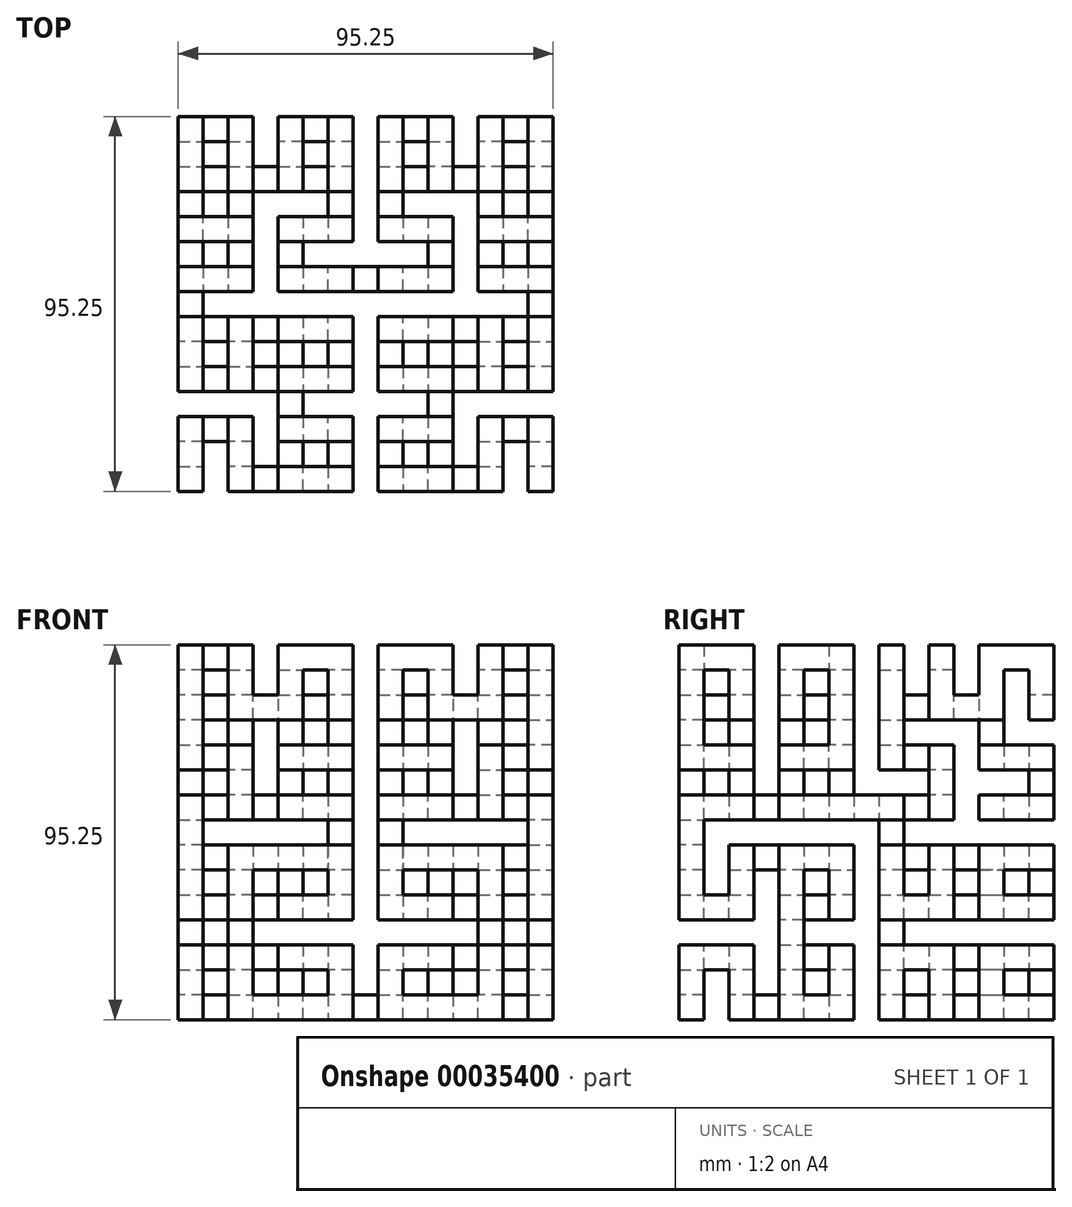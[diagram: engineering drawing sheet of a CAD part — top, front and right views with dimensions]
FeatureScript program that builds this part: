
annotation { "Feature Type Name" : "Feature", "Feature Type Description" : "" }
export const myFeature = defineFeature(function(context is Context, id is Id, definition is map)
    precondition{}
    {
        {
            var Q0;
            Q0=qCreatedBy(makeId("Top.planeOp"),FACE);
            var sketch = newSketch(context, id + "F0", { "sketchPlane" : qUnion([Q0])});
            skLineSegment(sketch, "E0.bottom", {"start": v(-71.04, -70.84) * mm, "end": v(-64.7, -70.84) * mm});
            skLineSegment(sketch, "E0.top", {"start": v(-71.04, -64.49) * mm, "end": v(-64.7, -64.49) * mm});
            skLineSegment(sketch, "E0.left", {"start": v(-71.04, -70.84) * mm, "end": v(-71.04, -64.49) * mm});
            skLineSegment(sketch, "E0.right", {"start": v(-64.7, -70.84) * mm, "end": v(-64.7, -64.49) * mm});
            skSolve(sketch);
        }
        {
            var Q0;
            Q0=makeQuery(id+"F0.imprint","IMPRINT",FACE,{"disambiguationData":[TD([[makeQuery(id+"F0.imprint","IMPRINT",EDGE,{"derivedFrom":sQuery(id+"F0.wireOp",EDGE,"E0.bottom")}),1.0]])]});
            extrude(context, id + "F1", {"entities" : qUnion([Q0]), "depth" : 19.05 * mm});
        }
        {
            var Q0;
            Q0=makeQuery(id+"F1.opExtrude","SWEPT_FACE",FACE,{"disambiguationData":[OSD([sQuery(id+"F0.wireOp",EDGE,"E0.bottom")])]});
            var sketch = newSketch(context, id + "F2", { "sketchPlane" : qUnion([Q0])});
            skLineSegment(sketch, "E1.bottom", {"start": v(-64.7, 19.05) * mm, "end": v(-71.04, 19.05) * mm});
            skLineSegment(sketch, "E1.top", {"start": v(-64.7, 12.7) * mm, "end": v(-71.04, 12.7) * mm});
            skLineSegment(sketch, "E1.left", {"start": v(-64.7, 19.05) * mm, "end": v(-64.7, 12.7) * mm});
            skLineSegment(sketch, "E1.right", {"start": v(-71.04, 19.05) * mm, "end": v(-71.04, 12.7) * mm});
            skSolve(sketch);
        }
        {
            var Q0;
            Q0=makeQuery(id+"F2.imprint","IMPRINT",FACE,{"disambiguationData":[TD([[makeQuery(id+"F2.imprint","IMPRINT",EDGE,{"derivedFrom":sQuery(id+"F2.wireOp",EDGE,"E1.bottom")}),-1.0]])]});
            extrude(context, id + "F3", {"entities" : qUnion([Q0]), "operationType" : NewBodyOperationType.ADD, "oppositeDirection" : true, "depth" : 19.05 * mm});
        }
        {
            var Q0;
            Q0=makeQuery(id+"F3.boolean.opBoolean","MERGE",FACE,{"derivedFrom":[makeQuery(id+"F1.opExtrude","CAP_FACE",FACE,{"disambiguationData":[OSD([sQuery(id+"F0.wireOp",EDGE,"E0.bottom"),sQuery(id+"F0.wireOp",EDGE,"E0.top"),sQuery(id+"F0.wireOp",EDGE,"E0.left"),sQuery(id+"F0.wireOp",EDGE,"E0.right")])],"isStart":false}),makeQuery(id+"F3.opExtrude","SWEPT_FACE",FACE,{"disambiguationData":[OSD([sQuery(id+"F2.wireOp",EDGE,"E1.bottom")])]})]});
            var sketch = newSketch(context, id + "F4", { "sketchPlane" : qUnion([Q0])});
            skLineSegment(sketch, "E2.bottom", {"start": v(-64.7, -51.79) * mm, "end": v(-71.04, -51.79) * mm});
            skLineSegment(sketch, "E2.top", {"start": v(-64.7, -58.14) * mm, "end": v(-71.04, -58.14) * mm});
            skLineSegment(sketch, "E2.left", {"start": v(-64.7, -51.79) * mm, "end": v(-64.7, -58.14) * mm});
            skLineSegment(sketch, "E2.right", {"start": v(-71.04, -51.79) * mm, "end": v(-71.04, -58.14) * mm});
            skSolve(sketch);
        }
        {
            var Q0;
            Q0=makeQuery(id+"F4.imprint","IMPRINT",FACE,{"disambiguationData":[TD([[makeQuery(id+"F4.imprint","IMPRINT",EDGE,{"derivedFrom":sQuery(id+"F4.wireOp",EDGE,"E2.bottom")}),-1.0]])]});
            extrude(context, id + "F5", {"entities" : qUnion([Q0]), "operationType" : NewBodyOperationType.ADD, "oppositeDirection" : true, "depth" : 19.05 * mm});
        }
        {
            var Q0;
            Q0=makeQuery(id+"F5.boolean.opBoolean","MERGE",FACE,{"derivedFrom":[makeQuery(id+"F3.boolean.opBoolean","MERGE",FACE,{"derivedFrom":[makeQuery(id+"F1.opExtrude","SWEPT_FACE",FACE,{"disambiguationData":[OSD([sQuery(id+"F0.wireOp",EDGE,"E0.left")])]}),makeQuery(id+"F3.opExtrude","SWEPT_FACE",FACE,{"disambiguationData":[OSD([sQuery(id+"F2.wireOp",EDGE,"E1.right")])]})]}),makeQuery(id+"F5.opExtrude","SWEPT_FACE",FACE,{"disambiguationData":[OSD([sQuery(id+"F4.wireOp",EDGE,"E2.right")])]})]});
            var sketch = newSketch(context, id + "F6", { "sketchPlane" : qUnion([Q0])});
            skLineSegment(sketch, "E3.bottom", {"start": v(51.79, 0) * mm, "end": v(58.14, 0) * mm});
            skLineSegment(sketch, "E3.top", {"start": v(51.79, 6.35) * mm, "end": v(58.14, 6.35) * mm});
            skLineSegment(sketch, "E3.left", {"start": v(51.79, 0) * mm, "end": v(51.79, 6.35) * mm});
            skLineSegment(sketch, "E3.right", {"start": v(58.14, 0) * mm, "end": v(58.14, 6.35) * mm});
            skSolve(sketch);
        }
        {
            var Q0;
            Q0=makeQuery(id+"F6.imprint","IMPRINT",FACE,{"disambiguationData":[TD([[makeQuery(id+"F6.imprint","IMPRINT",EDGE,{"derivedFrom":sQuery(id+"F6.wireOp",EDGE,"E3.bottom")}),-1.0]])]});
            extrude(context, id + "F7", {"entities" : qUnion([Q0]), "operationType" : NewBodyOperationType.ADD, "oppositeDirection" : true, "depth" : 19.05 * mm});
        }
        {
            var Q0;
            Q0=makeQuery(id+"F7.boolean.opBoolean","MERGE",FACE,{"derivedFrom":[makeQuery(id+"F5.opExtrude","CAP_FACE",FACE,{"disambiguationData":[OSD([sQuery(id+"F4.wireOp",EDGE,"E2.bottom"),sQuery(id+"F4.wireOp",EDGE,"E2.top"),sQuery(id+"F4.wireOp",EDGE,"E2.left"),sQuery(id+"F4.wireOp",EDGE,"E2.right")])],"isStart":false}),makeQuery(id+"F7.opExtrude","SWEPT_FACE",FACE,{"disambiguationData":[OSD([sQuery(id+"F6.wireOp",EDGE,"E3.bottom")])]})]});
            var sketch = newSketch(context, id + "F8", { "sketchPlane" : qUnion([Q0])});
            skLineSegment(sketch, "E4.bottom", {"start": v(-52, 58.14) * mm, "end": v(-58.34, 58.14) * mm});
            skLineSegment(sketch, "E4.top", {"start": v(-52, 51.79) * mm, "end": v(-58.34, 51.79) * mm});
            skLineSegment(sketch, "E4.left", {"start": v(-52, 58.14) * mm, "end": v(-52, 51.79) * mm});
            skLineSegment(sketch, "E4.right", {"start": v(-58.34, 58.14) * mm, "end": v(-58.34, 51.79) * mm});
            skSolve(sketch);
        }
        {
            var Q0;
            Q0=makeQuery(id+"F8.imprint","IMPRINT",FACE,{"disambiguationData":[TD([[makeQuery(id+"F8.imprint","IMPRINT",EDGE,{"derivedFrom":sQuery(id+"F8.wireOp",EDGE,"E4.bottom")}),1.0]])]});
            extrude(context, id + "F9", {"entities" : qUnion([Q0]), "operationType" : NewBodyOperationType.ADD, "oppositeDirection" : true, "depth" : 19.05 * mm});
        }
        {
            var Q0;
            Q0=makeQuery(id+"F9.boolean.opBoolean","MERGE",FACE,{"derivedFrom":[makeQuery(id+"F7.boolean.opBoolean","MERGE",FACE,{"derivedFrom":[makeQuery(id+"F5.boolean.opBoolean","MERGE",FACE,{"derivedFrom":[makeQuery(id+"F3.opExtrude","CAP_FACE",FACE,{"disambiguationData":[OSD([sQuery(id+"F2.wireOp",EDGE,"E1.bottom"),sQuery(id+"F2.wireOp",EDGE,"E1.top"),sQuery(id+"F2.wireOp",EDGE,"E1.left"),sQuery(id+"F2.wireOp",EDGE,"E1.right")])],"isStart":false}),makeQuery(id+"F5.opExtrude","SWEPT_FACE",FACE,{"disambiguationData":[OSD([sQuery(id+"F4.wireOp",EDGE,"E2.bottom")])]})]}),makeQuery(id+"F7.opExtrude","SWEPT_FACE",FACE,{"disambiguationData":[OSD([sQuery(id+"F6.wireOp",EDGE,"E3.left")])]})]}),makeQuery(id+"F9.opExtrude","SWEPT_FACE",FACE,{"disambiguationData":[OSD([sQuery(id+"F8.wireOp",EDGE,"E4.top")])]})]});
            var sketch = newSketch(context, id + "F10", { "sketchPlane" : qUnion([Q0])});
            skLineSegment(sketch, "E5.bottom", {"start": v(52, 19.05) * mm, "end": v(58.34, 19.05) * mm});
            skLineSegment(sketch, "E5.top", {"start": v(52, 12.7) * mm, "end": v(58.34, 12.7) * mm});
            skLineSegment(sketch, "E5.left", {"start": v(52, 19.05) * mm, "end": v(52, 12.7) * mm});
            skLineSegment(sketch, "E5.right", {"start": v(58.34, 19.05) * mm, "end": v(58.34, 12.7) * mm});
            skSolve(sketch);
        }
        {
            var Q0;
            Q0=makeQuery(id+"F10.imprint","IMPRINT",FACE,{"disambiguationData":[TD([[makeQuery(id+"F10.imprint","IMPRINT",EDGE,{"derivedFrom":sQuery(id+"F10.wireOp",EDGE,"E5.bottom")}),1.0]])]});
            extrude(context, id + "F11", {"entities" : qUnion([Q0]), "operationType" : NewBodyOperationType.ADD, "oppositeDirection" : true, "depth" : 19.05 * mm});
        }
        {
            var Q0;
            Q0=makeQuery(id+"F11.boolean.opBoolean","MERGE",FACE,{"derivedFrom":[makeQuery(id+"F9.opExtrude","CAP_FACE",FACE,{"disambiguationData":[OSD([sQuery(id+"F8.wireOp",EDGE,"E4.bottom"),sQuery(id+"F8.wireOp",EDGE,"E4.top"),sQuery(id+"F8.wireOp",EDGE,"E4.left"),sQuery(id+"F8.wireOp",EDGE,"E4.right")])],"isStart":false}),makeQuery(id+"F11.opExtrude","SWEPT_FACE",FACE,{"disambiguationData":[OSD([sQuery(id+"F10.wireOp",EDGE,"E5.bottom")])]})]});
            var sketch = newSketch(context, id + "F12", { "sketchPlane" : qUnion([Q0])});
            skLineSegment(sketch, "E6.bottom", {"start": v(-52, -70.84) * mm, "end": v(-58.34, -70.84) * mm});
            skLineSegment(sketch, "E6.top", {"start": v(-52, -64.49) * mm, "end": v(-58.34, -64.49) * mm});
            skLineSegment(sketch, "E6.left", {"start": v(-52, -70.84) * mm, "end": v(-52, -64.49) * mm});
            skLineSegment(sketch, "E6.right", {"start": v(-58.34, -70.84) * mm, "end": v(-58.34, -64.49) * mm});
            skSolve(sketch);
        }
        {
            var Q0;
            Q0=makeQuery(id+"F12.imprint","IMPRINT",FACE,{"disambiguationData":[TD([[makeQuery(id+"F12.imprint","IMPRINT",EDGE,{"derivedFrom":sQuery(id+"F12.wireOp",EDGE,"E6.bottom")}),1.0]])]});
            extrude(context, id + "F13", {"entities" : qUnion([Q0]), "operationType" : NewBodyOperationType.ADD, "oppositeDirection" : true, "depth" : 19.05 * mm});
        }
        {
            var Q0;
            Q0=makeQuery(id+"F13.boolean.opBoolean","MERGE",FACE,{"derivedFrom":[makeQuery(id+"F11.boolean.opBoolean","MERGE",FACE,{"derivedFrom":[makeQuery(id+"F9.opExtrude","SWEPT_FACE",FACE,{"disambiguationData":[OSD([sQuery(id+"F8.wireOp",EDGE,"E4.right")])]}),makeQuery(id+"F11.opExtrude","SWEPT_FACE",FACE,{"disambiguationData":[OSD([sQuery(id+"F10.wireOp",EDGE,"E5.right")])]})]}),makeQuery(id+"F13.opExtrude","SWEPT_FACE",FACE,{"disambiguationData":[OSD([sQuery(id+"F12.wireOp",EDGE,"E6.right")])]})]});
            var sketch = newSketch(context, id + "F14", { "sketchPlane" : qUnion([Q0])});
            skLineSegment(sketch, "E7.bottom", {"start": v(70.84, 0) * mm, "end": v(64.49, 0) * mm});
            skLineSegment(sketch, "E7.top", {"start": v(70.84, 6.35) * mm, "end": v(64.49, 6.35) * mm});
            skLineSegment(sketch, "E7.left", {"start": v(70.84, 0) * mm, "end": v(70.84, 6.35) * mm});
            skLineSegment(sketch, "E7.right", {"start": v(64.49, 0) * mm, "end": v(64.49, 6.35) * mm});
            skSolve(sketch);
        }
        {
            var Q0;
            Q0=makeQuery(id+"F14.imprint","IMPRINT",FACE,{"disambiguationData":[TD([[makeQuery(id+"F14.imprint","IMPRINT",EDGE,{"derivedFrom":sQuery(id+"F14.wireOp",EDGE,"E7.bottom")}),-1.0]])]});
            extrude(context, id + "F15", {"entities" : qUnion([Q0]), "operationType" : NewBodyOperationType.ADD, "oppositeDirection" : true, "depth" : 31.75 * mm});
        }
        {
            var Q0;
            Q0=makeQuery(id+"F15.boolean.opBoolean","MERGE",FACE,{"derivedFrom":[makeQuery(id+"F13.opExtrude","CAP_FACE",FACE,{"disambiguationData":[OSD([sQuery(id+"F12.wireOp",EDGE,"E6.bottom"),sQuery(id+"F12.wireOp",EDGE,"E6.top"),sQuery(id+"F12.wireOp",EDGE,"E6.left"),sQuery(id+"F12.wireOp",EDGE,"E6.right")])],"isStart":false}),makeQuery(id+"F15.opExtrude","SWEPT_FACE",FACE,{"disambiguationData":[OSD([sQuery(id+"F14.wireOp",EDGE,"E7.bottom")])]})]});
            var sketch = newSketch(context, id + "F16", { "sketchPlane" : qUnion([Q0])});
            skLineSegment(sketch, "E8.bottom", {"start": v(-26.6, 70.84) * mm, "end": v(-32.94, 70.84) * mm});
            skLineSegment(sketch, "E8.top", {"start": v(-26.6, 64.49) * mm, "end": v(-32.94, 64.49) * mm});
            skLineSegment(sketch, "E8.left", {"start": v(-26.6, 70.84) * mm, "end": v(-26.6, 64.49) * mm});
            skLineSegment(sketch, "E8.right", {"start": v(-32.94, 70.84) * mm, "end": v(-32.94, 64.49) * mm});
            skSolve(sketch);
        }
        {
            var Q0;
            Q0=makeQuery(id+"F16.imprint","IMPRINT",FACE,{"disambiguationData":[TD([[makeQuery(id+"F16.imprint","IMPRINT",EDGE,{"derivedFrom":sQuery(id+"F16.wireOp",EDGE,"E8.bottom")}),-1.0]])]});
            extrude(context, id + "F17", {"entities" : qUnion([Q0]), "operationType" : NewBodyOperationType.ADD, "oppositeDirection" : true, "depth" : 19.05 * mm});
        }
        {
            var Q0;
            Q0=makeQuery(id+"F17.boolean.opBoolean","MERGE",FACE,{"derivedFrom":[makeQuery(id+"F15.opExtrude","CAP_FACE",FACE,{"disambiguationData":[OSD([sQuery(id+"F14.wireOp",EDGE,"E7.bottom"),sQuery(id+"F14.wireOp",EDGE,"E7.top"),sQuery(id+"F14.wireOp",EDGE,"E7.left"),sQuery(id+"F14.wireOp",EDGE,"E7.right")])],"isStart":false}),makeQuery(id+"F17.opExtrude","SWEPT_FACE",FACE,{"disambiguationData":[OSD([sQuery(id+"F16.wireOp",EDGE,"E8.left")])]})]});
            var sketch = newSketch(context, id + "F18", { "sketchPlane" : qUnion([Q0])});
            skLineSegment(sketch, "E9.bottom", {"start": v(-64.49, 19.05) * mm, "end": v(-70.84, 19.05) * mm});
            skLineSegment(sketch, "E9.top", {"start": v(-64.49, 12.7) * mm, "end": v(-70.84, 12.7) * mm});
            skLineSegment(sketch, "E9.left", {"start": v(-64.49, 19.05) * mm, "end": v(-64.49, 12.7) * mm});
            skLineSegment(sketch, "E9.right", {"start": v(-70.84, 19.05) * mm, "end": v(-70.84, 12.7) * mm});
            skSolve(sketch);
        }
        {
            var Q0;
            Q0=makeQuery(id+"F18.imprint","IMPRINT",FACE,{"disambiguationData":[TD([[makeQuery(id+"F18.imprint","IMPRINT",EDGE,{"derivedFrom":sQuery(id+"F18.wireOp",EDGE,"E9.bottom")}),-1.0]])]});
            extrude(context, id + "F19", {"entities" : qUnion([Q0]), "operationType" : NewBodyOperationType.ADD, "oppositeDirection" : true, "depth" : 19.05 * mm});
        }
        {
            var Q0;
            Q0=makeQuery(id+"F19.boolean.opBoolean","MERGE",FACE,{"derivedFrom":[makeQuery(id+"F17.boolean.opBoolean","MERGE",FACE,{"derivedFrom":[makeQuery(id+"F15.boolean.opBoolean","MERGE",FACE,{"derivedFrom":[makeQuery(id+"F13.boolean.opBoolean","MERGE",FACE,{"derivedFrom":[makeQuery(id+"F11.opExtrude","CAP_FACE",FACE,{"disambiguationData":[OSD([sQuery(id+"F10.wireOp",EDGE,"E5.bottom"),sQuery(id+"F10.wireOp",EDGE,"E5.top"),sQuery(id+"F10.wireOp",EDGE,"E5.left"),sQuery(id+"F10.wireOp",EDGE,"E5.right")])],"isStart":false}),makeQuery(id+"F13.opExtrude","SWEPT_FACE",FACE,{"disambiguationData":[OSD([sQuery(id+"F12.wireOp",EDGE,"E6.bottom")])]})]}),makeQuery(id+"F15.opExtrude","SWEPT_FACE",FACE,{"disambiguationData":[OSD([sQuery(id+"F14.wireOp",EDGE,"E7.left")])]})]}),makeQuery(id+"F17.opExtrude","SWEPT_FACE",FACE,{"disambiguationData":[OSD([sQuery(id+"F16.wireOp",EDGE,"E8.bottom")])]})]}),makeQuery(id+"F19.opExtrude","SWEPT_FACE",FACE,{"disambiguationData":[OSD([sQuery(id+"F18.wireOp",EDGE,"E9.right")])]})]});
            var sketch = newSketch(context, id + "F20", { "sketchPlane" : qUnion([Q0])});
            skLineSegment(sketch, "E10.bottom", {"start": v(-45.64, 19.05) * mm, "end": v(-39.3, 19.05) * mm});
            skLineSegment(sketch, "E10.top", {"start": v(-45.64, 12.7) * mm, "end": v(-39.3, 12.7) * mm});
            skLineSegment(sketch, "E10.left", {"start": v(-45.64, 19.05) * mm, "end": v(-45.64, 12.7) * mm});
            skLineSegment(sketch, "E10.right", {"start": v(-39.3, 19.05) * mm, "end": v(-39.3, 12.7) * mm});
            skSolve(sketch);
        }
        {
            var Q0;
            Q0=makeQuery(id+"F20.imprint","IMPRINT",FACE,{"disambiguationData":[TD([[makeQuery(id+"F20.imprint","IMPRINT",EDGE,{"derivedFrom":sQuery(id+"F20.wireOp",EDGE,"E10.bottom")}),-1.0]])]});
            extrude(context, id + "F21", {"entities" : qUnion([Q0]), "operationType" : NewBodyOperationType.ADD, "oppositeDirection" : true, "depth" : 19.05 * mm});
        }
        {
            var Q0;
            Q0=makeQuery(id+"F21.boolean.opBoolean","MERGE",FACE,{"derivedFrom":[makeQuery(id+"F19.opExtrude","CAP_FACE",FACE,{"disambiguationData":[OSD([sQuery(id+"F18.wireOp",EDGE,"E9.bottom"),sQuery(id+"F18.wireOp",EDGE,"E9.top"),sQuery(id+"F18.wireOp",EDGE,"E9.left"),sQuery(id+"F18.wireOp",EDGE,"E9.right")])],"isStart":false}),makeQuery(id+"F21.opExtrude","SWEPT_FACE",FACE,{"disambiguationData":[OSD([sQuery(id+"F20.wireOp",EDGE,"E10.left")])]})]});
            var sketch = newSketch(context, id + "F22", { "sketchPlane" : qUnion([Q0])});
            skLineSegment(sketch, "E11.bottom", {"start": v(51.79, 19.05) * mm, "end": v(58.14, 19.05) * mm});
            skLineSegment(sketch, "E11.top", {"start": v(51.79, 12.7) * mm, "end": v(58.14, 12.7) * mm});
            skLineSegment(sketch, "E11.left", {"start": v(51.79, 19.05) * mm, "end": v(51.79, 12.7) * mm});
            skLineSegment(sketch, "E11.right", {"start": v(58.14, 19.05) * mm, "end": v(58.14, 12.7) * mm});
            skSolve(sketch);
        }
        {
            var Q0;
            Q0=makeQuery(id+"F22.imprint","IMPRINT",FACE,{"disambiguationData":[TD([[makeQuery(id+"F22.imprint","IMPRINT",EDGE,{"derivedFrom":sQuery(id+"F22.wireOp",EDGE,"E11.bottom")}),1.0]])]});
            extrude(context, id + "F23", {"entities" : qUnion([Q0]), "operationType" : NewBodyOperationType.ADD, "oppositeDirection" : true, "depth" : 19.05 * mm});
        }
        {
            var Q0;
            Q0=makeQuery(id+"F23.boolean.opBoolean","MERGE",FACE,{"derivedFrom":[makeQuery(id+"F21.boolean.opBoolean","MERGE",FACE,{"derivedFrom":[makeQuery(id+"F19.boolean.opBoolean","MERGE",FACE,{"derivedFrom":[makeQuery(id+"F17.opExtrude","CAP_FACE",FACE,{"disambiguationData":[OSD([sQuery(id+"F16.wireOp",EDGE,"E8.bottom"),sQuery(id+"F16.wireOp",EDGE,"E8.top"),sQuery(id+"F16.wireOp",EDGE,"E8.left"),sQuery(id+"F16.wireOp",EDGE,"E8.right")])],"isStart":false}),makeQuery(id+"F19.opExtrude","SWEPT_FACE",FACE,{"disambiguationData":[OSD([sQuery(id+"F18.wireOp",EDGE,"E9.bottom")])]})]}),makeQuery(id+"F21.opExtrude","SWEPT_FACE",FACE,{"disambiguationData":[OSD([sQuery(id+"F20.wireOp",EDGE,"E10.bottom")])]})]}),makeQuery(id+"F23.opExtrude","SWEPT_FACE",FACE,{"disambiguationData":[OSD([sQuery(id+"F22.wireOp",EDGE,"E11.bottom")])]})]});
            var sketch = newSketch(context, id + "F24", { "sketchPlane" : qUnion([Q0])});
            skLineSegment(sketch, "E12.bottom", {"start": v(-26.6, -51.79) * mm, "end": v(-32.94, -51.79) * mm});
            skLineSegment(sketch, "E12.top", {"start": v(-26.6, -58.14) * mm, "end": v(-32.94, -58.14) * mm});
            skLineSegment(sketch, "E12.left", {"start": v(-26.6, -51.79) * mm, "end": v(-26.6, -58.14) * mm});
            skLineSegment(sketch, "E12.right", {"start": v(-32.94, -51.79) * mm, "end": v(-32.94, -58.14) * mm});
            skSolve(sketch);
        }
        {
            var Q0;
            Q0=makeQuery(id+"F24.imprint","IMPRINT",FACE,{"disambiguationData":[TD([[makeQuery(id+"F24.imprint","IMPRINT",EDGE,{"derivedFrom":sQuery(id+"F24.wireOp",EDGE,"E12.bottom")}),-1.0]])]});
            extrude(context, id + "F25", {"entities" : qUnion([Q0]), "operationType" : NewBodyOperationType.ADD, "oppositeDirection" : true, "depth" : 19.05 * mm});
        }
        {
            var Q0;
            Q0=makeQuery(id+"F25.boolean.opBoolean","MERGE",FACE,{"derivedFrom":[makeQuery(id+"F23.opExtrude","CAP_FACE",FACE,{"disambiguationData":[OSD([sQuery(id+"F22.wireOp",EDGE,"E11.bottom"),sQuery(id+"F22.wireOp",EDGE,"E11.top"),sQuery(id+"F22.wireOp",EDGE,"E11.left"),sQuery(id+"F22.wireOp",EDGE,"E11.right")])],"isStart":false}),makeQuery(id+"F25.opExtrude","SWEPT_FACE",FACE,{"disambiguationData":[OSD([sQuery(id+"F24.wireOp",EDGE,"E12.left")])]})]});
            var sketch = newSketch(context, id + "F26", { "sketchPlane" : qUnion([Q0])});
            skLineSegment(sketch, "E13.bottom", {"start": v(-51.79, 0) * mm, "end": v(-58.14, 0) * mm});
            skLineSegment(sketch, "E13.top", {"start": v(-51.79, 6.35) * mm, "end": v(-58.14, 6.35) * mm});
            skLineSegment(sketch, "E13.left", {"start": v(-51.79, 0) * mm, "end": v(-51.79, 6.35) * mm});
            skLineSegment(sketch, "E13.right", {"start": v(-58.14, 0) * mm, "end": v(-58.14, 6.35) * mm});
            skSolve(sketch);
        }
        {
            var Q0;
            Q0=makeQuery(id+"F26.imprint","IMPRINT",FACE,{"disambiguationData":[TD([[makeQuery(id+"F26.imprint","IMPRINT",EDGE,{"derivedFrom":sQuery(id+"F26.wireOp",EDGE,"E13.bottom")}),1.0]])]});
            extrude(context, id + "F27", {"entities" : qUnion([Q0]), "operationType" : NewBodyOperationType.ADD, "oppositeDirection" : true, "depth" : 19.05 * mm});
        }
        {
            var Q0;
            Q0=makeQuery(id+"F27.boolean.opBoolean","MERGE",FACE,{"derivedFrom":[makeQuery(id+"F25.boolean.opBoolean","MERGE",FACE,{"derivedFrom":[makeQuery(id+"F23.opExtrude","SWEPT_FACE",FACE,{"disambiguationData":[OSD([sQuery(id+"F22.wireOp",EDGE,"E11.right")])]}),makeQuery(id+"F25.opExtrude","SWEPT_FACE",FACE,{"disambiguationData":[OSD([sQuery(id+"F24.wireOp",EDGE,"E12.top")])]})]}),makeQuery(id+"F27.opExtrude","SWEPT_FACE",FACE,{"disambiguationData":[OSD([sQuery(id+"F26.wireOp",EDGE,"E13.right")])]})]});
            var sketch = newSketch(context, id + "F28", { "sketchPlane" : qUnion([Q0])});
            skLineSegment(sketch, "E14.bottom", {"start": v(-45.64, 0) * mm, "end": v(-39.3, 0) * mm});
            skLineSegment(sketch, "E14.top", {"start": v(-45.64, 6.35) * mm, "end": v(-39.3, 6.35) * mm});
            skLineSegment(sketch, "E14.left", {"start": v(-45.64, 0) * mm, "end": v(-45.64, 6.35) * mm});
            skLineSegment(sketch, "E14.right", {"start": v(-39.3, 0) * mm, "end": v(-39.3, 6.35) * mm});
            skSolve(sketch);
        }
        {
            var Q0;
            Q0=makeQuery(id+"F28.imprint","IMPRINT",FACE,{"disambiguationData":[TD([[makeQuery(id+"F28.imprint","IMPRINT",EDGE,{"derivedFrom":sQuery(id+"F28.wireOp",EDGE,"E14.bottom")}),-1.0]])]});
            extrude(context, id + "F29", {"entities" : qUnion([Q0]), "operationType" : NewBodyOperationType.ADD, "oppositeDirection" : true, "depth" : 19.05 * mm});
        }
        {
            var Q0;
            Q0=makeQuery(id+"F29.boolean.opBoolean","MERGE",FACE,{"derivedFrom":[makeQuery(id+"F27.opExtrude","CAP_FACE",FACE,{"disambiguationData":[OSD([sQuery(id+"F26.wireOp",EDGE,"E13.bottom"),sQuery(id+"F26.wireOp",EDGE,"E13.top"),sQuery(id+"F26.wireOp",EDGE,"E13.left"),sQuery(id+"F26.wireOp",EDGE,"E13.right")])],"isStart":false}),makeQuery(id+"F29.opExtrude","SWEPT_FACE",FACE,{"disambiguationData":[OSD([sQuery(id+"F28.wireOp",EDGE,"E14.left")])]})]});
            var sketch = newSketch(context, id + "F30", { "sketchPlane" : qUnion([Q0])});
            skLineSegment(sketch, "E15.bottom", {"start": v(39.09, 6.35) * mm, "end": v(45.44, 6.35) * mm});
            skLineSegment(sketch, "E15.top", {"start": v(39.09, 0) * mm, "end": v(45.44, 0) * mm});
            skLineSegment(sketch, "E15.left", {"start": v(39.09, 6.35) * mm, "end": v(39.09, 0) * mm});
            skLineSegment(sketch, "E15.right", {"start": v(45.44, 6.35) * mm, "end": v(45.44, 0) * mm});
            skSolve(sketch);
        }
        {
            var Q0;
            Q0=makeQuery(id+"F30.imprint","IMPRINT",FACE,{"disambiguationData":[TD([[makeQuery(id+"F30.imprint","IMPRINT",EDGE,{"derivedFrom":sQuery(id+"F30.wireOp",EDGE,"E15.bottom")}),-1.0]])]});
            extrude(context, id + "F31", {"entities" : qUnion([Q0]), "operationType" : NewBodyOperationType.ADD, "oppositeDirection" : true, "depth" : 19.05 * mm});
        }
        {
            var Q0;
            Q0=makeQuery(id+"F31.opExtrude","SWEPT_FACE",FACE,{"disambiguationData":[OSD([sQuery(id+"F30.wireOp",EDGE,"E15.right")])]});
            var sketch = newSketch(context, id + "F32", { "sketchPlane" : qUnion([Q0])});
            skLineSegment(sketch, "E16.bottom", {"start": v(-26.6, 0) * mm, "end": v(-32.94, 0) * mm});
            skLineSegment(sketch, "E16.top", {"start": v(-26.6, 6.35) * mm, "end": v(-32.94, 6.35) * mm});
            skLineSegment(sketch, "E16.left", {"start": v(-26.6, 0) * mm, "end": v(-26.6, 6.35) * mm});
            skLineSegment(sketch, "E16.right", {"start": v(-32.94, 0) * mm, "end": v(-32.94, 6.35) * mm});
            skSolve(sketch);
        }
        {
            var Q0;
            Q0=makeQuery(id+"F32.imprint","IMPRINT",FACE,{"disambiguationData":[TD([[makeQuery(id+"F32.imprint","IMPRINT",EDGE,{"derivedFrom":sQuery(id+"F32.wireOp",EDGE,"E16.bottom")}),-1.0]])]});
            extrude(context, id + "F33", {"entities" : qUnion([Q0]), "operationType" : NewBodyOperationType.ADD, "oppositeDirection" : true, "depth" : 19.05 * mm});
        }
        {
            var Q0;
            Q0=makeQuery(id+"F33.boolean.opBoolean","MERGE",FACE,{"derivedFrom":[makeQuery(id+"F31.opExtrude","CAP_FACE",FACE,{"disambiguationData":[OSD([sQuery(id+"F30.wireOp",EDGE,"E15.bottom"),sQuery(id+"F30.wireOp",EDGE,"E15.top"),sQuery(id+"F30.wireOp",EDGE,"E15.left"),sQuery(id+"F30.wireOp",EDGE,"E15.right")])],"isStart":false}),makeQuery(id+"F33.opExtrude","SWEPT_FACE",FACE,{"disambiguationData":[OSD([sQuery(id+"F32.wireOp",EDGE,"E16.left")])]})]});
            var sketch = newSketch(context, id + "F34", { "sketchPlane" : qUnion([Q0])});
            skLineSegment(sketch, "E17.bottom", {"start": v(-26.39, 6.35) * mm, "end": v(-32.74, 6.35) * mm});
            skLineSegment(sketch, "E17.top", {"start": v(-26.39, 0) * mm, "end": v(-32.74, 0) * mm});
            skLineSegment(sketch, "E17.left", {"start": v(-26.39, 6.35) * mm, "end": v(-26.39, 0) * mm});
            skLineSegment(sketch, "E17.right", {"start": v(-32.74, 6.35) * mm, "end": v(-32.74, 0) * mm});
            skSolve(sketch);
        }
        {
            var Q0;
            Q0=makeQuery(id+"F34.imprint","IMPRINT",FACE,{"disambiguationData":[TD([[makeQuery(id+"F34.imprint","IMPRINT",EDGE,{"derivedFrom":sQuery(id+"F34.wireOp",EDGE,"E17.bottom")}),1.0]])]});
            extrude(context, id + "F35", {"entities" : qUnion([Q0]), "operationType" : NewBodyOperationType.ADD, "oppositeDirection" : true, "depth" : 19.05 * mm});
        }
        {
            var Q0;
            Q0=makeQuery(id+"F35.boolean.opBoolean","MERGE",FACE,{"derivedFrom":[makeQuery(id+"F33.boolean.opBoolean","MERGE",FACE,{"derivedFrom":[makeQuery(id+"F31.boolean.opBoolean","MERGE",FACE,{"derivedFrom":[makeQuery(id+"F29.boolean.opBoolean","MERGE",FACE,{"derivedFrom":[makeQuery(id+"F27.boolean.opBoolean","MERGE",FACE,{"derivedFrom":[makeQuery(id+"F25.opExtrude","CAP_FACE",FACE,{"disambiguationData":[OSD([sQuery(id+"F24.wireOp",EDGE,"E12.bottom"),sQuery(id+"F24.wireOp",EDGE,"E12.top"),sQuery(id+"F24.wireOp",EDGE,"E12.left"),sQuery(id+"F24.wireOp",EDGE,"E12.right")])],"isStart":false}),makeQuery(id+"F27.opExtrude","SWEPT_FACE",FACE,{"disambiguationData":[OSD([sQuery(id+"F26.wireOp",EDGE,"E13.bottom")])]})]}),makeQuery(id+"F29.opExtrude","SWEPT_FACE",FACE,{"disambiguationData":[OSD([sQuery(id+"F28.wireOp",EDGE,"E14.bottom")])]})]}),makeQuery(id+"F31.opExtrude","SWEPT_FACE",FACE,{"disambiguationData":[OSD([sQuery(id+"F30.wireOp",EDGE,"E15.top")])]})]}),makeQuery(id+"F33.opExtrude","SWEPT_FACE",FACE,{"disambiguationData":[OSD([sQuery(id+"F32.wireOp",EDGE,"E16.bottom")])]})]}),makeQuery(id+"F35.opExtrude","SWEPT_FACE",FACE,{"disambiguationData":[OSD([sQuery(id+"F34.wireOp",EDGE,"E17.top")])]})]});
            var sketch = newSketch(context, id + "F36", { "sketchPlane" : qUnion([Q0])});
            skLineSegment(sketch, "E18.bottom", {"start": v(-45.64, 26.39) * mm, "end": v(-39.3, 26.39) * mm});
            skLineSegment(sketch, "E18.top", {"start": v(-45.64, 32.74) * mm, "end": v(-39.3, 32.74) * mm});
            skLineSegment(sketch, "E18.left", {"start": v(-45.64, 26.39) * mm, "end": v(-45.64, 32.74) * mm});
            skLineSegment(sketch, "E18.right", {"start": v(-39.3, 26.39) * mm, "end": v(-39.3, 32.74) * mm});
            skSolve(sketch);
        }
        {
            var Q0;
            Q0=makeQuery(id+"F36.imprint","IMPRINT",FACE,{"disambiguationData":[TD([[makeQuery(id+"F36.imprint","IMPRINT",EDGE,{"derivedFrom":sQuery(id+"F36.wireOp",EDGE,"E18.bottom")}),-1.0]])]});
            extrude(context, id + "F37", {"entities" : qUnion([Q0]), "operationType" : NewBodyOperationType.ADD, "oppositeDirection" : true, "depth" : 19.05 * mm});
        }
        {
            var Q0;
            Q0=makeQuery(id+"F37.boolean.opBoolean","MERGE",FACE,{"derivedFrom":[makeQuery(id+"F35.opExtrude","CAP_FACE",FACE,{"disambiguationData":[OSD([sQuery(id+"F34.wireOp",EDGE,"E17.bottom"),sQuery(id+"F34.wireOp",EDGE,"E17.top"),sQuery(id+"F34.wireOp",EDGE,"E17.left"),sQuery(id+"F34.wireOp",EDGE,"E17.right")])],"isStart":false}),makeQuery(id+"F37.opExtrude","SWEPT_FACE",FACE,{"disambiguationData":[OSD([sQuery(id+"F36.wireOp",EDGE,"E18.left")])]})]});
            var sketch = newSketch(context, id + "F38", { "sketchPlane" : qUnion([Q0])});
            skLineSegment(sketch, "E19.bottom", {"start": v(32.74, 19.05) * mm, "end": v(26.39, 19.05) * mm});
            skLineSegment(sketch, "E19.top", {"start": v(32.74, 12.7) * mm, "end": v(26.39, 12.7) * mm});
            skLineSegment(sketch, "E19.left", {"start": v(32.74, 19.05) * mm, "end": v(32.74, 12.7) * mm});
            skLineSegment(sketch, "E19.right", {"start": v(26.39, 19.05) * mm, "end": v(26.39, 12.7) * mm});
            skSolve(sketch);
        }
        {
            var Q0;
            Q0=makeQuery(id+"F38.imprint","IMPRINT",FACE,{"disambiguationData":[TD([[makeQuery(id+"F38.imprint","IMPRINT",EDGE,{"derivedFrom":sQuery(id+"F38.wireOp",EDGE,"E19.bottom")}),1.0]])]});
            extrude(context, id + "F39", {"entities" : qUnion([Q0]), "operationType" : NewBodyOperationType.ADD, "oppositeDirection" : true, "depth" : 19.05 * mm});
        }
        {
            var Q0;
            Q0=makeQuery(id+"F39.boolean.opBoolean","MERGE",FACE,{"derivedFrom":[makeQuery(id+"F37.boolean.opBoolean","MERGE",FACE,{"derivedFrom":[makeQuery(id+"F35.boolean.opBoolean","MERGE",FACE,{"derivedFrom":[makeQuery(id+"F33.opExtrude","CAP_FACE",FACE,{"disambiguationData":[OSD([sQuery(id+"F32.wireOp",EDGE,"E16.bottom"),sQuery(id+"F32.wireOp",EDGE,"E16.top"),sQuery(id+"F32.wireOp",EDGE,"E16.left"),sQuery(id+"F32.wireOp",EDGE,"E16.right")])],"isStart":false}),makeQuery(id+"F35.opExtrude","SWEPT_FACE",FACE,{"disambiguationData":[OSD([sQuery(id+"F34.wireOp",EDGE,"E17.left")])]})]}),makeQuery(id+"F37.opExtrude","SWEPT_FACE",FACE,{"disambiguationData":[OSD([sQuery(id+"F36.wireOp",EDGE,"E18.bottom")])]})]}),makeQuery(id+"F39.opExtrude","SWEPT_FACE",FACE,{"disambiguationData":[OSD([sQuery(id+"F38.wireOp",EDGE,"E19.right")])]})]});
            var sketch = newSketch(context, id + "F40", { "sketchPlane" : qUnion([Q0])});
            skLineSegment(sketch, "E20.bottom", {"start": v(26.6, 19.05) * mm, "end": v(32.94, 19.05) * mm});
            skLineSegment(sketch, "E20.top", {"start": v(26.6, 12.7) * mm, "end": v(32.94, 12.7) * mm});
            skLineSegment(sketch, "E20.left", {"start": v(26.6, 19.05) * mm, "end": v(26.6, 12.7) * mm});
            skLineSegment(sketch, "E20.right", {"start": v(32.94, 19.05) * mm, "end": v(32.94, 12.7) * mm});
            skSolve(sketch);
        }
        {
            var Q0;
            Q0=makeQuery(id+"F40.imprint","IMPRINT",FACE,{"disambiguationData":[TD([[makeQuery(id+"F40.imprint","IMPRINT",EDGE,{"derivedFrom":sQuery(id+"F40.wireOp",EDGE,"E20.bottom")}),-1.0]])]});
            extrude(context, id + "F41", {"entities" : qUnion([Q0]), "operationType" : NewBodyOperationType.ADD, "oppositeDirection" : true, "depth" : 19.05 * mm});
        }
        {
            var Q0;
            Q0=makeQuery(id+"F41.boolean.opBoolean","MERGE",FACE,{"derivedFrom":[makeQuery(id+"F39.opExtrude","CAP_FACE",FACE,{"disambiguationData":[OSD([sQuery(id+"F38.wireOp",EDGE,"E19.bottom"),sQuery(id+"F38.wireOp",EDGE,"E19.top"),sQuery(id+"F38.wireOp",EDGE,"E19.left"),sQuery(id+"F38.wireOp",EDGE,"E19.right")])],"isStart":false}),makeQuery(id+"F41.opExtrude","SWEPT_FACE",FACE,{"disambiguationData":[OSD([sQuery(id+"F40.wireOp",EDGE,"E20.left")])]})]});
            var sketch = newSketch(context, id + "F42", { "sketchPlane" : qUnion([Q0])});
            skLineSegment(sketch, "E21.bottom", {"start": v(-45.44, 19.05) * mm, "end": v(-39.09, 19.05) * mm});
            skLineSegment(sketch, "E21.top", {"start": v(-45.44, 12.7) * mm, "end": v(-39.09, 12.7) * mm});
            skLineSegment(sketch, "E21.left", {"start": v(-45.44, 19.05) * mm, "end": v(-45.44, 12.7) * mm});
            skLineSegment(sketch, "E21.right", {"start": v(-39.09, 19.05) * mm, "end": v(-39.09, 12.7) * mm});
            skSolve(sketch);
        }
        {
            var Q0;
            Q0=makeQuery(id+"F42.imprint","IMPRINT",FACE,{"disambiguationData":[TD([[makeQuery(id+"F42.imprint","IMPRINT",EDGE,{"derivedFrom":sQuery(id+"F42.wireOp",EDGE,"E21.bottom")}),-1.0]])]});
            extrude(context, id + "F43", {"entities" : qUnion([Q0]), "operationType" : NewBodyOperationType.ADD, "oppositeDirection" : true, "depth" : 31.75 * mm});
        }
        {
            var Q0;
            Q0=makeQuery(id+"F43.boolean.opBoolean","MERGE",FACE,{"derivedFrom":[makeQuery(id+"F41.boolean.opBoolean","MERGE",FACE,{"derivedFrom":[makeQuery(id+"F39.boolean.opBoolean","MERGE",FACE,{"derivedFrom":[makeQuery(id+"F37.opExtrude","CAP_FACE",FACE,{"disambiguationData":[OSD([sQuery(id+"F36.wireOp",EDGE,"E18.bottom"),sQuery(id+"F36.wireOp",EDGE,"E18.top"),sQuery(id+"F36.wireOp",EDGE,"E18.left"),sQuery(id+"F36.wireOp",EDGE,"E18.right")])],"isStart":false}),makeQuery(id+"F39.opExtrude","SWEPT_FACE",FACE,{"disambiguationData":[OSD([sQuery(id+"F38.wireOp",EDGE,"E19.bottom")])]})]}),makeQuery(id+"F41.opExtrude","SWEPT_FACE",FACE,{"disambiguationData":[OSD([sQuery(id+"F40.wireOp",EDGE,"E20.bottom")])]})]}),makeQuery(id+"F43.opExtrude","SWEPT_FACE",FACE,{"disambiguationData":[OSD([sQuery(id+"F42.wireOp",EDGE,"E21.bottom")])]})]});
            var sketch = newSketch(context, id + "F44", { "sketchPlane" : qUnion([Q0])});
            skLineSegment(sketch, "E22.bottom", {"start": v(-58.34, -39.09) * mm, "end": v(-52, -39.09) * mm});
            skLineSegment(sketch, "E22.top", {"start": v(-58.34, -45.44) * mm, "end": v(-52, -45.44) * mm});
            skLineSegment(sketch, "E22.left", {"start": v(-58.34, -39.09) * mm, "end": v(-58.34, -45.44) * mm});
            skLineSegment(sketch, "E22.right", {"start": v(-52, -39.09) * mm, "end": v(-52, -45.44) * mm});
            skSolve(sketch);
        }
        {
            var Q0;
            Q0=makeQuery(id+"F44.imprint","IMPRINT",FACE,{"disambiguationData":[TD([[makeQuery(id+"F44.imprint","IMPRINT",EDGE,{"derivedFrom":sQuery(id+"F44.wireOp",EDGE,"E22.bottom")}),-1.0]])]});
            extrude(context, id + "F45", {"entities" : qUnion([Q0]), "operationType" : NewBodyOperationType.ADD, "oppositeDirection" : true, "depth" : 19.05 * mm});
        }
        {
            var Q0;
            Q0=makeQuery(id+"F45.boolean.opBoolean","MERGE",FACE,{"derivedFrom":[makeQuery(id+"F43.boolean.opBoolean","MERGE",FACE,{"derivedFrom":[makeQuery(id+"F41.opExtrude","CAP_FACE",FACE,{"disambiguationData":[OSD([sQuery(id+"F40.wireOp",EDGE,"E20.bottom"),sQuery(id+"F40.wireOp",EDGE,"E20.top"),sQuery(id+"F40.wireOp",EDGE,"E20.left"),sQuery(id+"F40.wireOp",EDGE,"E20.right")])],"isStart":false}),makeQuery(id+"F43.opExtrude","SWEPT_FACE",FACE,{"disambiguationData":[OSD([sQuery(id+"F42.wireOp",EDGE,"E21.left")])]})]}),makeQuery(id+"F45.opExtrude","SWEPT_FACE",FACE,{"disambiguationData":[OSD([sQuery(id+"F44.wireOp",EDGE,"E22.top")])]})]});
            var sketch = newSketch(context, id + "F46", { "sketchPlane" : qUnion([Q0])});
            skLineSegment(sketch, "E23.bottom", {"start": v(-58.34, 0) * mm, "end": v(-52, 0) * mm});
            skLineSegment(sketch, "E23.top", {"start": v(-58.34, 6.35) * mm, "end": v(-52, 6.35) * mm});
            skLineSegment(sketch, "E23.left", {"start": v(-58.34, 0) * mm, "end": v(-58.34, 6.35) * mm});
            skLineSegment(sketch, "E23.right", {"start": v(-52, 0) * mm, "end": v(-52, 6.35) * mm});
            skSolve(sketch);
        }
        {
            var Q0;
            Q0=makeQuery(id+"F46.imprint","IMPRINT",FACE,{"disambiguationData":[TD([[makeQuery(id+"F46.imprint","IMPRINT",EDGE,{"derivedFrom":sQuery(id+"F46.wireOp",EDGE,"E23.bottom")}),-1.0]])]});
            extrude(context, id + "F47", {"entities" : qUnion([Q0]), "operationType" : NewBodyOperationType.ADD, "oppositeDirection" : true, "depth" : 19.05 * mm});
        }
        {
            var Q0;
            Q0=makeQuery(id+"F47.boolean.opBoolean","MERGE",FACE,{"derivedFrom":[makeQuery(id+"F45.opExtrude","CAP_FACE",FACE,{"disambiguationData":[OSD([sQuery(id+"F44.wireOp",EDGE,"E22.bottom"),sQuery(id+"F44.wireOp",EDGE,"E22.top"),sQuery(id+"F44.wireOp",EDGE,"E22.left"),sQuery(id+"F44.wireOp",EDGE,"E22.right")])],"isStart":false}),makeQuery(id+"F47.opExtrude","SWEPT_FACE",FACE,{"disambiguationData":[OSD([sQuery(id+"F46.wireOp",EDGE,"E23.bottom")])]})]});
            var sketch = newSketch(context, id + "F48", { "sketchPlane" : qUnion([Q0])});
            skLineSegment(sketch, "E24.bottom", {"start": v(-58.34, 26.39) * mm, "end": v(-52, 26.39) * mm});
            skLineSegment(sketch, "E24.top", {"start": v(-58.34, 32.74) * mm, "end": v(-52, 32.74) * mm});
            skLineSegment(sketch, "E24.left", {"start": v(-58.34, 26.39) * mm, "end": v(-58.34, 32.74) * mm});
            skLineSegment(sketch, "E24.right", {"start": v(-52, 26.39) * mm, "end": v(-52, 32.74) * mm});
            skSolve(sketch);
        }
        {
            var Q0;
            Q0=makeQuery(id+"F48.imprint","IMPRINT",FACE,{"disambiguationData":[TD([[makeQuery(id+"F48.imprint","IMPRINT",EDGE,{"derivedFrom":sQuery(id+"F48.wireOp",EDGE,"E24.bottom")}),-1.0]])]});
            extrude(context, id + "F49", {"entities" : qUnion([Q0]), "operationType" : NewBodyOperationType.ADD, "oppositeDirection" : true, "depth" : 19.05 * mm});
        }
        {
            var Q0;
            Q0=makeQuery(id+"F49.boolean.opBoolean","MERGE",FACE,{"derivedFrom":[makeQuery(id+"F47.boolean.opBoolean","MERGE",FACE,{"derivedFrom":[makeQuery(id+"F45.opExtrude","SWEPT_FACE",FACE,{"disambiguationData":[OSD([sQuery(id+"F44.wireOp",EDGE,"E22.right")])]}),makeQuery(id+"F47.opExtrude","SWEPT_FACE",FACE,{"disambiguationData":[OSD([sQuery(id+"F46.wireOp",EDGE,"E23.right")])]})]}),makeQuery(id+"F49.opExtrude","SWEPT_FACE",FACE,{"disambiguationData":[OSD([sQuery(id+"F48.wireOp",EDGE,"E24.right")])]})]});
            var sketch = newSketch(context, id + "F50", { "sketchPlane" : qUnion([Q0])});
            skLineSegment(sketch, "E25.bottom", {"start": v(-26.39, 19.05) * mm, "end": v(-32.74, 19.05) * mm});
            skLineSegment(sketch, "E25.top", {"start": v(-26.39, 12.7) * mm, "end": v(-32.74, 12.7) * mm});
            skLineSegment(sketch, "E25.left", {"start": v(-26.39, 19.05) * mm, "end": v(-26.39, 12.7) * mm});
            skLineSegment(sketch, "E25.right", {"start": v(-32.74, 19.05) * mm, "end": v(-32.74, 12.7) * mm});
            skSolve(sketch);
        }
        {
            var Q0;
            Q0=makeQuery(id+"F50.imprint","IMPRINT",FACE,{"disambiguationData":[TD([[makeQuery(id+"F50.imprint","IMPRINT",EDGE,{"derivedFrom":sQuery(id+"F50.wireOp",EDGE,"E25.bottom")}),1.0]])]});
            extrude(context, id + "F51", {"entities" : qUnion([Q0]), "operationType" : NewBodyOperationType.ADD, "oppositeDirection" : true, "depth" : 19.05 * mm});
        }
        {
            var Q0;
            Q0=makeQuery(id+"F51.boolean.opBoolean","MERGE",FACE,{"derivedFrom":[makeQuery(id+"F49.opExtrude","CAP_FACE",FACE,{"disambiguationData":[OSD([sQuery(id+"F48.wireOp",EDGE,"E24.bottom"),sQuery(id+"F48.wireOp",EDGE,"E24.top"),sQuery(id+"F48.wireOp",EDGE,"E24.left"),sQuery(id+"F48.wireOp",EDGE,"E24.right")])],"isStart":false}),makeQuery(id+"F51.opExtrude","SWEPT_FACE",FACE,{"disambiguationData":[OSD([sQuery(id+"F50.wireOp",EDGE,"E25.bottom")])]})]});
            var sketch = newSketch(context, id + "F52", { "sketchPlane" : qUnion([Q0])});
            skLineSegment(sketch, "E26.bottom", {"start": v(-71.04, -26.39) * mm, "end": v(-64.7, -26.39) * mm});
            skLineSegment(sketch, "E26.top", {"start": v(-71.04, -32.74) * mm, "end": v(-64.7, -32.74) * mm});
            skLineSegment(sketch, "E26.left", {"start": v(-71.04, -26.39) * mm, "end": v(-71.04, -32.74) * mm});
            skLineSegment(sketch, "E26.right", {"start": v(-64.7, -26.39) * mm, "end": v(-64.7, -32.74) * mm});
            skSolve(sketch);
        }
        {
            var Q0;
            Q0=makeQuery(id+"F52.imprint","IMPRINT",FACE,{"disambiguationData":[TD([[makeQuery(id+"F52.imprint","IMPRINT",EDGE,{"derivedFrom":sQuery(id+"F52.wireOp",EDGE,"E26.bottom")}),1.0]])]});
            extrude(context, id + "F53", {"entities" : qUnion([Q0]), "operationType" : NewBodyOperationType.ADD, "oppositeDirection" : true, "depth" : 19.05 * mm});
        }
        {
            var Q0;
            Q0=makeQuery(id+"F53.boolean.opBoolean","MERGE",FACE,{"derivedFrom":[makeQuery(id+"F51.boolean.opBoolean","MERGE",FACE,{"derivedFrom":[makeQuery(id+"F49.boolean.opBoolean","MERGE",FACE,{"derivedFrom":[makeQuery(id+"F47.opExtrude","CAP_FACE",FACE,{"disambiguationData":[OSD([sQuery(id+"F46.wireOp",EDGE,"E23.bottom"),sQuery(id+"F46.wireOp",EDGE,"E23.top"),sQuery(id+"F46.wireOp",EDGE,"E23.left"),sQuery(id+"F46.wireOp",EDGE,"E23.right")])],"isStart":false}),makeQuery(id+"F49.opExtrude","SWEPT_FACE",FACE,{"disambiguationData":[OSD([sQuery(id+"F48.wireOp",EDGE,"E24.bottom")])]})]}),makeQuery(id+"F51.opExtrude","SWEPT_FACE",FACE,{"disambiguationData":[OSD([sQuery(id+"F50.wireOp",EDGE,"E25.left")])]})]}),makeQuery(id+"F53.opExtrude","SWEPT_FACE",FACE,{"disambiguationData":[OSD([sQuery(id+"F52.wireOp",EDGE,"E26.bottom")])]})]});
            var sketch = newSketch(context, id + "F54", { "sketchPlane" : qUnion([Q0])});
            skLineSegment(sketch, "E27.bottom", {"start": v(71.04, 0) * mm, "end": v(64.7, 0) * mm});
            skLineSegment(sketch, "E27.top", {"start": v(71.04, 6.35) * mm, "end": v(64.7, 6.35) * mm});
            skLineSegment(sketch, "E27.left", {"start": v(71.04, 0) * mm, "end": v(71.04, 6.35) * mm});
            skLineSegment(sketch, "E27.right", {"start": v(64.7, 0) * mm, "end": v(64.7, 6.35) * mm});
            skSolve(sketch);
        }
        {
            var Q0;
            Q0=makeQuery(id+"F54.imprint","IMPRINT",FACE,{"disambiguationData":[TD([[makeQuery(id+"F54.imprint","IMPRINT",EDGE,{"derivedFrom":sQuery(id+"F54.wireOp",EDGE,"E27.bottom")}),1.0]])]});
            extrude(context, id + "F55", {"entities" : qUnion([Q0]), "operationType" : NewBodyOperationType.ADD, "oppositeDirection" : true, "depth" : 19.05 * mm});
        }
        {
            var Q0;
            Q0=makeQuery(id+"F55.boolean.opBoolean","MERGE",FACE,{"derivedFrom":[makeQuery(id+"F53.opExtrude","CAP_FACE",FACE,{"disambiguationData":[OSD([sQuery(id+"F52.wireOp",EDGE,"E26.bottom"),sQuery(id+"F52.wireOp",EDGE,"E26.top"),sQuery(id+"F52.wireOp",EDGE,"E26.left"),sQuery(id+"F52.wireOp",EDGE,"E26.right")])],"isStart":false}),makeQuery(id+"F55.opExtrude","SWEPT_FACE",FACE,{"disambiguationData":[OSD([sQuery(id+"F54.wireOp",EDGE,"E27.bottom")])]})]});
            var sketch = newSketch(context, id + "F56", { "sketchPlane" : qUnion([Q0])});
            skLineSegment(sketch, "E28.bottom", {"start": v(-71.04, 45.44) * mm, "end": v(-64.7, 45.44) * mm});
            skLineSegment(sketch, "E28.top", {"start": v(-71.04, 39.09) * mm, "end": v(-64.7, 39.09) * mm});
            skLineSegment(sketch, "E28.left", {"start": v(-71.04, 45.44) * mm, "end": v(-71.04, 39.09) * mm});
            skLineSegment(sketch, "E28.right", {"start": v(-64.7, 45.44) * mm, "end": v(-64.7, 39.09) * mm});
            skSolve(sketch);
        }
        {
            var Q0;
            Q0=makeQuery(id+"F56.imprint","IMPRINT",FACE,{"disambiguationData":[TD([[makeQuery(id+"F56.imprint","IMPRINT",EDGE,{"derivedFrom":sQuery(id+"F56.wireOp",EDGE,"E28.bottom")}),1.0]])]});
            extrude(context, id + "F57", {"entities" : qUnion([Q0]), "operationType" : NewBodyOperationType.ADD, "oppositeDirection" : true, "depth" : 44.45 * mm});
        }
        {
            var Q0;
            Q0=makeQuery(id+"F57.boolean.opBoolean","MERGE",FACE,{"derivedFrom":[makeQuery(id+"F55.opExtrude","CAP_FACE",FACE,{"disambiguationData":[OSD([sQuery(id+"F54.wireOp",EDGE,"E27.bottom"),sQuery(id+"F54.wireOp",EDGE,"E27.top"),sQuery(id+"F54.wireOp",EDGE,"E27.left"),sQuery(id+"F54.wireOp",EDGE,"E27.right")])],"isStart":false}),makeQuery(id+"F57.opExtrude","SWEPT_FACE",FACE,{"disambiguationData":[OSD([sQuery(id+"F56.wireOp",EDGE,"E28.bottom")])]})]});
            var sketch = newSketch(context, id + "F58", { "sketchPlane" : qUnion([Q0])});
            skLineSegment(sketch, "E29.bottom", {"start": v(-64.7, 44.45) * mm, "end": v(-71.04, 44.45) * mm});
            skLineSegment(sketch, "E29.top", {"start": v(-64.7, 38.1) * mm, "end": v(-71.04, 38.1) * mm});
            skLineSegment(sketch, "E29.left", {"start": v(-64.7, 44.45) * mm, "end": v(-64.7, 38.1) * mm});
            skLineSegment(sketch, "E29.right", {"start": v(-71.04, 44.45) * mm, "end": v(-71.04, 38.1) * mm});
            skSolve(sketch);
        }
        {
            var Q0;
            Q0=makeQuery(id+"F58.imprint","IMPRINT",FACE,{"disambiguationData":[TD([[makeQuery(id+"F58.imprint","IMPRINT",EDGE,{"derivedFrom":sQuery(id+"F58.wireOp",EDGE,"E29.bottom")}),1.0]])]});
            extrude(context, id + "F59", {"entities" : qUnion([Q0]), "operationType" : NewBodyOperationType.ADD, "oppositeDirection" : true, "depth" : 19.05 * mm});
        }
        {
            var Q0;
            Q0=makeQuery(id+"F59.boolean.opBoolean","MERGE",FACE,{"derivedFrom":[makeQuery(id+"F57.opExtrude","CAP_FACE",FACE,{"disambiguationData":[OSD([sQuery(id+"F56.wireOp",EDGE,"E28.bottom"),sQuery(id+"F56.wireOp",EDGE,"E28.top"),sQuery(id+"F56.wireOp",EDGE,"E28.left"),sQuery(id+"F56.wireOp",EDGE,"E28.right")])],"isStart":false}),makeQuery(id+"F59.opExtrude","SWEPT_FACE",FACE,{"disambiguationData":[OSD([sQuery(id+"F58.wireOp",EDGE,"E29.bottom")])]})]});
            var sketch = newSketch(context, id + "F60", { "sketchPlane" : qUnion([Q0])});
            skLineSegment(sketch, "E30.bottom", {"start": v(-64.7, -26.39) * mm, "end": v(-71.04, -26.39) * mm});
            skLineSegment(sketch, "E30.top", {"start": v(-64.7, -32.74) * mm, "end": v(-71.04, -32.74) * mm});
            skLineSegment(sketch, "E30.left", {"start": v(-64.7, -26.39) * mm, "end": v(-64.7, -32.74) * mm});
            skLineSegment(sketch, "E30.right", {"start": v(-71.04, -26.39) * mm, "end": v(-71.04, -32.74) * mm});
            skSolve(sketch);
        }
        {
            var Q0;
            Q0=makeQuery(id+"F60.imprint","IMPRINT",FACE,{"disambiguationData":[TD([[makeQuery(id+"F60.imprint","IMPRINT",EDGE,{"derivedFrom":sQuery(id+"F60.wireOp",EDGE,"E30.bottom")}),1.0]])]});
            extrude(context, id + "F61", {"entities" : qUnion([Q0]), "operationType" : NewBodyOperationType.ADD, "oppositeDirection" : true, "depth" : 19.05 * mm});
        }
        {
            var Q0;
            Q0=makeQuery(id+"F61.boolean.opBoolean","MERGE",FACE,{"derivedFrom":[makeQuery(id+"F59.boolean.opBoolean","MERGE",FACE,{"derivedFrom":[makeQuery(id+"F57.boolean.opBoolean","MERGE",FACE,{"derivedFrom":[makeQuery(id+"F55.boolean.opBoolean","MERGE",FACE,{"derivedFrom":[makeQuery(id+"F53.boolean.opBoolean","MERGE",FACE,{"derivedFrom":[makeQuery(id+"F51.opExtrude","CAP_FACE",FACE,{"disambiguationData":[OSD([sQuery(id+"F50.wireOp",EDGE,"E25.bottom"),sQuery(id+"F50.wireOp",EDGE,"E25.top"),sQuery(id+"F50.wireOp",EDGE,"E25.left"),sQuery(id+"F50.wireOp",EDGE,"E25.right")])],"isStart":false}),makeQuery(id+"F53.opExtrude","SWEPT_FACE",FACE,{"disambiguationData":[OSD([sQuery(id+"F52.wireOp",EDGE,"E26.left")])]})]}),makeQuery(id+"F55.opExtrude","SWEPT_FACE",FACE,{"disambiguationData":[OSD([sQuery(id+"F54.wireOp",EDGE,"E27.left")])]})]}),makeQuery(id+"F57.opExtrude","SWEPT_FACE",FACE,{"disambiguationData":[OSD([sQuery(id+"F56.wireOp",EDGE,"E28.left")])]})]}),makeQuery(id+"F59.opExtrude","SWEPT_FACE",FACE,{"disambiguationData":[OSD([sQuery(id+"F58.wireOp",EDGE,"E29.right")])]})]}),makeQuery(id+"F61.opExtrude","SWEPT_FACE",FACE,{"disambiguationData":[OSD([sQuery(id+"F60.wireOp",EDGE,"E30.right")])]})]});
            var sketch = newSketch(context, id + "F62", { "sketchPlane" : qUnion([Q0])});
            skLineSegment(sketch, "E31.bottom", {"start": v(26.39, 25.4) * mm, "end": v(32.74, 25.4) * mm});
            skLineSegment(sketch, "E31.top", {"start": v(26.39, 31.75) * mm, "end": v(32.74, 31.75) * mm});
            skLineSegment(sketch, "E31.left", {"start": v(26.39, 25.4) * mm, "end": v(26.39, 31.75) * mm});
            skLineSegment(sketch, "E31.right", {"start": v(32.74, 25.4) * mm, "end": v(32.74, 31.75) * mm});
            skSolve(sketch);
        }
        {
            var Q0;
            Q0=makeQuery(id+"F62.imprint","IMPRINT",FACE,{"disambiguationData":[TD([[makeQuery(id+"F62.imprint","IMPRINT",EDGE,{"derivedFrom":sQuery(id+"F62.wireOp",EDGE,"E31.bottom")}),1.0]])]});
            extrude(context, id + "F63", {"entities" : qUnion([Q0]), "operationType" : NewBodyOperationType.ADD, "oppositeDirection" : true, "depth" : 19.05 * mm});
        }
        {
            var Q0;
            Q0=makeQuery(id+"F63.boolean.opBoolean","MERGE",FACE,{"derivedFrom":[makeQuery(id+"F61.opExtrude","CAP_FACE",FACE,{"disambiguationData":[OSD([sQuery(id+"F60.wireOp",EDGE,"E30.bottom"),sQuery(id+"F60.wireOp",EDGE,"E30.top"),sQuery(id+"F60.wireOp",EDGE,"E30.left"),sQuery(id+"F60.wireOp",EDGE,"E30.right")])],"isStart":false}),makeQuery(id+"F63.opExtrude","SWEPT_FACE",FACE,{"disambiguationData":[OSD([sQuery(id+"F62.wireOp",EDGE,"E31.bottom")])]})]});
            var sketch = newSketch(context, id + "F64", { "sketchPlane" : qUnion([Q0])});
            skLineSegment(sketch, "E32.bottom", {"start": v(-52, 26.39) * mm, "end": v(-58.34, 26.39) * mm});
            skLineSegment(sketch, "E32.top", {"start": v(-52, 32.74) * mm, "end": v(-58.34, 32.74) * mm});
            skLineSegment(sketch, "E32.left", {"start": v(-52, 26.39) * mm, "end": v(-52, 32.74) * mm});
            skLineSegment(sketch, "E32.right", {"start": v(-58.34, 26.39) * mm, "end": v(-58.34, 32.74) * mm});
            skSolve(sketch);
        }
        {
            var Q0;
            Q0=makeQuery(id+"F64.imprint","IMPRINT",FACE,{"disambiguationData":[TD([[makeQuery(id+"F64.imprint","IMPRINT",EDGE,{"derivedFrom":sQuery(id+"F64.wireOp",EDGE,"E32.bottom")}),-1.0]])]});
            extrude(context, id + "F65", {"entities" : qUnion([Q0]), "operationType" : NewBodyOperationType.ADD, "oppositeDirection" : true, "depth" : 19.05 * mm});
        }
        {
            var Q0;
            Q0=makeQuery(id+"F65.boolean.opBoolean","MERGE",FACE,{"derivedFrom":[makeQuery(id+"F63.boolean.opBoolean","MERGE",FACE,{"derivedFrom":[makeQuery(id+"F61.boolean.opBoolean","MERGE",FACE,{"derivedFrom":[makeQuery(id+"F59.opExtrude","CAP_FACE",FACE,{"disambiguationData":[OSD([sQuery(id+"F58.wireOp",EDGE,"E29.bottom"),sQuery(id+"F58.wireOp",EDGE,"E29.top"),sQuery(id+"F58.wireOp",EDGE,"E29.left"),sQuery(id+"F58.wireOp",EDGE,"E29.right")])],"isStart":false}),makeQuery(id+"F61.opExtrude","SWEPT_FACE",FACE,{"disambiguationData":[OSD([sQuery(id+"F60.wireOp",EDGE,"E30.bottom")])]})]}),makeQuery(id+"F63.opExtrude","SWEPT_FACE",FACE,{"disambiguationData":[OSD([sQuery(id+"F62.wireOp",EDGE,"E31.left")])]})]}),makeQuery(id+"F65.opExtrude","SWEPT_FACE",FACE,{"disambiguationData":[OSD([sQuery(id+"F64.wireOp",EDGE,"E32.bottom")])]})]});
            var sketch = newSketch(context, id + "F66", { "sketchPlane" : qUnion([Q0])});
            skLineSegment(sketch, "E33.bottom", {"start": v(52, 44.45) * mm, "end": v(58.34, 44.45) * mm});
            skLineSegment(sketch, "E33.top", {"start": v(52, 38.1) * mm, "end": v(58.34, 38.1) * mm});
            skLineSegment(sketch, "E33.left", {"start": v(52, 44.45) * mm, "end": v(52, 38.1) * mm});
            skLineSegment(sketch, "E33.right", {"start": v(58.34, 44.45) * mm, "end": v(58.34, 38.1) * mm});
            skSolve(sketch);
        }
        {
            var Q0;
            Q0=makeQuery(id+"F66.imprint","IMPRINT",FACE,{"disambiguationData":[TD([[makeQuery(id+"F66.imprint","IMPRINT",EDGE,{"derivedFrom":sQuery(id+"F66.wireOp",EDGE,"E33.bottom")}),-1.0]])]});
            extrude(context, id + "F67", {"entities" : qUnion([Q0]), "operationType" : NewBodyOperationType.ADD, "oppositeDirection" : true, "depth" : 19.05 * mm});
        }
        {
            var Q0;
            Q0=makeQuery(id+"F67.boolean.opBoolean","MERGE",FACE,{"derivedFrom":[makeQuery(id+"F65.opExtrude","CAP_FACE",FACE,{"disambiguationData":[OSD([sQuery(id+"F64.wireOp",EDGE,"E32.bottom"),sQuery(id+"F64.wireOp",EDGE,"E32.top"),sQuery(id+"F64.wireOp",EDGE,"E32.left"),sQuery(id+"F64.wireOp",EDGE,"E32.right")])],"isStart":false}),makeQuery(id+"F67.opExtrude","SWEPT_FACE",FACE,{"disambiguationData":[OSD([sQuery(id+"F66.wireOp",EDGE,"E33.bottom")])]})]});
            var sketch = newSketch(context, id + "F68", { "sketchPlane" : qUnion([Q0])});
            skLineSegment(sketch, "E34.bottom", {"start": v(-58.34, -45.44) * mm, "end": v(-52, -45.44) * mm});
            skLineSegment(sketch, "E34.top", {"start": v(-58.34, -39.09) * mm, "end": v(-52, -39.09) * mm});
            skLineSegment(sketch, "E34.left", {"start": v(-58.34, -45.44) * mm, "end": v(-58.34, -39.09) * mm});
            skLineSegment(sketch, "E34.right", {"start": v(-52, -45.44) * mm, "end": v(-52, -39.09) * mm});
            skSolve(sketch);
        }
        {
            var Q0;
            Q0=makeQuery(id+"F68.imprint","IMPRINT",FACE,{"disambiguationData":[TD([[makeQuery(id+"F68.imprint","IMPRINT",EDGE,{"derivedFrom":sQuery(id+"F68.wireOp",EDGE,"E34.bottom")}),-1.0]])]});
            extrude(context, id + "F69", {"entities" : qUnion([Q0]), "operationType" : NewBodyOperationType.ADD, "oppositeDirection" : true, "depth" : 19.05 * mm});
        }
        {
            var Q0;
            Q0=makeQuery(id+"F69.boolean.opBoolean","MERGE",FACE,{"derivedFrom":[makeQuery(id+"F67.boolean.opBoolean","MERGE",FACE,{"derivedFrom":[makeQuery(id+"F65.opExtrude","SWEPT_FACE",FACE,{"disambiguationData":[OSD([sQuery(id+"F64.wireOp",EDGE,"E32.right")])]}),makeQuery(id+"F67.opExtrude","SWEPT_FACE",FACE,{"disambiguationData":[OSD([sQuery(id+"F66.wireOp",EDGE,"E33.right")])]})]}),makeQuery(id+"F69.opExtrude","SWEPT_FACE",FACE,{"disambiguationData":[OSD([sQuery(id+"F68.wireOp",EDGE,"E34.left")])]})]});
            var sketch = newSketch(context, id + "F70", { "sketchPlane" : qUnion([Q0])});
            skLineSegment(sketch, "E35.bottom", {"start": v(45.44, 25.4) * mm, "end": v(39.09, 25.4) * mm});
            skLineSegment(sketch, "E35.top", {"start": v(45.44, 31.75) * mm, "end": v(39.09, 31.75) * mm});
            skLineSegment(sketch, "E35.left", {"start": v(45.44, 25.4) * mm, "end": v(45.44, 31.75) * mm});
            skLineSegment(sketch, "E35.right", {"start": v(39.09, 25.4) * mm, "end": v(39.09, 31.75) * mm});
            skSolve(sketch);
        }
        {
            var Q0;
            Q0=makeQuery(id+"F70.imprint","IMPRINT",FACE,{"disambiguationData":[TD([[makeQuery(id+"F70.imprint","IMPRINT",EDGE,{"derivedFrom":sQuery(id+"F70.wireOp",EDGE,"E35.bottom")}),1.0]])]});
            extrude(context, id + "F71", {"entities" : qUnion([Q0]), "operationType" : NewBodyOperationType.ADD, "oppositeDirection" : true, "depth" : 31.75 * mm});
        }
        {
            var Q0;
            Q0=makeQuery(id+"F71.boolean.opBoolean","MERGE",FACE,{"derivedFrom":[makeQuery(id+"F69.boolean.opBoolean","MERGE",FACE,{"derivedFrom":[makeQuery(id+"F67.opExtrude","CAP_FACE",FACE,{"disambiguationData":[OSD([sQuery(id+"F66.wireOp",EDGE,"E33.bottom"),sQuery(id+"F66.wireOp",EDGE,"E33.top"),sQuery(id+"F66.wireOp",EDGE,"E33.left"),sQuery(id+"F66.wireOp",EDGE,"E33.right")])],"isStart":false}),makeQuery(id+"F69.opExtrude","SWEPT_FACE",FACE,{"disambiguationData":[OSD([sQuery(id+"F68.wireOp",EDGE,"E34.bottom")])]})]}),makeQuery(id+"F71.opExtrude","SWEPT_FACE",FACE,{"disambiguationData":[OSD([sQuery(id+"F70.wireOp",EDGE,"E35.left")])]})]});
            var sketch = newSketch(context, id + "F72", { "sketchPlane" : qUnion([Q0])});
            skLineSegment(sketch, "E36.bottom", {"start": v(-26.6, 25.4) * mm, "end": v(-32.94, 25.4) * mm});
            skLineSegment(sketch, "E36.top", {"start": v(-26.6, 31.75) * mm, "end": v(-32.94, 31.75) * mm});
            skLineSegment(sketch, "E36.left", {"start": v(-26.6, 25.4) * mm, "end": v(-26.6, 31.75) * mm});
            skLineSegment(sketch, "E36.right", {"start": v(-32.94, 25.4) * mm, "end": v(-32.94, 31.75) * mm});
            skSolve(sketch);
        }
        {
            var Q0;
            Q0=makeQuery(id+"F72.imprint","IMPRINT",FACE,{"disambiguationData":[TD([[makeQuery(id+"F72.imprint","IMPRINT",EDGE,{"derivedFrom":sQuery(id+"F72.wireOp",EDGE,"E36.bottom")}),-1.0]])]});
            extrude(context, id + "F73", {"entities" : qUnion([Q0]), "operationType" : NewBodyOperationType.ADD, "oppositeDirection" : true, "depth" : 19.05 * mm});
        }
        {
            var Q0;
            Q0=makeQuery(id+"F73.boolean.opBoolean","MERGE",FACE,{"derivedFrom":[makeQuery(id+"F71.opExtrude","CAP_FACE",FACE,{"disambiguationData":[OSD([sQuery(id+"F70.wireOp",EDGE,"E35.bottom"),sQuery(id+"F70.wireOp",EDGE,"E35.top"),sQuery(id+"F70.wireOp",EDGE,"E35.left"),sQuery(id+"F70.wireOp",EDGE,"E35.right")])],"isStart":false}),makeQuery(id+"F73.opExtrude","SWEPT_FACE",FACE,{"disambiguationData":[OSD([sQuery(id+"F72.wireOp",EDGE,"E36.left")])]})]});
            var sketch = newSketch(context, id + "F74", { "sketchPlane" : qUnion([Q0])});
            skLineSegment(sketch, "E37.bottom", {"start": v(-26.39, 25.4) * mm, "end": v(-32.74, 25.4) * mm});
            skLineSegment(sketch, "E37.top", {"start": v(-26.39, 31.75) * mm, "end": v(-32.74, 31.75) * mm});
            skLineSegment(sketch, "E37.left", {"start": v(-26.39, 25.4) * mm, "end": v(-26.39, 31.75) * mm});
            skLineSegment(sketch, "E37.right", {"start": v(-32.74, 25.4) * mm, "end": v(-32.74, 31.75) * mm});
            skSolve(sketch);
        }
        {
            var Q0;
            Q0=makeQuery(id+"F74.imprint","IMPRINT",FACE,{"disambiguationData":[TD([[makeQuery(id+"F74.imprint","IMPRINT",EDGE,{"derivedFrom":sQuery(id+"F74.wireOp",EDGE,"E37.bottom")}),-1.0]])]});
            extrude(context, id + "F75", {"entities" : qUnion([Q0]), "operationType" : NewBodyOperationType.ADD, "oppositeDirection" : true, "depth" : 19.05 * mm});
        }
        {
            var Q0;
            Q0=makeQuery(id+"F75.boolean.opBoolean","MERGE",FACE,{"derivedFrom":[makeQuery(id+"F73.boolean.opBoolean","MERGE",FACE,{"derivedFrom":[makeQuery(id+"F71.boolean.opBoolean","MERGE",FACE,{"derivedFrom":[makeQuery(id+"F69.opExtrude","CAP_FACE",FACE,{"disambiguationData":[OSD([sQuery(id+"F68.wireOp",EDGE,"E34.bottom"),sQuery(id+"F68.wireOp",EDGE,"E34.top"),sQuery(id+"F68.wireOp",EDGE,"E34.left"),sQuery(id+"F68.wireOp",EDGE,"E34.right")])],"isStart":false}),makeQuery(id+"F71.opExtrude","SWEPT_FACE",FACE,{"disambiguationData":[OSD([sQuery(id+"F70.wireOp",EDGE,"E35.bottom")])]})]}),makeQuery(id+"F73.opExtrude","SWEPT_FACE",FACE,{"disambiguationData":[OSD([sQuery(id+"F72.wireOp",EDGE,"E36.bottom")])]})]}),makeQuery(id+"F75.opExtrude","SWEPT_FACE",FACE,{"disambiguationData":[OSD([sQuery(id+"F74.wireOp",EDGE,"E37.bottom")])]})]});
            var sketch = newSketch(context, id + "F76", { "sketchPlane" : qUnion([Q0])});
            skLineSegment(sketch, "E38.bottom", {"start": v(-45.64, 26.39) * mm, "end": v(-39.3, 26.39) * mm});
            skLineSegment(sketch, "E38.top", {"start": v(-45.64, 32.74) * mm, "end": v(-39.3, 32.74) * mm});
            skLineSegment(sketch, "E38.left", {"start": v(-45.64, 26.39) * mm, "end": v(-45.64, 32.74) * mm});
            skLineSegment(sketch, "E38.right", {"start": v(-39.3, 26.39) * mm, "end": v(-39.3, 32.74) * mm});
            skSolve(sketch);
        }
        {
            var Q0;
            Q0=makeQuery(id+"F76.imprint","IMPRINT",FACE,{"disambiguationData":[TD([[makeQuery(id+"F76.imprint","IMPRINT",EDGE,{"derivedFrom":sQuery(id+"F76.wireOp",EDGE,"E38.bottom")}),-1.0]])]});
            extrude(context, id + "F77", {"entities" : qUnion([Q0]), "operationType" : NewBodyOperationType.ADD, "oppositeDirection" : true, "depth" : 19.05 * mm});
        }
        {
            var Q0;
            Q0=makeQuery(id+"F77.boolean.opBoolean","MERGE",FACE,{"derivedFrom":[makeQuery(id+"F75.opExtrude","CAP_FACE",FACE,{"disambiguationData":[OSD([sQuery(id+"F74.wireOp",EDGE,"E37.bottom"),sQuery(id+"F74.wireOp",EDGE,"E37.top"),sQuery(id+"F74.wireOp",EDGE,"E37.left"),sQuery(id+"F74.wireOp",EDGE,"E37.right")])],"isStart":false}),makeQuery(id+"F77.opExtrude","SWEPT_FACE",FACE,{"disambiguationData":[OSD([sQuery(id+"F76.wireOp",EDGE,"E38.left")])]})]});
            var sketch = newSketch(context, id + "F78", { "sketchPlane" : qUnion([Q0])});
            skLineSegment(sketch, "E39.bottom", {"start": v(26.39, 44.45) * mm, "end": v(32.74, 44.45) * mm});
            skLineSegment(sketch, "E39.top", {"start": v(26.39, 38.1) * mm, "end": v(32.74, 38.1) * mm});
            skLineSegment(sketch, "E39.left", {"start": v(26.39, 44.45) * mm, "end": v(26.39, 38.1) * mm});
            skLineSegment(sketch, "E39.right", {"start": v(32.74, 44.45) * mm, "end": v(32.74, 38.1) * mm});
            skSolve(sketch);
        }
        {
            var Q0;
            Q0=makeQuery(id+"F78.imprint","IMPRINT",FACE,{"disambiguationData":[TD([[makeQuery(id+"F78.imprint","IMPRINT",EDGE,{"derivedFrom":sQuery(id+"F78.wireOp",EDGE,"E39.bottom")}),-1.0]])]});
            extrude(context, id + "F79", {"entities" : qUnion([Q0]), "operationType" : NewBodyOperationType.ADD, "oppositeDirection" : true, "depth" : 19.05 * mm});
        }
        {
            var Q0;
            Q0=makeQuery(id+"F79.boolean.opBoolean","MERGE",FACE,{"derivedFrom":[makeQuery(id+"F77.boolean.opBoolean","MERGE",FACE,{"derivedFrom":[makeQuery(id+"F75.boolean.opBoolean","MERGE",FACE,{"derivedFrom":[makeQuery(id+"F73.opExtrude","CAP_FACE",FACE,{"disambiguationData":[OSD([sQuery(id+"F72.wireOp",EDGE,"E36.bottom"),sQuery(id+"F72.wireOp",EDGE,"E36.top"),sQuery(id+"F72.wireOp",EDGE,"E36.left"),sQuery(id+"F72.wireOp",EDGE,"E36.right")])],"isStart":false}),makeQuery(id+"F75.opExtrude","SWEPT_FACE",FACE,{"disambiguationData":[OSD([sQuery(id+"F74.wireOp",EDGE,"E37.left")])]})]}),makeQuery(id+"F77.opExtrude","SWEPT_FACE",FACE,{"disambiguationData":[OSD([sQuery(id+"F76.wireOp",EDGE,"E38.bottom")])]})]}),makeQuery(id+"F79.opExtrude","SWEPT_FACE",FACE,{"disambiguationData":[OSD([sQuery(id+"F78.wireOp",EDGE,"E39.left")])]})]});
            var sketch = newSketch(context, id + "F80", { "sketchPlane" : qUnion([Q0])});
            skLineSegment(sketch, "E40.bottom", {"start": v(26.6, 44.45) * mm, "end": v(32.94, 44.45) * mm});
            skLineSegment(sketch, "E40.top", {"start": v(26.6, 38.1) * mm, "end": v(32.94, 38.1) * mm});
            skLineSegment(sketch, "E40.left", {"start": v(26.6, 44.45) * mm, "end": v(26.6, 38.1) * mm});
            skLineSegment(sketch, "E40.right", {"start": v(32.94, 44.45) * mm, "end": v(32.94, 38.1) * mm});
            skSolve(sketch);
        }
        {
            var Q0;
            Q0=makeQuery(id+"F80.imprint","IMPRINT",FACE,{"disambiguationData":[TD([[makeQuery(id+"F80.imprint","IMPRINT",EDGE,{"derivedFrom":sQuery(id+"F80.wireOp",EDGE,"E40.bottom")}),-1.0]])]});
            extrude(context, id + "F81", {"entities" : qUnion([Q0]), "operationType" : NewBodyOperationType.ADD, "oppositeDirection" : true, "depth" : 19.05 * mm});
        }
        {
            var Q0;
            Q0=makeQuery(id+"F81.boolean.opBoolean","MERGE",FACE,{"derivedFrom":[makeQuery(id+"F79.opExtrude","CAP_FACE",FACE,{"disambiguationData":[OSD([sQuery(id+"F78.wireOp",EDGE,"E39.bottom"),sQuery(id+"F78.wireOp",EDGE,"E39.top"),sQuery(id+"F78.wireOp",EDGE,"E39.left"),sQuery(id+"F78.wireOp",EDGE,"E39.right")])],"isStart":false}),makeQuery(id+"F81.opExtrude","SWEPT_FACE",FACE,{"disambiguationData":[OSD([sQuery(id+"F80.wireOp",EDGE,"E40.left")])]})]});
            var sketch = newSketch(context, id + "F82", { "sketchPlane" : qUnion([Q0])});
            skLineSegment(sketch, "E41.bottom", {"start": v(-45.44, 44.45) * mm, "end": v(-39.09, 44.45) * mm});
            skLineSegment(sketch, "E41.top", {"start": v(-45.44, 38.1) * mm, "end": v(-39.09, 38.1) * mm});
            skLineSegment(sketch, "E41.left", {"start": v(-45.44, 44.45) * mm, "end": v(-45.44, 38.1) * mm});
            skLineSegment(sketch, "E41.right", {"start": v(-39.09, 44.45) * mm, "end": v(-39.09, 38.1) * mm});
            skSolve(sketch);
        }
        {
            var Q0;
            Q0=makeQuery(id+"F82.imprint","IMPRINT",FACE,{"disambiguationData":[TD([[makeQuery(id+"F82.imprint","IMPRINT",EDGE,{"derivedFrom":sQuery(id+"F82.wireOp",EDGE,"E41.bottom")}),1.0]])]});
            extrude(context, id + "F83", {"entities" : qUnion([Q0]), "operationType" : NewBodyOperationType.ADD, "oppositeDirection" : true, "depth" : 19.05 * mm});
        }
        {
            var Q0;
            Q0=makeQuery(id+"F83.opExtrude","SWEPT_FACE",FACE,{"disambiguationData":[OSD([sQuery(id+"F82.wireOp",EDGE,"E41.right")])]});
            var sketch = newSketch(context, id + "F84", { "sketchPlane" : qUnion([Q0])});
            skLineSegment(sketch, "E42.bottom", {"start": v(45.64, 44.45) * mm, "end": v(39.3, 44.45) * mm});
            skLineSegment(sketch, "E42.top", {"start": v(45.64, 38.1) * mm, "end": v(39.3, 38.1) * mm});
            skLineSegment(sketch, "E42.left", {"start": v(45.64, 44.45) * mm, "end": v(45.64, 38.1) * mm});
            skLineSegment(sketch, "E42.right", {"start": v(39.3, 44.45) * mm, "end": v(39.3, 38.1) * mm});
            skSolve(sketch);
        }
        {
            var Q0;
            Q0=makeQuery(id+"F84.imprint","IMPRINT",FACE,{"disambiguationData":[TD([[makeQuery(id+"F84.imprint","IMPRINT",EDGE,{"derivedFrom":sQuery(id+"F84.wireOp",EDGE,"E42.bottom")}),1.0]])]});
            extrude(context, id + "F85", {"entities" : qUnion([Q0]), "operationType" : NewBodyOperationType.ADD, "oppositeDirection" : true, "depth" : 19.05 * mm});
        }
        {
            var Q0;
            Q0=makeQuery(id+"F85.boolean.opBoolean","MERGE",FACE,{"derivedFrom":[makeQuery(id+"F83.opExtrude","CAP_FACE",FACE,{"disambiguationData":[OSD([sQuery(id+"F82.wireOp",EDGE,"E41.bottom"),sQuery(id+"F82.wireOp",EDGE,"E41.top"),sQuery(id+"F82.wireOp",EDGE,"E41.left"),sQuery(id+"F82.wireOp",EDGE,"E41.right")])],"isStart":false}),makeQuery(id+"F85.opExtrude","SWEPT_FACE",FACE,{"disambiguationData":[OSD([sQuery(id+"F84.wireOp",EDGE,"E42.left")])]})]});
            var sketch = newSketch(context, id + "F86", { "sketchPlane" : qUnion([Q0])});
            skLineSegment(sketch, "E43.bottom", {"start": v(58.14, 44.45) * mm, "end": v(51.79, 44.45) * mm});
            skLineSegment(sketch, "E43.top", {"start": v(58.14, 38.1) * mm, "end": v(51.79, 38.1) * mm});
            skLineSegment(sketch, "E43.left", {"start": v(58.14, 44.45) * mm, "end": v(58.14, 38.1) * mm});
            skLineSegment(sketch, "E43.right", {"start": v(51.79, 44.45) * mm, "end": v(51.79, 38.1) * mm});
            skSolve(sketch);
        }
        {
            var Q0;
            Q0=makeQuery(id+"F86.imprint","IMPRINT",FACE,{"disambiguationData":[TD([[makeQuery(id+"F86.imprint","IMPRINT",EDGE,{"derivedFrom":sQuery(id+"F86.wireOp",EDGE,"E43.bottom")}),-1.0]])]});
            extrude(context, id + "F87", {"entities" : qUnion([Q0]), "operationType" : NewBodyOperationType.ADD, "oppositeDirection" : true, "depth" : 19.05 * mm});
        }
        {
            var Q0;
            Q0=makeQuery(id+"F87.boolean.opBoolean","MERGE",FACE,{"derivedFrom":[makeQuery(id+"F85.boolean.opBoolean","MERGE",FACE,{"derivedFrom":[makeQuery(id+"F83.boolean.opBoolean","MERGE",FACE,{"derivedFrom":[makeQuery(id+"F81.boolean.opBoolean","MERGE",FACE,{"derivedFrom":[makeQuery(id+"F79.boolean.opBoolean","MERGE",FACE,{"derivedFrom":[makeQuery(id+"F77.opExtrude","CAP_FACE",FACE,{"disambiguationData":[OSD([sQuery(id+"F76.wireOp",EDGE,"E38.bottom"),sQuery(id+"F76.wireOp",EDGE,"E38.top"),sQuery(id+"F76.wireOp",EDGE,"E38.left"),sQuery(id+"F76.wireOp",EDGE,"E38.right")])],"isStart":false}),makeQuery(id+"F79.opExtrude","SWEPT_FACE",FACE,{"disambiguationData":[OSD([sQuery(id+"F78.wireOp",EDGE,"E39.bottom")])]})]}),makeQuery(id+"F81.opExtrude","SWEPT_FACE",FACE,{"disambiguationData":[OSD([sQuery(id+"F80.wireOp",EDGE,"E40.bottom")])]})]}),makeQuery(id+"F83.opExtrude","SWEPT_FACE",FACE,{"disambiguationData":[OSD([sQuery(id+"F82.wireOp",EDGE,"E41.bottom")])]})]}),makeQuery(id+"F85.opExtrude","SWEPT_FACE",FACE,{"disambiguationData":[OSD([sQuery(id+"F84.wireOp",EDGE,"E42.bottom")])]})]}),makeQuery(id+"F87.opExtrude","SWEPT_FACE",FACE,{"disambiguationData":[OSD([sQuery(id+"F86.wireOp",EDGE,"E43.bottom")])]})]});
            var sketch = newSketch(context, id + "F88", { "sketchPlane" : qUnion([Q0])});
            skLineSegment(sketch, "E44.bottom", {"start": v(-26.6, -58.14) * mm, "end": v(-32.94, -58.14) * mm});
            skLineSegment(sketch, "E44.top", {"start": v(-26.6, -51.79) * mm, "end": v(-32.94, -51.79) * mm});
            skLineSegment(sketch, "E44.left", {"start": v(-26.6, -58.14) * mm, "end": v(-26.6, -51.79) * mm});
            skLineSegment(sketch, "E44.right", {"start": v(-32.94, -58.14) * mm, "end": v(-32.94, -51.79) * mm});
            skSolve(sketch);
        }
        {
            var Q0;
            Q0=makeQuery(id+"F88.imprint","IMPRINT",FACE,{"disambiguationData":[TD([[makeQuery(id+"F88.imprint","IMPRINT",EDGE,{"derivedFrom":sQuery(id+"F88.wireOp",EDGE,"E44.bottom")}),1.0]])]});
            extrude(context, id + "F89", {"entities" : qUnion([Q0]), "operationType" : NewBodyOperationType.ADD, "oppositeDirection" : true, "depth" : 19.05 * mm});
        }
        {
            var Q0;
            Q0=makeQuery(id+"F89.boolean.opBoolean","MERGE",FACE,{"derivedFrom":[makeQuery(id+"F87.opExtrude","CAP_FACE",FACE,{"disambiguationData":[OSD([sQuery(id+"F86.wireOp",EDGE,"E43.bottom"),sQuery(id+"F86.wireOp",EDGE,"E43.top"),sQuery(id+"F86.wireOp",EDGE,"E43.left"),sQuery(id+"F86.wireOp",EDGE,"E43.right")])],"isStart":false}),makeQuery(id+"F89.opExtrude","SWEPT_FACE",FACE,{"disambiguationData":[OSD([sQuery(id+"F88.wireOp",EDGE,"E44.left")])]})]});
            var sketch = newSketch(context, id + "F90", { "sketchPlane" : qUnion([Q0])});
            skLineSegment(sketch, "E45.bottom", {"start": v(-58.14, 25.4) * mm, "end": v(-51.79, 25.4) * mm});
            skLineSegment(sketch, "E45.top", {"start": v(-58.14, 31.75) * mm, "end": v(-51.79, 31.75) * mm});
            skLineSegment(sketch, "E45.left", {"start": v(-58.14, 25.4) * mm, "end": v(-58.14, 31.75) * mm});
            skLineSegment(sketch, "E45.right", {"start": v(-51.79, 25.4) * mm, "end": v(-51.79, 31.75) * mm});
            skSolve(sketch);
        }
        {
            var Q0;
            Q0=makeQuery(id+"F90.imprint","IMPRINT",FACE,{"disambiguationData":[TD([[makeQuery(id+"F90.imprint","IMPRINT",EDGE,{"derivedFrom":sQuery(id+"F90.wireOp",EDGE,"E45.bottom")}),-1.0]])]});
            extrude(context, id + "F91", {"entities" : qUnion([Q0]), "operationType" : NewBodyOperationType.ADD, "oppositeDirection" : true, "depth" : 19.05 * mm});
        }
        {
            var Q0;
            Q0=makeQuery(id+"F91.boolean.opBoolean","MERGE",FACE,{"derivedFrom":[makeQuery(id+"F89.boolean.opBoolean","MERGE",FACE,{"derivedFrom":[makeQuery(id+"F87.opExtrude","SWEPT_FACE",FACE,{"disambiguationData":[OSD([sQuery(id+"F86.wireOp",EDGE,"E43.right")])]}),makeQuery(id+"F89.opExtrude","SWEPT_FACE",FACE,{"disambiguationData":[OSD([sQuery(id+"F88.wireOp",EDGE,"E44.top")])]})]}),makeQuery(id+"F91.opExtrude","SWEPT_FACE",FACE,{"disambiguationData":[OSD([sQuery(id+"F90.wireOp",EDGE,"E45.right")])]})]});
            var sketch = newSketch(context, id + "F92", { "sketchPlane" : qUnion([Q0])});
            skLineSegment(sketch, "E46.bottom", {"start": v(45.64, 25.4) * mm, "end": v(39.3, 25.4) * mm});
            skLineSegment(sketch, "E46.top", {"start": v(45.64, 31.75) * mm, "end": v(39.3, 31.75) * mm});
            skLineSegment(sketch, "E46.left", {"start": v(45.64, 25.4) * mm, "end": v(45.64, 31.75) * mm});
            skLineSegment(sketch, "E46.right", {"start": v(39.3, 25.4) * mm, "end": v(39.3, 31.75) * mm});
            skSolve(sketch);
        }
        {
            var Q0;
            Q0=makeQuery(id+"F92.imprint","IMPRINT",FACE,{"disambiguationData":[TD([[makeQuery(id+"F92.imprint","IMPRINT",EDGE,{"derivedFrom":sQuery(id+"F92.wireOp",EDGE,"E46.bottom")}),1.0]])]});
            extrude(context, id + "F93", {"entities" : qUnion([Q0]), "operationType" : NewBodyOperationType.ADD, "oppositeDirection" : true, "depth" : 19.05 * mm});
        }
        {
            var Q0;
            Q0=makeQuery(id+"F93.boolean.opBoolean","MERGE",FACE,{"derivedFrom":[makeQuery(id+"F91.opExtrude","CAP_FACE",FACE,{"disambiguationData":[OSD([sQuery(id+"F90.wireOp",EDGE,"E45.bottom"),sQuery(id+"F90.wireOp",EDGE,"E45.top"),sQuery(id+"F90.wireOp",EDGE,"E45.left"),sQuery(id+"F90.wireOp",EDGE,"E45.right")])],"isStart":false}),makeQuery(id+"F93.opExtrude","SWEPT_FACE",FACE,{"disambiguationData":[OSD([sQuery(id+"F92.wireOp",EDGE,"E46.left")])]})]});
            var sketch = newSketch(context, id + "F94", { "sketchPlane" : qUnion([Q0])});
            skLineSegment(sketch, "E47.bottom", {"start": v(70.84, 25.4) * mm, "end": v(64.49, 25.4) * mm});
            skLineSegment(sketch, "E47.top", {"start": v(70.84, 31.75) * mm, "end": v(64.49, 31.75) * mm});
            skLineSegment(sketch, "E47.left", {"start": v(70.84, 25.4) * mm, "end": v(70.84, 31.75) * mm});
            skLineSegment(sketch, "E47.right", {"start": v(64.49, 25.4) * mm, "end": v(64.49, 31.75) * mm});
            skSolve(sketch);
        }
        {
            var Q0;
            Q0=makeQuery(id+"F94.imprint","IMPRINT",FACE,{"disambiguationData":[TD([[makeQuery(id+"F94.imprint","IMPRINT",EDGE,{"derivedFrom":sQuery(id+"F94.wireOp",EDGE,"E47.bottom")}),1.0]])]});
            extrude(context, id + "F95", {"entities" : qUnion([Q0]), "operationType" : NewBodyOperationType.ADD, "oppositeDirection" : true, "depth" : 19.05 * mm});
        }
        {
            var Q0;
            Q0=makeQuery(id+"F95.boolean.opBoolean","MERGE",FACE,{"derivedFrom":[makeQuery(id+"F93.boolean.opBoolean","MERGE",FACE,{"derivedFrom":[makeQuery(id+"F91.boolean.opBoolean","MERGE",FACE,{"derivedFrom":[makeQuery(id+"F89.opExtrude","CAP_FACE",FACE,{"disambiguationData":[OSD([sQuery(id+"F88.wireOp",EDGE,"E44.bottom"),sQuery(id+"F88.wireOp",EDGE,"E44.top"),sQuery(id+"F88.wireOp",EDGE,"E44.left"),sQuery(id+"F88.wireOp",EDGE,"E44.right")])],"isStart":false}),makeQuery(id+"F91.opExtrude","SWEPT_FACE",FACE,{"disambiguationData":[OSD([sQuery(id+"F90.wireOp",EDGE,"E45.bottom")])]})]}),makeQuery(id+"F93.opExtrude","SWEPT_FACE",FACE,{"disambiguationData":[OSD([sQuery(id+"F92.wireOp",EDGE,"E46.bottom")])]})]}),makeQuery(id+"F95.opExtrude","SWEPT_FACE",FACE,{"disambiguationData":[OSD([sQuery(id+"F94.wireOp",EDGE,"E47.bottom")])]})]});
            var sketch = newSketch(context, id + "F96", { "sketchPlane" : qUnion([Q0])});
            skLineSegment(sketch, "E48.bottom", {"start": v(-26.6, 70.84) * mm, "end": v(-32.94, 70.84) * mm});
            skLineSegment(sketch, "E48.top", {"start": v(-26.6, 64.49) * mm, "end": v(-32.94, 64.49) * mm});
            skLineSegment(sketch, "E48.left", {"start": v(-26.6, 70.84) * mm, "end": v(-26.6, 64.49) * mm});
            skLineSegment(sketch, "E48.right", {"start": v(-32.94, 70.84) * mm, "end": v(-32.94, 64.49) * mm});
            skSolve(sketch);
        }
        {
            var Q0;
            Q0=makeQuery(id+"F96.imprint","IMPRINT",FACE,{"disambiguationData":[TD([[makeQuery(id+"F96.imprint","IMPRINT",EDGE,{"derivedFrom":sQuery(id+"F96.wireOp",EDGE,"E48.bottom")}),1.0]])]});
            extrude(context, id + "F97", {"entities" : qUnion([Q0]), "operationType" : NewBodyOperationType.ADD, "oppositeDirection" : true, "depth" : 19.05 * mm});
        }
        {
            var Q0;
            Q0=makeQuery(id+"F97.boolean.opBoolean","MERGE",FACE,{"derivedFrom":[makeQuery(id+"F95.opExtrude","CAP_FACE",FACE,{"disambiguationData":[OSD([sQuery(id+"F94.wireOp",EDGE,"E47.bottom"),sQuery(id+"F94.wireOp",EDGE,"E47.top"),sQuery(id+"F94.wireOp",EDGE,"E47.left"),sQuery(id+"F94.wireOp",EDGE,"E47.right")])],"isStart":false}),makeQuery(id+"F97.opExtrude","SWEPT_FACE",FACE,{"disambiguationData":[OSD([sQuery(id+"F96.wireOp",EDGE,"E48.left")])]})]});
            var sketch = newSketch(context, id + "F98", { "sketchPlane" : qUnion([Q0])});
            skLineSegment(sketch, "E49.bottom", {"start": v(-70.84, 44.45) * mm, "end": v(-64.49, 44.45) * mm});
            skLineSegment(sketch, "E49.top", {"start": v(-70.84, 38.1) * mm, "end": v(-64.49, 38.1) * mm});
            skLineSegment(sketch, "E49.left", {"start": v(-70.84, 44.45) * mm, "end": v(-70.84, 38.1) * mm});
            skLineSegment(sketch, "E49.right", {"start": v(-64.49, 44.45) * mm, "end": v(-64.49, 38.1) * mm});
            skSolve(sketch);
        }
        {
            var Q0;
            Q0=makeQuery(id+"F98.imprint","IMPRINT",FACE,{"disambiguationData":[TD([[makeQuery(id+"F98.imprint","IMPRINT",EDGE,{"derivedFrom":sQuery(id+"F98.wireOp",EDGE,"E49.bottom")}),1.0]])]});
            extrude(context, id + "F99", {"entities" : qUnion([Q0]), "operationType" : NewBodyOperationType.ADD, "oppositeDirection" : true, "depth" : 31.75 * mm});
        }
        {
            var Q0;
            Q0=makeQuery(id+"F99.boolean.opBoolean","MERGE",FACE,{"derivedFrom":[makeQuery(id+"F97.opExtrude","CAP_FACE",FACE,{"disambiguationData":[OSD([sQuery(id+"F96.wireOp",EDGE,"E48.bottom"),sQuery(id+"F96.wireOp",EDGE,"E48.top"),sQuery(id+"F96.wireOp",EDGE,"E48.left"),sQuery(id+"F96.wireOp",EDGE,"E48.right")])],"isStart":false}),makeQuery(id+"F99.opExtrude","SWEPT_FACE",FACE,{"disambiguationData":[OSD([sQuery(id+"F98.wireOp",EDGE,"E49.bottom")])]})]});
            var sketch = newSketch(context, id + "F100", { "sketchPlane" : qUnion([Q0])});
            skLineSegment(sketch, "E50.bottom", {"start": v(-58.34, -70.84) * mm, "end": v(-52, -70.84) * mm});
            skLineSegment(sketch, "E50.top", {"start": v(-58.34, -64.49) * mm, "end": v(-52, -64.49) * mm});
            skLineSegment(sketch, "E50.left", {"start": v(-58.34, -70.84) * mm, "end": v(-58.34, -64.49) * mm});
            skLineSegment(sketch, "E50.right", {"start": v(-52, -70.84) * mm, "end": v(-52, -64.49) * mm});
            skSolve(sketch);
        }
        {
            var Q0;
            Q0=makeQuery(id+"F100.imprint","IMPRINT",FACE,{"disambiguationData":[TD([[makeQuery(id+"F100.imprint","IMPRINT",EDGE,{"derivedFrom":sQuery(id+"F100.wireOp",EDGE,"E50.bottom")}),-1.0]])]});
            extrude(context, id + "F101", {"entities" : qUnion([Q0]), "operationType" : NewBodyOperationType.ADD, "oppositeDirection" : true, "depth" : 19.05 * mm});
        }
        {
            var Q0;
            Q0=makeQuery(id+"F101.boolean.opBoolean","MERGE",FACE,{"derivedFrom":[makeQuery(id+"F99.boolean.opBoolean","MERGE",FACE,{"derivedFrom":[makeQuery(id+"F97.boolean.opBoolean","MERGE",FACE,{"derivedFrom":[makeQuery(id+"F95.boolean.opBoolean","MERGE",FACE,{"derivedFrom":[makeQuery(id+"F93.opExtrude","CAP_FACE",FACE,{"disambiguationData":[OSD([sQuery(id+"F92.wireOp",EDGE,"E46.bottom"),sQuery(id+"F92.wireOp",EDGE,"E46.top"),sQuery(id+"F92.wireOp",EDGE,"E46.left"),sQuery(id+"F92.wireOp",EDGE,"E46.right")])],"isStart":false}),makeQuery(id+"F95.opExtrude","SWEPT_FACE",FACE,{"disambiguationData":[OSD([sQuery(id+"F94.wireOp",EDGE,"E47.left")])]})]}),makeQuery(id+"F97.opExtrude","SWEPT_FACE",FACE,{"disambiguationData":[OSD([sQuery(id+"F96.wireOp",EDGE,"E48.bottom")])]})]}),makeQuery(id+"F99.opExtrude","SWEPT_FACE",FACE,{"disambiguationData":[OSD([sQuery(id+"F98.wireOp",EDGE,"E49.left")])]})]}),makeQuery(id+"F101.opExtrude","SWEPT_FACE",FACE,{"disambiguationData":[OSD([sQuery(id+"F100.wireOp",EDGE,"E50.bottom")])]})]});
            var sketch = newSketch(context, id + "F102", { "sketchPlane" : qUnion([Q0])});
            skLineSegment(sketch, "E51.bottom", {"start": v(-58.34, 25.4) * mm, "end": v(-52, 25.4) * mm});
            skLineSegment(sketch, "E51.top", {"start": v(-58.34, 31.75) * mm, "end": v(-52, 31.75) * mm});
            skLineSegment(sketch, "E51.left", {"start": v(-58.34, 25.4) * mm, "end": v(-58.34, 31.75) * mm});
            skLineSegment(sketch, "E51.right", {"start": v(-52, 25.4) * mm, "end": v(-52, 31.75) * mm});
            skSolve(sketch);
        }
        {
            var Q0;
            Q0=makeQuery(id+"F102.imprint","IMPRINT",FACE,{"disambiguationData":[TD([[makeQuery(id+"F102.imprint","IMPRINT",EDGE,{"derivedFrom":sQuery(id+"F102.wireOp",EDGE,"E51.bottom")}),-1.0]])]});
            extrude(context, id + "F103", {"entities" : qUnion([Q0]), "operationType" : NewBodyOperationType.ADD, "oppositeDirection" : true, "depth" : 19.05 * mm});
        }
        {
            var Q0;
            Q0=makeQuery(id+"F103.boolean.opBoolean","MERGE",FACE,{"derivedFrom":[makeQuery(id+"F101.opExtrude","CAP_FACE",FACE,{"disambiguationData":[OSD([sQuery(id+"F100.wireOp",EDGE,"E50.bottom"),sQuery(id+"F100.wireOp",EDGE,"E50.top"),sQuery(id+"F100.wireOp",EDGE,"E50.left"),sQuery(id+"F100.wireOp",EDGE,"E50.right")])],"isStart":false}),makeQuery(id+"F103.opExtrude","SWEPT_FACE",FACE,{"disambiguationData":[OSD([sQuery(id+"F102.wireOp",EDGE,"E51.bottom")])]})]});
            var sketch = newSketch(context, id + "F104", { "sketchPlane" : qUnion([Q0])});
            skLineSegment(sketch, "E52.bottom", {"start": v(-52, 51.79) * mm, "end": v(-58.34, 51.79) * mm});
            skLineSegment(sketch, "E52.top", {"start": v(-52, 58.14) * mm, "end": v(-58.34, 58.14) * mm});
            skLineSegment(sketch, "E52.left", {"start": v(-52, 51.79) * mm, "end": v(-52, 58.14) * mm});
            skLineSegment(sketch, "E52.right", {"start": v(-58.34, 51.79) * mm, "end": v(-58.34, 58.14) * mm});
            skSolve(sketch);
        }
        {
            var Q0;
            Q0=makeQuery(id+"F104.imprint","IMPRINT",FACE,{"disambiguationData":[TD([[makeQuery(id+"F104.imprint","IMPRINT",EDGE,{"derivedFrom":sQuery(id+"F104.wireOp",EDGE,"E52.bottom")}),-1.0]])]});
            extrude(context, id + "F105", {"entities" : qUnion([Q0]), "operationType" : NewBodyOperationType.ADD, "oppositeDirection" : true, "depth" : 19.05 * mm});
        }
        {
            var Q0;
            Q0=makeQuery(id+"F105.boolean.opBoolean","MERGE",FACE,{"derivedFrom":[makeQuery(id+"F103.boolean.opBoolean","MERGE",FACE,{"derivedFrom":[makeQuery(id+"F101.opExtrude","SWEPT_FACE",FACE,{"disambiguationData":[OSD([sQuery(id+"F100.wireOp",EDGE,"E50.right")])]}),makeQuery(id+"F103.opExtrude","SWEPT_FACE",FACE,{"disambiguationData":[OSD([sQuery(id+"F102.wireOp",EDGE,"E51.right")])]})]}),makeQuery(id+"F105.opExtrude","SWEPT_FACE",FACE,{"disambiguationData":[OSD([sQuery(id+"F104.wireOp",EDGE,"E52.left")])]})]});
            var sketch = newSketch(context, id + "F106", { "sketchPlane" : qUnion([Q0])});
            skLineSegment(sketch, "E53.bottom", {"start": v(-51.79, 44.45) * mm, "end": v(-58.14, 44.45) * mm});
            skLineSegment(sketch, "E53.top", {"start": v(-51.79, 38.1) * mm, "end": v(-58.14, 38.1) * mm});
            skLineSegment(sketch, "E53.left", {"start": v(-51.79, 44.45) * mm, "end": v(-51.79, 38.1) * mm});
            skLineSegment(sketch, "E53.right", {"start": v(-58.14, 44.45) * mm, "end": v(-58.14, 38.1) * mm});
            skSolve(sketch);
        }
        {
            var Q0;
            Q0=makeQuery(id+"F106.imprint","IMPRINT",FACE,{"disambiguationData":[TD([[makeQuery(id+"F106.imprint","IMPRINT",EDGE,{"derivedFrom":sQuery(id+"F106.wireOp",EDGE,"E53.bottom")}),-1.0]])]});
            extrude(context, id + "F107", {"entities" : qUnion([Q0]), "operationType" : NewBodyOperationType.ADD, "oppositeDirection" : true, "depth" : 19.05 * mm});
        }
        {
            var Q0;
            Q0=makeQuery(id+"F107.boolean.opBoolean","MERGE",FACE,{"derivedFrom":[makeQuery(id+"F105.opExtrude","CAP_FACE",FACE,{"disambiguationData":[OSD([sQuery(id+"F104.wireOp",EDGE,"E52.bottom"),sQuery(id+"F104.wireOp",EDGE,"E52.top"),sQuery(id+"F104.wireOp",EDGE,"E52.left"),sQuery(id+"F104.wireOp",EDGE,"E52.right")])],"isStart":false}),makeQuery(id+"F107.opExtrude","SWEPT_FACE",FACE,{"disambiguationData":[OSD([sQuery(id+"F106.wireOp",EDGE,"E53.bottom")])]})]});
            var sketch = newSketch(context, id + "F108", { "sketchPlane" : qUnion([Q0])});
            skLineSegment(sketch, "E54.bottom", {"start": v(-71.04, -58.14) * mm, "end": v(-64.7, -58.14) * mm});
            skLineSegment(sketch, "E54.top", {"start": v(-71.04, -51.79) * mm, "end": v(-64.7, -51.79) * mm});
            skLineSegment(sketch, "E54.left", {"start": v(-71.04, -58.14) * mm, "end": v(-71.04, -51.79) * mm});
            skLineSegment(sketch, "E54.right", {"start": v(-64.7, -58.14) * mm, "end": v(-64.7, -51.79) * mm});
            skSolve(sketch);
        }
        {
            var Q0;
            Q0=makeQuery(id+"F108.imprint","IMPRINT",FACE,{"disambiguationData":[TD([[makeQuery(id+"F108.imprint","IMPRINT",EDGE,{"derivedFrom":sQuery(id+"F108.wireOp",EDGE,"E54.bottom")}),-1.0]])]});
            extrude(context, id + "F109", {"entities" : qUnion([Q0]), "operationType" : NewBodyOperationType.ADD, "oppositeDirection" : true, "depth" : 19.05 * mm});
        }
        {
            var Q0;
            Q0=makeQuery(id+"F109.boolean.opBoolean","MERGE",FACE,{"derivedFrom":[makeQuery(id+"F107.boolean.opBoolean","MERGE",FACE,{"derivedFrom":[makeQuery(id+"F105.boolean.opBoolean","MERGE",FACE,{"derivedFrom":[makeQuery(id+"F103.opExtrude","CAP_FACE",FACE,{"disambiguationData":[OSD([sQuery(id+"F102.wireOp",EDGE,"E51.bottom"),sQuery(id+"F102.wireOp",EDGE,"E51.top"),sQuery(id+"F102.wireOp",EDGE,"E51.left"),sQuery(id+"F102.wireOp",EDGE,"E51.right")])],"isStart":false}),makeQuery(id+"F105.opExtrude","SWEPT_FACE",FACE,{"disambiguationData":[OSD([sQuery(id+"F104.wireOp",EDGE,"E52.bottom")])]})]}),makeQuery(id+"F107.opExtrude","SWEPT_FACE",FACE,{"disambiguationData":[OSD([sQuery(id+"F106.wireOp",EDGE,"E53.left")])]})]}),makeQuery(id+"F109.opExtrude","SWEPT_FACE",FACE,{"disambiguationData":[OSD([sQuery(id+"F108.wireOp",EDGE,"E54.top")])]})]});
            var sketch = newSketch(context, id + "F110", { "sketchPlane" : qUnion([Q0])});
            skLineSegment(sketch, "E55.bottom", {"start": v(71.04, 25.4) * mm, "end": v(64.7, 25.4) * mm});
            skLineSegment(sketch, "E55.top", {"start": v(71.04, 31.75) * mm, "end": v(64.7, 31.75) * mm});
            skLineSegment(sketch, "E55.left", {"start": v(71.04, 25.4) * mm, "end": v(71.04, 31.75) * mm});
            skLineSegment(sketch, "E55.right", {"start": v(64.7, 25.4) * mm, "end": v(64.7, 31.75) * mm});
            skSolve(sketch);
        }
        {
            var Q0;
            Q0=makeQuery(id+"F110.imprint","IMPRINT",FACE,{"disambiguationData":[TD([[makeQuery(id+"F110.imprint","IMPRINT",EDGE,{"derivedFrom":sQuery(id+"F110.wireOp",EDGE,"E55.bottom")}),1.0]])]});
            extrude(context, id + "F111", {"entities" : qUnion([Q0]), "operationType" : NewBodyOperationType.ADD, "oppositeDirection" : true, "depth" : 19.05 * mm});
        }
        {
            var Q0;
            Q0=makeQuery(id+"F111.boolean.opBoolean","MERGE",FACE,{"derivedFrom":[makeQuery(id+"F109.opExtrude","CAP_FACE",FACE,{"disambiguationData":[OSD([sQuery(id+"F108.wireOp",EDGE,"E54.bottom"),sQuery(id+"F108.wireOp",EDGE,"E54.top"),sQuery(id+"F108.wireOp",EDGE,"E54.left"),sQuery(id+"F108.wireOp",EDGE,"E54.right")])],"isStart":false}),makeQuery(id+"F111.opExtrude","SWEPT_FACE",FACE,{"disambiguationData":[OSD([sQuery(id+"F110.wireOp",EDGE,"E55.bottom")])]})]});
            var sketch = newSketch(context, id + "F112", { "sketchPlane" : qUnion([Q0])});
            skLineSegment(sketch, "E56.bottom", {"start": v(-71.04, 70.84) * mm, "end": v(-64.7, 70.84) * mm});
            skLineSegment(sketch, "E56.top", {"start": v(-71.04, 64.49) * mm, "end": v(-64.7, 64.49) * mm});
            skLineSegment(sketch, "E56.left", {"start": v(-71.04, 70.84) * mm, "end": v(-71.04, 64.49) * mm});
            skLineSegment(sketch, "E56.right", {"start": v(-64.7, 70.84) * mm, "end": v(-64.7, 64.49) * mm});
            skSolve(sketch);
        }
        {
            var Q0;
            Q0=makeQuery(id+"F112.imprint","IMPRINT",FACE,{"disambiguationData":[TD([[makeQuery(id+"F112.imprint","IMPRINT",EDGE,{"derivedFrom":sQuery(id+"F112.wireOp",EDGE,"E56.bottom")}),1.0]])]});
            extrude(context, id + "F113", {"entities" : qUnion([Q0]), "operationType" : NewBodyOperationType.ADD, "oppositeDirection" : true, "depth" : 31.75 * mm});
        }
        {
            var Q0;
            Q0=makeQuery(id+"F113.boolean.opBoolean","MERGE",FACE,{"derivedFrom":[makeQuery(id+"F111.opExtrude","CAP_FACE",FACE,{"disambiguationData":[OSD([sQuery(id+"F110.wireOp",EDGE,"E55.bottom"),sQuery(id+"F110.wireOp",EDGE,"E55.top"),sQuery(id+"F110.wireOp",EDGE,"E55.left"),sQuery(id+"F110.wireOp",EDGE,"E55.right")])],"isStart":false}),makeQuery(id+"F113.opExtrude","SWEPT_FACE",FACE,{"disambiguationData":[OSD([sQuery(id+"F112.wireOp",EDGE,"E56.bottom")])]})]});
            var sketch = newSketch(context, id + "F114", { "sketchPlane" : qUnion([Q0])});
            skLineSegment(sketch, "E57.bottom", {"start": v(-64.7, 57.15) * mm, "end": v(-71.04, 57.15) * mm});
            skLineSegment(sketch, "E57.top", {"start": v(-64.7, 50.8) * mm, "end": v(-71.04, 50.8) * mm});
            skLineSegment(sketch, "E57.left", {"start": v(-64.7, 57.15) * mm, "end": v(-64.7, 50.8) * mm});
            skLineSegment(sketch, "E57.right", {"start": v(-71.04, 57.15) * mm, "end": v(-71.04, 50.8) * mm});
            skSolve(sketch);
        }
        {
            var Q0;
            Q0=makeQuery(id+"F114.imprint","IMPRINT",FACE,{"disambiguationData":[TD([[makeQuery(id+"F114.imprint","IMPRINT",EDGE,{"derivedFrom":sQuery(id+"F114.wireOp",EDGE,"E57.bottom")}),1.0]])]});
            extrude(context, id + "F115", {"entities" : qUnion([Q0]), "operationType" : NewBodyOperationType.ADD, "oppositeDirection" : true, "depth" : 19.05 * mm});
        }
        {
            var Q0;
            Q0=makeQuery(id+"F115.boolean.opBoolean","MERGE",FACE,{"derivedFrom":[makeQuery(id+"F113.boolean.opBoolean","MERGE",FACE,{"derivedFrom":[makeQuery(id+"F111.boolean.opBoolean","MERGE",FACE,{"derivedFrom":[makeQuery(id+"F109.boolean.opBoolean","MERGE",FACE,{"derivedFrom":[makeQuery(id+"F107.opExtrude","CAP_FACE",FACE,{"disambiguationData":[OSD([sQuery(id+"F106.wireOp",EDGE,"E53.bottom"),sQuery(id+"F106.wireOp",EDGE,"E53.top"),sQuery(id+"F106.wireOp",EDGE,"E53.left"),sQuery(id+"F106.wireOp",EDGE,"E53.right")])],"isStart":false}),makeQuery(id+"F109.opExtrude","SWEPT_FACE",FACE,{"disambiguationData":[OSD([sQuery(id+"F108.wireOp",EDGE,"E54.left")])]})]}),makeQuery(id+"F111.opExtrude","SWEPT_FACE",FACE,{"disambiguationData":[OSD([sQuery(id+"F110.wireOp",EDGE,"E55.left")])]})]}),makeQuery(id+"F113.opExtrude","SWEPT_FACE",FACE,{"disambiguationData":[OSD([sQuery(id+"F112.wireOp",EDGE,"E56.left")])]})]}),makeQuery(id+"F115.opExtrude","SWEPT_FACE",FACE,{"disambiguationData":[OSD([sQuery(id+"F114.wireOp",EDGE,"E57.right")])]})]});
            var sketch = newSketch(context, id + "F116", { "sketchPlane" : qUnion([Q0])});
            skLineSegment(sketch, "E58.bottom", {"start": v(51.79, 57.15) * mm, "end": v(58.14, 57.15) * mm});
            skLineSegment(sketch, "E58.top", {"start": v(51.79, 50.8) * mm, "end": v(58.14, 50.8) * mm});
            skLineSegment(sketch, "E58.left", {"start": v(51.79, 57.15) * mm, "end": v(51.79, 50.8) * mm});
            skLineSegment(sketch, "E58.right", {"start": v(58.14, 57.15) * mm, "end": v(58.14, 50.8) * mm});
            skSolve(sketch);
        }
        {
            var Q0;
            Q0=makeQuery(id+"F116.imprint","IMPRINT",FACE,{"disambiguationData":[TD([[makeQuery(id+"F116.imprint","IMPRINT",EDGE,{"derivedFrom":sQuery(id+"F116.wireOp",EDGE,"E58.bottom")}),1.0]])]});
            extrude(context, id + "F117", {"entities" : qUnion([Q0]), "operationType" : NewBodyOperationType.ADD, "oppositeDirection" : true, "depth" : 19.05 * mm});
        }
        {
            var Q0;
            Q0=makeQuery(id+"F117.boolean.opBoolean","MERGE",FACE,{"derivedFrom":[makeQuery(id+"F115.opExtrude","CAP_FACE",FACE,{"disambiguationData":[OSD([sQuery(id+"F114.wireOp",EDGE,"E57.bottom"),sQuery(id+"F114.wireOp",EDGE,"E57.top"),sQuery(id+"F114.wireOp",EDGE,"E57.left"),sQuery(id+"F114.wireOp",EDGE,"E57.right")])],"isStart":false}),makeQuery(id+"F117.opExtrude","SWEPT_FACE",FACE,{"disambiguationData":[OSD([sQuery(id+"F116.wireOp",EDGE,"E58.left")])]})]});
            var sketch = newSketch(context, id + "F118", { "sketchPlane" : qUnion([Q0])});
            skLineSegment(sketch, "E59.bottom", {"start": v(52, 57.15) * mm, "end": v(58.34, 57.15) * mm});
            skLineSegment(sketch, "E59.top", {"start": v(52, 50.8) * mm, "end": v(58.34, 50.8) * mm});
            skLineSegment(sketch, "E59.left", {"start": v(52, 57.15) * mm, "end": v(52, 50.8) * mm});
            skLineSegment(sketch, "E59.right", {"start": v(58.34, 57.15) * mm, "end": v(58.34, 50.8) * mm});
            skSolve(sketch);
        }
        {
            var Q0;
            Q0=makeQuery(id+"F118.imprint","IMPRINT",FACE,{"disambiguationData":[TD([[makeQuery(id+"F118.imprint","IMPRINT",EDGE,{"derivedFrom":sQuery(id+"F118.wireOp",EDGE,"E59.bottom")}),-1.0]])]});
            extrude(context, id + "F119", {"entities" : qUnion([Q0]), "operationType" : NewBodyOperationType.ADD, "oppositeDirection" : true, "depth" : 19.05 * mm});
        }
        {
            var Q0;
            Q0=makeQuery(id+"F119.boolean.opBoolean","MERGE",FACE,{"derivedFrom":[makeQuery(id+"F117.boolean.opBoolean","MERGE",FACE,{"derivedFrom":[makeQuery(id+"F115.opExtrude","SWEPT_FACE",FACE,{"disambiguationData":[OSD([sQuery(id+"F114.wireOp",EDGE,"E57.top")])]}),makeQuery(id+"F117.opExtrude","SWEPT_FACE",FACE,{"disambiguationData":[OSD([sQuery(id+"F116.wireOp",EDGE,"E58.top")])]})]}),makeQuery(id+"F119.opExtrude","SWEPT_FACE",FACE,{"disambiguationData":[OSD([sQuery(id+"F118.wireOp",EDGE,"E59.top")])]})]});
            var sketch = newSketch(context, id + "F120", { "sketchPlane" : qUnion([Q0])});
            skLineSegment(sketch, "E60.bottom", {"start": v(-52, 70.84) * mm, "end": v(-58.34, 70.84) * mm});
            skLineSegment(sketch, "E60.top", {"start": v(-52, 64.49) * mm, "end": v(-58.34, 64.49) * mm});
            skLineSegment(sketch, "E60.left", {"start": v(-52, 70.84) * mm, "end": v(-52, 64.49) * mm});
            skLineSegment(sketch, "E60.right", {"start": v(-58.34, 70.84) * mm, "end": v(-58.34, 64.49) * mm});
            skSolve(sketch);
        }
        {
            var Q0;
            Q0=makeQuery(id+"F120.imprint","IMPRINT",FACE,{"disambiguationData":[TD([[makeQuery(id+"F120.imprint","IMPRINT",EDGE,{"derivedFrom":sQuery(id+"F120.wireOp",EDGE,"E60.bottom")}),1.0]])]});
            extrude(context, id + "F121", {"entities" : qUnion([Q0]), "operationType" : NewBodyOperationType.ADD, "oppositeDirection" : true, "depth" : 19.05 * mm});
        }
        {
            var Q0;
            Q0=makeQuery(id+"F121.boolean.opBoolean","MERGE",FACE,{"derivedFrom":[makeQuery(id+"F119.opExtrude","CAP_FACE",FACE,{"disambiguationData":[OSD([sQuery(id+"F118.wireOp",EDGE,"E59.bottom"),sQuery(id+"F118.wireOp",EDGE,"E59.top"),sQuery(id+"F118.wireOp",EDGE,"E59.left"),sQuery(id+"F118.wireOp",EDGE,"E59.right")])],"isStart":false}),makeQuery(id+"F121.opExtrude","SWEPT_FACE",FACE,{"disambiguationData":[OSD([sQuery(id+"F120.wireOp",EDGE,"E60.bottom")])]})]});
            var sketch = newSketch(context, id + "F122", { "sketchPlane" : qUnion([Q0])});
            skLineSegment(sketch, "E61.bottom", {"start": v(-52, 69.85) * mm, "end": v(-58.34, 69.85) * mm});
            skLineSegment(sketch, "E61.top", {"start": v(-52, 63.5) * mm, "end": v(-58.34, 63.5) * mm});
            skLineSegment(sketch, "E61.left", {"start": v(-52, 69.85) * mm, "end": v(-52, 63.5) * mm});
            skLineSegment(sketch, "E61.right", {"start": v(-58.34, 69.85) * mm, "end": v(-58.34, 63.5) * mm});
            skSolve(sketch);
        }
        {
            var Q0;
            Q0=makeQuery(id+"F122.imprint","IMPRINT",FACE,{"disambiguationData":[TD([[makeQuery(id+"F122.imprint","IMPRINT",EDGE,{"derivedFrom":sQuery(id+"F122.wireOp",EDGE,"E61.bottom")}),1.0]])]});
            extrude(context, id + "F123", {"entities" : qUnion([Q0]), "operationType" : NewBodyOperationType.ADD, "oppositeDirection" : true, "depth" : 19.05 * mm});
        }
        {
            var Q0;
            Q0=makeQuery(id+"F123.boolean.opBoolean","MERGE",FACE,{"derivedFrom":[makeQuery(id+"F121.boolean.opBoolean","MERGE",FACE,{"derivedFrom":[makeQuery(id+"F119.boolean.opBoolean","MERGE",FACE,{"derivedFrom":[makeQuery(id+"F117.opExtrude","CAP_FACE",FACE,{"disambiguationData":[OSD([sQuery(id+"F116.wireOp",EDGE,"E58.bottom"),sQuery(id+"F116.wireOp",EDGE,"E58.top"),sQuery(id+"F116.wireOp",EDGE,"E58.left"),sQuery(id+"F116.wireOp",EDGE,"E58.right")])],"isStart":false}),makeQuery(id+"F119.opExtrude","SWEPT_FACE",FACE,{"disambiguationData":[OSD([sQuery(id+"F118.wireOp",EDGE,"E59.left")])]})]}),makeQuery(id+"F121.opExtrude","SWEPT_FACE",FACE,{"disambiguationData":[OSD([sQuery(id+"F120.wireOp",EDGE,"E60.left")])]})]}),makeQuery(id+"F123.opExtrude","SWEPT_FACE",FACE,{"disambiguationData":[OSD([sQuery(id+"F122.wireOp",EDGE,"E61.left")])]})]});
            var sketch = newSketch(context, id + "F124", { "sketchPlane" : qUnion([Q0])});
            skLineSegment(sketch, "E62.bottom", {"start": v(-51.79, 69.85) * mm, "end": v(-58.14, 69.85) * mm});
            skLineSegment(sketch, "E62.top", {"start": v(-51.79, 63.5) * mm, "end": v(-58.14, 63.5) * mm});
            skLineSegment(sketch, "E62.left", {"start": v(-51.79, 69.85) * mm, "end": v(-51.79, 63.5) * mm});
            skLineSegment(sketch, "E62.right", {"start": v(-58.14, 69.85) * mm, "end": v(-58.14, 63.5) * mm});
            skSolve(sketch);
        }
        {
            var Q0;
            Q0=makeQuery(id+"F124.imprint","IMPRINT",FACE,{"disambiguationData":[TD([[makeQuery(id+"F124.imprint","IMPRINT",EDGE,{"derivedFrom":sQuery(id+"F124.wireOp",EDGE,"E62.bottom")}),1.0]])]});
            extrude(context, id + "F125", {"entities" : qUnion([Q0]), "operationType" : NewBodyOperationType.ADD, "oppositeDirection" : true, "depth" : 19.05 * mm});
        }
        {
            var Q0;
            Q0=makeQuery(id+"F125.boolean.opBoolean","MERGE",FACE,{"derivedFrom":[makeQuery(id+"F123.opExtrude","CAP_FACE",FACE,{"disambiguationData":[OSD([sQuery(id+"F122.wireOp",EDGE,"E61.bottom"),sQuery(id+"F122.wireOp",EDGE,"E61.top"),sQuery(id+"F122.wireOp",EDGE,"E61.left"),sQuery(id+"F122.wireOp",EDGE,"E61.right")])],"isStart":false}),makeQuery(id+"F125.opExtrude","SWEPT_FACE",FACE,{"disambiguationData":[OSD([sQuery(id+"F124.wireOp",EDGE,"E62.left")])]})]});
            var sketch = newSketch(context, id + "F126", { "sketchPlane" : qUnion([Q0])});
            skLineSegment(sketch, "E63.bottom", {"start": v(71.04, 63.5) * mm, "end": v(64.7, 63.5) * mm});
            skLineSegment(sketch, "E63.top", {"start": v(71.04, 69.85) * mm, "end": v(64.7, 69.85) * mm});
            skLineSegment(sketch, "E63.left", {"start": v(71.04, 63.5) * mm, "end": v(71.04, 69.85) * mm});
            skLineSegment(sketch, "E63.right", {"start": v(64.7, 63.5) * mm, "end": v(64.7, 69.85) * mm});
            skSolve(sketch);
        }
        {
            var Q0;
            Q0=makeQuery(id+"F126.imprint","IMPRINT",FACE,{"disambiguationData":[TD([[makeQuery(id+"F126.imprint","IMPRINT",EDGE,{"derivedFrom":sQuery(id+"F126.wireOp",EDGE,"E63.bottom")}),1.0]])]});
            extrude(context, id + "F127", {"entities" : qUnion([Q0]), "operationType" : NewBodyOperationType.ADD, "oppositeDirection" : true, "depth" : 19.05 * mm});
        }
        {
            var Q0;
            Q0=makeQuery(id+"F127.boolean.opBoolean","MERGE",FACE,{"derivedFrom":[makeQuery(id+"F125.boolean.opBoolean","MERGE",FACE,{"derivedFrom":[makeQuery(id+"F123.opExtrude","SWEPT_FACE",FACE,{"disambiguationData":[OSD([sQuery(id+"F122.wireOp",EDGE,"E61.top")])]}),makeQuery(id+"F125.opExtrude","SWEPT_FACE",FACE,{"disambiguationData":[OSD([sQuery(id+"F124.wireOp",EDGE,"E62.top")])]})]}),makeQuery(id+"F127.opExtrude","SWEPT_FACE",FACE,{"disambiguationData":[OSD([sQuery(id+"F126.wireOp",EDGE,"E63.bottom")])]})]});
            var sketch = newSketch(context, id + "F128", { "sketchPlane" : qUnion([Q0])});
            skLineSegment(sketch, "E64.bottom", {"start": v(-71.04, 70.84) * mm, "end": v(-64.7, 70.84) * mm});
            skLineSegment(sketch, "E64.top", {"start": v(-71.04, 64.49) * mm, "end": v(-64.7, 64.49) * mm});
            skLineSegment(sketch, "E64.left", {"start": v(-71.04, 70.84) * mm, "end": v(-71.04, 64.49) * mm});
            skLineSegment(sketch, "E64.right", {"start": v(-64.7, 70.84) * mm, "end": v(-64.7, 64.49) * mm});
            skSolve(sketch);
        }
        {
            var Q0;
            Q0=makeQuery(id+"F128.imprint","IMPRINT",FACE,{"disambiguationData":[TD([[makeQuery(id+"F128.imprint","IMPRINT",EDGE,{"derivedFrom":sQuery(id+"F128.wireOp",EDGE,"E64.bottom")}),1.0]])]});
            extrude(context, id + "F129", {"entities" : qUnion([Q0]), "operationType" : NewBodyOperationType.ADD, "oppositeDirection" : true, "depth" : 31.75 * mm});
        }
        {
            var Q0;
            Q0=makeQuery(id+"F129.boolean.opBoolean","MERGE",FACE,{"derivedFrom":[makeQuery(id+"F127.opExtrude","CAP_FACE",FACE,{"disambiguationData":[OSD([sQuery(id+"F126.wireOp",EDGE,"E63.bottom"),sQuery(id+"F126.wireOp",EDGE,"E63.top"),sQuery(id+"F126.wireOp",EDGE,"E63.left"),sQuery(id+"F126.wireOp",EDGE,"E63.right")])],"isStart":false}),makeQuery(id+"F129.opExtrude","SWEPT_FACE",FACE,{"disambiguationData":[OSD([sQuery(id+"F128.wireOp",EDGE,"E64.bottom")])]})]});
            var sketch = newSketch(context, id + "F130", { "sketchPlane" : qUnion([Q0])});
            skLineSegment(sketch, "E65.bottom", {"start": v(-64.7, 95.25) * mm, "end": v(-71.04, 95.25) * mm});
            skLineSegment(sketch, "E65.top", {"start": v(-64.7, 88.9) * mm, "end": v(-71.04, 88.9) * mm});
            skLineSegment(sketch, "E65.left", {"start": v(-64.7, 95.25) * mm, "end": v(-64.7, 88.9) * mm});
            skLineSegment(sketch, "E65.right", {"start": v(-71.04, 95.25) * mm, "end": v(-71.04, 88.9) * mm});
            skSolve(sketch);
        }
        {
            var Q0;
            Q0=makeQuery(id+"F130.imprint","IMPRINT",FACE,{"disambiguationData":[TD([[makeQuery(id+"F130.imprint","IMPRINT",EDGE,{"derivedFrom":sQuery(id+"F130.wireOp",EDGE,"E65.bottom")}),1.0]])]});
            extrude(context, id + "F131", {"entities" : qUnion([Q0]), "operationType" : NewBodyOperationType.ADD, "oppositeDirection" : true, "depth" : 19.05 * mm});
        }
        {
            var Q0;
            Q0=makeQuery(id+"F131.boolean.opBoolean","MERGE",FACE,{"derivedFrom":[makeQuery(id+"F129.opExtrude","CAP_FACE",FACE,{"disambiguationData":[OSD([sQuery(id+"F128.wireOp",EDGE,"E64.bottom"),sQuery(id+"F128.wireOp",EDGE,"E64.top"),sQuery(id+"F128.wireOp",EDGE,"E64.left"),sQuery(id+"F128.wireOp",EDGE,"E64.right")])],"isStart":false}),makeQuery(id+"F131.opExtrude","SWEPT_FACE",FACE,{"disambiguationData":[OSD([sQuery(id+"F130.wireOp",EDGE,"E65.bottom")])]})]});
            var sketch = newSketch(context, id + "F132", { "sketchPlane" : qUnion([Q0])});
            skLineSegment(sketch, "E66.bottom", {"start": v(-71.04, -51.79) * mm, "end": v(-64.7, -51.79) * mm});
            skLineSegment(sketch, "E66.top", {"start": v(-71.04, -58.14) * mm, "end": v(-64.7, -58.14) * mm});
            skLineSegment(sketch, "E66.left", {"start": v(-71.04, -51.79) * mm, "end": v(-71.04, -58.14) * mm});
            skLineSegment(sketch, "E66.right", {"start": v(-64.7, -51.79) * mm, "end": v(-64.7, -58.14) * mm});
            skSolve(sketch);
        }
        {
            var Q0;
            Q0=makeQuery(id+"F132.imprint","IMPRINT",FACE,{"disambiguationData":[TD([[makeQuery(id+"F132.imprint","IMPRINT",EDGE,{"derivedFrom":sQuery(id+"F132.wireOp",EDGE,"E66.bottom")}),1.0]])]});
            extrude(context, id + "F133", {"entities" : qUnion([Q0]), "operationType" : NewBodyOperationType.ADD, "oppositeDirection" : true, "depth" : 19.05 * mm});
        }
        {
            var Q0;
            Q0=makeQuery(id+"F133.boolean.opBoolean","MERGE",FACE,{"derivedFrom":[makeQuery(id+"F131.boolean.opBoolean","MERGE",FACE,{"derivedFrom":[makeQuery(id+"F129.boolean.opBoolean","MERGE",FACE,{"derivedFrom":[makeQuery(id+"F127.boolean.opBoolean","MERGE",FACE,{"derivedFrom":[makeQuery(id+"F125.opExtrude","CAP_FACE",FACE,{"disambiguationData":[OSD([sQuery(id+"F124.wireOp",EDGE,"E62.bottom"),sQuery(id+"F124.wireOp",EDGE,"E62.top"),sQuery(id+"F124.wireOp",EDGE,"E62.left"),sQuery(id+"F124.wireOp",EDGE,"E62.right")])],"isStart":false}),makeQuery(id+"F127.opExtrude","SWEPT_FACE",FACE,{"disambiguationData":[OSD([sQuery(id+"F126.wireOp",EDGE,"E63.left")])]})]}),makeQuery(id+"F129.opExtrude","SWEPT_FACE",FACE,{"disambiguationData":[OSD([sQuery(id+"F128.wireOp",EDGE,"E64.left")])]})]}),makeQuery(id+"F131.opExtrude","SWEPT_FACE",FACE,{"disambiguationData":[OSD([sQuery(id+"F130.wireOp",EDGE,"E65.right")])]})]}),makeQuery(id+"F133.opExtrude","SWEPT_FACE",FACE,{"disambiguationData":[OSD([sQuery(id+"F132.wireOp",EDGE,"E66.left")])]})]});
            var sketch = newSketch(context, id + "F134", { "sketchPlane" : qUnion([Q0])});
            skLineSegment(sketch, "E67.bottom", {"start": v(51.79, 76.2) * mm, "end": v(58.14, 76.2) * mm});
            skLineSegment(sketch, "E67.top", {"start": v(51.79, 82.55) * mm, "end": v(58.14, 82.55) * mm});
            skLineSegment(sketch, "E67.left", {"start": v(51.79, 76.2) * mm, "end": v(51.79, 82.55) * mm});
            skLineSegment(sketch, "E67.right", {"start": v(58.14, 76.2) * mm, "end": v(58.14, 82.55) * mm});
            skSolve(sketch);
        }
        {
            var Q0;
            Q0=makeQuery(id+"F134.imprint","IMPRINT",FACE,{"disambiguationData":[TD([[makeQuery(id+"F134.imprint","IMPRINT",EDGE,{"derivedFrom":sQuery(id+"F134.wireOp",EDGE,"E67.bottom")}),1.0]])]});
            extrude(context, id + "F135", {"entities" : qUnion([Q0]), "operationType" : NewBodyOperationType.ADD, "oppositeDirection" : true, "depth" : 19.05 * mm});
        }
        {
            var Q0;
            Q0=makeQuery(id+"F135.boolean.opBoolean","MERGE",FACE,{"derivedFrom":[makeQuery(id+"F133.opExtrude","CAP_FACE",FACE,{"disambiguationData":[OSD([sQuery(id+"F132.wireOp",EDGE,"E66.bottom"),sQuery(id+"F132.wireOp",EDGE,"E66.top"),sQuery(id+"F132.wireOp",EDGE,"E66.left"),sQuery(id+"F132.wireOp",EDGE,"E66.right")])],"isStart":false}),makeQuery(id+"F135.opExtrude","SWEPT_FACE",FACE,{"disambiguationData":[OSD([sQuery(id+"F134.wireOp",EDGE,"E67.bottom")])]})]});
            var sketch = newSketch(context, id + "F136", { "sketchPlane" : qUnion([Q0])});
            skLineSegment(sketch, "E68.bottom", {"start": v(-52, 51.79) * mm, "end": v(-58.34, 51.79) * mm});
            skLineSegment(sketch, "E68.top", {"start": v(-52, 58.14) * mm, "end": v(-58.34, 58.14) * mm});
            skLineSegment(sketch, "E68.left", {"start": v(-52, 51.79) * mm, "end": v(-52, 58.14) * mm});
            skLineSegment(sketch, "E68.right", {"start": v(-58.34, 51.79) * mm, "end": v(-58.34, 58.14) * mm});
            skSolve(sketch);
        }
        {
            var Q0;
            Q0=makeQuery(id+"F136.imprint","IMPRINT",FACE,{"disambiguationData":[TD([[makeQuery(id+"F136.imprint","IMPRINT",EDGE,{"derivedFrom":sQuery(id+"F136.wireOp",EDGE,"E68.bottom")}),-1.0]])]});
            extrude(context, id + "F137", {"entities" : qUnion([Q0]), "operationType" : NewBodyOperationType.ADD, "oppositeDirection" : true, "depth" : 19.05 * mm});
        }
        {
            var Q0;
            Q0=makeQuery(id+"F137.boolean.opBoolean","MERGE",FACE,{"derivedFrom":[makeQuery(id+"F135.boolean.opBoolean","MERGE",FACE,{"derivedFrom":[makeQuery(id+"F133.boolean.opBoolean","MERGE",FACE,{"derivedFrom":[makeQuery(id+"F131.opExtrude","CAP_FACE",FACE,{"disambiguationData":[OSD([sQuery(id+"F130.wireOp",EDGE,"E65.bottom"),sQuery(id+"F130.wireOp",EDGE,"E65.top"),sQuery(id+"F130.wireOp",EDGE,"E65.left"),sQuery(id+"F130.wireOp",EDGE,"E65.right")])],"isStart":false}),makeQuery(id+"F133.opExtrude","SWEPT_FACE",FACE,{"disambiguationData":[OSD([sQuery(id+"F132.wireOp",EDGE,"E66.bottom")])]})]}),makeQuery(id+"F135.opExtrude","SWEPT_FACE",FACE,{"disambiguationData":[OSD([sQuery(id+"F134.wireOp",EDGE,"E67.left")])]})]}),makeQuery(id+"F137.opExtrude","SWEPT_FACE",FACE,{"disambiguationData":[OSD([sQuery(id+"F136.wireOp",EDGE,"E68.bottom")])]})]});
            var sketch = newSketch(context, id + "F138", { "sketchPlane" : qUnion([Q0])});
            skLineSegment(sketch, "E69.bottom", {"start": v(52, 95.25) * mm, "end": v(58.34, 95.25) * mm});
            skLineSegment(sketch, "E69.top", {"start": v(52, 88.9) * mm, "end": v(58.34, 88.9) * mm});
            skLineSegment(sketch, "E69.left", {"start": v(52, 95.25) * mm, "end": v(52, 88.9) * mm});
            skLineSegment(sketch, "E69.right", {"start": v(58.34, 95.25) * mm, "end": v(58.34, 88.9) * mm});
            skSolve(sketch);
        }
        {
            var Q0;
            Q0=makeQuery(id+"F138.imprint","IMPRINT",FACE,{"disambiguationData":[TD([[makeQuery(id+"F138.imprint","IMPRINT",EDGE,{"derivedFrom":sQuery(id+"F138.wireOp",EDGE,"E69.bottom")}),-1.0]])]});
            extrude(context, id + "F139", {"entities" : qUnion([Q0]), "operationType" : NewBodyOperationType.ADD, "oppositeDirection" : true, "depth" : 19.05 * mm});
        }
        {
            var Q0;
            Q0=makeQuery(id+"F139.boolean.opBoolean","MERGE",FACE,{"derivedFrom":[makeQuery(id+"F137.opExtrude","CAP_FACE",FACE,{"disambiguationData":[OSD([sQuery(id+"F136.wireOp",EDGE,"E68.bottom"),sQuery(id+"F136.wireOp",EDGE,"E68.top"),sQuery(id+"F136.wireOp",EDGE,"E68.left"),sQuery(id+"F136.wireOp",EDGE,"E68.right")])],"isStart":false}),makeQuery(id+"F139.opExtrude","SWEPT_FACE",FACE,{"disambiguationData":[OSD([sQuery(id+"F138.wireOp",EDGE,"E69.bottom")])]})]});
            var sketch = newSketch(context, id + "F140", { "sketchPlane" : qUnion([Q0])});
            skLineSegment(sketch, "E70.bottom", {"start": v(-52, -70.84) * mm, "end": v(-58.34, -70.84) * mm});
            skLineSegment(sketch, "E70.top", {"start": v(-52, -64.49) * mm, "end": v(-58.34, -64.49) * mm});
            skLineSegment(sketch, "E70.left", {"start": v(-52, -70.84) * mm, "end": v(-52, -64.49) * mm});
            skLineSegment(sketch, "E70.right", {"start": v(-58.34, -70.84) * mm, "end": v(-58.34, -64.49) * mm});
            skSolve(sketch);
        }
        {
            var Q0;
            Q0=makeQuery(id+"F140.imprint","IMPRINT",FACE,{"disambiguationData":[TD([[makeQuery(id+"F140.imprint","IMPRINT",EDGE,{"derivedFrom":sQuery(id+"F140.wireOp",EDGE,"E70.bottom")}),-1.0]])]});
            extrude(context, id + "F141", {"entities" : qUnion([Q0]), "operationType" : NewBodyOperationType.ADD, "oppositeDirection" : true, "depth" : 19.05 * mm});
        }
        {
            var Q0;
            Q0=makeQuery(id+"F141.boolean.opBoolean","MERGE",FACE,{"derivedFrom":[makeQuery(id+"F139.boolean.opBoolean","MERGE",FACE,{"derivedFrom":[makeQuery(id+"F137.opExtrude","SWEPT_FACE",FACE,{"disambiguationData":[OSD([sQuery(id+"F136.wireOp",EDGE,"E68.right")])]}),makeQuery(id+"F139.opExtrude","SWEPT_FACE",FACE,{"disambiguationData":[OSD([sQuery(id+"F138.wireOp",EDGE,"E69.right")])]})]}),makeQuery(id+"F141.opExtrude","SWEPT_FACE",FACE,{"disambiguationData":[OSD([sQuery(id+"F140.wireOp",EDGE,"E70.right")])]})]});
            var sketch = newSketch(context, id + "F142", { "sketchPlane" : qUnion([Q0])});
            skLineSegment(sketch, "E71.bottom", {"start": v(70.84, 76.2) * mm, "end": v(64.49, 76.2) * mm});
            skLineSegment(sketch, "E71.top", {"start": v(70.84, 82.55) * mm, "end": v(64.49, 82.55) * mm});
            skLineSegment(sketch, "E71.left", {"start": v(70.84, 76.2) * mm, "end": v(70.84, 82.55) * mm});
            skLineSegment(sketch, "E71.right", {"start": v(64.49, 76.2) * mm, "end": v(64.49, 82.55) * mm});
            skSolve(sketch);
        }
        {
            var Q0;
            Q0=makeQuery(id+"F142.imprint","IMPRINT",FACE,{"disambiguationData":[TD([[makeQuery(id+"F142.imprint","IMPRINT",EDGE,{"derivedFrom":sQuery(id+"F142.wireOp",EDGE,"E71.bottom")}),1.0]])]});
            extrude(context, id + "F143", {"entities" : qUnion([Q0]), "operationType" : NewBodyOperationType.ADD, "oppositeDirection" : true, "depth" : 19.05 * mm});
        }
        {
            var Q0;
            Q0=makeQuery(id+"F143.boolean.opBoolean","MERGE",FACE,{"derivedFrom":[makeQuery(id+"F141.opExtrude","CAP_FACE",FACE,{"disambiguationData":[OSD([sQuery(id+"F140.wireOp",EDGE,"E70.bottom"),sQuery(id+"F140.wireOp",EDGE,"E70.top"),sQuery(id+"F140.wireOp",EDGE,"E70.left"),sQuery(id+"F140.wireOp",EDGE,"E70.right")])],"isStart":false}),makeQuery(id+"F143.opExtrude","SWEPT_FACE",FACE,{"disambiguationData":[OSD([sQuery(id+"F142.wireOp",EDGE,"E71.bottom")])]})]});
            var sketch = newSketch(context, id + "F144", { "sketchPlane" : qUnion([Q0])});
            skLineSegment(sketch, "E72.bottom", {"start": v(-39.3, 70.84) * mm, "end": v(-45.64, 70.84) * mm});
            skLineSegment(sketch, "E72.top", {"start": v(-39.3, 64.49) * mm, "end": v(-45.64, 64.49) * mm});
            skLineSegment(sketch, "E72.left", {"start": v(-39.3, 70.84) * mm, "end": v(-39.3, 64.49) * mm});
            skLineSegment(sketch, "E72.right", {"start": v(-45.64, 70.84) * mm, "end": v(-45.64, 64.49) * mm});
            skSolve(sketch);
        }
        {
            var Q0;
            Q0=makeQuery(id+"F144.imprint","IMPRINT",FACE,{"disambiguationData":[TD([[makeQuery(id+"F144.imprint","IMPRINT",EDGE,{"derivedFrom":sQuery(id+"F144.wireOp",EDGE,"E72.bottom")}),1.0]])]});
            extrude(context, id + "F145", {"entities" : qUnion([Q0]), "operationType" : NewBodyOperationType.ADD, "oppositeDirection" : true, "depth" : 19.05 * mm});
        }
        {
            var Q0;
            Q0=makeQuery(id+"F145.opExtrude","SWEPT_FACE",FACE,{"disambiguationData":[OSD([sQuery(id+"F144.wireOp",EDGE,"E72.right")])]});
            var sketch = newSketch(context, id + "F146", { "sketchPlane" : qUnion([Q0])});
            skLineSegment(sketch, "E73.bottom", {"start": v(70.84, 95.25) * mm, "end": v(64.49, 95.25) * mm});
            skLineSegment(sketch, "E73.top", {"start": v(70.84, 88.9) * mm, "end": v(64.49, 88.9) * mm});
            skLineSegment(sketch, "E73.left", {"start": v(70.84, 95.25) * mm, "end": v(70.84, 88.9) * mm});
            skLineSegment(sketch, "E73.right", {"start": v(64.49, 95.25) * mm, "end": v(64.49, 88.9) * mm});
            skSolve(sketch);
        }
        {
            var Q0;
            Q0=makeQuery(id+"F146.imprint","IMPRINT",FACE,{"disambiguationData":[TD([[makeQuery(id+"F146.imprint","IMPRINT",EDGE,{"derivedFrom":sQuery(id+"F146.wireOp",EDGE,"E73.bottom")}),1.0]])]});
            extrude(context, id + "F147", {"entities" : qUnion([Q0]), "operationType" : NewBodyOperationType.ADD, "oppositeDirection" : true, "depth" : 19.05 * mm});
        }
        {
            var Q0;
            Q0=makeQuery(id+"F147.boolean.opBoolean","MERGE",FACE,{"derivedFrom":[makeQuery(id+"F145.opExtrude","CAP_FACE",FACE,{"disambiguationData":[OSD([sQuery(id+"F144.wireOp",EDGE,"E72.bottom"),sQuery(id+"F144.wireOp",EDGE,"E72.top"),sQuery(id+"F144.wireOp",EDGE,"E72.left"),sQuery(id+"F144.wireOp",EDGE,"E72.right")])],"isStart":false}),makeQuery(id+"F147.opExtrude","SWEPT_FACE",FACE,{"disambiguationData":[OSD([sQuery(id+"F146.wireOp",EDGE,"E73.bottom")])]})]});
            var sketch = newSketch(context, id + "F148", { "sketchPlane" : qUnion([Q0])});
            skLineSegment(sketch, "E74.bottom", {"start": v(-26.6, -64.49) * mm, "end": v(-32.94, -64.49) * mm});
            skLineSegment(sketch, "E74.top", {"start": v(-26.6, -70.84) * mm, "end": v(-32.94, -70.84) * mm});
            skLineSegment(sketch, "E74.left", {"start": v(-26.6, -64.49) * mm, "end": v(-26.6, -70.84) * mm});
            skLineSegment(sketch, "E74.right", {"start": v(-32.94, -64.49) * mm, "end": v(-32.94, -70.84) * mm});
            skSolve(sketch);
        }
        {
            var Q0;
            Q0=makeQuery(id+"F148.imprint","IMPRINT",FACE,{"disambiguationData":[TD([[makeQuery(id+"F148.imprint","IMPRINT",EDGE,{"derivedFrom":sQuery(id+"F148.wireOp",EDGE,"E74.bottom")}),1.0]])]});
            extrude(context, id + "F149", {"entities" : qUnion([Q0]), "operationType" : NewBodyOperationType.ADD, "oppositeDirection" : true, "depth" : 19.05 * mm});
        }
        {
            var Q0;
            Q0=makeQuery(id+"F149.boolean.opBoolean","MERGE",FACE,{"derivedFrom":[makeQuery(id+"F147.boolean.opBoolean","MERGE",FACE,{"derivedFrom":[makeQuery(id+"F145.boolean.opBoolean","MERGE",FACE,{"derivedFrom":[makeQuery(id+"F143.boolean.opBoolean","MERGE",FACE,{"derivedFrom":[makeQuery(id+"F141.boolean.opBoolean","MERGE",FACE,{"derivedFrom":[makeQuery(id+"F139.opExtrude","CAP_FACE",FACE,{"disambiguationData":[OSD([sQuery(id+"F138.wireOp",EDGE,"E69.bottom"),sQuery(id+"F138.wireOp",EDGE,"E69.top"),sQuery(id+"F138.wireOp",EDGE,"E69.left"),sQuery(id+"F138.wireOp",EDGE,"E69.right")])],"isStart":false}),makeQuery(id+"F141.opExtrude","SWEPT_FACE",FACE,{"disambiguationData":[OSD([sQuery(id+"F140.wireOp",EDGE,"E70.bottom")])]})]}),makeQuery(id+"F143.opExtrude","SWEPT_FACE",FACE,{"disambiguationData":[OSD([sQuery(id+"F142.wireOp",EDGE,"E71.left")])]})]}),makeQuery(id+"F145.opExtrude","SWEPT_FACE",FACE,{"disambiguationData":[OSD([sQuery(id+"F144.wireOp",EDGE,"E72.bottom")])]})]}),makeQuery(id+"F147.opExtrude","SWEPT_FACE",FACE,{"disambiguationData":[OSD([sQuery(id+"F146.wireOp",EDGE,"E73.left")])]})]}),makeQuery(id+"F149.opExtrude","SWEPT_FACE",FACE,{"disambiguationData":[OSD([sQuery(id+"F148.wireOp",EDGE,"E74.top")])]})]});
            var sketch = newSketch(context, id + "F150", { "sketchPlane" : qUnion([Q0])});
            skLineSegment(sketch, "E75.bottom", {"start": v(-26.6, 76.2) * mm, "end": v(-32.94, 76.2) * mm});
            skLineSegment(sketch, "E75.top", {"start": v(-26.6, 82.55) * mm, "end": v(-32.94, 82.55) * mm});
            skLineSegment(sketch, "E75.left", {"start": v(-26.6, 76.2) * mm, "end": v(-26.6, 82.55) * mm});
            skLineSegment(sketch, "E75.right", {"start": v(-32.94, 76.2) * mm, "end": v(-32.94, 82.55) * mm});
            skSolve(sketch);
        }
        {
            var Q0;
            Q0=makeQuery(id+"F150.imprint","IMPRINT",FACE,{"disambiguationData":[TD([[makeQuery(id+"F150.imprint","IMPRINT",EDGE,{"derivedFrom":sQuery(id+"F150.wireOp",EDGE,"E75.bottom")}),-1.0]])]});
            extrude(context, id + "F151", {"entities" : qUnion([Q0]), "operationType" : NewBodyOperationType.ADD, "oppositeDirection" : true, "depth" : 19.05 * mm});
        }
        {
            var Q0;
            Q0=makeQuery(id+"F151.boolean.opBoolean","MERGE",FACE,{"derivedFrom":[makeQuery(id+"F149.opExtrude","CAP_FACE",FACE,{"disambiguationData":[OSD([sQuery(id+"F148.wireOp",EDGE,"E74.bottom"),sQuery(id+"F148.wireOp",EDGE,"E74.top"),sQuery(id+"F148.wireOp",EDGE,"E74.left"),sQuery(id+"F148.wireOp",EDGE,"E74.right")])],"isStart":false}),makeQuery(id+"F151.opExtrude","SWEPT_FACE",FACE,{"disambiguationData":[OSD([sQuery(id+"F150.wireOp",EDGE,"E75.bottom")])]})]});
            var sketch = newSketch(context, id + "F152", { "sketchPlane" : qUnion([Q0])});
            skLineSegment(sketch, "E76.bottom", {"start": v(-26.6, 51.79) * mm, "end": v(-32.94, 51.79) * mm});
            skLineSegment(sketch, "E76.top", {"start": v(-26.6, 58.14) * mm, "end": v(-32.94, 58.14) * mm});
            skLineSegment(sketch, "E76.left", {"start": v(-26.6, 51.79) * mm, "end": v(-26.6, 58.14) * mm});
            skLineSegment(sketch, "E76.right", {"start": v(-32.94, 51.79) * mm, "end": v(-32.94, 58.14) * mm});
            skSolve(sketch);
        }
        {
            var Q0;
            Q0=makeQuery(id+"F152.imprint","IMPRINT",FACE,{"disambiguationData":[TD([[makeQuery(id+"F152.imprint","IMPRINT",EDGE,{"derivedFrom":sQuery(id+"F152.wireOp",EDGE,"E76.bottom")}),-1.0]])]});
            extrude(context, id + "F153", {"entities" : qUnion([Q0]), "operationType" : NewBodyOperationType.ADD, "oppositeDirection" : true, "depth" : 19.05 * mm});
        }
        {
            var Q0;
            Q0=makeQuery(id+"F153.boolean.opBoolean","MERGE",FACE,{"derivedFrom":[makeQuery(id+"F151.boolean.opBoolean","MERGE",FACE,{"derivedFrom":[makeQuery(id+"F149.boolean.opBoolean","MERGE",FACE,{"derivedFrom":[makeQuery(id+"F147.opExtrude","CAP_FACE",FACE,{"disambiguationData":[OSD([sQuery(id+"F146.wireOp",EDGE,"E73.bottom"),sQuery(id+"F146.wireOp",EDGE,"E73.top"),sQuery(id+"F146.wireOp",EDGE,"E73.left"),sQuery(id+"F146.wireOp",EDGE,"E73.right")])],"isStart":false}),makeQuery(id+"F149.opExtrude","SWEPT_FACE",FACE,{"disambiguationData":[OSD([sQuery(id+"F148.wireOp",EDGE,"E74.left")])]})]}),makeQuery(id+"F151.opExtrude","SWEPT_FACE",FACE,{"disambiguationData":[OSD([sQuery(id+"F150.wireOp",EDGE,"E75.left")])]})]}),makeQuery(id+"F153.opExtrude","SWEPT_FACE",FACE,{"disambiguationData":[OSD([sQuery(id+"F152.wireOp",EDGE,"E76.left")])]})]});
            var sketch = newSketch(context, id + "F154", { "sketchPlane" : qUnion([Q0])});
            skLineSegment(sketch, "E77.bottom", {"start": v(-51.79, 95.25) * mm, "end": v(-58.14, 95.25) * mm});
            skLineSegment(sketch, "E77.top", {"start": v(-51.79, 88.9) * mm, "end": v(-58.14, 88.9) * mm});
            skLineSegment(sketch, "E77.left", {"start": v(-51.79, 95.25) * mm, "end": v(-51.79, 88.9) * mm});
            skLineSegment(sketch, "E77.right", {"start": v(-58.14, 95.25) * mm, "end": v(-58.14, 88.9) * mm});
            skSolve(sketch);
        }
        {
            var Q0;
            Q0=makeQuery(id+"F154.imprint","IMPRINT",FACE,{"disambiguationData":[TD([[makeQuery(id+"F154.imprint","IMPRINT",EDGE,{"derivedFrom":sQuery(id+"F154.wireOp",EDGE,"E77.bottom")}),-1.0]])]});
            extrude(context, id + "F155", {"entities" : qUnion([Q0]), "operationType" : NewBodyOperationType.ADD, "oppositeDirection" : true, "depth" : 19.05 * mm});
        }
        {
            var Q0;
            Q0=makeQuery(id+"F155.boolean.opBoolean","MERGE",FACE,{"derivedFrom":[makeQuery(id+"F153.opExtrude","CAP_FACE",FACE,{"disambiguationData":[OSD([sQuery(id+"F152.wireOp",EDGE,"E76.bottom"),sQuery(id+"F152.wireOp",EDGE,"E76.top"),sQuery(id+"F152.wireOp",EDGE,"E76.left"),sQuery(id+"F152.wireOp",EDGE,"E76.right")])],"isStart":false}),makeQuery(id+"F155.opExtrude","SWEPT_FACE",FACE,{"disambiguationData":[OSD([sQuery(id+"F154.wireOp",EDGE,"E77.bottom")])]})]});
            var sketch = newSketch(context, id + "F156", { "sketchPlane" : qUnion([Q0])});
            skLineSegment(sketch, "E78.bottom", {"start": v(-45.64, -51.79) * mm, "end": v(-39.3, -51.79) * mm});
            skLineSegment(sketch, "E78.top", {"start": v(-45.64, -58.14) * mm, "end": v(-39.3, -58.14) * mm});
            skLineSegment(sketch, "E78.left", {"start": v(-45.64, -51.79) * mm, "end": v(-45.64, -58.14) * mm});
            skLineSegment(sketch, "E78.right", {"start": v(-39.3, -51.79) * mm, "end": v(-39.3, -58.14) * mm});
            skSolve(sketch);
        }
        {
            var Q0;
            Q0=makeQuery(id+"F156.imprint","IMPRINT",FACE,{"disambiguationData":[TD([[makeQuery(id+"F156.imprint","IMPRINT",EDGE,{"derivedFrom":sQuery(id+"F156.wireOp",EDGE,"E78.bottom")}),1.0]])]});
            extrude(context, id + "F157", {"entities" : qUnion([Q0]), "operationType" : NewBodyOperationType.ADD, "oppositeDirection" : true, "depth" : 31.75 * mm});
        }
        {
            var Q0;
            Q0=makeQuery(id+"F157.boolean.opBoolean","MERGE",FACE,{"derivedFrom":[makeQuery(id+"F155.boolean.opBoolean","MERGE",FACE,{"derivedFrom":[makeQuery(id+"F153.boolean.opBoolean","MERGE",FACE,{"derivedFrom":[makeQuery(id+"F151.opExtrude","CAP_FACE",FACE,{"disambiguationData":[OSD([sQuery(id+"F150.wireOp",EDGE,"E75.bottom"),sQuery(id+"F150.wireOp",EDGE,"E75.top"),sQuery(id+"F150.wireOp",EDGE,"E75.left"),sQuery(id+"F150.wireOp",EDGE,"E75.right")])],"isStart":false}),makeQuery(id+"F153.opExtrude","SWEPT_FACE",FACE,{"disambiguationData":[OSD([sQuery(id+"F152.wireOp",EDGE,"E76.bottom")])]})]}),makeQuery(id+"F155.opExtrude","SWEPT_FACE",FACE,{"disambiguationData":[OSD([sQuery(id+"F154.wireOp",EDGE,"E77.left")])]})]}),makeQuery(id+"F157.opExtrude","SWEPT_FACE",FACE,{"disambiguationData":[OSD([sQuery(id+"F156.wireOp",EDGE,"E78.bottom")])]})]});
            var sketch = newSketch(context, id + "F158", { "sketchPlane" : qUnion([Q0])});
            skLineSegment(sketch, "E79.bottom", {"start": v(45.64, 63.5) * mm, "end": v(39.3, 63.5) * mm});
            skLineSegment(sketch, "E79.top", {"start": v(45.64, 69.85) * mm, "end": v(39.3, 69.85) * mm});
            skLineSegment(sketch, "E79.left", {"start": v(45.64, 63.5) * mm, "end": v(45.64, 69.85) * mm});
            skLineSegment(sketch, "E79.right", {"start": v(39.3, 63.5) * mm, "end": v(39.3, 69.85) * mm});
            skSolve(sketch);
        }
        {
            var Q0;
            Q0=makeQuery(id+"F158.imprint","IMPRINT",FACE,{"disambiguationData":[TD([[makeQuery(id+"F158.imprint","IMPRINT",EDGE,{"derivedFrom":sQuery(id+"F158.wireOp",EDGE,"E79.bottom")}),1.0]])]});
            extrude(context, id + "F159", {"entities" : qUnion([Q0]), "operationType" : NewBodyOperationType.ADD, "oppositeDirection" : true, "depth" : 19.05 * mm});
        }
        {
            var Q0;
            Q0=makeQuery(id+"F159.boolean.opBoolean","MERGE",FACE,{"derivedFrom":[makeQuery(id+"F157.boolean.opBoolean","MERGE",FACE,{"derivedFrom":[makeQuery(id+"F155.opExtrude","CAP_FACE",FACE,{"disambiguationData":[OSD([sQuery(id+"F154.wireOp",EDGE,"E77.bottom"),sQuery(id+"F154.wireOp",EDGE,"E77.top"),sQuery(id+"F154.wireOp",EDGE,"E77.left"),sQuery(id+"F154.wireOp",EDGE,"E77.right")])],"isStart":false}),makeQuery(id+"F157.opExtrude","SWEPT_FACE",FACE,{"disambiguationData":[OSD([sQuery(id+"F156.wireOp",EDGE,"E78.left")])]})]}),makeQuery(id+"F159.opExtrude","SWEPT_FACE",FACE,{"disambiguationData":[OSD([sQuery(id+"F158.wireOp",EDGE,"E79.left")])]})]});
            var sketch = newSketch(context, id + "F160", { "sketchPlane" : qUnion([Q0])});
            skLineSegment(sketch, "E80.bottom", {"start": v(70.84, 63.5) * mm, "end": v(64.49, 63.5) * mm});
            skLineSegment(sketch, "E80.top", {"start": v(70.84, 69.85) * mm, "end": v(64.49, 69.85) * mm});
            skLineSegment(sketch, "E80.left", {"start": v(70.84, 63.5) * mm, "end": v(70.84, 69.85) * mm});
            skLineSegment(sketch, "E80.right", {"start": v(64.49, 63.5) * mm, "end": v(64.49, 69.85) * mm});
            skSolve(sketch);
        }
        {
            var Q0;
            Q0=makeQuery(id+"F160.imprint","IMPRINT",FACE,{"disambiguationData":[TD([[makeQuery(id+"F160.imprint","IMPRINT",EDGE,{"derivedFrom":sQuery(id+"F160.wireOp",EDGE,"E80.bottom")}),-1.0]])]});
            extrude(context, id + "F161", {"entities" : qUnion([Q0]), "operationType" : NewBodyOperationType.ADD, "oppositeDirection" : true, "depth" : 19.05 * mm});
        }
        {
            var Q0;
            Q0=makeQuery(id+"F161.boolean.opBoolean","MERGE",FACE,{"derivedFrom":[makeQuery(id+"F159.opExtrude","CAP_FACE",FACE,{"disambiguationData":[OSD([sQuery(id+"F158.wireOp",EDGE,"E79.bottom"),sQuery(id+"F158.wireOp",EDGE,"E79.top"),sQuery(id+"F158.wireOp",EDGE,"E79.left"),sQuery(id+"F158.wireOp",EDGE,"E79.right")])],"isStart":false}),makeQuery(id+"F161.opExtrude","SWEPT_FACE",FACE,{"disambiguationData":[OSD([sQuery(id+"F160.wireOp",EDGE,"E80.left")])]})]});
            var sketch = newSketch(context, id + "F162", { "sketchPlane" : qUnion([Q0])});
            skLineSegment(sketch, "E81.bottom", {"start": v(-26.6, 63.5) * mm, "end": v(-32.94, 63.5) * mm});
            skLineSegment(sketch, "E81.top", {"start": v(-26.6, 69.85) * mm, "end": v(-32.94, 69.85) * mm});
            skLineSegment(sketch, "E81.left", {"start": v(-26.6, 63.5) * mm, "end": v(-26.6, 69.85) * mm});
            skLineSegment(sketch, "E81.right", {"start": v(-32.94, 63.5) * mm, "end": v(-32.94, 69.85) * mm});
            skSolve(sketch);
        }
        {
            var Q0;
            Q0=makeQuery(id+"F162.imprint","IMPRINT",FACE,{"disambiguationData":[TD([[makeQuery(id+"F162.imprint","IMPRINT",EDGE,{"derivedFrom":sQuery(id+"F162.wireOp",EDGE,"E81.bottom")}),-1.0]])]});
            extrude(context, id + "F163", {"entities" : qUnion([Q0]), "operationType" : NewBodyOperationType.ADD, "oppositeDirection" : true, "depth" : 19.05 * mm});
        }
        {
            var Q0;
            Q0=makeQuery(id+"F163.boolean.opBoolean","MERGE",FACE,{"derivedFrom":[makeQuery(id+"F161.boolean.opBoolean","MERGE",FACE,{"derivedFrom":[makeQuery(id+"F159.opExtrude","SWEPT_FACE",FACE,{"disambiguationData":[OSD([sQuery(id+"F158.wireOp",EDGE,"E79.top")])]}),makeQuery(id+"F161.opExtrude","SWEPT_FACE",FACE,{"disambiguationData":[OSD([sQuery(id+"F160.wireOp",EDGE,"E80.top")])]})]}),makeQuery(id+"F163.opExtrude","SWEPT_FACE",FACE,{"disambiguationData":[OSD([sQuery(id+"F162.wireOp",EDGE,"E81.top")])]})]});
            var sketch = newSketch(context, id + "F164", { "sketchPlane" : qUnion([Q0])});
            skLineSegment(sketch, "E82.bottom", {"start": v(-26.6, -51.79) * mm, "end": v(-32.94, -51.79) * mm});
            skLineSegment(sketch, "E82.top", {"start": v(-26.6, -58.14) * mm, "end": v(-32.94, -58.14) * mm});
            skLineSegment(sketch, "E82.left", {"start": v(-26.6, -51.79) * mm, "end": v(-26.6, -58.14) * mm});
            skLineSegment(sketch, "E82.right", {"start": v(-32.94, -51.79) * mm, "end": v(-32.94, -58.14) * mm});
            skSolve(sketch);
        }
        {
            var Q0;
            Q0=makeQuery(id+"F164.imprint","IMPRINT",FACE,{"disambiguationData":[TD([[makeQuery(id+"F164.imprint","IMPRINT",EDGE,{"derivedFrom":sQuery(id+"F164.wireOp",EDGE,"E82.bottom")}),-1.0]])]});
            extrude(context, id + "F165", {"entities" : qUnion([Q0]), "operationType" : NewBodyOperationType.ADD, "oppositeDirection" : true, "depth" : 19.05 * mm});
        }
        {
            var Q0;
            Q0=makeQuery(id+"F165.boolean.opBoolean","MERGE",FACE,{"derivedFrom":[makeQuery(id+"F163.opExtrude","CAP_FACE",FACE,{"disambiguationData":[OSD([sQuery(id+"F162.wireOp",EDGE,"E81.bottom"),sQuery(id+"F162.wireOp",EDGE,"E81.top"),sQuery(id+"F162.wireOp",EDGE,"E81.left"),sQuery(id+"F162.wireOp",EDGE,"E81.right")])],"isStart":false}),makeQuery(id+"F165.opExtrude","SWEPT_FACE",FACE,{"disambiguationData":[OSD([sQuery(id+"F164.wireOp",EDGE,"E82.bottom")])]})]});
            var sketch = newSketch(context, id + "F166", { "sketchPlane" : qUnion([Q0])});
            skLineSegment(sketch, "E83.bottom", {"start": v(32.94, 50.8) * mm, "end": v(26.6, 50.8) * mm});
            skLineSegment(sketch, "E83.top", {"start": v(32.94, 57.15) * mm, "end": v(26.6, 57.15) * mm});
            skLineSegment(sketch, "E83.left", {"start": v(32.94, 50.8) * mm, "end": v(32.94, 57.15) * mm});
            skLineSegment(sketch, "E83.right", {"start": v(26.6, 50.8) * mm, "end": v(26.6, 57.15) * mm});
            skSolve(sketch);
        }
        {
            var Q0;
            Q0=makeQuery(id+"F166.imprint","IMPRINT",FACE,{"disambiguationData":[TD([[makeQuery(id+"F166.imprint","IMPRINT",EDGE,{"derivedFrom":sQuery(id+"F166.wireOp",EDGE,"E83.bottom")}),-1.0]])]});
            extrude(context, id + "F167", {"entities" : qUnion([Q0]), "operationType" : NewBodyOperationType.ADD, "oppositeDirection" : true, "depth" : 19.05 * mm});
        }
        {
            var Q0;
            Q0=makeQuery(id+"F167.boolean.opBoolean","MERGE",FACE,{"derivedFrom":[makeQuery(id+"F165.boolean.opBoolean","MERGE",FACE,{"derivedFrom":[makeQuery(id+"F163.boolean.opBoolean","MERGE",FACE,{"derivedFrom":[makeQuery(id+"F161.opExtrude","CAP_FACE",FACE,{"disambiguationData":[OSD([sQuery(id+"F160.wireOp",EDGE,"E80.bottom"),sQuery(id+"F160.wireOp",EDGE,"E80.top"),sQuery(id+"F160.wireOp",EDGE,"E80.left"),sQuery(id+"F160.wireOp",EDGE,"E80.right")])],"isStart":false}),makeQuery(id+"F163.opExtrude","SWEPT_FACE",FACE,{"disambiguationData":[OSD([sQuery(id+"F162.wireOp",EDGE,"E81.left")])]})]}),makeQuery(id+"F165.opExtrude","SWEPT_FACE",FACE,{"disambiguationData":[OSD([sQuery(id+"F164.wireOp",EDGE,"E82.left")])]})]}),makeQuery(id+"F167.opExtrude","SWEPT_FACE",FACE,{"disambiguationData":[OSD([sQuery(id+"F166.wireOp",EDGE,"E83.right")])]})]});
            var sketch = newSketch(context, id + "F168", { "sketchPlane" : qUnion([Q0])});
            skLineSegment(sketch, "E84.bottom", {"start": v(-70.84, 50.8) * mm, "end": v(-64.49, 50.8) * mm});
            skLineSegment(sketch, "E84.top", {"start": v(-70.84, 57.15) * mm, "end": v(-64.49, 57.15) * mm});
            skLineSegment(sketch, "E84.left", {"start": v(-70.84, 50.8) * mm, "end": v(-70.84, 57.15) * mm});
            skLineSegment(sketch, "E84.right", {"start": v(-64.49, 50.8) * mm, "end": v(-64.49, 57.15) * mm});
            skSolve(sketch);
        }
        {
            var Q0;
            Q0=makeQuery(id+"F168.imprint","IMPRINT",FACE,{"disambiguationData":[TD([[makeQuery(id+"F168.imprint","IMPRINT",EDGE,{"derivedFrom":sQuery(id+"F168.wireOp",EDGE,"E84.bottom")}),1.0]])]});
            extrude(context, id + "F169", {"entities" : qUnion([Q0]), "operationType" : NewBodyOperationType.ADD, "oppositeDirection" : true, "depth" : 19.05 * mm});
        }
        {
            var Q0;
            Q0=makeQuery(id+"F169.boolean.opBoolean","MERGE",FACE,{"derivedFrom":[makeQuery(id+"F167.opExtrude","CAP_FACE",FACE,{"disambiguationData":[OSD([sQuery(id+"F166.wireOp",EDGE,"E83.bottom"),sQuery(id+"F166.wireOp",EDGE,"E83.top"),sQuery(id+"F166.wireOp",EDGE,"E83.left"),sQuery(id+"F166.wireOp",EDGE,"E83.right")])],"isStart":false}),makeQuery(id+"F169.opExtrude","SWEPT_FACE",FACE,{"disambiguationData":[OSD([sQuery(id+"F168.wireOp",EDGE,"E84.left")])]})]});
            var sketch = newSketch(context, id + "F170", { "sketchPlane" : qUnion([Q0])});
            skLineSegment(sketch, "E85.bottom", {"start": v(-45.64, 57.15) * mm, "end": v(-39.3, 57.15) * mm});
            skLineSegment(sketch, "E85.top", {"start": v(-45.64, 50.8) * mm, "end": v(-39.3, 50.8) * mm});
            skLineSegment(sketch, "E85.left", {"start": v(-45.64, 57.15) * mm, "end": v(-45.64, 50.8) * mm});
            skLineSegment(sketch, "E85.right", {"start": v(-39.3, 57.15) * mm, "end": v(-39.3, 50.8) * mm});
            skSolve(sketch);
        }
        {
            var Q0;
            Q0=makeQuery(id+"F170.imprint","IMPRINT",FACE,{"disambiguationData":[TD([[makeQuery(id+"F170.imprint","IMPRINT",EDGE,{"derivedFrom":sQuery(id+"F170.wireOp",EDGE,"E85.bottom")}),-1.0]])]});
            extrude(context, id + "F171", {"entities" : qUnion([Q0]), "operationType" : NewBodyOperationType.ADD, "oppositeDirection" : true, "depth" : 44.45 * mm});
        }
        {
            var Q0;
            Q0=makeQuery(id+"F171.boolean.opBoolean","MERGE",FACE,{"derivedFrom":[makeQuery(id+"F169.opExtrude","CAP_FACE",FACE,{"disambiguationData":[OSD([sQuery(id+"F168.wireOp",EDGE,"E84.bottom"),sQuery(id+"F168.wireOp",EDGE,"E84.top"),sQuery(id+"F168.wireOp",EDGE,"E84.left"),sQuery(id+"F168.wireOp",EDGE,"E84.right")])],"isStart":false}),makeQuery(id+"F171.opExtrude","SWEPT_FACE",FACE,{"disambiguationData":[OSD([sQuery(id+"F170.wireOp",EDGE,"E85.left")])]})]});
            var sketch = newSketch(context, id + "F172", { "sketchPlane" : qUnion([Q0])});
            skLineSegment(sketch, "E86.bottom", {"start": v(26.39, 57.15) * mm, "end": v(32.74, 57.15) * mm});
            skLineSegment(sketch, "E86.top", {"start": v(26.39, 50.8) * mm, "end": v(32.74, 50.8) * mm});
            skLineSegment(sketch, "E86.left", {"start": v(26.39, 57.15) * mm, "end": v(26.39, 50.8) * mm});
            skLineSegment(sketch, "E86.right", {"start": v(32.74, 57.15) * mm, "end": v(32.74, 50.8) * mm});
            skSolve(sketch);
        }
        {
            var Q0;
            Q0=makeQuery(id+"F172.imprint","IMPRINT",FACE,{"disambiguationData":[TD([[makeQuery(id+"F172.imprint","IMPRINT",EDGE,{"derivedFrom":sQuery(id+"F172.wireOp",EDGE,"E86.bottom")}),1.0]])]});
            extrude(context, id + "F173", {"entities" : qUnion([Q0]), "operationType" : NewBodyOperationType.ADD, "oppositeDirection" : true, "depth" : 19.05 * mm});
        }
        {
            var Q0;
            Q0=makeQuery(id+"F173.boolean.opBoolean","MERGE",FACE,{"derivedFrom":[makeQuery(id+"F171.opExtrude","CAP_FACE",FACE,{"disambiguationData":[OSD([sQuery(id+"F170.wireOp",EDGE,"E85.bottom"),sQuery(id+"F170.wireOp",EDGE,"E85.top"),sQuery(id+"F170.wireOp",EDGE,"E85.left"),sQuery(id+"F170.wireOp",EDGE,"E85.right")])],"isStart":false}),makeQuery(id+"F173.opExtrude","SWEPT_FACE",FACE,{"disambiguationData":[OSD([sQuery(id+"F172.wireOp",EDGE,"E86.left")])]})]});
            var sketch = newSketch(context, id + "F174", { "sketchPlane" : qUnion([Q0])});
            skLineSegment(sketch, "E87.bottom", {"start": v(26.6, 50.8) * mm, "end": v(32.94, 50.8) * mm});
            skLineSegment(sketch, "E87.top", {"start": v(26.6, 57.15) * mm, "end": v(32.94, 57.15) * mm});
            skLineSegment(sketch, "E87.left", {"start": v(26.6, 50.8) * mm, "end": v(26.6, 57.15) * mm});
            skLineSegment(sketch, "E87.right", {"start": v(32.94, 50.8) * mm, "end": v(32.94, 57.15) * mm});
            skSolve(sketch);
        }
        {
            var Q0;
            Q0=makeQuery(id+"F174.imprint","IMPRINT",FACE,{"disambiguationData":[TD([[makeQuery(id+"F174.imprint","IMPRINT",EDGE,{"derivedFrom":sQuery(id+"F174.wireOp",EDGE,"E87.bottom")}),-1.0]])]});
            extrude(context, id + "F175", {"entities" : qUnion([Q0]), "operationType" : NewBodyOperationType.ADD, "oppositeDirection" : true, "depth" : 19.05 * mm});
        }
        {
            var Q0;
            Q0=makeQuery(id+"F175.boolean.opBoolean","MERGE",FACE,{"derivedFrom":[makeQuery(id+"F173.boolean.opBoolean","MERGE",FACE,{"derivedFrom":[makeQuery(id+"F171.boolean.opBoolean","MERGE",FACE,{"derivedFrom":[makeQuery(id+"F169.boolean.opBoolean","MERGE",FACE,{"derivedFrom":[makeQuery(id+"F167.boolean.opBoolean","MERGE",FACE,{"derivedFrom":[makeQuery(id+"F165.opExtrude","CAP_FACE",FACE,{"disambiguationData":[OSD([sQuery(id+"F164.wireOp",EDGE,"E82.bottom"),sQuery(id+"F164.wireOp",EDGE,"E82.top"),sQuery(id+"F164.wireOp",EDGE,"E82.left"),sQuery(id+"F164.wireOp",EDGE,"E82.right")])],"isStart":false}),makeQuery(id+"F167.opExtrude","SWEPT_FACE",FACE,{"disambiguationData":[OSD([sQuery(id+"F166.wireOp",EDGE,"E83.bottom")])]})]}),makeQuery(id+"F169.opExtrude","SWEPT_FACE",FACE,{"disambiguationData":[OSD([sQuery(id+"F168.wireOp",EDGE,"E84.bottom")])]})]}),makeQuery(id+"F171.opExtrude","SWEPT_FACE",FACE,{"disambiguationData":[OSD([sQuery(id+"F170.wireOp",EDGE,"E85.top")])]})]}),makeQuery(id+"F173.opExtrude","SWEPT_FACE",FACE,{"disambiguationData":[OSD([sQuery(id+"F172.wireOp",EDGE,"E86.top")])]})]}),makeQuery(id+"F175.opExtrude","SWEPT_FACE",FACE,{"disambiguationData":[OSD([sQuery(id+"F174.wireOp",EDGE,"E87.bottom")])]})]});
            var sketch = newSketch(context, id + "F176", { "sketchPlane" : qUnion([Q0])});
            skLineSegment(sketch, "E88.bottom", {"start": v(-26.6, 45.44) * mm, "end": v(-32.94, 45.44) * mm});
            skLineSegment(sketch, "E88.top", {"start": v(-26.6, 39.09) * mm, "end": v(-32.94, 39.09) * mm});
            skLineSegment(sketch, "E88.left", {"start": v(-26.6, 45.44) * mm, "end": v(-26.6, 39.09) * mm});
            skLineSegment(sketch, "E88.right", {"start": v(-32.94, 45.44) * mm, "end": v(-32.94, 39.09) * mm});
            skSolve(sketch);
        }
        {
            var Q0;
            Q0=makeQuery(id+"F176.imprint","IMPRINT",FACE,{"disambiguationData":[TD([[makeQuery(id+"F176.imprint","IMPRINT",EDGE,{"derivedFrom":sQuery(id+"F176.wireOp",EDGE,"E88.bottom")}),-1.0]])]});
            extrude(context, id + "F177", {"entities" : qUnion([Q0]), "operationType" : NewBodyOperationType.ADD, "oppositeDirection" : true, "depth" : 19.05 * mm});
        }
        {
            var Q0;
            Q0=makeQuery(id+"F177.boolean.opBoolean","MERGE",FACE,{"derivedFrom":[makeQuery(id+"F175.opExtrude","CAP_FACE",FACE,{"disambiguationData":[OSD([sQuery(id+"F174.wireOp",EDGE,"E87.bottom"),sQuery(id+"F174.wireOp",EDGE,"E87.top"),sQuery(id+"F174.wireOp",EDGE,"E87.left"),sQuery(id+"F174.wireOp",EDGE,"E87.right")])],"isStart":false}),makeQuery(id+"F177.opExtrude","SWEPT_FACE",FACE,{"disambiguationData":[OSD([sQuery(id+"F176.wireOp",EDGE,"E88.bottom")])]})]});
            var sketch = newSketch(context, id + "F178", { "sketchPlane" : qUnion([Q0])});
            skLineSegment(sketch, "E89.bottom", {"start": v(-26.6, 69.85) * mm, "end": v(-32.94, 69.85) * mm});
            skLineSegment(sketch, "E89.top", {"start": v(-26.6, 63.5) * mm, "end": v(-32.94, 63.5) * mm});
            skLineSegment(sketch, "E89.left", {"start": v(-26.6, 69.85) * mm, "end": v(-26.6, 63.5) * mm});
            skLineSegment(sketch, "E89.right", {"start": v(-32.94, 69.85) * mm, "end": v(-32.94, 63.5) * mm});
            skSolve(sketch);
        }
        {
            var Q0;
            Q0=makeQuery(id+"F178.imprint","IMPRINT",FACE,{"disambiguationData":[TD([[makeQuery(id+"F178.imprint","IMPRINT",EDGE,{"derivedFrom":sQuery(id+"F178.wireOp",EDGE,"E89.bottom")}),-1.0]])]});
            extrude(context, id + "F179", {"entities" : qUnion([Q0]), "operationType" : NewBodyOperationType.ADD, "oppositeDirection" : true, "depth" : 19.05 * mm});
        }
        {
            var Q0;
            Q0=makeQuery(id+"F179.boolean.opBoolean","MERGE",FACE,{"derivedFrom":[makeQuery(id+"F177.boolean.opBoolean","MERGE",FACE,{"derivedFrom":[makeQuery(id+"F175.boolean.opBoolean","MERGE",FACE,{"derivedFrom":[makeQuery(id+"F173.opExtrude","CAP_FACE",FACE,{"disambiguationData":[OSD([sQuery(id+"F172.wireOp",EDGE,"E86.bottom"),sQuery(id+"F172.wireOp",EDGE,"E86.top"),sQuery(id+"F172.wireOp",EDGE,"E86.left"),sQuery(id+"F172.wireOp",EDGE,"E86.right")])],"isStart":false}),makeQuery(id+"F175.opExtrude","SWEPT_FACE",FACE,{"disambiguationData":[OSD([sQuery(id+"F174.wireOp",EDGE,"E87.left")])]})]}),makeQuery(id+"F177.opExtrude","SWEPT_FACE",FACE,{"disambiguationData":[OSD([sQuery(id+"F176.wireOp",EDGE,"E88.left")])]})]}),makeQuery(id+"F179.opExtrude","SWEPT_FACE",FACE,{"disambiguationData":[OSD([sQuery(id+"F178.wireOp",EDGE,"E89.left")])]})]});
            var sketch = newSketch(context, id + "F180", { "sketchPlane" : qUnion([Q0])});
            skLineSegment(sketch, "E90.bottom", {"start": v(-26.39, 69.85) * mm, "end": v(-32.74, 69.85) * mm});
            skLineSegment(sketch, "E90.top", {"start": v(-26.39, 63.5) * mm, "end": v(-32.74, 63.5) * mm});
            skLineSegment(sketch, "E90.left", {"start": v(-26.39, 69.85) * mm, "end": v(-26.39, 63.5) * mm});
            skLineSegment(sketch, "E90.right", {"start": v(-32.74, 69.85) * mm, "end": v(-32.74, 63.5) * mm});
            skSolve(sketch);
        }
        {
            var Q0;
            Q0=makeQuery(id+"F180.imprint","IMPRINT",FACE,{"disambiguationData":[TD([[makeQuery(id+"F180.imprint","IMPRINT",EDGE,{"derivedFrom":sQuery(id+"F180.wireOp",EDGE,"E90.bottom")}),-1.0]])]});
            extrude(context, id + "F181", {"entities" : qUnion([Q0]), "operationType" : NewBodyOperationType.ADD, "oppositeDirection" : true, "depth" : 19.05 * mm});
        }
        {
            var Q0;
            Q0=makeQuery(id+"F181.boolean.opBoolean","MERGE",FACE,{"derivedFrom":[makeQuery(id+"F179.opExtrude","CAP_FACE",FACE,{"disambiguationData":[OSD([sQuery(id+"F178.wireOp",EDGE,"E89.bottom"),sQuery(id+"F178.wireOp",EDGE,"E89.top"),sQuery(id+"F178.wireOp",EDGE,"E89.left"),sQuery(id+"F178.wireOp",EDGE,"E89.right")])],"isStart":false}),makeQuery(id+"F181.opExtrude","SWEPT_FACE",FACE,{"disambiguationData":[OSD([sQuery(id+"F180.wireOp",EDGE,"E90.left")])]})]});
            var sketch = newSketch(context, id + "F182", { "sketchPlane" : qUnion([Q0])});
            skLineSegment(sketch, "E91.bottom", {"start": v(45.64, 69.85) * mm, "end": v(39.3, 69.85) * mm});
            skLineSegment(sketch, "E91.top", {"start": v(45.64, 63.5) * mm, "end": v(39.3, 63.5) * mm});
            skLineSegment(sketch, "E91.left", {"start": v(45.64, 69.85) * mm, "end": v(45.64, 63.5) * mm});
            skLineSegment(sketch, "E91.right", {"start": v(39.3, 69.85) * mm, "end": v(39.3, 63.5) * mm});
            skSolve(sketch);
        }
        {
            var Q0;
            Q0=makeQuery(id+"F182.imprint","IMPRINT",FACE,{"disambiguationData":[TD([[makeQuery(id+"F182.imprint","IMPRINT",EDGE,{"derivedFrom":sQuery(id+"F182.wireOp",EDGE,"E91.bottom")}),1.0]])]});
            extrude(context, id + "F183", {"entities" : qUnion([Q0]), "operationType" : NewBodyOperationType.ADD, "oppositeDirection" : true, "depth" : 19.05 * mm});
        }
        {
            var Q0;
            Q0=makeQuery(id+"F183.boolean.opBoolean","MERGE",FACE,{"derivedFrom":[makeQuery(id+"F181.boolean.opBoolean","MERGE",FACE,{"derivedFrom":[makeQuery(id+"F179.opExtrude","SWEPT_FACE",FACE,{"disambiguationData":[OSD([sQuery(id+"F178.wireOp",EDGE,"E89.top")])]}),makeQuery(id+"F181.opExtrude","SWEPT_FACE",FACE,{"disambiguationData":[OSD([sQuery(id+"F180.wireOp",EDGE,"E90.top")])]})]}),makeQuery(id+"F183.opExtrude","SWEPT_FACE",FACE,{"disambiguationData":[OSD([sQuery(id+"F182.wireOp",EDGE,"E91.top")])]})]});
            var sketch = newSketch(context, id + "F184", { "sketchPlane" : qUnion([Q0])});
            skLineSegment(sketch, "E92.bottom", {"start": v(-45.64, 45.44) * mm, "end": v(-39.3, 45.44) * mm});
            skLineSegment(sketch, "E92.top", {"start": v(-45.64, 39.09) * mm, "end": v(-39.3, 39.09) * mm});
            skLineSegment(sketch, "E92.left", {"start": v(-45.64, 45.44) * mm, "end": v(-45.64, 39.09) * mm});
            skLineSegment(sketch, "E92.right", {"start": v(-39.3, 45.44) * mm, "end": v(-39.3, 39.09) * mm});
            skSolve(sketch);
        }
        {
            var Q0;
            Q0=makeQuery(id+"F184.imprint","IMPRINT",FACE,{"disambiguationData":[TD([[makeQuery(id+"F184.imprint","IMPRINT",EDGE,{"derivedFrom":sQuery(id+"F184.wireOp",EDGE,"E92.bottom")}),1.0]])]});
            extrude(context, id + "F185", {"entities" : qUnion([Q0]), "operationType" : NewBodyOperationType.ADD, "oppositeDirection" : true, "depth" : 31.75 * mm});
        }
        {
            var Q0;
            Q0=makeQuery(id+"F185.boolean.opBoolean","MERGE",FACE,{"derivedFrom":[makeQuery(id+"F183.boolean.opBoolean","MERGE",FACE,{"derivedFrom":[makeQuery(id+"F181.opExtrude","CAP_FACE",FACE,{"disambiguationData":[OSD([sQuery(id+"F180.wireOp",EDGE,"E90.bottom"),sQuery(id+"F180.wireOp",EDGE,"E90.top"),sQuery(id+"F180.wireOp",EDGE,"E90.left"),sQuery(id+"F180.wireOp",EDGE,"E90.right")])],"isStart":false}),makeQuery(id+"F183.opExtrude","SWEPT_FACE",FACE,{"disambiguationData":[OSD([sQuery(id+"F182.wireOp",EDGE,"E91.left")])]})]}),makeQuery(id+"F185.opExtrude","SWEPT_FACE",FACE,{"disambiguationData":[OSD([sQuery(id+"F184.wireOp",EDGE,"E92.left")])]})]});
            var sketch = newSketch(context, id + "F186", { "sketchPlane" : qUnion([Q0])});
            skLineSegment(sketch, "E93.bottom", {"start": v(45.44, 95.25) * mm, "end": v(39.09, 95.25) * mm});
            skLineSegment(sketch, "E93.top", {"start": v(45.44, 88.9) * mm, "end": v(39.09, 88.9) * mm});
            skLineSegment(sketch, "E93.left", {"start": v(45.44, 95.25) * mm, "end": v(45.44, 88.9) * mm});
            skLineSegment(sketch, "E93.right", {"start": v(39.09, 95.25) * mm, "end": v(39.09, 88.9) * mm});
            skSolve(sketch);
        }
        {
            var Q0;
            Q0=makeQuery(id+"F186.imprint","IMPRINT",FACE,{"disambiguationData":[TD([[makeQuery(id+"F186.imprint","IMPRINT",EDGE,{"derivedFrom":sQuery(id+"F186.wireOp",EDGE,"E93.bottom")}),-1.0]])]});
            extrude(context, id + "F187", {"entities" : qUnion([Q0]), "operationType" : NewBodyOperationType.ADD, "oppositeDirection" : true, "depth" : 19.05 * mm});
        }
        {
            var Q0;
            Q0=makeQuery(id+"F187.boolean.opBoolean","MERGE",FACE,{"derivedFrom":[makeQuery(id+"F185.opExtrude","CAP_FACE",FACE,{"disambiguationData":[OSD([sQuery(id+"F184.wireOp",EDGE,"E92.bottom"),sQuery(id+"F184.wireOp",EDGE,"E92.top"),sQuery(id+"F184.wireOp",EDGE,"E92.left"),sQuery(id+"F184.wireOp",EDGE,"E92.right")])],"isStart":false}),makeQuery(id+"F187.opExtrude","SWEPT_FACE",FACE,{"disambiguationData":[OSD([sQuery(id+"F186.wireOp",EDGE,"E93.bottom")])]})]});
            var sketch = newSketch(context, id + "F188", { "sketchPlane" : qUnion([Q0])});
            skLineSegment(sketch, "E94.bottom", {"start": v(-26.6, -39.09) * mm, "end": v(-32.94, -39.09) * mm});
            skLineSegment(sketch, "E94.top", {"start": v(-26.6, -45.44) * mm, "end": v(-32.94, -45.44) * mm});
            skLineSegment(sketch, "E94.left", {"start": v(-26.6, -39.09) * mm, "end": v(-26.6, -45.44) * mm});
            skLineSegment(sketch, "E94.right", {"start": v(-32.94, -39.09) * mm, "end": v(-32.94, -45.44) * mm});
            skSolve(sketch);
        }
        {
            var Q0;
            Q0=makeQuery(id+"F188.imprint","IMPRINT",FACE,{"disambiguationData":[TD([[makeQuery(id+"F188.imprint","IMPRINT",EDGE,{"derivedFrom":sQuery(id+"F188.wireOp",EDGE,"E94.bottom")}),-1.0]])]});
            extrude(context, id + "F189", {"entities" : qUnion([Q0]), "operationType" : NewBodyOperationType.ADD, "oppositeDirection" : true, "depth" : 19.05 * mm});
        }
        {
            var Q0;
            Q0=makeQuery(id+"F189.boolean.opBoolean","MERGE",FACE,{"derivedFrom":[makeQuery(id+"F187.boolean.opBoolean","MERGE",FACE,{"derivedFrom":[makeQuery(id+"F185.boolean.opBoolean","MERGE",FACE,{"derivedFrom":[makeQuery(id+"F183.opExtrude","CAP_FACE",FACE,{"disambiguationData":[OSD([sQuery(id+"F182.wireOp",EDGE,"E91.bottom"),sQuery(id+"F182.wireOp",EDGE,"E91.top"),sQuery(id+"F182.wireOp",EDGE,"E91.left"),sQuery(id+"F182.wireOp",EDGE,"E91.right")])],"isStart":false}),makeQuery(id+"F185.opExtrude","SWEPT_FACE",FACE,{"disambiguationData":[OSD([sQuery(id+"F184.wireOp",EDGE,"E92.bottom")])]})]}),makeQuery(id+"F187.opExtrude","SWEPT_FACE",FACE,{"disambiguationData":[OSD([sQuery(id+"F186.wireOp",EDGE,"E93.left")])]})]}),makeQuery(id+"F189.opExtrude","SWEPT_FACE",FACE,{"disambiguationData":[OSD([sQuery(id+"F188.wireOp",EDGE,"E94.top")])]})]});
            var sketch = newSketch(context, id + "F190", { "sketchPlane" : qUnion([Q0])});
            skLineSegment(sketch, "E95.bottom", {"start": v(-26.6, 76.2) * mm, "end": v(-32.94, 76.2) * mm});
            skLineSegment(sketch, "E95.top", {"start": v(-26.6, 82.55) * mm, "end": v(-32.94, 82.55) * mm});
            skLineSegment(sketch, "E95.left", {"start": v(-26.6, 76.2) * mm, "end": v(-26.6, 82.55) * mm});
            skLineSegment(sketch, "E95.right", {"start": v(-32.94, 76.2) * mm, "end": v(-32.94, 82.55) * mm});
            skSolve(sketch);
        }
        {
            var Q0;
            Q0=makeQuery(id+"F190.imprint","IMPRINT",FACE,{"disambiguationData":[TD([[makeQuery(id+"F190.imprint","IMPRINT",EDGE,{"derivedFrom":sQuery(id+"F190.wireOp",EDGE,"E95.bottom")}),-1.0]])]});
            extrude(context, id + "F191", {"entities" : qUnion([Q0]), "operationType" : NewBodyOperationType.ADD, "oppositeDirection" : true, "depth" : 19.05 * mm});
        }
        {
            var Q0;
            Q0=makeQuery(id+"F191.boolean.opBoolean","MERGE",FACE,{"derivedFrom":[makeQuery(id+"F189.opExtrude","CAP_FACE",FACE,{"disambiguationData":[OSD([sQuery(id+"F188.wireOp",EDGE,"E94.bottom"),sQuery(id+"F188.wireOp",EDGE,"E94.top"),sQuery(id+"F188.wireOp",EDGE,"E94.left"),sQuery(id+"F188.wireOp",EDGE,"E94.right")])],"isStart":false}),makeQuery(id+"F191.opExtrude","SWEPT_FACE",FACE,{"disambiguationData":[OSD([sQuery(id+"F190.wireOp",EDGE,"E95.bottom")])]})]});
            var sketch = newSketch(context, id + "F192", { "sketchPlane" : qUnion([Q0])});
            skLineSegment(sketch, "E96.bottom", {"start": v(-32.94, 26.39) * mm, "end": v(-26.6, 26.39) * mm});
            skLineSegment(sketch, "E96.top", {"start": v(-32.94, 32.74) * mm, "end": v(-26.6, 32.74) * mm});
            skLineSegment(sketch, "E96.left", {"start": v(-32.94, 26.39) * mm, "end": v(-32.94, 32.74) * mm});
            skLineSegment(sketch, "E96.right", {"start": v(-26.6, 26.39) * mm, "end": v(-26.6, 32.74) * mm});
            skSolve(sketch);
        }
        {
            var Q0;
            Q0=makeQuery(id+"F192.imprint","IMPRINT",FACE,{"disambiguationData":[TD([[makeQuery(id+"F192.imprint","IMPRINT",EDGE,{"derivedFrom":sQuery(id+"F192.wireOp",EDGE,"E96.bottom")}),-1.0]])]});
            extrude(context, id + "F193", {"entities" : qUnion([Q0]), "operationType" : NewBodyOperationType.ADD, "oppositeDirection" : true, "depth" : 19.05 * mm});
        }
        {
            var Q0;
            Q0=makeQuery(id+"F193.boolean.opBoolean","MERGE",FACE,{"derivedFrom":[makeQuery(id+"F191.boolean.opBoolean","MERGE",FACE,{"derivedFrom":[makeQuery(id+"F189.boolean.opBoolean","MERGE",FACE,{"derivedFrom":[makeQuery(id+"F187.opExtrude","CAP_FACE",FACE,{"disambiguationData":[OSD([sQuery(id+"F186.wireOp",EDGE,"E93.bottom"),sQuery(id+"F186.wireOp",EDGE,"E93.top"),sQuery(id+"F186.wireOp",EDGE,"E93.left"),sQuery(id+"F186.wireOp",EDGE,"E93.right")])],"isStart":false}),makeQuery(id+"F189.opExtrude","SWEPT_FACE",FACE,{"disambiguationData":[OSD([sQuery(id+"F188.wireOp",EDGE,"E94.left")])]})]}),makeQuery(id+"F191.opExtrude","SWEPT_FACE",FACE,{"disambiguationData":[OSD([sQuery(id+"F190.wireOp",EDGE,"E95.left")])]})]}),makeQuery(id+"F193.opExtrude","SWEPT_FACE",FACE,{"disambiguationData":[OSD([sQuery(id+"F192.wireOp",EDGE,"E96.right")])]})]});
            var sketch = newSketch(context, id + "F194", { "sketchPlane" : qUnion([Q0])});
            skLineSegment(sketch, "E97.bottom", {"start": v(-26.39, 95.25) * mm, "end": v(-32.74, 95.25) * mm});
            skLineSegment(sketch, "E97.top", {"start": v(-26.39, 88.9) * mm, "end": v(-32.74, 88.9) * mm});
            skLineSegment(sketch, "E97.left", {"start": v(-26.39, 95.25) * mm, "end": v(-26.39, 88.9) * mm});
            skLineSegment(sketch, "E97.right", {"start": v(-32.74, 95.25) * mm, "end": v(-32.74, 88.9) * mm});
            skSolve(sketch);
        }
        {
            var Q0;
            Q0=makeQuery(id+"F194.imprint","IMPRINT",FACE,{"disambiguationData":[TD([[makeQuery(id+"F194.imprint","IMPRINT",EDGE,{"derivedFrom":sQuery(id+"F194.wireOp",EDGE,"E97.bottom")}),1.0]])]});
            extrude(context, id + "F195", {"entities" : qUnion([Q0]), "operationType" : NewBodyOperationType.ADD, "oppositeDirection" : true, "depth" : 19.05 * mm});
        }
        {
            var Q0;
            Q0=makeQuery(id+"F195.boolean.opBoolean","MERGE",FACE,{"derivedFrom":[makeQuery(id+"F193.opExtrude","CAP_FACE",FACE,{"disambiguationData":[OSD([sQuery(id+"F192.wireOp",EDGE,"E96.bottom"),sQuery(id+"F192.wireOp",EDGE,"E96.top"),sQuery(id+"F192.wireOp",EDGE,"E96.left"),sQuery(id+"F192.wireOp",EDGE,"E96.right")])],"isStart":false}),makeQuery(id+"F195.opExtrude","SWEPT_FACE",FACE,{"disambiguationData":[OSD([sQuery(id+"F194.wireOp",EDGE,"E97.bottom")])]})]});
            var sketch = newSketch(context, id + "F196", { "sketchPlane" : qUnion([Q0])});
            skLineSegment(sketch, "E98.bottom", {"start": v(-45.64, -26.39) * mm, "end": v(-39.3, -26.39) * mm});
            skLineSegment(sketch, "E98.top", {"start": v(-45.64, -32.74) * mm, "end": v(-39.3, -32.74) * mm});
            skLineSegment(sketch, "E98.left", {"start": v(-45.64, -26.39) * mm, "end": v(-45.64, -32.74) * mm});
            skLineSegment(sketch, "E98.right", {"start": v(-39.3, -26.39) * mm, "end": v(-39.3, -32.74) * mm});
            skSolve(sketch);
        }
        {
            var Q0;
            Q0=makeQuery(id+"F196.imprint","IMPRINT",FACE,{"disambiguationData":[TD([[makeQuery(id+"F196.imprint","IMPRINT",EDGE,{"derivedFrom":sQuery(id+"F196.wireOp",EDGE,"E98.bottom")}),1.0]])]});
            extrude(context, id + "F197", {"entities" : qUnion([Q0]), "operationType" : NewBodyOperationType.ADD, "oppositeDirection" : true, "depth" : 19.05 * mm});
        }
        {
            var Q0;
            Q0=makeQuery(id+"F197.opExtrude","SWEPT_FACE",FACE,{"disambiguationData":[OSD([sQuery(id+"F196.wireOp",EDGE,"E98.right")])]});
            var sketch = newSketch(context, id + "F198", { "sketchPlane" : qUnion([Q0])});
            skLineSegment(sketch, "E99.bottom", {"start": v(-26.39, 76.2) * mm, "end": v(-32.74, 76.2) * mm});
            skLineSegment(sketch, "E99.top", {"start": v(-26.39, 82.55) * mm, "end": v(-32.74, 82.55) * mm});
            skLineSegment(sketch, "E99.left", {"start": v(-26.39, 76.2) * mm, "end": v(-26.39, 82.55) * mm});
            skLineSegment(sketch, "E99.right", {"start": v(-32.74, 76.2) * mm, "end": v(-32.74, 82.55) * mm});
            skSolve(sketch);
        }
        {
            var Q0;
            Q0=makeQuery(id+"F198.imprint","IMPRINT",FACE,{"disambiguationData":[TD([[makeQuery(id+"F198.imprint","IMPRINT",EDGE,{"derivedFrom":sQuery(id+"F198.wireOp",EDGE,"E99.bottom")}),-1.0]])]});
            extrude(context, id + "F199", {"entities" : qUnion([Q0]), "operationType" : NewBodyOperationType.ADD, "oppositeDirection" : true, "depth" : 19.05 * mm});
        }
        {
            var Q0;
            Q0=makeQuery(id+"F199.boolean.opBoolean","MERGE",FACE,{"derivedFrom":[makeQuery(id+"F197.opExtrude","CAP_FACE",FACE,{"disambiguationData":[OSD([sQuery(id+"F196.wireOp",EDGE,"E98.bottom"),sQuery(id+"F196.wireOp",EDGE,"E98.top"),sQuery(id+"F196.wireOp",EDGE,"E98.left"),sQuery(id+"F196.wireOp",EDGE,"E98.right")])],"isStart":false}),makeQuery(id+"F199.opExtrude","SWEPT_FACE",FACE,{"disambiguationData":[OSD([sQuery(id+"F198.wireOp",EDGE,"E99.bottom")])]})]});
            var sketch = newSketch(context, id + "F200", { "sketchPlane" : qUnion([Q0])});
            skLineSegment(sketch, "E100.bottom", {"start": v(-58.34, 32.74) * mm, "end": v(-52, 32.74) * mm});
            skLineSegment(sketch, "E100.top", {"start": v(-58.34, 26.39) * mm, "end": v(-52, 26.39) * mm});
            skLineSegment(sketch, "E100.left", {"start": v(-58.34, 32.74) * mm, "end": v(-58.34, 26.39) * mm});
            skLineSegment(sketch, "E100.right", {"start": v(-52, 32.74) * mm, "end": v(-52, 26.39) * mm});
            skSolve(sketch);
        }
        {
            var Q0;
            Q0=makeQuery(id+"F200.imprint","IMPRINT",FACE,{"disambiguationData":[TD([[makeQuery(id+"F200.imprint","IMPRINT",EDGE,{"derivedFrom":sQuery(id+"F200.wireOp",EDGE,"E100.bottom")}),-1.0]])]});
            extrude(context, id + "F201", {"entities" : qUnion([Q0]), "operationType" : NewBodyOperationType.ADD, "oppositeDirection" : true, "depth" : 19.05 * mm});
        }
        {
            var Q0;
            Q0=makeQuery(id+"F201.boolean.opBoolean","MERGE",FACE,{"derivedFrom":[makeQuery(id+"F199.boolean.opBoolean","MERGE",FACE,{"derivedFrom":[makeQuery(id+"F197.boolean.opBoolean","MERGE",FACE,{"derivedFrom":[makeQuery(id+"F195.boolean.opBoolean","MERGE",FACE,{"derivedFrom":[makeQuery(id+"F193.boolean.opBoolean","MERGE",FACE,{"derivedFrom":[makeQuery(id+"F191.opExtrude","CAP_FACE",FACE,{"disambiguationData":[OSD([sQuery(id+"F190.wireOp",EDGE,"E95.bottom"),sQuery(id+"F190.wireOp",EDGE,"E95.top"),sQuery(id+"F190.wireOp",EDGE,"E95.left"),sQuery(id+"F190.wireOp",EDGE,"E95.right")])],"isStart":false}),makeQuery(id+"F193.opExtrude","SWEPT_FACE",FACE,{"disambiguationData":[OSD([sQuery(id+"F192.wireOp",EDGE,"E96.bottom")])]})]}),makeQuery(id+"F195.opExtrude","SWEPT_FACE",FACE,{"disambiguationData":[OSD([sQuery(id+"F194.wireOp",EDGE,"E97.left")])]})]}),makeQuery(id+"F197.opExtrude","SWEPT_FACE",FACE,{"disambiguationData":[OSD([sQuery(id+"F196.wireOp",EDGE,"E98.bottom")])]})]}),makeQuery(id+"F199.opExtrude","SWEPT_FACE",FACE,{"disambiguationData":[OSD([sQuery(id+"F198.wireOp",EDGE,"E99.left")])]})]}),makeQuery(id+"F201.opExtrude","SWEPT_FACE",FACE,{"disambiguationData":[OSD([sQuery(id+"F200.wireOp",EDGE,"E100.top")])]})]});
            var sketch = newSketch(context, id + "F202", { "sketchPlane" : qUnion([Q0])});
            skLineSegment(sketch, "E101.bottom", {"start": v(58.34, 95.25) * mm, "end": v(52, 95.25) * mm});
            skLineSegment(sketch, "E101.top", {"start": v(58.34, 88.9) * mm, "end": v(52, 88.9) * mm});
            skLineSegment(sketch, "E101.left", {"start": v(58.34, 95.25) * mm, "end": v(58.34, 88.9) * mm});
            skLineSegment(sketch, "E101.right", {"start": v(52, 95.25) * mm, "end": v(52, 88.9) * mm});
            skSolve(sketch);
        }
        {
            var Q0;
            Q0=makeQuery(id+"F202.imprint","IMPRINT",FACE,{"disambiguationData":[TD([[makeQuery(id+"F202.imprint","IMPRINT",EDGE,{"derivedFrom":sQuery(id+"F202.wireOp",EDGE,"E101.bottom")}),-1.0]])]});
            extrude(context, id + "F203", {"entities" : qUnion([Q0]), "operationType" : NewBodyOperationType.ADD, "oppositeDirection" : true, "depth" : 19.05 * mm});
        }
        {
            var Q0;
            Q0=makeQuery(id+"F203.boolean.opBoolean","MERGE",FACE,{"derivedFrom":[makeQuery(id+"F201.opExtrude","CAP_FACE",FACE,{"disambiguationData":[OSD([sQuery(id+"F200.wireOp",EDGE,"E100.bottom"),sQuery(id+"F200.wireOp",EDGE,"E100.top"),sQuery(id+"F200.wireOp",EDGE,"E100.left"),sQuery(id+"F200.wireOp",EDGE,"E100.right")])],"isStart":false}),makeQuery(id+"F203.opExtrude","SWEPT_FACE",FACE,{"disambiguationData":[OSD([sQuery(id+"F202.wireOp",EDGE,"E101.bottom")])]})]});
            var sketch = newSketch(context, id + "F204", { "sketchPlane" : qUnion([Q0])});
            skLineSegment(sketch, "E102.bottom", {"start": v(-58.34, -45.44) * mm, "end": v(-52, -45.44) * mm});
            skLineSegment(sketch, "E102.top", {"start": v(-58.34, -39.09) * mm, "end": v(-52, -39.09) * mm});
            skLineSegment(sketch, "E102.left", {"start": v(-58.34, -45.44) * mm, "end": v(-58.34, -39.09) * mm});
            skLineSegment(sketch, "E102.right", {"start": v(-52, -45.44) * mm, "end": v(-52, -39.09) * mm});
            skSolve(sketch);
        }
        {
            var Q0;
            Q0=makeQuery(id+"F204.imprint","IMPRINT",FACE,{"disambiguationData":[TD([[makeQuery(id+"F204.imprint","IMPRINT",EDGE,{"derivedFrom":sQuery(id+"F204.wireOp",EDGE,"E102.bottom")}),-1.0]])]});
            extrude(context, id + "F205", {"entities" : qUnion([Q0]), "operationType" : NewBodyOperationType.ADD, "oppositeDirection" : true, "depth" : 19.05 * mm});
        }
        {
            var Q0;
            Q0=makeQuery(id+"F205.boolean.opBoolean","MERGE",FACE,{"derivedFrom":[makeQuery(id+"F203.boolean.opBoolean","MERGE",FACE,{"derivedFrom":[makeQuery(id+"F201.opExtrude","SWEPT_FACE",FACE,{"disambiguationData":[OSD([sQuery(id+"F200.wireOp",EDGE,"E100.right")])]}),makeQuery(id+"F203.opExtrude","SWEPT_FACE",FACE,{"disambiguationData":[OSD([sQuery(id+"F202.wireOp",EDGE,"E101.right")])]})]}),makeQuery(id+"F205.opExtrude","SWEPT_FACE",FACE,{"disambiguationData":[OSD([sQuery(id+"F204.wireOp",EDGE,"E102.right")])]})]});
            var sketch = newSketch(context, id + "F206", { "sketchPlane" : qUnion([Q0])});
            skLineSegment(sketch, "E103.bottom", {"start": v(-45.44, 76.2) * mm, "end": v(-39.09, 76.2) * mm});
            skLineSegment(sketch, "E103.top", {"start": v(-45.44, 82.55) * mm, "end": v(-39.09, 82.55) * mm});
            skLineSegment(sketch, "E103.left", {"start": v(-45.44, 76.2) * mm, "end": v(-45.44, 82.55) * mm});
            skLineSegment(sketch, "E103.right", {"start": v(-39.09, 76.2) * mm, "end": v(-39.09, 82.55) * mm});
            skSolve(sketch);
        }
        {
            var Q0;
            Q0=makeQuery(id+"F206.imprint","IMPRINT",FACE,{"disambiguationData":[TD([[makeQuery(id+"F206.imprint","IMPRINT",EDGE,{"derivedFrom":sQuery(id+"F206.wireOp",EDGE,"E103.bottom")}),1.0]])]});
            extrude(context, id + "F207", {"entities" : qUnion([Q0]), "operationType" : NewBodyOperationType.ADD, "oppositeDirection" : true, "depth" : 19.05 * mm});
        }
        {
            var Q0;
            Q0=makeQuery(id+"F207.boolean.opBoolean","MERGE",FACE,{"derivedFrom":[makeQuery(id+"F205.opExtrude","CAP_FACE",FACE,{"disambiguationData":[OSD([sQuery(id+"F204.wireOp",EDGE,"E102.bottom"),sQuery(id+"F204.wireOp",EDGE,"E102.top"),sQuery(id+"F204.wireOp",EDGE,"E102.left"),sQuery(id+"F204.wireOp",EDGE,"E102.right")])],"isStart":false}),makeQuery(id+"F207.opExtrude","SWEPT_FACE",FACE,{"disambiguationData":[OSD([sQuery(id+"F206.wireOp",EDGE,"E103.bottom")])]})]});
            var sketch = newSketch(context, id + "F208", { "sketchPlane" : qUnion([Q0])});
            skLineSegment(sketch, "E104.bottom", {"start": v(-71.04, 45.44) * mm, "end": v(-64.7, 45.44) * mm});
            skLineSegment(sketch, "E104.top", {"start": v(-71.04, 39.09) * mm, "end": v(-64.7, 39.09) * mm});
            skLineSegment(sketch, "E104.left", {"start": v(-71.04, 45.44) * mm, "end": v(-71.04, 39.09) * mm});
            skLineSegment(sketch, "E104.right", {"start": v(-64.7, 45.44) * mm, "end": v(-64.7, 39.09) * mm});
            skSolve(sketch);
        }
        {
            var Q0;
            Q0=makeQuery(id+"F208.imprint","IMPRINT",FACE,{"disambiguationData":[TD([[makeQuery(id+"F208.imprint","IMPRINT",EDGE,{"derivedFrom":sQuery(id+"F208.wireOp",EDGE,"E104.bottom")}),1.0]])]});
            extrude(context, id + "F209", {"entities" : qUnion([Q0]), "operationType" : NewBodyOperationType.ADD, "oppositeDirection" : true, "depth" : 19.05 * mm});
        }
        {
            var Q0;
            Q0=makeQuery(id+"F209.boolean.opBoolean","MERGE",FACE,{"derivedFrom":[makeQuery(id+"F207.boolean.opBoolean","MERGE",FACE,{"derivedFrom":[makeQuery(id+"F205.boolean.opBoolean","MERGE",FACE,{"derivedFrom":[makeQuery(id+"F203.opExtrude","CAP_FACE",FACE,{"disambiguationData":[OSD([sQuery(id+"F202.wireOp",EDGE,"E101.bottom"),sQuery(id+"F202.wireOp",EDGE,"E101.top"),sQuery(id+"F202.wireOp",EDGE,"E101.left"),sQuery(id+"F202.wireOp",EDGE,"E101.right")])],"isStart":false}),makeQuery(id+"F205.opExtrude","SWEPT_FACE",FACE,{"disambiguationData":[OSD([sQuery(id+"F204.wireOp",EDGE,"E102.bottom")])]})]}),makeQuery(id+"F207.opExtrude","SWEPT_FACE",FACE,{"disambiguationData":[OSD([sQuery(id+"F206.wireOp",EDGE,"E103.left")])]})]}),makeQuery(id+"F209.opExtrude","SWEPT_FACE",FACE,{"disambiguationData":[OSD([sQuery(id+"F208.wireOp",EDGE,"E104.bottom")])]})]});
            var sketch = newSketch(context, id + "F210", { "sketchPlane" : qUnion([Q0])});
            skLineSegment(sketch, "E105.bottom", {"start": v(-71.04, 95.25) * mm, "end": v(-64.7, 95.25) * mm});
            skLineSegment(sketch, "E105.top", {"start": v(-71.04, 88.9) * mm, "end": v(-64.7, 88.9) * mm});
            skLineSegment(sketch, "E105.left", {"start": v(-71.04, 95.25) * mm, "end": v(-71.04, 88.9) * mm});
            skLineSegment(sketch, "E105.right", {"start": v(-64.7, 95.25) * mm, "end": v(-64.7, 88.9) * mm});
            skSolve(sketch);
        }
        {
            var Q0;
            Q0=makeQuery(id+"F210.imprint","IMPRINT",FACE,{"disambiguationData":[TD([[makeQuery(id+"F210.imprint","IMPRINT",EDGE,{"derivedFrom":sQuery(id+"F210.wireOp",EDGE,"E105.bottom")}),1.0]])]});
            extrude(context, id + "F211", {"entities" : qUnion([Q0]), "operationType" : NewBodyOperationType.ADD, "oppositeDirection" : true, "depth" : 19.05 * mm});
        }
        {
            var Q0;
            Q0=makeQuery(id+"F211.boolean.opBoolean","MERGE",FACE,{"derivedFrom":[makeQuery(id+"F209.opExtrude","CAP_FACE",FACE,{"disambiguationData":[OSD([sQuery(id+"F208.wireOp",EDGE,"E104.bottom"),sQuery(id+"F208.wireOp",EDGE,"E104.top"),sQuery(id+"F208.wireOp",EDGE,"E104.left"),sQuery(id+"F208.wireOp",EDGE,"E104.right")])],"isStart":false}),makeQuery(id+"F211.opExtrude","SWEPT_FACE",FACE,{"disambiguationData":[OSD([sQuery(id+"F210.wireOp",EDGE,"E105.bottom")])]})]});
            var sketch = newSketch(context, id + "F212", { "sketchPlane" : qUnion([Q0])});
            skLineSegment(sketch, "E106.bottom", {"start": v(-71.04, -26.39) * mm, "end": v(-64.7, -26.39) * mm});
            skLineSegment(sketch, "E106.top", {"start": v(-71.04, -32.74) * mm, "end": v(-64.7, -32.74) * mm});
            skLineSegment(sketch, "E106.left", {"start": v(-71.04, -26.39) * mm, "end": v(-71.04, -32.74) * mm});
            skLineSegment(sketch, "E106.right", {"start": v(-64.7, -26.39) * mm, "end": v(-64.7, -32.74) * mm});
            skSolve(sketch);
        }
        {
            var Q0;
            Q0=makeQuery(id+"F212.imprint","IMPRINT",FACE,{"disambiguationData":[TD([[makeQuery(id+"F212.imprint","IMPRINT",EDGE,{"derivedFrom":sQuery(id+"F212.wireOp",EDGE,"E106.bottom")}),1.0]])]});
            extrude(context, id + "F213", {"entities" : qUnion([Q0]), "operationType" : NewBodyOperationType.ADD, "oppositeDirection" : true, "depth" : 31.75 * mm});
        }
        {
            var Q0;
            Q0=makeQuery(id+"F213.boolean.opBoolean","MERGE",FACE,{"derivedFrom":[makeQuery(id+"F211.opExtrude","CAP_FACE",FACE,{"disambiguationData":[OSD([sQuery(id+"F210.wireOp",EDGE,"E105.bottom"),sQuery(id+"F210.wireOp",EDGE,"E105.top"),sQuery(id+"F210.wireOp",EDGE,"E105.left"),sQuery(id+"F210.wireOp",EDGE,"E105.right")])],"isStart":false}),makeQuery(id+"F213.opExtrude","SWEPT_FACE",FACE,{"disambiguationData":[OSD([sQuery(id+"F212.wireOp",EDGE,"E106.bottom")])]})]});
            var sketch = newSketch(context, id + "F214", { "sketchPlane" : qUnion([Q0])});
            skLineSegment(sketch, "E107.bottom", {"start": v(71.04, 63.5) * mm, "end": v(64.7, 63.5) * mm});
            skLineSegment(sketch, "E107.top", {"start": v(71.04, 69.85) * mm, "end": v(64.7, 69.85) * mm});
            skLineSegment(sketch, "E107.left", {"start": v(71.04, 63.5) * mm, "end": v(71.04, 69.85) * mm});
            skLineSegment(sketch, "E107.right", {"start": v(64.7, 63.5) * mm, "end": v(64.7, 69.85) * mm});
            skSolve(sketch);
        }
        {
            var Q0;
            Q0=makeQuery(id+"F214.imprint","IMPRINT",FACE,{"disambiguationData":[TD([[makeQuery(id+"F214.imprint","IMPRINT",EDGE,{"derivedFrom":sQuery(id+"F214.wireOp",EDGE,"E107.bottom")}),1.0]])]});
            extrude(context, id + "F215", {"entities" : qUnion([Q0]), "operationType" : NewBodyOperationType.ADD, "oppositeDirection" : true, "depth" : 19.05 * mm});
        }
        {
            var Q0;
            Q0=makeQuery(id+"F215.boolean.opBoolean","MERGE",FACE,{"derivedFrom":[makeQuery(id+"F213.boolean.opBoolean","MERGE",FACE,{"derivedFrom":[makeQuery(id+"F211.boolean.opBoolean","MERGE",FACE,{"derivedFrom":[makeQuery(id+"F209.boolean.opBoolean","MERGE",FACE,{"derivedFrom":[makeQuery(id+"F207.opExtrude","CAP_FACE",FACE,{"disambiguationData":[OSD([sQuery(id+"F206.wireOp",EDGE,"E103.bottom"),sQuery(id+"F206.wireOp",EDGE,"E103.top"),sQuery(id+"F206.wireOp",EDGE,"E103.left"),sQuery(id+"F206.wireOp",EDGE,"E103.right")])],"isStart":false}),makeQuery(id+"F209.opExtrude","SWEPT_FACE",FACE,{"disambiguationData":[OSD([sQuery(id+"F208.wireOp",EDGE,"E104.left")])]})]}),makeQuery(id+"F211.opExtrude","SWEPT_FACE",FACE,{"disambiguationData":[OSD([sQuery(id+"F210.wireOp",EDGE,"E105.left")])]})]}),makeQuery(id+"F213.opExtrude","SWEPT_FACE",FACE,{"disambiguationData":[OSD([sQuery(id+"F212.wireOp",EDGE,"E106.left")])]})]}),makeQuery(id+"F215.opExtrude","SWEPT_FACE",FACE,{"disambiguationData":[OSD([sQuery(id+"F214.wireOp",EDGE,"E107.left")])]})]});
            var sketch = newSketch(context, id + "F216", { "sketchPlane" : qUnion([Q0])});
            skLineSegment(sketch, "E108.bottom", {"start": v(45.44, 63.5) * mm, "end": v(39.09, 63.5) * mm});
            skLineSegment(sketch, "E108.top", {"start": v(45.44, 69.85) * mm, "end": v(39.09, 69.85) * mm});
            skLineSegment(sketch, "E108.left", {"start": v(45.44, 63.5) * mm, "end": v(45.44, 69.85) * mm});
            skLineSegment(sketch, "E108.right", {"start": v(39.09, 63.5) * mm, "end": v(39.09, 69.85) * mm});
            skSolve(sketch);
        }
        {
            var Q0;
            Q0=makeQuery(id+"F216.imprint","IMPRINT",FACE,{"disambiguationData":[TD([[makeQuery(id+"F216.imprint","IMPRINT",EDGE,{"derivedFrom":sQuery(id+"F216.wireOp",EDGE,"E108.bottom")}),-1.0]])]});
            extrude(context, id + "F217", {"entities" : qUnion([Q0]), "operationType" : NewBodyOperationType.ADD, "oppositeDirection" : true, "depth" : 19.05 * mm});
        }
        {
            var Q0;
            Q0=makeQuery(id+"F217.boolean.opBoolean","MERGE",FACE,{"derivedFrom":[makeQuery(id+"F215.opExtrude","CAP_FACE",FACE,{"disambiguationData":[OSD([sQuery(id+"F214.wireOp",EDGE,"E107.bottom"),sQuery(id+"F214.wireOp",EDGE,"E107.top"),sQuery(id+"F214.wireOp",EDGE,"E107.left"),sQuery(id+"F214.wireOp",EDGE,"E107.right")])],"isStart":false}),makeQuery(id+"F217.opExtrude","SWEPT_FACE",FACE,{"disambiguationData":[OSD([sQuery(id+"F216.wireOp",EDGE,"E108.left")])]})]});
            var sketch = newSketch(context, id + "F218", { "sketchPlane" : qUnion([Q0])});
            skLineSegment(sketch, "E109.bottom", {"start": v(-52, 69.85) * mm, "end": v(-58.34, 69.85) * mm});
            skLineSegment(sketch, "E109.top", {"start": v(-52, 63.5) * mm, "end": v(-58.34, 63.5) * mm});
            skLineSegment(sketch, "E109.left", {"start": v(-52, 69.85) * mm, "end": v(-52, 63.5) * mm});
            skLineSegment(sketch, "E109.right", {"start": v(-58.34, 69.85) * mm, "end": v(-58.34, 63.5) * mm});
            skSolve(sketch);
        }
        {
            var Q0;
            Q0=makeQuery(id+"F218.imprint","IMPRINT",FACE,{"disambiguationData":[TD([[makeQuery(id+"F218.imprint","IMPRINT",EDGE,{"derivedFrom":sQuery(id+"F218.wireOp",EDGE,"E109.bottom")}),-1.0]])]});
            extrude(context, id + "F219", {"entities" : qUnion([Q0]), "operationType" : NewBodyOperationType.ADD, "oppositeDirection" : true, "depth" : 19.05 * mm});
        }
        {
            var Q0;
            Q0=makeQuery(id+"F219.boolean.opBoolean","MERGE",FACE,{"derivedFrom":[makeQuery(id+"F217.boolean.opBoolean","MERGE",FACE,{"derivedFrom":[makeQuery(id+"F215.opExtrude","SWEPT_FACE",FACE,{"disambiguationData":[OSD([sQuery(id+"F214.wireOp",EDGE,"E107.top")])]}),makeQuery(id+"F217.opExtrude","SWEPT_FACE",FACE,{"disambiguationData":[OSD([sQuery(id+"F216.wireOp",EDGE,"E108.top")])]})]}),makeQuery(id+"F219.opExtrude","SWEPT_FACE",FACE,{"disambiguationData":[OSD([sQuery(id+"F218.wireOp",EDGE,"E109.bottom")])]})]});
            var sketch = newSketch(context, id + "F220", { "sketchPlane" : qUnion([Q0])});
            skLineSegment(sketch, "E110.bottom", {"start": v(-52, -26.39) * mm, "end": v(-58.34, -26.39) * mm});
            skLineSegment(sketch, "E110.top", {"start": v(-52, -32.74) * mm, "end": v(-58.34, -32.74) * mm});
            skLineSegment(sketch, "E110.left", {"start": v(-52, -26.39) * mm, "end": v(-52, -32.74) * mm});
            skLineSegment(sketch, "E110.right", {"start": v(-58.34, -26.39) * mm, "end": v(-58.34, -32.74) * mm});
            skSolve(sketch);
        }
        {
            var Q0;
            Q0=makeQuery(id+"F220.imprint","IMPRINT",FACE,{"disambiguationData":[TD([[makeQuery(id+"F220.imprint","IMPRINT",EDGE,{"derivedFrom":sQuery(id+"F220.wireOp",EDGE,"E110.bottom")}),-1.0]])]});
            extrude(context, id + "F221", {"entities" : qUnion([Q0]), "operationType" : NewBodyOperationType.ADD, "oppositeDirection" : true, "depth" : 19.05 * mm});
        }
        {
            var Q0;
            Q0=makeQuery(id+"F221.boolean.opBoolean","MERGE",FACE,{"derivedFrom":[makeQuery(id+"F219.opExtrude","CAP_FACE",FACE,{"disambiguationData":[OSD([sQuery(id+"F218.wireOp",EDGE,"E109.bottom"),sQuery(id+"F218.wireOp",EDGE,"E109.top"),sQuery(id+"F218.wireOp",EDGE,"E109.left"),sQuery(id+"F218.wireOp",EDGE,"E109.right")])],"isStart":false}),makeQuery(id+"F221.opExtrude","SWEPT_FACE",FACE,{"disambiguationData":[OSD([sQuery(id+"F220.wireOp",EDGE,"E110.bottom")])]})]});
            var sketch = newSketch(context, id + "F222", { "sketchPlane" : qUnion([Q0])});
            skLineSegment(sketch, "E111.bottom", {"start": v(58.34, 50.8) * mm, "end": v(52, 50.8) * mm});
            skLineSegment(sketch, "E111.top", {"start": v(58.34, 57.15) * mm, "end": v(52, 57.15) * mm});
            skLineSegment(sketch, "E111.left", {"start": v(58.34, 50.8) * mm, "end": v(58.34, 57.15) * mm});
            skLineSegment(sketch, "E111.right", {"start": v(52, 50.8) * mm, "end": v(52, 57.15) * mm});
            skSolve(sketch);
        }
        {
            var Q0;
            Q0=makeQuery(id+"F222.imprint","IMPRINT",FACE,{"disambiguationData":[TD([[makeQuery(id+"F222.imprint","IMPRINT",EDGE,{"derivedFrom":sQuery(id+"F222.wireOp",EDGE,"E111.bottom")}),-1.0]])]});
            extrude(context, id + "F223", {"entities" : qUnion([Q0]), "operationType" : NewBodyOperationType.ADD, "oppositeDirection" : true, "depth" : 19.05 * mm});
        }
        {
            var Q0;
            Q0=makeQuery(id+"F223.boolean.opBoolean","MERGE",FACE,{"derivedFrom":[makeQuery(id+"F221.boolean.opBoolean","MERGE",FACE,{"derivedFrom":[makeQuery(id+"F219.boolean.opBoolean","MERGE",FACE,{"derivedFrom":[makeQuery(id+"F217.opExtrude","CAP_FACE",FACE,{"disambiguationData":[OSD([sQuery(id+"F216.wireOp",EDGE,"E108.bottom"),sQuery(id+"F216.wireOp",EDGE,"E108.top"),sQuery(id+"F216.wireOp",EDGE,"E108.left"),sQuery(id+"F216.wireOp",EDGE,"E108.right")])],"isStart":false}),makeQuery(id+"F219.opExtrude","SWEPT_FACE",FACE,{"disambiguationData":[OSD([sQuery(id+"F218.wireOp",EDGE,"E109.left")])]})]}),makeQuery(id+"F221.opExtrude","SWEPT_FACE",FACE,{"disambiguationData":[OSD([sQuery(id+"F220.wireOp",EDGE,"E110.left")])]})]}),makeQuery(id+"F223.opExtrude","SWEPT_FACE",FACE,{"disambiguationData":[OSD([sQuery(id+"F222.wireOp",EDGE,"E111.right")])]})]});
            var sketch = newSketch(context, id + "F224", { "sketchPlane" : qUnion([Q0])});
            skLineSegment(sketch, "E112.bottom", {"start": v(-45.44, 50.8) * mm, "end": v(-39.09, 50.8) * mm});
            skLineSegment(sketch, "E112.top", {"start": v(-45.44, 57.15) * mm, "end": v(-39.09, 57.15) * mm});
            skLineSegment(sketch, "E112.left", {"start": v(-45.44, 50.8) * mm, "end": v(-45.44, 57.15) * mm});
            skLineSegment(sketch, "E112.right", {"start": v(-39.09, 50.8) * mm, "end": v(-39.09, 57.15) * mm});
            skSolve(sketch);
        }
        {
            var Q0;
            Q0=makeQuery(id+"F224.imprint","IMPRINT",FACE,{"disambiguationData":[TD([[makeQuery(id+"F224.imprint","IMPRINT",EDGE,{"derivedFrom":sQuery(id+"F224.wireOp",EDGE,"E112.bottom")}),1.0]])]});
            extrude(context, id + "F225", {"entities" : qUnion([Q0]), "operationType" : NewBodyOperationType.ADD, "oppositeDirection" : true, "depth" : 19.05 * mm});
        }
        {
            var Q0;
            Q0=makeQuery(id+"F225.boolean.opBoolean","MERGE",FACE,{"derivedFrom":[makeQuery(id+"F223.opExtrude","CAP_FACE",FACE,{"disambiguationData":[OSD([sQuery(id+"F222.wireOp",EDGE,"E111.bottom"),sQuery(id+"F222.wireOp",EDGE,"E111.top"),sQuery(id+"F222.wireOp",EDGE,"E111.left"),sQuery(id+"F222.wireOp",EDGE,"E111.right")])],"isStart":false}),makeQuery(id+"F225.opExtrude","SWEPT_FACE",FACE,{"disambiguationData":[OSD([sQuery(id+"F224.wireOp",EDGE,"E112.left")])]})]});
            var sketch = newSketch(context, id + "F226", { "sketchPlane" : qUnion([Q0])});
            skLineSegment(sketch, "E113.bottom", {"start": v(-71.04, 57.15) * mm, "end": v(-64.7, 57.15) * mm});
            skLineSegment(sketch, "E113.top", {"start": v(-71.04, 50.8) * mm, "end": v(-64.7, 50.8) * mm});
            skLineSegment(sketch, "E113.left", {"start": v(-71.04, 57.15) * mm, "end": v(-71.04, 50.8) * mm});
            skLineSegment(sketch, "E113.right", {"start": v(-64.7, 57.15) * mm, "end": v(-64.7, 50.8) * mm});
            skSolve(sketch);
        }
        {
            var Q0;
            Q0=makeQuery(id+"F226.imprint","IMPRINT",FACE,{"disambiguationData":[TD([[makeQuery(id+"F226.imprint","IMPRINT",EDGE,{"derivedFrom":sQuery(id+"F226.wireOp",EDGE,"E113.bottom")}),-1.0]])]});
            extrude(context, id + "F227", {"entities" : qUnion([Q0]), "operationType" : NewBodyOperationType.ADD, "oppositeDirection" : true, "depth" : 31.75 * mm});
        }
        {
            var Q0;
            Q0=makeQuery(id+"F227.boolean.opBoolean","MERGE",FACE,{"derivedFrom":[makeQuery(id+"F225.opExtrude","CAP_FACE",FACE,{"disambiguationData":[OSD([sQuery(id+"F224.wireOp",EDGE,"E112.bottom"),sQuery(id+"F224.wireOp",EDGE,"E112.top"),sQuery(id+"F224.wireOp",EDGE,"E112.left"),sQuery(id+"F224.wireOp",EDGE,"E112.right")])],"isStart":false}),makeQuery(id+"F227.opExtrude","SWEPT_FACE",FACE,{"disambiguationData":[OSD([sQuery(id+"F226.wireOp",EDGE,"E113.left")])]})]});
            var sketch = newSketch(context, id + "F228", { "sketchPlane" : qUnion([Q0])});
            skLineSegment(sketch, "E114.bottom", {"start": v(13.69, 57.15) * mm, "end": v(20.04, 57.15) * mm});
            skLineSegment(sketch, "E114.top", {"start": v(13.69, 50.8) * mm, "end": v(20.04, 50.8) * mm});
            skLineSegment(sketch, "E114.left", {"start": v(13.69, 57.15) * mm, "end": v(13.69, 50.8) * mm});
            skLineSegment(sketch, "E114.right", {"start": v(20.04, 57.15) * mm, "end": v(20.04, 50.8) * mm});
            skSolve(sketch);
        }
        {
            var Q0;
            Q0=makeQuery(id+"F228.imprint","IMPRINT",FACE,{"disambiguationData":[TD([[makeQuery(id+"F228.imprint","IMPRINT",EDGE,{"derivedFrom":sQuery(id+"F228.wireOp",EDGE,"E114.bottom")}),1.0]])]});
            extrude(context, id + "F229", {"entities" : qUnion([Q0]), "operationType" : NewBodyOperationType.ADD, "oppositeDirection" : true, "depth" : 19.05 * mm});
        }
        {
            var Q0;
            Q0=makeQuery(id+"F229.opExtrude","SWEPT_FACE",FACE,{"disambiguationData":[OSD([sQuery(id+"F228.wireOp",EDGE,"E114.right")])]});
            var sketch = newSketch(context, id + "F230", { "sketchPlane" : qUnion([Q0])});
            skLineSegment(sketch, "E115.bottom", {"start": v(-52, 57.15) * mm, "end": v(-58.34, 57.15) * mm});
            skLineSegment(sketch, "E115.top", {"start": v(-52, 50.8) * mm, "end": v(-58.34, 50.8) * mm});
            skLineSegment(sketch, "E115.left", {"start": v(-52, 57.15) * mm, "end": v(-52, 50.8) * mm});
            skLineSegment(sketch, "E115.right", {"start": v(-58.34, 57.15) * mm, "end": v(-58.34, 50.8) * mm});
            skSolve(sketch);
        }
        {
            var Q0;
            Q0=makeQuery(id+"F230.imprint","IMPRINT",FACE,{"disambiguationData":[TD([[makeQuery(id+"F230.imprint","IMPRINT",EDGE,{"derivedFrom":sQuery(id+"F230.wireOp",EDGE,"E115.bottom")}),1.0]])]});
            extrude(context, id + "F231", {"entities" : qUnion([Q0]), "operationType" : NewBodyOperationType.ADD, "oppositeDirection" : true, "depth" : 19.05 * mm});
        }
        {
            var Q0;
            Q0=makeQuery(id+"F231.boolean.opBoolean","MERGE",FACE,{"derivedFrom":[makeQuery(id+"F229.opExtrude","CAP_FACE",FACE,{"disambiguationData":[OSD([sQuery(id+"F228.wireOp",EDGE,"E114.bottom"),sQuery(id+"F228.wireOp",EDGE,"E114.top"),sQuery(id+"F228.wireOp",EDGE,"E114.left"),sQuery(id+"F228.wireOp",EDGE,"E114.right")])],"isStart":false}),makeQuery(id+"F231.opExtrude","SWEPT_FACE",FACE,{"disambiguationData":[OSD([sQuery(id+"F230.wireOp",EDGE,"E115.left")])]})]});
            var sketch = newSketch(context, id + "F232", { "sketchPlane" : qUnion([Q0])});
            skLineSegment(sketch, "E116.bottom", {"start": v(-0.99, 50.8) * mm, "end": v(-7.34, 50.8) * mm});
            skLineSegment(sketch, "E116.top", {"start": v(-0.99, 57.15) * mm, "end": v(-7.34, 57.15) * mm});
            skLineSegment(sketch, "E116.left", {"start": v(-0.99, 50.8) * mm, "end": v(-0.99, 57.15) * mm});
            skLineSegment(sketch, "E116.right", {"start": v(-7.34, 50.8) * mm, "end": v(-7.34, 57.15) * mm});
            skSolve(sketch);
        }
        {
            var Q0;
            Q0=makeQuery(id+"F232.imprint","IMPRINT",FACE,{"disambiguationData":[TD([[makeQuery(id+"F232.imprint","IMPRINT",EDGE,{"derivedFrom":sQuery(id+"F232.wireOp",EDGE,"E116.bottom")}),1.0]])]});
            extrude(context, id + "F233", {"entities" : qUnion([Q0]), "operationType" : NewBodyOperationType.ADD, "oppositeDirection" : true, "depth" : 19.05 * mm});
        }
        {
            var Q0;
            Q0=makeQuery(id+"F233.boolean.opBoolean","MERGE",FACE,{"derivedFrom":[makeQuery(id+"F231.boolean.opBoolean","MERGE",FACE,{"derivedFrom":[makeQuery(id+"F229.boolean.opBoolean","MERGE",FACE,{"derivedFrom":[makeQuery(id+"F227.boolean.opBoolean","MERGE",FACE,{"derivedFrom":[makeQuery(id+"F225.boolean.opBoolean","MERGE",FACE,{"derivedFrom":[makeQuery(id+"F223.boolean.opBoolean","MERGE",FACE,{"derivedFrom":[makeQuery(id+"F221.opExtrude","CAP_FACE",FACE,{"disambiguationData":[OSD([sQuery(id+"F220.wireOp",EDGE,"E110.bottom"),sQuery(id+"F220.wireOp",EDGE,"E110.top"),sQuery(id+"F220.wireOp",EDGE,"E110.left"),sQuery(id+"F220.wireOp",EDGE,"E110.right")])],"isStart":false}),makeQuery(id+"F223.opExtrude","SWEPT_FACE",FACE,{"disambiguationData":[OSD([sQuery(id+"F222.wireOp",EDGE,"E111.bottom")])]})]}),makeQuery(id+"F225.opExtrude","SWEPT_FACE",FACE,{"disambiguationData":[OSD([sQuery(id+"F224.wireOp",EDGE,"E112.bottom")])]})]}),makeQuery(id+"F227.opExtrude","SWEPT_FACE",FACE,{"disambiguationData":[OSD([sQuery(id+"F226.wireOp",EDGE,"E113.top")])]})]}),makeQuery(id+"F229.opExtrude","SWEPT_FACE",FACE,{"disambiguationData":[OSD([sQuery(id+"F228.wireOp",EDGE,"E114.top")])]})]}),makeQuery(id+"F231.opExtrude","SWEPT_FACE",FACE,{"disambiguationData":[OSD([sQuery(id+"F230.wireOp",EDGE,"E115.top")])]})]}),makeQuery(id+"F233.opExtrude","SWEPT_FACE",FACE,{"disambiguationData":[OSD([sQuery(id+"F232.wireOp",EDGE,"E116.bottom")])]})]});
            var sketch = newSketch(context, id + "F234", { "sketchPlane" : qUnion([Q0])});
            skLineSegment(sketch, "E117.bottom", {"start": v(-71.04, 0.99) * mm, "end": v(-64.7, 0.99) * mm});
            skLineSegment(sketch, "E117.top", {"start": v(-71.04, 7.34) * mm, "end": v(-64.7, 7.34) * mm});
            skLineSegment(sketch, "E117.left", {"start": v(-71.04, 0.99) * mm, "end": v(-71.04, 7.34) * mm});
            skLineSegment(sketch, "E117.right", {"start": v(-64.7, 0.99) * mm, "end": v(-64.7, 7.34) * mm});
            skSolve(sketch);
        }
        {
            var Q0;
            Q0=makeQuery(id+"F234.imprint","IMPRINT",FACE,{"disambiguationData":[TD([[makeQuery(id+"F234.imprint","IMPRINT",EDGE,{"derivedFrom":sQuery(id+"F234.wireOp",EDGE,"E117.bottom")}),-1.0]])]});
            extrude(context, id + "F235", {"entities" : qUnion([Q0]), "operationType" : NewBodyOperationType.ADD, "oppositeDirection" : true, "depth" : 19.05 * mm});
        }
        {
            var Q0;
            Q0=makeQuery(id+"F235.boolean.opBoolean","MERGE",FACE,{"derivedFrom":[makeQuery(id+"F233.opExtrude","CAP_FACE",FACE,{"disambiguationData":[OSD([sQuery(id+"F232.wireOp",EDGE,"E116.bottom"),sQuery(id+"F232.wireOp",EDGE,"E116.top"),sQuery(id+"F232.wireOp",EDGE,"E116.left"),sQuery(id+"F232.wireOp",EDGE,"E116.right")])],"isStart":false}),makeQuery(id+"F235.opExtrude","SWEPT_FACE",FACE,{"disambiguationData":[OSD([sQuery(id+"F234.wireOp",EDGE,"E117.left")])]})]});
            var sketch = newSketch(context, id + "F236", { "sketchPlane" : qUnion([Q0])});
            skLineSegment(sketch, "E118.bottom", {"start": v(7.34, 69.85) * mm, "end": v(0.99, 69.85) * mm});
            skLineSegment(sketch, "E118.top", {"start": v(7.34, 63.5) * mm, "end": v(0.99, 63.5) * mm});
            skLineSegment(sketch, "E118.left", {"start": v(7.34, 69.85) * mm, "end": v(7.34, 63.5) * mm});
            skLineSegment(sketch, "E118.right", {"start": v(0.99, 69.85) * mm, "end": v(0.99, 63.5) * mm});
            skSolve(sketch);
        }
        {
            var Q0;
            Q0=makeQuery(id+"F236.imprint","IMPRINT",FACE,{"disambiguationData":[TD([[makeQuery(id+"F236.imprint","IMPRINT",EDGE,{"derivedFrom":sQuery(id+"F236.wireOp",EDGE,"E118.bottom")}),1.0]])]});
            extrude(context, id + "F237", {"entities" : qUnion([Q0]), "operationType" : NewBodyOperationType.ADD, "oppositeDirection" : true, "depth" : 19.05 * mm});
        }
        {
            var Q0;
            Q0=makeQuery(id+"F237.boolean.opBoolean","MERGE",FACE,{"derivedFrom":[makeQuery(id+"F235.boolean.opBoolean","MERGE",FACE,{"derivedFrom":[makeQuery(id+"F233.boolean.opBoolean","MERGE",FACE,{"derivedFrom":[makeQuery(id+"F231.opExtrude","CAP_FACE",FACE,{"disambiguationData":[OSD([sQuery(id+"F230.wireOp",EDGE,"E115.bottom"),sQuery(id+"F230.wireOp",EDGE,"E115.top"),sQuery(id+"F230.wireOp",EDGE,"E115.left"),sQuery(id+"F230.wireOp",EDGE,"E115.right")])],"isStart":false}),makeQuery(id+"F233.opExtrude","SWEPT_FACE",FACE,{"disambiguationData":[OSD([sQuery(id+"F232.wireOp",EDGE,"E116.left")])]})]}),makeQuery(id+"F235.opExtrude","SWEPT_FACE",FACE,{"disambiguationData":[OSD([sQuery(id+"F234.wireOp",EDGE,"E117.bottom")])]})]}),makeQuery(id+"F237.opExtrude","SWEPT_FACE",FACE,{"disambiguationData":[OSD([sQuery(id+"F236.wireOp",EDGE,"E118.right")])]})]});
            var sketch = newSketch(context, id + "F238", { "sketchPlane" : qUnion([Q0])});
            skLineSegment(sketch, "E119.bottom", {"start": v(52, 69.85) * mm, "end": v(58.34, 69.85) * mm});
            skLineSegment(sketch, "E119.top", {"start": v(52, 63.5) * mm, "end": v(58.34, 63.5) * mm});
            skLineSegment(sketch, "E119.left", {"start": v(52, 69.85) * mm, "end": v(52, 63.5) * mm});
            skLineSegment(sketch, "E119.right", {"start": v(58.34, 69.85) * mm, "end": v(58.34, 63.5) * mm});
            skSolve(sketch);
        }
        {
            var Q0;
            Q0=makeQuery(id+"F238.imprint","IMPRINT",FACE,{"disambiguationData":[TD([[makeQuery(id+"F238.imprint","IMPRINT",EDGE,{"derivedFrom":sQuery(id+"F238.wireOp",EDGE,"E119.bottom")}),-1.0]])]});
            extrude(context, id + "F239", {"entities" : qUnion([Q0]), "operationType" : NewBodyOperationType.ADD, "oppositeDirection" : true, "depth" : 19.05 * mm});
        }
        {
            var Q0;
            Q0=makeQuery(id+"F239.boolean.opBoolean","MERGE",FACE,{"derivedFrom":[makeQuery(id+"F237.opExtrude","CAP_FACE",FACE,{"disambiguationData":[OSD([sQuery(id+"F236.wireOp",EDGE,"E118.bottom"),sQuery(id+"F236.wireOp",EDGE,"E118.top"),sQuery(id+"F236.wireOp",EDGE,"E118.left"),sQuery(id+"F236.wireOp",EDGE,"E118.right")])],"isStart":false}),makeQuery(id+"F239.opExtrude","SWEPT_FACE",FACE,{"disambiguationData":[OSD([sQuery(id+"F238.wireOp",EDGE,"E119.left")])]})]});
            var sketch = newSketch(context, id + "F240", { "sketchPlane" : qUnion([Q0])});
            skLineSegment(sketch, "E120.bottom", {"start": v(-20.04, 69.85) * mm, "end": v(-13.69, 69.85) * mm});
            skLineSegment(sketch, "E120.top", {"start": v(-20.04, 63.5) * mm, "end": v(-13.69, 63.5) * mm});
            skLineSegment(sketch, "E120.left", {"start": v(-20.04, 69.85) * mm, "end": v(-20.04, 63.5) * mm});
            skLineSegment(sketch, "E120.right", {"start": v(-13.69, 69.85) * mm, "end": v(-13.69, 63.5) * mm});
            skSolve(sketch);
        }
        {
            var Q0;
            Q0=makeQuery(id+"F240.imprint","IMPRINT",FACE,{"disambiguationData":[TD([[makeQuery(id+"F240.imprint","IMPRINT",EDGE,{"derivedFrom":sQuery(id+"F240.wireOp",EDGE,"E120.bottom")}),-1.0]])]});
            extrude(context, id + "F241", {"entities" : qUnion([Q0]), "operationType" : NewBodyOperationType.ADD, "oppositeDirection" : true, "depth" : 19.05 * mm});
        }
        {
            var Q0;
            Q0=makeQuery(id+"F241.boolean.opBoolean","MERGE",FACE,{"derivedFrom":[makeQuery(id+"F239.boolean.opBoolean","MERGE",FACE,{"derivedFrom":[makeQuery(id+"F237.opExtrude","SWEPT_FACE",FACE,{"disambiguationData":[OSD([sQuery(id+"F236.wireOp",EDGE,"E118.top")])]}),makeQuery(id+"F239.opExtrude","SWEPT_FACE",FACE,{"disambiguationData":[OSD([sQuery(id+"F238.wireOp",EDGE,"E119.top")])]})]}),makeQuery(id+"F241.opExtrude","SWEPT_FACE",FACE,{"disambiguationData":[OSD([sQuery(id+"F240.wireOp",EDGE,"E120.top")])]})]});
            var sketch = newSketch(context, id + "F242", { "sketchPlane" : qUnion([Q0])});
            skLineSegment(sketch, "E121.bottom", {"start": v(-71.04, 20.04) * mm, "end": v(-64.7, 20.04) * mm});
            skLineSegment(sketch, "E121.top", {"start": v(-71.04, 13.69) * mm, "end": v(-64.7, 13.69) * mm});
            skLineSegment(sketch, "E121.left", {"start": v(-71.04, 20.04) * mm, "end": v(-71.04, 13.69) * mm});
            skLineSegment(sketch, "E121.right", {"start": v(-64.7, 20.04) * mm, "end": v(-64.7, 13.69) * mm});
            skSolve(sketch);
        }
        {
            var Q0;
            Q0=makeQuery(id+"F242.imprint","IMPRINT",FACE,{"disambiguationData":[TD([[makeQuery(id+"F242.imprint","IMPRINT",EDGE,{"derivedFrom":sQuery(id+"F242.wireOp",EDGE,"E121.bottom")}),1.0]])]});
            extrude(context, id + "F243", {"entities" : qUnion([Q0]), "operationType" : NewBodyOperationType.ADD, "oppositeDirection" : true, "depth" : 31.75 * mm});
        }
        {
            var Q0;
            Q0=makeQuery(id+"F243.boolean.opBoolean","MERGE",FACE,{"derivedFrom":[makeQuery(id+"F241.opExtrude","CAP_FACE",FACE,{"disambiguationData":[OSD([sQuery(id+"F240.wireOp",EDGE,"E120.bottom"),sQuery(id+"F240.wireOp",EDGE,"E120.top"),sQuery(id+"F240.wireOp",EDGE,"E120.left"),sQuery(id+"F240.wireOp",EDGE,"E120.right")])],"isStart":false}),makeQuery(id+"F243.opExtrude","SWEPT_FACE",FACE,{"disambiguationData":[OSD([sQuery(id+"F242.wireOp",EDGE,"E121.left")])]})]});
            var sketch = newSketch(context, id + "F244", { "sketchPlane" : qUnion([Q0])});
            skLineSegment(sketch, "E122.bottom", {"start": v(20.04, 95.25) * mm, "end": v(13.69, 95.25) * mm});
            skLineSegment(sketch, "E122.top", {"start": v(20.04, 88.9) * mm, "end": v(13.69, 88.9) * mm});
            skLineSegment(sketch, "E122.left", {"start": v(20.04, 95.25) * mm, "end": v(20.04, 88.9) * mm});
            skLineSegment(sketch, "E122.right", {"start": v(13.69, 95.25) * mm, "end": v(13.69, 88.9) * mm});
            skSolve(sketch);
        }
        {
            var Q0;
            Q0=makeQuery(id+"F244.imprint","IMPRINT",FACE,{"disambiguationData":[TD([[makeQuery(id+"F244.imprint","IMPRINT",EDGE,{"derivedFrom":sQuery(id+"F244.wireOp",EDGE,"E122.bottom")}),1.0]])]});
            extrude(context, id + "F245", {"entities" : qUnion([Q0]), "operationType" : NewBodyOperationType.ADD, "oppositeDirection" : true, "depth" : 19.05 * mm});
        }
        {
            var Q0;
            Q0=makeQuery(id+"F245.boolean.opBoolean","MERGE",FACE,{"derivedFrom":[makeQuery(id+"F243.opExtrude","CAP_FACE",FACE,{"disambiguationData":[OSD([sQuery(id+"F242.wireOp",EDGE,"E121.bottom"),sQuery(id+"F242.wireOp",EDGE,"E121.top"),sQuery(id+"F242.wireOp",EDGE,"E121.left"),sQuery(id+"F242.wireOp",EDGE,"E121.right")])],"isStart":false}),makeQuery(id+"F245.opExtrude","SWEPT_FACE",FACE,{"disambiguationData":[OSD([sQuery(id+"F244.wireOp",EDGE,"E122.bottom")])]})]});
            var sketch = newSketch(context, id + "F246", { "sketchPlane" : qUnion([Q0])});
            skLineSegment(sketch, "E123.bottom", {"start": v(-52, -20.04) * mm, "end": v(-58.34, -20.04) * mm});
            skLineSegment(sketch, "E123.top", {"start": v(-52, -13.69) * mm, "end": v(-58.34, -13.69) * mm});
            skLineSegment(sketch, "E123.left", {"start": v(-52, -20.04) * mm, "end": v(-52, -13.69) * mm});
            skLineSegment(sketch, "E123.right", {"start": v(-58.34, -20.04) * mm, "end": v(-58.34, -13.69) * mm});
            skSolve(sketch);
        }
        {
            var Q0;
            Q0=makeQuery(id+"F246.imprint","IMPRINT",FACE,{"disambiguationData":[TD([[makeQuery(id+"F246.imprint","IMPRINT",EDGE,{"derivedFrom":sQuery(id+"F246.wireOp",EDGE,"E123.bottom")}),-1.0]])]});
            extrude(context, id + "F247", {"entities" : qUnion([Q0]), "operationType" : NewBodyOperationType.ADD, "oppositeDirection" : true, "depth" : 19.05 * mm});
        }
        {
            var Q0;
            Q0=makeQuery(id+"F247.boolean.opBoolean","MERGE",FACE,{"derivedFrom":[makeQuery(id+"F245.boolean.opBoolean","MERGE",FACE,{"derivedFrom":[makeQuery(id+"F243.boolean.opBoolean","MERGE",FACE,{"derivedFrom":[makeQuery(id+"F241.opExtrude","SWEPT_FACE",FACE,{"disambiguationData":[OSD([sQuery(id+"F240.wireOp",EDGE,"E120.right")])]}),makeQuery(id+"F243.opExtrude","SWEPT_FACE",FACE,{"disambiguationData":[OSD([sQuery(id+"F242.wireOp",EDGE,"E121.top")])]})]}),makeQuery(id+"F245.opExtrude","SWEPT_FACE",FACE,{"disambiguationData":[OSD([sQuery(id+"F244.wireOp",EDGE,"E122.right")])]})]}),makeQuery(id+"F247.opExtrude","SWEPT_FACE",FACE,{"disambiguationData":[OSD([sQuery(id+"F246.wireOp",EDGE,"E123.top")])]})]});
            var sketch = newSketch(context, id + "F248", { "sketchPlane" : qUnion([Q0])});
            skLineSegment(sketch, "E124.bottom", {"start": v(52, 76.2) * mm, "end": v(58.34, 76.2) * mm});
            skLineSegment(sketch, "E124.top", {"start": v(52, 82.55) * mm, "end": v(58.34, 82.55) * mm});
            skLineSegment(sketch, "E124.left", {"start": v(52, 76.2) * mm, "end": v(52, 82.55) * mm});
            skLineSegment(sketch, "E124.right", {"start": v(58.34, 76.2) * mm, "end": v(58.34, 82.55) * mm});
            skSolve(sketch);
        }
        {
            var Q0;
            Q0=makeQuery(id+"F248.imprint","IMPRINT",FACE,{"disambiguationData":[TD([[makeQuery(id+"F248.imprint","IMPRINT",EDGE,{"derivedFrom":sQuery(id+"F248.wireOp",EDGE,"E124.bottom")}),-1.0]])]});
            extrude(context, id + "F249", {"entities" : qUnion([Q0]), "operationType" : NewBodyOperationType.ADD, "depth" : 12.7 * mm});
        }
        {
            var Q0;
            Q0=makeQuery(id+"F249.boolean.opBoolean","MERGE",FACE,{"derivedFrom":[makeQuery(id+"F247.opExtrude","CAP_FACE",FACE,{"disambiguationData":[OSD([sQuery(id+"F246.wireOp",EDGE,"E123.bottom"),sQuery(id+"F246.wireOp",EDGE,"E123.top"),sQuery(id+"F246.wireOp",EDGE,"E123.left"),sQuery(id+"F246.wireOp",EDGE,"E123.right")])],"isStart":false}),makeQuery(id+"F249.opExtrude","SWEPT_FACE",FACE,{"disambiguationData":[OSD([sQuery(id+"F248.wireOp",EDGE,"E124.bottom")])]})]});
            var sketch = newSketch(context, id + "F250", { "sketchPlane" : qUnion([Q0])});
            skLineSegment(sketch, "E125.bottom", {"start": v(-52, 0.99) * mm, "end": v(-58.34, 0.99) * mm});
            skLineSegment(sketch, "E125.top", {"start": v(-52, 7.34) * mm, "end": v(-58.34, 7.34) * mm});
            skLineSegment(sketch, "E125.left", {"start": v(-52, 0.99) * mm, "end": v(-52, 7.34) * mm});
            skLineSegment(sketch, "E125.right", {"start": v(-58.34, 0.99) * mm, "end": v(-58.34, 7.34) * mm});
            skSolve(sketch);
        }
        {
            var Q0;
            Q0=makeQuery(id+"F250.imprint","IMPRINT",FACE,{"disambiguationData":[TD([[makeQuery(id+"F250.imprint","IMPRINT",EDGE,{"derivedFrom":sQuery(id+"F250.wireOp",EDGE,"E125.bottom")}),1.0]])]});
            extrude(context, id + "F251", {"entities" : qUnion([Q0]), "operationType" : NewBodyOperationType.ADD, "oppositeDirection" : true, "depth" : 19.05 * mm});
        }
        {
            var Q0;
            Q0=makeQuery(id+"F251.boolean.opBoolean","MERGE",FACE,{"derivedFrom":[makeQuery(id+"F249.boolean.opBoolean","MERGE",FACE,{"derivedFrom":[makeQuery(id+"F247.boolean.opBoolean","MERGE",FACE,{"derivedFrom":[makeQuery(id+"F245.opExtrude","CAP_FACE",FACE,{"disambiguationData":[OSD([sQuery(id+"F244.wireOp",EDGE,"E122.bottom"),sQuery(id+"F244.wireOp",EDGE,"E122.top"),sQuery(id+"F244.wireOp",EDGE,"E122.left"),sQuery(id+"F244.wireOp",EDGE,"E122.right")])],"isStart":false}),makeQuery(id+"F247.opExtrude","SWEPT_FACE",FACE,{"disambiguationData":[OSD([sQuery(id+"F246.wireOp",EDGE,"E123.left")])]})]}),makeQuery(id+"F249.opExtrude","SWEPT_FACE",FACE,{"disambiguationData":[OSD([sQuery(id+"F248.wireOp",EDGE,"E124.left")])]})]}),makeQuery(id+"F251.opExtrude","SWEPT_FACE",FACE,{"disambiguationData":[OSD([sQuery(id+"F250.wireOp",EDGE,"E125.left")])]})]});
            var sketch = newSketch(context, id + "F252", { "sketchPlane" : qUnion([Q0])});
            skLineSegment(sketch, "E126.bottom", {"start": v(-0.99, 95.25) * mm, "end": v(-7.34, 95.25) * mm});
            skLineSegment(sketch, "E126.top", {"start": v(-0.99, 88.9) * mm, "end": v(-7.34, 88.9) * mm});
            skLineSegment(sketch, "E126.left", {"start": v(-0.99, 95.25) * mm, "end": v(-0.99, 88.9) * mm});
            skLineSegment(sketch, "E126.right", {"start": v(-7.34, 95.25) * mm, "end": v(-7.34, 88.9) * mm});
            skSolve(sketch);
        }
        {
            var Q0;
            Q0=makeQuery(id+"F252.imprint","IMPRINT",FACE,{"disambiguationData":[TD([[makeQuery(id+"F252.imprint","IMPRINT",EDGE,{"derivedFrom":sQuery(id+"F252.wireOp",EDGE,"E126.bottom")}),-1.0]])]});
            extrude(context, id + "F253", {"entities" : qUnion([Q0]), "operationType" : NewBodyOperationType.ADD, "oppositeDirection" : true, "depth" : 19.05 * mm});
        }
        {
            var Q0;
            Q0=makeQuery(id+"F253.boolean.opBoolean","MERGE",FACE,{"derivedFrom":[makeQuery(id+"F251.opExtrude","CAP_FACE",FACE,{"disambiguationData":[OSD([sQuery(id+"F250.wireOp",EDGE,"E125.bottom"),sQuery(id+"F250.wireOp",EDGE,"E125.top"),sQuery(id+"F250.wireOp",EDGE,"E125.left"),sQuery(id+"F250.wireOp",EDGE,"E125.right")])],"isStart":false}),makeQuery(id+"F253.opExtrude","SWEPT_FACE",FACE,{"disambiguationData":[OSD([sQuery(id+"F252.wireOp",EDGE,"E126.bottom")])]})]});
            var sketch = newSketch(context, id + "F254", { "sketchPlane" : qUnion([Q0])});
            skLineSegment(sketch, "E127.bottom", {"start": v(-71.04, -0.99) * mm, "end": v(-64.7, -0.99) * mm});
            skLineSegment(sketch, "E127.top", {"start": v(-71.04, -7.34) * mm, "end": v(-64.7, -7.34) * mm});
            skLineSegment(sketch, "E127.left", {"start": v(-71.04, -0.99) * mm, "end": v(-71.04, -7.34) * mm});
            skLineSegment(sketch, "E127.right", {"start": v(-64.7, -0.99) * mm, "end": v(-64.7, -7.34) * mm});
            skSolve(sketch);
        }
        {
            var Q0;
            Q0=makeQuery(id+"F254.imprint","IMPRINT",FACE,{"disambiguationData":[TD([[makeQuery(id+"F254.imprint","IMPRINT",EDGE,{"derivedFrom":sQuery(id+"F254.wireOp",EDGE,"E127.bottom")}),-1.0]])]});
            extrude(context, id + "F255", {"entities" : qUnion([Q0]), "operationType" : NewBodyOperationType.ADD, "oppositeDirection" : true, "depth" : 19.05 * mm});
        }
        {
            var Q0;
            Q0=makeQuery(id+"F255.boolean.opBoolean","MERGE",FACE,{"derivedFrom":[makeQuery(id+"F253.boolean.opBoolean","MERGE",FACE,{"derivedFrom":[makeQuery(id+"F251.opExtrude","SWEPT_FACE",FACE,{"disambiguationData":[OSD([sQuery(id+"F250.wireOp",EDGE,"E125.top")])]}),makeQuery(id+"F253.opExtrude","SWEPT_FACE",FACE,{"disambiguationData":[OSD([sQuery(id+"F252.wireOp",EDGE,"E126.right")])]})]}),makeQuery(id+"F255.opExtrude","SWEPT_FACE",FACE,{"disambiguationData":[OSD([sQuery(id+"F254.wireOp",EDGE,"E127.top")])]})]});
            var sketch = newSketch(context, id + "F256", { "sketchPlane" : qUnion([Q0])});
            skLineSegment(sketch, "E128.bottom", {"start": v(-71.04, 76.2) * mm, "end": v(-64.7, 76.2) * mm});
            skLineSegment(sketch, "E128.top", {"start": v(-71.04, 82.55) * mm, "end": v(-64.7, 82.55) * mm});
            skLineSegment(sketch, "E128.left", {"start": v(-71.04, 76.2) * mm, "end": v(-71.04, 82.55) * mm});
            skLineSegment(sketch, "E128.right", {"start": v(-64.7, 76.2) * mm, "end": v(-64.7, 82.55) * mm});
            skSolve(sketch);
        }
        {
            var Q0;
            Q0=makeQuery(id+"F256.imprint","IMPRINT",FACE,{"disambiguationData":[TD([[makeQuery(id+"F256.imprint","IMPRINT",EDGE,{"derivedFrom":sQuery(id+"F256.wireOp",EDGE,"E128.bottom")}),-1.0]])]});
            extrude(context, id + "F257", {"entities" : qUnion([Q0]), "operationType" : NewBodyOperationType.ADD, "oppositeDirection" : true, "depth" : 19.05 * mm});
        }
        {
            var Q0;
            Q0=makeQuery(id+"F257.boolean.opBoolean","MERGE",FACE,{"derivedFrom":[makeQuery(id+"F255.opExtrude","CAP_FACE",FACE,{"disambiguationData":[OSD([sQuery(id+"F254.wireOp",EDGE,"E127.bottom"),sQuery(id+"F254.wireOp",EDGE,"E127.top"),sQuery(id+"F254.wireOp",EDGE,"E127.left"),sQuery(id+"F254.wireOp",EDGE,"E127.right")])],"isStart":false}),makeQuery(id+"F257.opExtrude","SWEPT_FACE",FACE,{"disambiguationData":[OSD([sQuery(id+"F256.wireOp",EDGE,"E128.bottom")])]})]});
            var sketch = newSketch(context, id + "F258", { "sketchPlane" : qUnion([Q0])});
            skLineSegment(sketch, "E129.bottom", {"start": v(-64.7, -11.71) * mm, "end": v(-71.04, -11.71) * mm});
            skLineSegment(sketch, "E129.top", {"start": v(-64.7, -5.36) * mm, "end": v(-71.04, -5.36) * mm});
            skLineSegment(sketch, "E129.left", {"start": v(-64.7, -11.71) * mm, "end": v(-64.7, -5.36) * mm});
            skLineSegment(sketch, "E129.right", {"start": v(-71.04, -11.71) * mm, "end": v(-71.04, -5.36) * mm});
            skSolve(sketch);
        }
        {
            var Q0;
            Q0=makeQuery(id+"F258.imprint","IMPRINT",FACE,{"disambiguationData":[TD([[makeQuery(id+"F258.imprint","IMPRINT",EDGE,{"derivedFrom":sQuery(id+"F258.wireOp",EDGE,"E129.bottom")}),-1.0]])]});
            extrude(context, id + "F259", {"entities" : qUnion([Q0]), "operationType" : NewBodyOperationType.ADD, "oppositeDirection" : true, "depth" : 19.05 * mm});
        }
        {
            var Q0;
            Q0=makeQuery(id+"F259.opExtrude","SWEPT_FACE",FACE,{"disambiguationData":[OSD([sQuery(id+"F258.wireOp",EDGE,"E129.top")])]});
            var sketch = newSketch(context, id + "F260", { "sketchPlane" : qUnion([Q0])});
            skLineSegment(sketch, "E130.bottom", {"start": v(-64.7, 95.25) * mm, "end": v(-71.04, 95.25) * mm});
            skLineSegment(sketch, "E130.top", {"start": v(-64.7, 88.9) * mm, "end": v(-71.04, 88.9) * mm});
            skLineSegment(sketch, "E130.left", {"start": v(-64.7, 95.25) * mm, "end": v(-64.7, 88.9) * mm});
            skLineSegment(sketch, "E130.right", {"start": v(-71.04, 95.25) * mm, "end": v(-71.04, 88.9) * mm});
            skSolve(sketch);
        }
        {
            var Q0;
            Q0=makeQuery(id+"F260.imprint","IMPRINT",FACE,{"disambiguationData":[TD([[makeQuery(id+"F260.imprint","IMPRINT",EDGE,{"derivedFrom":sQuery(id+"F260.wireOp",EDGE,"E130.bottom")}),1.0]])]});
            extrude(context, id + "F261", {"entities" : qUnion([Q0]), "operationType" : NewBodyOperationType.ADD, "oppositeDirection" : true, "depth" : 19.05 * mm});
        }
        {
            var Q0;
            Q0=makeQuery(id+"F261.boolean.opBoolean","MERGE",FACE,{"derivedFrom":[makeQuery(id+"F259.opExtrude","CAP_FACE",FACE,{"disambiguationData":[OSD([sQuery(id+"F258.wireOp",EDGE,"E129.bottom"),sQuery(id+"F258.wireOp",EDGE,"E129.top"),sQuery(id+"F258.wireOp",EDGE,"E129.left"),sQuery(id+"F258.wireOp",EDGE,"E129.right")])],"isStart":false}),makeQuery(id+"F261.opExtrude","SWEPT_FACE",FACE,{"disambiguationData":[OSD([sQuery(id+"F260.wireOp",EDGE,"E130.bottom")])]})]});
            var sketch = newSketch(context, id + "F262", { "sketchPlane" : qUnion([Q0])});
            skLineSegment(sketch, "E131.bottom", {"start": v(-71.04, 24.41) * mm, "end": v(-64.7, 24.41) * mm});
            skLineSegment(sketch, "E131.top", {"start": v(-71.04, 18.06) * mm, "end": v(-64.7, 18.06) * mm});
            skLineSegment(sketch, "E131.left", {"start": v(-71.04, 24.41) * mm, "end": v(-71.04, 18.06) * mm});
            skLineSegment(sketch, "E131.right", {"start": v(-64.7, 24.41) * mm, "end": v(-64.7, 18.06) * mm});
            skSolve(sketch);
        }
        {
            var Q0;
            Q0=makeQuery(id+"F262.imprint","IMPRINT",FACE,{"disambiguationData":[TD([[makeQuery(id+"F262.imprint","IMPRINT",EDGE,{"derivedFrom":sQuery(id+"F262.wireOp",EDGE,"E131.bottom")}),1.0]])]});
            extrude(context, id + "F263", {"entities" : qUnion([Q0]), "operationType" : NewBodyOperationType.ADD, "oppositeDirection" : true, "depth" : 19.05 * mm});
        }
        {
            var Q0;
            Q0=makeQuery(id+"F263.boolean.opBoolean","MERGE",FACE,{"derivedFrom":[makeQuery(id+"F261.boolean.opBoolean","MERGE",FACE,{"derivedFrom":[makeQuery(id+"F259.boolean.opBoolean","MERGE",FACE,{"derivedFrom":[makeQuery(id+"F257.boolean.opBoolean","MERGE",FACE,{"derivedFrom":[makeQuery(id+"F255.boolean.opBoolean","MERGE",FACE,{"derivedFrom":[makeQuery(id+"F253.opExtrude","CAP_FACE",FACE,{"disambiguationData":[OSD([sQuery(id+"F252.wireOp",EDGE,"E126.bottom"),sQuery(id+"F252.wireOp",EDGE,"E126.top"),sQuery(id+"F252.wireOp",EDGE,"E126.left"),sQuery(id+"F252.wireOp",EDGE,"E126.right")])],"isStart":false}),makeQuery(id+"F255.opExtrude","SWEPT_FACE",FACE,{"disambiguationData":[OSD([sQuery(id+"F254.wireOp",EDGE,"E127.left")])]})]}),makeQuery(id+"F257.opExtrude","SWEPT_FACE",FACE,{"disambiguationData":[OSD([sQuery(id+"F256.wireOp",EDGE,"E128.left")])]})]}),makeQuery(id+"F259.opExtrude","SWEPT_FACE",FACE,{"disambiguationData":[OSD([sQuery(id+"F258.wireOp",EDGE,"E129.right")])]})]}),makeQuery(id+"F261.opExtrude","SWEPT_FACE",FACE,{"disambiguationData":[OSD([sQuery(id+"F260.wireOp",EDGE,"E130.right")])]})]}),makeQuery(id+"F263.opExtrude","SWEPT_FACE",FACE,{"disambiguationData":[OSD([sQuery(id+"F262.wireOp",EDGE,"E131.left")])]})]});
            var sketch = newSketch(context, id + "F264", { "sketchPlane" : qUnion([Q0])});
            skLineSegment(sketch, "E132.bottom", {"start": v(-24.41, 76.2) * mm, "end": v(-18.06, 76.2) * mm});
            skLineSegment(sketch, "E132.top", {"start": v(-24.41, 82.55) * mm, "end": v(-18.06, 82.55) * mm});
            skLineSegment(sketch, "E132.left", {"start": v(-24.41, 76.2) * mm, "end": v(-24.41, 82.55) * mm});
            skLineSegment(sketch, "E132.right", {"start": v(-18.06, 76.2) * mm, "end": v(-18.06, 82.55) * mm});
            skSolve(sketch);
        }
        {
            var Q0;
            Q0=makeQuery(id+"F264.imprint","IMPRINT",FACE,{"disambiguationData":[TD([[makeQuery(id+"F264.imprint","IMPRINT",EDGE,{"derivedFrom":sQuery(id+"F264.wireOp",EDGE,"E132.bottom")}),-1.0]])]});
            extrude(context, id + "F265", {"entities" : qUnion([Q0]), "operationType" : NewBodyOperationType.ADD, "oppositeDirection" : true, "depth" : 19.05 * mm});
        }
        {
            var Q0;
            Q0=makeQuery(id+"F265.boolean.opBoolean","MERGE",FACE,{"derivedFrom":[makeQuery(id+"F263.opExtrude","CAP_FACE",FACE,{"disambiguationData":[OSD([sQuery(id+"F262.wireOp",EDGE,"E131.bottom"),sQuery(id+"F262.wireOp",EDGE,"E131.top"),sQuery(id+"F262.wireOp",EDGE,"E131.left"),sQuery(id+"F262.wireOp",EDGE,"E131.right")])],"isStart":false}),makeQuery(id+"F265.opExtrude","SWEPT_FACE",FACE,{"disambiguationData":[OSD([sQuery(id+"F264.wireOp",EDGE,"E132.bottom")])]})]});
            var sketch = newSketch(context, id + "F266", { "sketchPlane" : qUnion([Q0])});
            skLineSegment(sketch, "E133.bottom", {"start": v(-52, -24.41) * mm, "end": v(-58.34, -24.41) * mm});
            skLineSegment(sketch, "E133.top", {"start": v(-52, -18.06) * mm, "end": v(-58.34, -18.06) * mm});
            skLineSegment(sketch, "E133.left", {"start": v(-52, -24.41) * mm, "end": v(-52, -18.06) * mm});
            skLineSegment(sketch, "E133.right", {"start": v(-58.34, -24.41) * mm, "end": v(-58.34, -18.06) * mm});
            skSolve(sketch);
        }
        {
            var Q0;
            Q0=makeQuery(id+"F266.imprint","IMPRINT",FACE,{"disambiguationData":[TD([[makeQuery(id+"F266.imprint","IMPRINT",EDGE,{"derivedFrom":sQuery(id+"F266.wireOp",EDGE,"E133.bottom")}),-1.0]])]});
            extrude(context, id + "F267", {"entities" : qUnion([Q0]), "operationType" : NewBodyOperationType.ADD, "oppositeDirection" : true, "depth" : 19.05 * mm});
        }
        {
            var Q0;
            Q0=makeQuery(id+"F267.boolean.opBoolean","MERGE",FACE,{"derivedFrom":[makeQuery(id+"F265.boolean.opBoolean","MERGE",FACE,{"derivedFrom":[makeQuery(id+"F263.boolean.opBoolean","MERGE",FACE,{"derivedFrom":[makeQuery(id+"F261.opExtrude","CAP_FACE",FACE,{"disambiguationData":[OSD([sQuery(id+"F260.wireOp",EDGE,"E130.bottom"),sQuery(id+"F260.wireOp",EDGE,"E130.top"),sQuery(id+"F260.wireOp",EDGE,"E130.left"),sQuery(id+"F260.wireOp",EDGE,"E130.right")])],"isStart":false}),makeQuery(id+"F263.opExtrude","SWEPT_FACE",FACE,{"disambiguationData":[OSD([sQuery(id+"F262.wireOp",EDGE,"E131.bottom")])]})]}),makeQuery(id+"F265.opExtrude","SWEPT_FACE",FACE,{"disambiguationData":[OSD([sQuery(id+"F264.wireOp",EDGE,"E132.left")])]})]}),makeQuery(id+"F267.opExtrude","SWEPT_FACE",FACE,{"disambiguationData":[OSD([sQuery(id+"F266.wireOp",EDGE,"E133.bottom")])]})]});
            var sketch = newSketch(context, id + "F268", { "sketchPlane" : qUnion([Q0])});
            skLineSegment(sketch, "E134.bottom", {"start": v(52, 95.25) * mm, "end": v(58.34, 95.25) * mm});
            skLineSegment(sketch, "E134.top", {"start": v(52, 88.9) * mm, "end": v(58.34, 88.9) * mm});
            skLineSegment(sketch, "E134.left", {"start": v(52, 95.25) * mm, "end": v(52, 88.9) * mm});
            skLineSegment(sketch, "E134.right", {"start": v(58.34, 95.25) * mm, "end": v(58.34, 88.9) * mm});
            skSolve(sketch);
        }
        {
            var Q0;
            Q0=makeQuery(id+"F268.imprint","IMPRINT",FACE,{"disambiguationData":[TD([[makeQuery(id+"F268.imprint","IMPRINT",EDGE,{"derivedFrom":sQuery(id+"F268.wireOp",EDGE,"E134.bottom")}),-1.0]])]});
            extrude(context, id + "F269", {"entities" : qUnion([Q0]), "operationType" : NewBodyOperationType.ADD, "oppositeDirection" : true, "depth" : 19.05 * mm});
        }
        {
            var Q0;
            Q0=makeQuery(id+"F269.boolean.opBoolean","MERGE",FACE,{"derivedFrom":[makeQuery(id+"F267.opExtrude","CAP_FACE",FACE,{"disambiguationData":[OSD([sQuery(id+"F266.wireOp",EDGE,"E133.bottom"),sQuery(id+"F266.wireOp",EDGE,"E133.top"),sQuery(id+"F266.wireOp",EDGE,"E133.left"),sQuery(id+"F266.wireOp",EDGE,"E133.right")])],"isStart":false}),makeQuery(id+"F269.opExtrude","SWEPT_FACE",FACE,{"disambiguationData":[OSD([sQuery(id+"F268.wireOp",EDGE,"E134.bottom")])]})]});
            var sketch = newSketch(context, id + "F270", { "sketchPlane" : qUnion([Q0])});
            skLineSegment(sketch, "E135.bottom", {"start": v(-52, 5.36) * mm, "end": v(-58.34, 5.36) * mm});
            skLineSegment(sketch, "E135.top", {"start": v(-52, 11.71) * mm, "end": v(-58.34, 11.71) * mm});
            skLineSegment(sketch, "E135.left", {"start": v(-52, 5.36) * mm, "end": v(-52, 11.71) * mm});
            skLineSegment(sketch, "E135.right", {"start": v(-58.34, 5.36) * mm, "end": v(-58.34, 11.71) * mm});
            skSolve(sketch);
        }
        {
            var Q0;
            Q0=makeQuery(id+"F270.imprint","IMPRINT",FACE,{"disambiguationData":[TD([[makeQuery(id+"F270.imprint","IMPRINT",EDGE,{"derivedFrom":sQuery(id+"F270.wireOp",EDGE,"E135.bottom")}),-1.0]])]});
            extrude(context, id + "F271", {"entities" : qUnion([Q0]), "operationType" : NewBodyOperationType.ADD, "oppositeDirection" : true, "depth" : 31.75 * mm});
        }
        {
            var Q0;
            Q0=makeQuery(id+"F271.boolean.opBoolean","MERGE",FACE,{"derivedFrom":[makeQuery(id+"F269.boolean.opBoolean","MERGE",FACE,{"derivedFrom":[makeQuery(id+"F267.boolean.opBoolean","MERGE",FACE,{"derivedFrom":[makeQuery(id+"F265.opExtrude","CAP_FACE",FACE,{"disambiguationData":[OSD([sQuery(id+"F264.wireOp",EDGE,"E132.bottom"),sQuery(id+"F264.wireOp",EDGE,"E132.top"),sQuery(id+"F264.wireOp",EDGE,"E132.left"),sQuery(id+"F264.wireOp",EDGE,"E132.right")])],"isStart":false}),makeQuery(id+"F267.opExtrude","SWEPT_FACE",FACE,{"disambiguationData":[OSD([sQuery(id+"F266.wireOp",EDGE,"E133.left")])]})]}),makeQuery(id+"F269.opExtrude","SWEPT_FACE",FACE,{"disambiguationData":[OSD([sQuery(id+"F268.wireOp",EDGE,"E134.left")])]})]}),makeQuery(id+"F271.opExtrude","SWEPT_FACE",FACE,{"disambiguationData":[OSD([sQuery(id+"F270.wireOp",EDGE,"E135.left")])]})]});
            var sketch = newSketch(context, id + "F272", { "sketchPlane" : qUnion([Q0])});
            skLineSegment(sketch, "E136.bottom", {"start": v(5.36, 63.5) * mm, "end": v(11.71, 63.5) * mm});
            skLineSegment(sketch, "E136.top", {"start": v(5.36, 69.85) * mm, "end": v(11.71, 69.85) * mm});
            skLineSegment(sketch, "E136.left", {"start": v(5.36, 63.5) * mm, "end": v(5.36, 69.85) * mm});
            skLineSegment(sketch, "E136.right", {"start": v(11.71, 63.5) * mm, "end": v(11.71, 69.85) * mm});
            skSolve(sketch);
        }
        {
            var Q0;
            Q0=makeQuery(id+"F272.imprint","IMPRINT",FACE,{"disambiguationData":[TD([[makeQuery(id+"F272.imprint","IMPRINT",EDGE,{"derivedFrom":sQuery(id+"F272.wireOp",EDGE,"E136.bottom")}),1.0]])]});
            extrude(context, id + "F273", {"entities" : qUnion([Q0]), "operationType" : NewBodyOperationType.ADD, "oppositeDirection" : true, "depth" : 19.05 * mm});
        }
        {
            var Q0;
            Q0=makeQuery(id+"F273.boolean.opBoolean","MERGE",FACE,{"derivedFrom":[makeQuery(id+"F271.boolean.opBoolean","MERGE",FACE,{"derivedFrom":[makeQuery(id+"F269.opExtrude","CAP_FACE",FACE,{"disambiguationData":[OSD([sQuery(id+"F268.wireOp",EDGE,"E134.bottom"),sQuery(id+"F268.wireOp",EDGE,"E134.top"),sQuery(id+"F268.wireOp",EDGE,"E134.left"),sQuery(id+"F268.wireOp",EDGE,"E134.right")])],"isStart":false}),makeQuery(id+"F271.opExtrude","SWEPT_FACE",FACE,{"disambiguationData":[OSD([sQuery(id+"F270.wireOp",EDGE,"E135.bottom")])]})]}),makeQuery(id+"F273.opExtrude","SWEPT_FACE",FACE,{"disambiguationData":[OSD([sQuery(id+"F272.wireOp",EDGE,"E136.left")])]})]});
            var sketch = newSketch(context, id + "F274", { "sketchPlane" : qUnion([Q0])});
            skLineSegment(sketch, "E137.bottom", {"start": v(-71.04, 63.5) * mm, "end": v(-64.7, 63.5) * mm});
            skLineSegment(sketch, "E137.top", {"start": v(-71.04, 69.85) * mm, "end": v(-64.7, 69.85) * mm});
            skLineSegment(sketch, "E137.left", {"start": v(-71.04, 63.5) * mm, "end": v(-71.04, 69.85) * mm});
            skLineSegment(sketch, "E137.right", {"start": v(-64.7, 63.5) * mm, "end": v(-64.7, 69.85) * mm});
            skSolve(sketch);
        }
        {
            var Q0;
            Q0=makeQuery(id+"F274.imprint","IMPRINT",FACE,{"disambiguationData":[TD([[makeQuery(id+"F274.imprint","IMPRINT",EDGE,{"derivedFrom":sQuery(id+"F274.wireOp",EDGE,"E137.bottom")}),-1.0]])]});
            extrude(context, id + "F275", {"entities" : qUnion([Q0]), "operationType" : NewBodyOperationType.ADD, "oppositeDirection" : true, "depth" : 19.05 * mm});
        }
        {
            var Q0;
            Q0=makeQuery(id+"F275.boolean.opBoolean","MERGE",FACE,{"derivedFrom":[makeQuery(id+"F273.opExtrude","CAP_FACE",FACE,{"disambiguationData":[OSD([sQuery(id+"F272.wireOp",EDGE,"E136.bottom"),sQuery(id+"F272.wireOp",EDGE,"E136.top"),sQuery(id+"F272.wireOp",EDGE,"E136.left"),sQuery(id+"F272.wireOp",EDGE,"E136.right")])],"isStart":false}),makeQuery(id+"F275.opExtrude","SWEPT_FACE",FACE,{"disambiguationData":[OSD([sQuery(id+"F274.wireOp",EDGE,"E137.left")])]})]});
            var sketch = newSketch(context, id + "F276", { "sketchPlane" : qUnion([Q0])});
            skLineSegment(sketch, "E138.bottom", {"start": v(-24.41, 69.85) * mm, "end": v(-18.06, 69.85) * mm});
            skLineSegment(sketch, "E138.top", {"start": v(-24.41, 63.5) * mm, "end": v(-18.06, 63.5) * mm});
            skLineSegment(sketch, "E138.left", {"start": v(-24.41, 69.85) * mm, "end": v(-24.41, 63.5) * mm});
            skLineSegment(sketch, "E138.right", {"start": v(-18.06, 69.85) * mm, "end": v(-18.06, 63.5) * mm});
            skSolve(sketch);
        }
        {
            var Q0;
            Q0=makeQuery(id+"F276.imprint","IMPRINT",FACE,{"disambiguationData":[TD([[makeQuery(id+"F276.imprint","IMPRINT",EDGE,{"derivedFrom":sQuery(id+"F276.wireOp",EDGE,"E138.bottom")}),1.0]])]});
            extrude(context, id + "F277", {"entities" : qUnion([Q0]), "operationType" : NewBodyOperationType.ADD, "oppositeDirection" : true, "depth" : 19.05 * mm});
        }
        {
            var Q0;
            Q0=makeQuery(id+"F277.boolean.opBoolean","MERGE",FACE,{"derivedFrom":[makeQuery(id+"F275.boolean.opBoolean","MERGE",FACE,{"derivedFrom":[makeQuery(id+"F273.opExtrude","SWEPT_FACE",FACE,{"disambiguationData":[OSD([sQuery(id+"F272.wireOp",EDGE,"E136.top")])]}),makeQuery(id+"F275.opExtrude","SWEPT_FACE",FACE,{"disambiguationData":[OSD([sQuery(id+"F274.wireOp",EDGE,"E137.top")])]})]}),makeQuery(id+"F277.opExtrude","SWEPT_FACE",FACE,{"disambiguationData":[OSD([sQuery(id+"F276.wireOp",EDGE,"E138.bottom")])]})]});
            var sketch = newSketch(context, id + "F278", { "sketchPlane" : qUnion([Q0])});
            skLineSegment(sketch, "E139.bottom", {"start": v(-52, 24.41) * mm, "end": v(-58.34, 24.41) * mm});
            skLineSegment(sketch, "E139.top", {"start": v(-52, 18.06) * mm, "end": v(-58.34, 18.06) * mm});
            skLineSegment(sketch, "E139.left", {"start": v(-52, 24.41) * mm, "end": v(-52, 18.06) * mm});
            skLineSegment(sketch, "E139.right", {"start": v(-58.34, 24.41) * mm, "end": v(-58.34, 18.06) * mm});
            skSolve(sketch);
        }
        {
            var Q0;
            Q0=makeQuery(id+"F278.imprint","IMPRINT",FACE,{"disambiguationData":[TD([[makeQuery(id+"F278.imprint","IMPRINT",EDGE,{"derivedFrom":sQuery(id+"F278.wireOp",EDGE,"E139.bottom")}),-1.0]])]});
            extrude(context, id + "F279", {"entities" : qUnion([Q0]), "operationType" : NewBodyOperationType.ADD, "oppositeDirection" : true, "depth" : 19.05 * mm});
        }
        {
            var Q0;
            Q0=makeQuery(id+"F279.boolean.opBoolean","MERGE",FACE,{"derivedFrom":[makeQuery(id+"F277.opExtrude","CAP_FACE",FACE,{"disambiguationData":[OSD([sQuery(id+"F276.wireOp",EDGE,"E138.bottom"),sQuery(id+"F276.wireOp",EDGE,"E138.top"),sQuery(id+"F276.wireOp",EDGE,"E138.left"),sQuery(id+"F276.wireOp",EDGE,"E138.right")])],"isStart":false}),makeQuery(id+"F279.opExtrude","SWEPT_FACE",FACE,{"disambiguationData":[OSD([sQuery(id+"F278.wireOp",EDGE,"E139.left")])]})]});
            var sketch = newSketch(context, id + "F280", { "sketchPlane" : qUnion([Q0])});
            skLineSegment(sketch, "E140.bottom", {"start": v(18.06, 50.8) * mm, "end": v(24.41, 50.8) * mm});
            skLineSegment(sketch, "E140.top", {"start": v(18.06, 57.15) * mm, "end": v(24.41, 57.15) * mm});
            skLineSegment(sketch, "E140.left", {"start": v(18.06, 50.8) * mm, "end": v(18.06, 57.15) * mm});
            skLineSegment(sketch, "E140.right", {"start": v(24.41, 50.8) * mm, "end": v(24.41, 57.15) * mm});
            skSolve(sketch);
        }
        {
            var Q0;
            Q0=makeQuery(id+"F280.imprint","IMPRINT",FACE,{"disambiguationData":[TD([[makeQuery(id+"F280.imprint","IMPRINT",EDGE,{"derivedFrom":sQuery(id+"F280.wireOp",EDGE,"E140.bottom")}),1.0]])]});
            extrude(context, id + "F281", {"entities" : qUnion([Q0]), "operationType" : NewBodyOperationType.ADD, "oppositeDirection" : true, "depth" : 19.05 * mm});
        }
        {
            var Q0;
            Q0=makeQuery(id+"F281.boolean.opBoolean","MERGE",FACE,{"derivedFrom":[makeQuery(id+"F279.boolean.opBoolean","MERGE",FACE,{"derivedFrom":[makeQuery(id+"F277.boolean.opBoolean","MERGE",FACE,{"derivedFrom":[makeQuery(id+"F275.opExtrude","CAP_FACE",FACE,{"disambiguationData":[OSD([sQuery(id+"F274.wireOp",EDGE,"E137.bottom"),sQuery(id+"F274.wireOp",EDGE,"E137.top"),sQuery(id+"F274.wireOp",EDGE,"E137.left"),sQuery(id+"F274.wireOp",EDGE,"E137.right")])],"isStart":false}),makeQuery(id+"F277.opExtrude","SWEPT_FACE",FACE,{"disambiguationData":[OSD([sQuery(id+"F276.wireOp",EDGE,"E138.left")])]})]}),makeQuery(id+"F279.opExtrude","SWEPT_FACE",FACE,{"disambiguationData":[OSD([sQuery(id+"F278.wireOp",EDGE,"E139.bottom")])]})]}),makeQuery(id+"F281.opExtrude","SWEPT_FACE",FACE,{"disambiguationData":[OSD([sQuery(id+"F280.wireOp",EDGE,"E140.right")])]})]});
            var sketch = newSketch(context, id + "F282", { "sketchPlane" : qUnion([Q0])});
            skLineSegment(sketch, "E141.bottom", {"start": v(71.04, 50.8) * mm, "end": v(64.7, 50.8) * mm});
            skLineSegment(sketch, "E141.top", {"start": v(71.04, 57.15) * mm, "end": v(64.7, 57.15) * mm});
            skLineSegment(sketch, "E141.left", {"start": v(71.04, 50.8) * mm, "end": v(71.04, 57.15) * mm});
            skLineSegment(sketch, "E141.right", {"start": v(64.7, 50.8) * mm, "end": v(64.7, 57.15) * mm});
            skSolve(sketch);
        }
        {
            var Q0;
            Q0=makeQuery(id+"F282.imprint","IMPRINT",FACE,{"disambiguationData":[TD([[makeQuery(id+"F282.imprint","IMPRINT",EDGE,{"derivedFrom":sQuery(id+"F282.wireOp",EDGE,"E141.bottom")}),-1.0]])]});
            extrude(context, id + "F283", {"entities" : qUnion([Q0]), "operationType" : NewBodyOperationType.ADD, "oppositeDirection" : true, "depth" : 19.05 * mm});
        }
        {
            var Q0;
            Q0=makeQuery(id+"F283.boolean.opBoolean","MERGE",FACE,{"derivedFrom":[makeQuery(id+"F281.opExtrude","CAP_FACE",FACE,{"disambiguationData":[OSD([sQuery(id+"F280.wireOp",EDGE,"E140.bottom"),sQuery(id+"F280.wireOp",EDGE,"E140.top"),sQuery(id+"F280.wireOp",EDGE,"E140.left"),sQuery(id+"F280.wireOp",EDGE,"E140.right")])],"isStart":false}),makeQuery(id+"F283.opExtrude","SWEPT_FACE",FACE,{"disambiguationData":[OSD([sQuery(id+"F282.wireOp",EDGE,"E141.left")])]})]});
            var sketch = newSketch(context, id + "F284", { "sketchPlane" : qUnion([Q0])});
            skLineSegment(sketch, "E142.bottom", {"start": v(-5.36, 57.15) * mm, "end": v(-11.71, 57.15) * mm});
            skLineSegment(sketch, "E142.top", {"start": v(-5.36, 50.8) * mm, "end": v(-11.71, 50.8) * mm});
            skLineSegment(sketch, "E142.left", {"start": v(-5.36, 57.15) * mm, "end": v(-5.36, 50.8) * mm});
            skLineSegment(sketch, "E142.right", {"start": v(-11.71, 57.15) * mm, "end": v(-11.71, 50.8) * mm});
            skSolve(sketch);
        }
        {
            var Q0;
            Q0=makeQuery(id+"F284.imprint","IMPRINT",FACE,{"disambiguationData":[TD([[makeQuery(id+"F284.imprint","IMPRINT",EDGE,{"derivedFrom":sQuery(id+"F284.wireOp",EDGE,"E142.bottom")}),1.0]])]});
            extrude(context, id + "F285", {"entities" : qUnion([Q0]), "operationType" : NewBodyOperationType.ADD, "oppositeDirection" : true, "depth" : 44.45 * mm});
        }
        {
            var Q0;
            Q0=makeQuery(id+"F285.boolean.opBoolean","MERGE",FACE,{"derivedFrom":[makeQuery(id+"F283.opExtrude","CAP_FACE",FACE,{"disambiguationData":[OSD([sQuery(id+"F282.wireOp",EDGE,"E141.bottom"),sQuery(id+"F282.wireOp",EDGE,"E141.top"),sQuery(id+"F282.wireOp",EDGE,"E141.left"),sQuery(id+"F282.wireOp",EDGE,"E141.right")])],"isStart":false}),makeQuery(id+"F285.opExtrude","SWEPT_FACE",FACE,{"disambiguationData":[OSD([sQuery(id+"F284.wireOp",EDGE,"E142.left")])]})]});
            var sketch = newSketch(context, id + "F286", { "sketchPlane" : qUnion([Q0])});
            skLineSegment(sketch, "E143.bottom", {"start": v(-26.6, 57.15) * mm, "end": v(-32.94, 57.15) * mm});
            skLineSegment(sketch, "E143.top", {"start": v(-26.6, 50.8) * mm, "end": v(-32.94, 50.8) * mm});
            skLineSegment(sketch, "E143.left", {"start": v(-26.6, 57.15) * mm, "end": v(-26.6, 50.8) * mm});
            skLineSegment(sketch, "E143.right", {"start": v(-32.94, 57.15) * mm, "end": v(-32.94, 50.8) * mm});
            skSolve(sketch);
        }
        {
            var Q0;
            Q0=makeQuery(id+"F286.imprint","IMPRINT",FACE,{"disambiguationData":[TD([[makeQuery(id+"F286.imprint","IMPRINT",EDGE,{"derivedFrom":sQuery(id+"F286.wireOp",EDGE,"E143.bottom")}),-1.0]])]});
            extrude(context, id + "F287", {"entities" : qUnion([Q0]), "operationType" : NewBodyOperationType.ADD, "oppositeDirection" : true, "depth" : 19.05 * mm});
        }
        {
            var Q0;
            Q0=makeQuery(id+"F287.boolean.opBoolean","MERGE",FACE,{"derivedFrom":[makeQuery(id+"F285.opExtrude","CAP_FACE",FACE,{"disambiguationData":[OSD([sQuery(id+"F284.wireOp",EDGE,"E142.bottom"),sQuery(id+"F284.wireOp",EDGE,"E142.top"),sQuery(id+"F284.wireOp",EDGE,"E142.left"),sQuery(id+"F284.wireOp",EDGE,"E142.right")])],"isStart":false}),makeQuery(id+"F287.opExtrude","SWEPT_FACE",FACE,{"disambiguationData":[OSD([sQuery(id+"F286.wireOp",EDGE,"E143.left")])]})]});
            var sketch = newSketch(context, id + "F288", { "sketchPlane" : qUnion([Q0])});
            skLineSegment(sketch, "E144.bottom", {"start": v(24.41, 50.8) * mm, "end": v(18.06, 50.8) * mm});
            skLineSegment(sketch, "E144.top", {"start": v(24.41, 57.15) * mm, "end": v(18.06, 57.15) * mm});
            skLineSegment(sketch, "E144.left", {"start": v(24.41, 50.8) * mm, "end": v(24.41, 57.15) * mm});
            skLineSegment(sketch, "E144.right", {"start": v(18.06, 50.8) * mm, "end": v(18.06, 57.15) * mm});
            skSolve(sketch);
        }
        {
            var Q0;
            Q0=makeQuery(id+"F288.imprint","IMPRINT",FACE,{"disambiguationData":[TD([[makeQuery(id+"F288.imprint","IMPRINT",EDGE,{"derivedFrom":sQuery(id+"F288.wireOp",EDGE,"E144.bottom")}),1.0]])]});
            extrude(context, id + "F289", {"entities" : qUnion([Q0]), "operationType" : NewBodyOperationType.ADD, "oppositeDirection" : true, "depth" : 19.05 * mm});
        }
        {
            var Q0;
            Q0=makeQuery(id+"F289.boolean.opBoolean","MERGE",FACE,{"derivedFrom":[makeQuery(id+"F287.boolean.opBoolean","MERGE",FACE,{"derivedFrom":[makeQuery(id+"F285.boolean.opBoolean","MERGE",FACE,{"derivedFrom":[makeQuery(id+"F283.boolean.opBoolean","MERGE",FACE,{"derivedFrom":[makeQuery(id+"F281.boolean.opBoolean","MERGE",FACE,{"derivedFrom":[makeQuery(id+"F279.opExtrude","CAP_FACE",FACE,{"disambiguationData":[OSD([sQuery(id+"F278.wireOp",EDGE,"E139.bottom"),sQuery(id+"F278.wireOp",EDGE,"E139.top"),sQuery(id+"F278.wireOp",EDGE,"E139.left"),sQuery(id+"F278.wireOp",EDGE,"E139.right")])],"isStart":false}),makeQuery(id+"F281.opExtrude","SWEPT_FACE",FACE,{"disambiguationData":[OSD([sQuery(id+"F280.wireOp",EDGE,"E140.bottom")])]})]}),makeQuery(id+"F283.opExtrude","SWEPT_FACE",FACE,{"disambiguationData":[OSD([sQuery(id+"F282.wireOp",EDGE,"E141.bottom")])]})]}),makeQuery(id+"F285.opExtrude","SWEPT_FACE",FACE,{"disambiguationData":[OSD([sQuery(id+"F284.wireOp",EDGE,"E142.top")])]})]}),makeQuery(id+"F287.opExtrude","SWEPT_FACE",FACE,{"disambiguationData":[OSD([sQuery(id+"F286.wireOp",EDGE,"E143.top")])]})]}),makeQuery(id+"F289.opExtrude","SWEPT_FACE",FACE,{"disambiguationData":[OSD([sQuery(id+"F288.wireOp",EDGE,"E144.bottom")])]})]});
            var sketch = newSketch(context, id + "F290", { "sketchPlane" : qUnion([Q0])});
            skLineSegment(sketch, "E145.bottom", {"start": v(-45.64, -24.41) * mm, "end": v(-39.3, -24.41) * mm});
            skLineSegment(sketch, "E145.top", {"start": v(-45.64, -18.06) * mm, "end": v(-39.3, -18.06) * mm});
            skLineSegment(sketch, "E145.left", {"start": v(-45.64, -24.41) * mm, "end": v(-45.64, -18.06) * mm});
            skLineSegment(sketch, "E145.right", {"start": v(-39.3, -24.41) * mm, "end": v(-39.3, -18.06) * mm});
            skSolve(sketch);
        }
        {
            var Q0;
            Q0=makeQuery(id+"F290.imprint","IMPRINT",FACE,{"disambiguationData":[TD([[makeQuery(id+"F290.imprint","IMPRINT",EDGE,{"derivedFrom":sQuery(id+"F290.wireOp",EDGE,"E145.bottom")}),1.0]])]});
            extrude(context, id + "F291", {"entities" : qUnion([Q0]), "operationType" : NewBodyOperationType.ADD, "oppositeDirection" : true, "depth" : 19.05 * mm});
        }
        {
            var Q0;
            Q0=makeQuery(id+"F291.boolean.opBoolean","MERGE",FACE,{"derivedFrom":[makeQuery(id+"F289.opExtrude","CAP_FACE",FACE,{"disambiguationData":[OSD([sQuery(id+"F288.wireOp",EDGE,"E144.bottom"),sQuery(id+"F288.wireOp",EDGE,"E144.top"),sQuery(id+"F288.wireOp",EDGE,"E144.left"),sQuery(id+"F288.wireOp",EDGE,"E144.right")])],"isStart":false}),makeQuery(id+"F291.opExtrude","SWEPT_FACE",FACE,{"disambiguationData":[OSD([sQuery(id+"F290.wireOp",EDGE,"E145.left")])]})]});
            var sketch = newSketch(context, id + "F292", { "sketchPlane" : qUnion([Q0])});
            skLineSegment(sketch, "E146.bottom", {"start": v(-18.06, 69.85) * mm, "end": v(-24.41, 69.85) * mm});
            skLineSegment(sketch, "E146.top", {"start": v(-18.06, 63.5) * mm, "end": v(-24.41, 63.5) * mm});
            skLineSegment(sketch, "E146.left", {"start": v(-18.06, 69.85) * mm, "end": v(-18.06, 63.5) * mm});
            skLineSegment(sketch, "E146.right", {"start": v(-24.41, 69.85) * mm, "end": v(-24.41, 63.5) * mm});
            skSolve(sketch);
        }
        {
            var Q0;
            Q0 = qSketchRegion(id + "F292", true);
            var Q1;
            Q1=makeQuery(id+"F292.imprint","IMPRINT",FACE,{"disambiguationData":[TD([[makeQuery(id+"F292.imprint","IMPRINT",EDGE,{"derivedFrom":sQuery(id+"F292.wireOp",EDGE,"E146.bottom")}),1.0]])]});
            extrude(context, id + "F293", {"entities" : qUnion([Q0, Q1]), "operationType" : NewBodyOperationType.ADD, "oppositeDirection" : true, "depth" : 19.05 * mm});
        }
        {
            var Q0;
            Q0=makeQuery(id+"F293.boolean.opBoolean","MERGE",FACE,{"derivedFrom":[makeQuery(id+"F291.boolean.opBoolean","MERGE",FACE,{"derivedFrom":[makeQuery(id+"F289.boolean.opBoolean","MERGE",FACE,{"derivedFrom":[makeQuery(id+"F287.opExtrude","CAP_FACE",FACE,{"disambiguationData":[OSD([sQuery(id+"F286.wireOp",EDGE,"E143.bottom"),sQuery(id+"F286.wireOp",EDGE,"E143.top"),sQuery(id+"F286.wireOp",EDGE,"E143.left"),sQuery(id+"F286.wireOp",EDGE,"E143.right")])],"isStart":false}),makeQuery(id+"F289.opExtrude","SWEPT_FACE",FACE,{"disambiguationData":[OSD([sQuery(id+"F288.wireOp",EDGE,"E144.left")])]})]}),makeQuery(id+"F291.opExtrude","SWEPT_FACE",FACE,{"disambiguationData":[OSD([sQuery(id+"F290.wireOp",EDGE,"E145.bottom")])]})]}),makeQuery(id+"F293.opExtrude","SWEPT_FACE",FACE,{"disambiguationData":[OSD([sQuery(id+"F292.wireOp",EDGE,"E146.right")])]})]});
            var sketch = newSketch(context, id + "F294", { "sketchPlane" : qUnion([Q0])});
            skLineSegment(sketch, "E147.bottom", {"start": v(26.6, 69.85) * mm, "end": v(32.94, 69.85) * mm});
            skLineSegment(sketch, "E147.top", {"start": v(26.6, 63.5) * mm, "end": v(32.94, 63.5) * mm});
            skLineSegment(sketch, "E147.left", {"start": v(26.6, 69.85) * mm, "end": v(26.6, 63.5) * mm});
            skLineSegment(sketch, "E147.right", {"start": v(32.94, 69.85) * mm, "end": v(32.94, 63.5) * mm});
            skSolve(sketch);
        }
        {
            var Q0;
            Q0 = qSketchRegion(id + "F294", true);
            var Q1;
            Q1=makeQuery(id+"F294.imprint","IMPRINT",FACE,{"disambiguationData":[TD([[makeQuery(id+"F294.imprint","IMPRINT",EDGE,{"derivedFrom":sQuery(id+"F294.wireOp",EDGE,"E147.bottom")}),1.0]])]});
            extrude(context, id + "F295", {"entities" : qUnion([Q0, Q1]), "operationType" : NewBodyOperationType.ADD, "oppositeDirection" : true, "depth" : 19.05 * mm});
        }
        {
            var Q0;
            Q0=makeQuery(id+"F295.boolean.opBoolean","MERGE",FACE,{"derivedFrom":[makeQuery(id+"F293.opExtrude","CAP_FACE",FACE,{"disambiguationData":[OSD([sQuery(id+"F292.wireOp",EDGE,"E146.bottom"),sQuery(id+"F292.wireOp",EDGE,"E146.top"),sQuery(id+"F292.wireOp",EDGE,"E146.left"),sQuery(id+"F292.wireOp",EDGE,"E146.right")])],"isStart":false}),makeQuery(id+"F295.opExtrude","SWEPT_FACE",FACE,{"disambiguationData":[OSD([sQuery(id+"F294.wireOp",EDGE,"E147.left")])]})]});
            var sketch = newSketch(context, id + "F296", { "sketchPlane" : qUnion([Q0])});
            skLineSegment(sketch, "E148.bottom", {"start": v(5.36, 69.85) * mm, "end": v(11.71, 69.85) * mm});
            skLineSegment(sketch, "E148.top", {"start": v(5.36, 63.5) * mm, "end": v(11.71, 63.5) * mm});
            skLineSegment(sketch, "E148.left", {"start": v(5.36, 69.85) * mm, "end": v(5.36, 63.5) * mm});
            skLineSegment(sketch, "E148.right", {"start": v(11.71, 69.85) * mm, "end": v(11.71, 63.5) * mm});
            skSolve(sketch);
        }
        {
            var Q0;
            Q0 = qSketchRegion(id + "F296", true);
            var Q1;
            Q1=makeQuery(id+"F296.imprint","IMPRINT",FACE,{"disambiguationData":[TD([[makeQuery(id+"F296.imprint","IMPRINT",EDGE,{"derivedFrom":sQuery(id+"F296.wireOp",EDGE,"E148.bottom")}),-1.0]])]});
            extrude(context, id + "F297", {"entities" : qUnion([Q0, Q1]), "operationType" : NewBodyOperationType.ADD, "oppositeDirection" : true, "depth" : 19.05 * mm});
        }
        {
            var Q0;
            Q0=makeQuery(id+"F297.boolean.opBoolean","MERGE",FACE,{"derivedFrom":[makeQuery(id+"F295.boolean.opBoolean","MERGE",FACE,{"derivedFrom":[makeQuery(id+"F293.opExtrude","SWEPT_FACE",FACE,{"disambiguationData":[OSD([sQuery(id+"F292.wireOp",EDGE,"E146.top")])]}),makeQuery(id+"F295.opExtrude","SWEPT_FACE",FACE,{"disambiguationData":[OSD([sQuery(id+"F294.wireOp",EDGE,"E147.top")])]})]}),makeQuery(id+"F297.opExtrude","SWEPT_FACE",FACE,{"disambiguationData":[OSD([sQuery(id+"F296.wireOp",EDGE,"E148.top")])]})]});
            var sketch = newSketch(context, id + "F298", { "sketchPlane" : qUnion([Q0])});
            skLineSegment(sketch, "E149.bottom", {"start": v(-45.64, -5.36) * mm, "end": v(-39.3, -5.36) * mm});
            skLineSegment(sketch, "E149.top", {"start": v(-45.64, -11.71) * mm, "end": v(-39.3, -11.71) * mm});
            skLineSegment(sketch, "E149.left", {"start": v(-45.64, -5.36) * mm, "end": v(-45.64, -11.71) * mm});
            skLineSegment(sketch, "E149.right", {"start": v(-39.3, -5.36) * mm, "end": v(-39.3, -11.71) * mm});
            skSolve(sketch);
        }
        {
            var Q0;
            Q0 = qSketchRegion(id + "F298", true);
            var Q1;
            Q1=makeQuery(id+"F298.imprint","IMPRINT",FACE,{"disambiguationData":[TD([[makeQuery(id+"F298.imprint","IMPRINT",EDGE,{"derivedFrom":sQuery(id+"F298.wireOp",EDGE,"E149.bottom")}),1.0]])]});
            extrude(context, id + "F299", {"entities" : qUnion([Q0, Q1]), "operationType" : NewBodyOperationType.ADD, "oppositeDirection" : true, "depth" : 31.75 * mm});
        }
        {
            var Q0;
            Q0=makeQuery(id+"F299.boolean.opBoolean","MERGE",FACE,{"derivedFrom":[makeQuery(id+"F297.boolean.opBoolean","MERGE",FACE,{"derivedFrom":[makeQuery(id+"F295.opExtrude","CAP_FACE",FACE,{"disambiguationData":[OSD([sQuery(id+"F294.wireOp",EDGE,"E147.bottom"),sQuery(id+"F294.wireOp",EDGE,"E147.top"),sQuery(id+"F294.wireOp",EDGE,"E147.left"),sQuery(id+"F294.wireOp",EDGE,"E147.right")])],"isStart":false}),makeQuery(id+"F297.opExtrude","SWEPT_FACE",FACE,{"disambiguationData":[OSD([sQuery(id+"F296.wireOp",EDGE,"E148.left")])]})]}),makeQuery(id+"F299.opExtrude","SWEPT_FACE",FACE,{"disambiguationData":[OSD([sQuery(id+"F298.wireOp",EDGE,"E149.bottom")])]})]});
            var sketch = newSketch(context, id + "F300", { "sketchPlane" : qUnion([Q0])});
            skLineSegment(sketch, "E150.bottom", {"start": v(-45.64, 95.25) * mm, "end": v(-39.3, 95.25) * mm});
            skLineSegment(sketch, "E150.top", {"start": v(-45.64, 88.9) * mm, "end": v(-39.3, 88.9) * mm});
            skLineSegment(sketch, "E150.left", {"start": v(-45.64, 95.25) * mm, "end": v(-45.64, 88.9) * mm});
            skLineSegment(sketch, "E150.right", {"start": v(-39.3, 95.25) * mm, "end": v(-39.3, 88.9) * mm});
            skSolve(sketch);
        }
        {
            var Q0;
            Q0=makeQuery(id+"F300.imprint","IMPRINT",FACE,{"disambiguationData":[TD([[makeQuery(id+"F300.imprint","IMPRINT",EDGE,{"derivedFrom":sQuery(id+"F300.wireOp",EDGE,"E150.bottom")}),1.0]])]});
            extrude(context, id + "F301", {"entities" : qUnion([Q0]), "operationType" : NewBodyOperationType.ADD, "oppositeDirection" : true, "depth" : 19.05 * mm});
        }
        {
            var Q0;
            Q0=makeQuery(id+"F301.boolean.opBoolean","MERGE",FACE,{"derivedFrom":[makeQuery(id+"F299.opExtrude","CAP_FACE",FACE,{"disambiguationData":[OSD([sQuery(id+"F298.wireOp",EDGE,"E149.bottom"),sQuery(id+"F298.wireOp",EDGE,"E149.top"),sQuery(id+"F298.wireOp",EDGE,"E149.left"),sQuery(id+"F298.wireOp",EDGE,"E149.right")])],"isStart":false}),makeQuery(id+"F301.opExtrude","SWEPT_FACE",FACE,{"disambiguationData":[OSD([sQuery(id+"F300.wireOp",EDGE,"E150.bottom")])]})]});
            var sketch = newSketch(context, id + "F302", { "sketchPlane" : qUnion([Q0])});
            skLineSegment(sketch, "E151.bottom", {"start": v(-45.64, 24.41) * mm, "end": v(-39.3, 24.41) * mm});
            skLineSegment(sketch, "E151.top", {"start": v(-45.64, 18.06) * mm, "end": v(-39.3, 18.06) * mm});
            skLineSegment(sketch, "E151.left", {"start": v(-45.64, 24.41) * mm, "end": v(-45.64, 18.06) * mm});
            skLineSegment(sketch, "E151.right", {"start": v(-39.3, 24.41) * mm, "end": v(-39.3, 18.06) * mm});
            skSolve(sketch);
        }
        {
            var Q0;
            Q0 = qSketchRegion(id + "F302", true);
            var Q1;
            Q1=makeQuery(id+"F302.imprint","IMPRINT",FACE,{"disambiguationData":[TD([[makeQuery(id+"F302.imprint","IMPRINT",EDGE,{"derivedFrom":sQuery(id+"F302.wireOp",EDGE,"E151.bottom")}),1.0]])]});
            extrude(context, id + "F303", {"entities" : qUnion([Q0, Q1]), "operationType" : NewBodyOperationType.ADD, "oppositeDirection" : true, "depth" : 19.05 * mm});
        }
        {
            var Q0;
            Q0=makeQuery(id+"F303.boolean.opBoolean","MERGE",FACE,{"derivedFrom":[makeQuery(id+"F301.boolean.opBoolean","MERGE",FACE,{"derivedFrom":[makeQuery(id+"F299.boolean.opBoolean","MERGE",FACE,{"derivedFrom":[makeQuery(id+"F297.opExtrude","CAP_FACE",FACE,{"disambiguationData":[OSD([sQuery(id+"F296.wireOp",EDGE,"E148.bottom"),sQuery(id+"F296.wireOp",EDGE,"E148.top"),sQuery(id+"F296.wireOp",EDGE,"E148.left"),sQuery(id+"F296.wireOp",EDGE,"E148.right")])],"isStart":false}),makeQuery(id+"F299.opExtrude","SWEPT_FACE",FACE,{"disambiguationData":[OSD([sQuery(id+"F298.wireOp",EDGE,"E149.left")])]})]}),makeQuery(id+"F301.opExtrude","SWEPT_FACE",FACE,{"disambiguationData":[OSD([sQuery(id+"F300.wireOp",EDGE,"E150.left")])]})]}),makeQuery(id+"F303.opExtrude","SWEPT_FACE",FACE,{"disambiguationData":[OSD([sQuery(id+"F302.wireOp",EDGE,"E151.left")])]})]});
            var sketch = newSketch(context, id + "F304", { "sketchPlane" : qUnion([Q0])});
            skLineSegment(sketch, "E152.bottom", {"start": v(-24.41, 76.2) * mm, "end": v(-18.06, 76.2) * mm});
            skLineSegment(sketch, "E152.top", {"start": v(-24.41, 82.55) * mm, "end": v(-18.06, 82.55) * mm});
            skLineSegment(sketch, "E152.left", {"start": v(-24.41, 76.2) * mm, "end": v(-24.41, 82.55) * mm});
            skLineSegment(sketch, "E152.right", {"start": v(-18.06, 76.2) * mm, "end": v(-18.06, 82.55) * mm});
            skSolve(sketch);
        }
        {
            var Q0;
            Q0 = qSketchRegion(id + "F304", true);
            var Q1;
            Q1=makeQuery(id+"F304.imprint","IMPRINT",FACE,{"disambiguationData":[TD([[makeQuery(id+"F304.imprint","IMPRINT",EDGE,{"derivedFrom":sQuery(id+"F304.wireOp",EDGE,"E152.bottom")}),-1.0]])]});
            extrude(context, id + "F305", {"entities" : qUnion([Q0, Q1]), "operationType" : NewBodyOperationType.ADD, "oppositeDirection" : true, "depth" : 19.05 * mm});
        }
        {
            var Q0;
            Q0=makeQuery(id+"F305.boolean.opBoolean","MERGE",FACE,{"derivedFrom":[makeQuery(id+"F303.opExtrude","CAP_FACE",FACE,{"disambiguationData":[OSD([sQuery(id+"F302.wireOp",EDGE,"E151.bottom"),sQuery(id+"F302.wireOp",EDGE,"E151.top"),sQuery(id+"F302.wireOp",EDGE,"E151.left"),sQuery(id+"F302.wireOp",EDGE,"E151.right")])],"isStart":false}),makeQuery(id+"F305.opExtrude","SWEPT_FACE",FACE,{"disambiguationData":[OSD([sQuery(id+"F304.wireOp",EDGE,"E152.bottom")])]})]});
            var sketch = newSketch(context, id + "F306", { "sketchPlane" : qUnion([Q0])});
            skLineSegment(sketch, "E153.bottom", {"start": v(-26.6, -24.41) * mm, "end": v(-32.94, -24.41) * mm});
            skLineSegment(sketch, "E153.top", {"start": v(-26.6, -18.06) * mm, "end": v(-32.94, -18.06) * mm});
            skLineSegment(sketch, "E153.left", {"start": v(-26.6, -24.41) * mm, "end": v(-26.6, -18.06) * mm});
            skLineSegment(sketch, "E153.right", {"start": v(-32.94, -24.41) * mm, "end": v(-32.94, -18.06) * mm});
            skSolve(sketch);
        }
        {
            var Q0;
            Q0 = qSketchRegion(id + "F306", true);
            var Q1;
            Q1=makeQuery(id+"F306.imprint","IMPRINT",FACE,{"disambiguationData":[TD([[makeQuery(id+"F306.imprint","IMPRINT",EDGE,{"derivedFrom":sQuery(id+"F306.wireOp",EDGE,"E153.bottom")}),-1.0]])]});
            extrude(context, id + "F307", {"entities" : qUnion([Q0, Q1]), "operationType" : NewBodyOperationType.ADD, "oppositeDirection" : true, "depth" : 19.05 * mm});
        }
        {
            var Q0;
            Q0=makeQuery(id+"F307.boolean.opBoolean","MERGE",FACE,{"derivedFrom":[makeQuery(id+"F305.boolean.opBoolean","MERGE",FACE,{"derivedFrom":[makeQuery(id+"F303.boolean.opBoolean","MERGE",FACE,{"derivedFrom":[makeQuery(id+"F301.opExtrude","CAP_FACE",FACE,{"disambiguationData":[OSD([sQuery(id+"F300.wireOp",EDGE,"E150.bottom"),sQuery(id+"F300.wireOp",EDGE,"E150.top"),sQuery(id+"F300.wireOp",EDGE,"E150.left"),sQuery(id+"F300.wireOp",EDGE,"E150.right")])],"isStart":false}),makeQuery(id+"F303.opExtrude","SWEPT_FACE",FACE,{"disambiguationData":[OSD([sQuery(id+"F302.wireOp",EDGE,"E151.bottom")])]})]}),makeQuery(id+"F305.opExtrude","SWEPT_FACE",FACE,{"disambiguationData":[OSD([sQuery(id+"F304.wireOp",EDGE,"E152.left")])]})]}),makeQuery(id+"F307.opExtrude","SWEPT_FACE",FACE,{"disambiguationData":[OSD([sQuery(id+"F306.wireOp",EDGE,"E153.bottom")])]})]});
            var sketch = newSketch(context, id + "F308", { "sketchPlane" : qUnion([Q0])});
            skLineSegment(sketch, "E154.bottom", {"start": v(26.6, 95.25) * mm, "end": v(32.94, 95.25) * mm});
            skLineSegment(sketch, "E154.top", {"start": v(26.6, 88.9) * mm, "end": v(32.94, 88.9) * mm});
            skLineSegment(sketch, "E154.left", {"start": v(26.6, 95.25) * mm, "end": v(26.6, 88.9) * mm});
            skLineSegment(sketch, "E154.right", {"start": v(32.94, 95.25) * mm, "end": v(32.94, 88.9) * mm});
            skSolve(sketch);
        }
        {
            var Q0;
            Q0 = qSketchRegion(id + "F308", true);
            var Q1;
            Q1=makeQuery(id+"F308.imprint","IMPRINT",FACE,{"disambiguationData":[TD([[makeQuery(id+"F308.imprint","IMPRINT",EDGE,{"derivedFrom":sQuery(id+"F308.wireOp",EDGE,"E154.bottom")}),-1.0]])]});
            extrude(context, id + "F309", {"entities" : qUnion([Q0, Q1]), "operationType" : NewBodyOperationType.ADD, "oppositeDirection" : true, "depth" : 19.05 * mm});
        }
        {
            var Q0;
            Q0=makeQuery(id+"F309.boolean.opBoolean","MERGE",FACE,{"derivedFrom":[makeQuery(id+"F307.opExtrude","CAP_FACE",FACE,{"disambiguationData":[OSD([sQuery(id+"F306.wireOp",EDGE,"E153.bottom"),sQuery(id+"F306.wireOp",EDGE,"E153.top"),sQuery(id+"F306.wireOp",EDGE,"E153.left"),sQuery(id+"F306.wireOp",EDGE,"E153.right")])],"isStart":false}),makeQuery(id+"F309.opExtrude","SWEPT_FACE",FACE,{"disambiguationData":[OSD([sQuery(id+"F308.wireOp",EDGE,"E154.bottom")])]})]});
            var sketch = newSketch(context, id + "F310", { "sketchPlane" : qUnion([Q0])});
            skLineSegment(sketch, "E155.bottom", {"start": v(-32.94, 5.36) * mm, "end": v(-26.6, 5.36) * mm});
            skLineSegment(sketch, "E155.top", {"start": v(-32.94, 11.71) * mm, "end": v(-26.6, 11.71) * mm});
            skLineSegment(sketch, "E155.left", {"start": v(-32.94, 5.36) * mm, "end": v(-32.94, 11.71) * mm});
            skLineSegment(sketch, "E155.right", {"start": v(-26.6, 5.36) * mm, "end": v(-26.6, 11.71) * mm});
            skSolve(sketch);
        }
        {
            var Q0;
            Q0 = qSketchRegion(id + "F310", true);
            var Q1;
            Q1=makeQuery(id+"F310.imprint","IMPRINT",FACE,{"disambiguationData":[TD([[makeQuery(id+"F310.imprint","IMPRINT",EDGE,{"derivedFrom":sQuery(id+"F310.wireOp",EDGE,"E155.bottom")}),-1.0]])]});
            extrude(context, id + "F311", {"entities" : qUnion([Q0, Q1]), "operationType" : NewBodyOperationType.ADD, "oppositeDirection" : true, "depth" : 19.05 * mm});
        }
        {
            var Q0;
            Q0=makeQuery(id+"F311.opExtrude","SWEPT_FACE",FACE,{"disambiguationData":[OSD([sQuery(id+"F310.wireOp",EDGE,"E155.top")])]});
            var sketch = newSketch(context, id + "F312", { "sketchPlane" : qUnion([Q0])});
            skLineSegment(sketch, "E156.bottom", {"start": v(26.6, 76.2) * mm, "end": v(32.94, 76.2) * mm});
            skLineSegment(sketch, "E156.top", {"start": v(26.6, 82.55) * mm, "end": v(32.94, 82.55) * mm});
            skLineSegment(sketch, "E156.left", {"start": v(26.6, 76.2) * mm, "end": v(26.6, 82.55) * mm});
            skLineSegment(sketch, "E156.right", {"start": v(32.94, 76.2) * mm, "end": v(32.94, 82.55) * mm});
            skSolve(sketch);
        }
        {
            var Q0;
            Q0 = qSketchRegion(id + "F312", true);
            var Q1;
            Q1=makeQuery(id+"F312.imprint","IMPRINT",FACE,{"disambiguationData":[TD([[makeQuery(id+"F312.imprint","IMPRINT",EDGE,{"derivedFrom":sQuery(id+"F312.wireOp",EDGE,"E156.bottom")}),-1.0]])]});
            extrude(context, id + "F313", {"entities" : qUnion([Q0, Q1]), "operationType" : NewBodyOperationType.ADD, "oppositeDirection" : true, "depth" : 19.05 * mm});
        }
        {
            var Q0;
            Q0=makeQuery(id+"F313.boolean.opBoolean","MERGE",FACE,{"derivedFrom":[makeQuery(id+"F311.opExtrude","CAP_FACE",FACE,{"disambiguationData":[OSD([sQuery(id+"F310.wireOp",EDGE,"E155.bottom"),sQuery(id+"F310.wireOp",EDGE,"E155.top"),sQuery(id+"F310.wireOp",EDGE,"E155.left"),sQuery(id+"F310.wireOp",EDGE,"E155.right")])],"isStart":false}),makeQuery(id+"F313.opExtrude","SWEPT_FACE",FACE,{"disambiguationData":[OSD([sQuery(id+"F312.wireOp",EDGE,"E156.bottom")])]})]});
            var sketch = newSketch(context, id + "F314", { "sketchPlane" : qUnion([Q0])});
            skLineSegment(sketch, "E157.bottom", {"start": v(-26.6, 7.34) * mm, "end": v(-32.94, 7.34) * mm});
            skLineSegment(sketch, "E157.top", {"start": v(-26.6, 0.99) * mm, "end": v(-32.94, 0.99) * mm});
            skLineSegment(sketch, "E157.left", {"start": v(-26.6, 7.34) * mm, "end": v(-26.6, 0.99) * mm});
            skLineSegment(sketch, "E157.right", {"start": v(-32.94, 7.34) * mm, "end": v(-32.94, 0.99) * mm});
            skSolve(sketch);
        }
        {
            var Q0;
            Q0 = qSketchRegion(id + "F314", true);
            var Q1;
            Q1=makeQuery(id+"F314.imprint","IMPRINT",FACE,{"disambiguationData":[TD([[makeQuery(id+"F314.imprint","IMPRINT",EDGE,{"derivedFrom":sQuery(id+"F314.wireOp",EDGE,"E157.bottom")}),-1.0]])]});
            extrude(context, id + "F315", {"entities" : qUnion([Q0, Q1]), "operationType" : NewBodyOperationType.ADD, "oppositeDirection" : true, "depth" : 19.05 * mm});
        }
        {
            var Q0;
            Q0=makeQuery(id+"F315.boolean.opBoolean","MERGE",FACE,{"derivedFrom":[makeQuery(id+"F313.boolean.opBoolean","MERGE",FACE,{"derivedFrom":[makeQuery(id+"F311.boolean.opBoolean","MERGE",FACE,{"derivedFrom":[makeQuery(id+"F309.boolean.opBoolean","MERGE",FACE,{"derivedFrom":[makeQuery(id+"F307.boolean.opBoolean","MERGE",FACE,{"derivedFrom":[makeQuery(id+"F305.opExtrude","CAP_FACE",FACE,{"disambiguationData":[OSD([sQuery(id+"F304.wireOp",EDGE,"E152.bottom"),sQuery(id+"F304.wireOp",EDGE,"E152.top"),sQuery(id+"F304.wireOp",EDGE,"E152.left"),sQuery(id+"F304.wireOp",EDGE,"E152.right")])],"isStart":false}),makeQuery(id+"F307.opExtrude","SWEPT_FACE",FACE,{"disambiguationData":[OSD([sQuery(id+"F306.wireOp",EDGE,"E153.left")])]})]}),makeQuery(id+"F309.opExtrude","SWEPT_FACE",FACE,{"disambiguationData":[OSD([sQuery(id+"F308.wireOp",EDGE,"E154.left")])]})]}),makeQuery(id+"F311.opExtrude","SWEPT_FACE",FACE,{"disambiguationData":[OSD([sQuery(id+"F310.wireOp",EDGE,"E155.right")])]})]}),makeQuery(id+"F313.opExtrude","SWEPT_FACE",FACE,{"disambiguationData":[OSD([sQuery(id+"F312.wireOp",EDGE,"E156.left")])]})]}),makeQuery(id+"F315.opExtrude","SWEPT_FACE",FACE,{"disambiguationData":[OSD([sQuery(id+"F314.wireOp",EDGE,"E157.left")])]})]});
            var sketch = newSketch(context, id + "F316", { "sketchPlane" : qUnion([Q0])});
            skLineSegment(sketch, "E158.bottom", {"start": v(-7.34, 95.25) * mm, "end": v(-0.99, 95.25) * mm});
            skLineSegment(sketch, "E158.top", {"start": v(-7.34, 88.9) * mm, "end": v(-0.99, 88.9) * mm});
            skLineSegment(sketch, "E158.left", {"start": v(-7.34, 95.25) * mm, "end": v(-7.34, 88.9) * mm});
            skLineSegment(sketch, "E158.right", {"start": v(-0.99, 95.25) * mm, "end": v(-0.99, 88.9) * mm});
            skSolve(sketch);
        }
        {
            var Q0;
            Q0 = qSketchRegion(id + "F316", true);
            var Q1;
            Q1=makeQuery(id+"F316.imprint","IMPRINT",FACE,{"disambiguationData":[TD([[makeQuery(id+"F316.imprint","IMPRINT",EDGE,{"derivedFrom":sQuery(id+"F316.wireOp",EDGE,"E158.bottom")}),-1.0]])]});
            extrude(context, id + "F317", {"entities" : qUnion([Q0, Q1]), "operationType" : NewBodyOperationType.ADD, "oppositeDirection" : true, "depth" : 19.05 * mm});
        }
        {
            var Q0;
            Q0=makeQuery(id+"F317.boolean.opBoolean","MERGE",FACE,{"derivedFrom":[makeQuery(id+"F315.opExtrude","CAP_FACE",FACE,{"disambiguationData":[OSD([sQuery(id+"F314.wireOp",EDGE,"E157.bottom"),sQuery(id+"F314.wireOp",EDGE,"E157.top"),sQuery(id+"F314.wireOp",EDGE,"E157.left"),sQuery(id+"F314.wireOp",EDGE,"E157.right")])],"isStart":false}),makeQuery(id+"F317.opExtrude","SWEPT_FACE",FACE,{"disambiguationData":[OSD([sQuery(id+"F316.wireOp",EDGE,"E158.bottom")])]})]});
            var sketch = newSketch(context, id + "F318", { "sketchPlane" : qUnion([Q0])});
            skLineSegment(sketch, "E159.bottom", {"start": v(-45.64, -7.34) * mm, "end": v(-39.3, -7.34) * mm});
            skLineSegment(sketch, "E159.top", {"start": v(-45.64, -0.99) * mm, "end": v(-39.3, -0.99) * mm});
            skLineSegment(sketch, "E159.left", {"start": v(-45.64, -7.34) * mm, "end": v(-45.64, -0.99) * mm});
            skLineSegment(sketch, "E159.right", {"start": v(-39.3, -7.34) * mm, "end": v(-39.3, -0.99) * mm});
            skSolve(sketch);
        }
        {
            var Q0;
            Q0 = qSketchRegion(id + "F318", true);
            var Q1;
            Q1=makeQuery(id+"F318.imprint","IMPRINT",FACE,{"disambiguationData":[TD([[makeQuery(id+"F318.imprint","IMPRINT",EDGE,{"derivedFrom":sQuery(id+"F318.wireOp",EDGE,"E159.bottom")}),1.0]])]});
            extrude(context, id + "F319", {"entities" : qUnion([Q0, Q1]), "operationType" : NewBodyOperationType.ADD, "oppositeDirection" : true, "depth" : 19.05 * mm});
        }
        {
            var Q0;
            Q0=makeQuery(id+"F319.boolean.opBoolean","MERGE",FACE,{"derivedFrom":[makeQuery(id+"F317.boolean.opBoolean","MERGE",FACE,{"derivedFrom":[makeQuery(id+"F315.opExtrude","SWEPT_FACE",FACE,{"disambiguationData":[OSD([sQuery(id+"F314.wireOp",EDGE,"E157.top")])]}),makeQuery(id+"F317.opExtrude","SWEPT_FACE",FACE,{"disambiguationData":[OSD([sQuery(id+"F316.wireOp",EDGE,"E158.right")])]})]}),makeQuery(id+"F319.opExtrude","SWEPT_FACE",FACE,{"disambiguationData":[OSD([sQuery(id+"F318.wireOp",EDGE,"E159.top")])]})]});
            var sketch = newSketch(context, id + "F320", { "sketchPlane" : qUnion([Q0])});
            skLineSegment(sketch, "E160.bottom", {"start": v(45.64, 76.2) * mm, "end": v(39.3, 76.2) * mm});
            skLineSegment(sketch, "E160.top", {"start": v(45.64, 82.55) * mm, "end": v(39.3, 82.55) * mm});
            skLineSegment(sketch, "E160.left", {"start": v(45.64, 76.2) * mm, "end": v(45.64, 82.55) * mm});
            skLineSegment(sketch, "E160.right", {"start": v(39.3, 76.2) * mm, "end": v(39.3, 82.55) * mm});
            skSolve(sketch);
        }
        {
            var Q0;
            Q0 = qSketchRegion(id + "F320", true);
            var Q1;
            Q1=makeQuery(id+"F320.imprint","IMPRINT",FACE,{"disambiguationData":[TD([[makeQuery(id+"F320.imprint","IMPRINT",EDGE,{"derivedFrom":sQuery(id+"F320.wireOp",EDGE,"E160.bottom")}),1.0]])]});
            extrude(context, id + "F321", {"entities" : qUnion([Q0, Q1]), "operationType" : NewBodyOperationType.ADD, "oppositeDirection" : true, "depth" : 19.05 * mm});
        }
        {
            var Q0;
            Q0=makeQuery(id+"F321.boolean.opBoolean","MERGE",FACE,{"derivedFrom":[makeQuery(id+"F319.opExtrude","CAP_FACE",FACE,{"disambiguationData":[OSD([sQuery(id+"F318.wireOp",EDGE,"E159.bottom"),sQuery(id+"F318.wireOp",EDGE,"E159.top"),sQuery(id+"F318.wireOp",EDGE,"E159.left"),sQuery(id+"F318.wireOp",EDGE,"E159.right")])],"isStart":false}),makeQuery(id+"F321.opExtrude","SWEPT_FACE",FACE,{"disambiguationData":[OSD([sQuery(id+"F320.wireOp",EDGE,"E160.bottom")])]})]});
            var sketch = newSketch(context, id + "F322", { "sketchPlane" : qUnion([Q0])});
            skLineSegment(sketch, "E161.bottom", {"start": v(-45.64, 20.04) * mm, "end": v(-39.3, 20.04) * mm});
            skLineSegment(sketch, "E161.top", {"start": v(-45.64, 13.69) * mm, "end": v(-39.3, 13.69) * mm});
            skLineSegment(sketch, "E161.left", {"start": v(-45.64, 20.04) * mm, "end": v(-45.64, 13.69) * mm});
            skLineSegment(sketch, "E161.right", {"start": v(-39.3, 20.04) * mm, "end": v(-39.3, 13.69) * mm});
            skSolve(sketch);
        }
        {
            var Q0;
            Q0 = qSketchRegion(id + "F322", true);
            var Q1;
            Q1=makeQuery(id+"F322.imprint","IMPRINT",FACE,{"disambiguationData":[TD([[makeQuery(id+"F322.imprint","IMPRINT",EDGE,{"derivedFrom":sQuery(id+"F322.wireOp",EDGE,"E161.bottom")}),1.0]])]});
            extrude(context, id + "F323", {"entities" : qUnion([Q0, Q1]), "operationType" : NewBodyOperationType.ADD, "oppositeDirection" : true, "depth" : 19.05 * mm});
        }
        {
            var Q0;
            Q0=makeQuery(id+"F323.boolean.opBoolean","MERGE",FACE,{"derivedFrom":[makeQuery(id+"F321.boolean.opBoolean","MERGE",FACE,{"derivedFrom":[makeQuery(id+"F319.boolean.opBoolean","MERGE",FACE,{"derivedFrom":[makeQuery(id+"F317.opExtrude","CAP_FACE",FACE,{"disambiguationData":[OSD([sQuery(id+"F316.wireOp",EDGE,"E158.bottom"),sQuery(id+"F316.wireOp",EDGE,"E158.top"),sQuery(id+"F316.wireOp",EDGE,"E158.left"),sQuery(id+"F316.wireOp",EDGE,"E158.right")])],"isStart":false}),makeQuery(id+"F319.opExtrude","SWEPT_FACE",FACE,{"disambiguationData":[OSD([sQuery(id+"F318.wireOp",EDGE,"E159.left")])]})]}),makeQuery(id+"F321.opExtrude","SWEPT_FACE",FACE,{"disambiguationData":[OSD([sQuery(id+"F320.wireOp",EDGE,"E160.left")])]})]}),makeQuery(id+"F323.opExtrude","SWEPT_FACE",FACE,{"disambiguationData":[OSD([sQuery(id+"F322.wireOp",EDGE,"E161.left")])]})]});
            var sketch = newSketch(context, id + "F324", { "sketchPlane" : qUnion([Q0])});
            skLineSegment(sketch, "E162.bottom", {"start": v(20.04, 95.25) * mm, "end": v(13.69, 95.25) * mm});
            skLineSegment(sketch, "E162.top", {"start": v(20.04, 88.9) * mm, "end": v(13.69, 88.9) * mm});
            skLineSegment(sketch, "E162.left", {"start": v(20.04, 95.25) * mm, "end": v(20.04, 88.9) * mm});
            skLineSegment(sketch, "E162.right", {"start": v(13.69, 95.25) * mm, "end": v(13.69, 88.9) * mm});
            skSolve(sketch);
        }
        {
            var Q0;
            Q0 = qSketchRegion(id + "F324", true);
            var Q1;
            Q1=makeQuery(id+"F324.imprint","IMPRINT",FACE,{"disambiguationData":[TD([[makeQuery(id+"F324.imprint","IMPRINT",EDGE,{"derivedFrom":sQuery(id+"F324.wireOp",EDGE,"E162.bottom")}),1.0]])]});
            extrude(context, id + "F325", {"entities" : qUnion([Q0, Q1]), "operationType" : NewBodyOperationType.ADD, "oppositeDirection" : true, "depth" : 19.05 * mm});
        }
        {
            var Q0;
            Q0=makeQuery(id+"F325.boolean.opBoolean","MERGE",FACE,{"derivedFrom":[makeQuery(id+"F323.opExtrude","CAP_FACE",FACE,{"disambiguationData":[OSD([sQuery(id+"F322.wireOp",EDGE,"E161.bottom"),sQuery(id+"F322.wireOp",EDGE,"E161.top"),sQuery(id+"F322.wireOp",EDGE,"E161.left"),sQuery(id+"F322.wireOp",EDGE,"E161.right")])],"isStart":false}),makeQuery(id+"F325.opExtrude","SWEPT_FACE",FACE,{"disambiguationData":[OSD([sQuery(id+"F324.wireOp",EDGE,"E162.bottom")])]})]});
            var sketch = newSketch(context, id + "F326", { "sketchPlane" : qUnion([Q0])});
            skLineSegment(sketch, "E163.bottom", {"start": v(-26.6, -20.04) * mm, "end": v(-32.94, -20.04) * mm});
            skLineSegment(sketch, "E163.top", {"start": v(-26.6, -13.69) * mm, "end": v(-32.94, -13.69) * mm});
            skLineSegment(sketch, "E163.left", {"start": v(-26.6, -20.04) * mm, "end": v(-26.6, -13.69) * mm});
            skLineSegment(sketch, "E163.right", {"start": v(-32.94, -20.04) * mm, "end": v(-32.94, -13.69) * mm});
            skSolve(sketch);
        }
        {
            var Q0;
            Q0 = qSketchRegion(id + "F326", true);
            var Q1;
            Q1=makeQuery(id+"F326.imprint","IMPRINT",FACE,{"disambiguationData":[TD([[makeQuery(id+"F326.imprint","IMPRINT",EDGE,{"derivedFrom":sQuery(id+"F326.wireOp",EDGE,"E163.bottom")}),-1.0]])]});
            extrude(context, id + "F327", {"entities" : qUnion([Q0, Q1]), "operationType" : NewBodyOperationType.ADD, "oppositeDirection" : true, "depth" : 31.75 * mm});
        }
        {
            var Q0;
            Q0=makeQuery(id+"F327.boolean.opBoolean","MERGE",FACE,{"derivedFrom":[makeQuery(id+"F325.opExtrude","CAP_FACE",FACE,{"disambiguationData":[OSD([sQuery(id+"F324.wireOp",EDGE,"E162.bottom"),sQuery(id+"F324.wireOp",EDGE,"E162.top"),sQuery(id+"F324.wireOp",EDGE,"E162.left"),sQuery(id+"F324.wireOp",EDGE,"E162.right")])],"isStart":false}),makeQuery(id+"F327.opExtrude","SWEPT_FACE",FACE,{"disambiguationData":[OSD([sQuery(id+"F326.wireOp",EDGE,"E163.left")])]})]});
            var sketch = newSketch(context, id + "F328", { "sketchPlane" : qUnion([Q0])});
            skLineSegment(sketch, "E164.bottom", {"start": v(-20.04, 63.5) * mm, "end": v(-13.69, 63.5) * mm});
            skLineSegment(sketch, "E164.top", {"start": v(-20.04, 69.85) * mm, "end": v(-13.69, 69.85) * mm});
            skLineSegment(sketch, "E164.left", {"start": v(-20.04, 63.5) * mm, "end": v(-20.04, 69.85) * mm});
            skLineSegment(sketch, "E164.right", {"start": v(-13.69, 63.5) * mm, "end": v(-13.69, 69.85) * mm});
            skSolve(sketch);
        }
        {
            var Q0;
            Q0 = qSketchRegion(id + "F328", true);
            var Q1;
            Q1=makeQuery(id+"F328.imprint","IMPRINT",FACE,{"disambiguationData":[TD([[makeQuery(id+"F328.imprint","IMPRINT",EDGE,{"derivedFrom":sQuery(id+"F328.wireOp",EDGE,"E164.bottom")}),1.0]])]});
            extrude(context, id + "F329", {"entities" : qUnion([Q0, Q1]), "operationType" : NewBodyOperationType.ADD, "oppositeDirection" : true, "depth" : 19.05 * mm});
        }
        {
            var Q0;
            Q0=makeQuery(id+"F329.boolean.opBoolean","MERGE",FACE,{"derivedFrom":[makeQuery(id+"F327.boolean.opBoolean","MERGE",FACE,{"derivedFrom":[makeQuery(id+"F325.boolean.opBoolean","MERGE",FACE,{"derivedFrom":[makeQuery(id+"F323.boolean.opBoolean","MERGE",FACE,{"derivedFrom":[makeQuery(id+"F321.opExtrude","CAP_FACE",FACE,{"disambiguationData":[OSD([sQuery(id+"F320.wireOp",EDGE,"E160.bottom"),sQuery(id+"F320.wireOp",EDGE,"E160.top"),sQuery(id+"F320.wireOp",EDGE,"E160.left"),sQuery(id+"F320.wireOp",EDGE,"E160.right")])],"isStart":false}),makeQuery(id+"F323.opExtrude","SWEPT_FACE",FACE,{"disambiguationData":[OSD([sQuery(id+"F322.wireOp",EDGE,"E161.bottom")])]})]}),makeQuery(id+"F325.opExtrude","SWEPT_FACE",FACE,{"disambiguationData":[OSD([sQuery(id+"F324.wireOp",EDGE,"E162.left")])]})]}),makeQuery(id+"F327.opExtrude","SWEPT_FACE",FACE,{"disambiguationData":[OSD([sQuery(id+"F326.wireOp",EDGE,"E163.bottom")])]})]}),makeQuery(id+"F329.opExtrude","SWEPT_FACE",FACE,{"disambiguationData":[OSD([sQuery(id+"F328.wireOp",EDGE,"E164.left")])]})]});
            var sketch = newSketch(context, id + "F330", { "sketchPlane" : qUnion([Q0])});
            skLineSegment(sketch, "E165.bottom", {"start": v(-45.64, 63.5) * mm, "end": v(-39.3, 63.5) * mm});
            skLineSegment(sketch, "E165.top", {"start": v(-45.64, 69.85) * mm, "end": v(-39.3, 69.85) * mm});
            skLineSegment(sketch, "E165.left", {"start": v(-45.64, 63.5) * mm, "end": v(-45.64, 69.85) * mm});
            skLineSegment(sketch, "E165.right", {"start": v(-39.3, 63.5) * mm, "end": v(-39.3, 69.85) * mm});
            skSolve(sketch);
        }
        {
            var Q0;
            Q0 = qSketchRegion(id + "F330", true);
            var Q1;
            Q1=makeQuery(id+"F330.imprint","IMPRINT",FACE,{"disambiguationData":[TD([[makeQuery(id+"F330.imprint","IMPRINT",EDGE,{"derivedFrom":sQuery(id+"F330.wireOp",EDGE,"E165.bottom")}),-1.0]])]});
            extrude(context, id + "F331", {"entities" : qUnion([Q0, Q1]), "operationType" : NewBodyOperationType.ADD, "oppositeDirection" : true, "depth" : 19.05 * mm});
        }
        {
            var Q0;
            Q0=makeQuery(id+"F331.boolean.opBoolean","MERGE",FACE,{"derivedFrom":[makeQuery(id+"F329.opExtrude","CAP_FACE",FACE,{"disambiguationData":[OSD([sQuery(id+"F328.wireOp",EDGE,"E164.bottom"),sQuery(id+"F328.wireOp",EDGE,"E164.top"),sQuery(id+"F328.wireOp",EDGE,"E164.left"),sQuery(id+"F328.wireOp",EDGE,"E164.right")])],"isStart":false}),makeQuery(id+"F331.opExtrude","SWEPT_FACE",FACE,{"disambiguationData":[OSD([sQuery(id+"F330.wireOp",EDGE,"E165.left")])]})]});
            var sketch = newSketch(context, id + "F332", { "sketchPlane" : qUnion([Q0])});
            skLineSegment(sketch, "E166.bottom", {"start": v(0.99, 63.5) * mm, "end": v(7.34, 63.5) * mm});
            skLineSegment(sketch, "E166.top", {"start": v(0.99, 69.85) * mm, "end": v(7.34, 69.85) * mm});
            skLineSegment(sketch, "E166.left", {"start": v(0.99, 63.5) * mm, "end": v(0.99, 69.85) * mm});
            skLineSegment(sketch, "E166.right", {"start": v(7.34, 63.5) * mm, "end": v(7.34, 69.85) * mm});
            skSolve(sketch);
        }
        {
            var Q0;
            Q0 = qSketchRegion(id + "F332", true);
            var Q1;
            Q1=makeQuery(id+"F332.imprint","IMPRINT",FACE,{"disambiguationData":[TD([[makeQuery(id+"F332.imprint","IMPRINT",EDGE,{"derivedFrom":sQuery(id+"F332.wireOp",EDGE,"E166.bottom")}),-1.0]])]});
            extrude(context, id + "F333", {"entities" : qUnion([Q0, Q1]), "operationType" : NewBodyOperationType.ADD, "oppositeDirection" : true, "depth" : 19.05 * mm});
        }
        {
            var Q0;
            Q0=makeQuery(id+"F333.boolean.opBoolean","MERGE",FACE,{"derivedFrom":[makeQuery(id+"F331.boolean.opBoolean","MERGE",FACE,{"derivedFrom":[makeQuery(id+"F329.opExtrude","SWEPT_FACE",FACE,{"disambiguationData":[OSD([sQuery(id+"F328.wireOp",EDGE,"E164.top")])]}),makeQuery(id+"F331.opExtrude","SWEPT_FACE",FACE,{"disambiguationData":[OSD([sQuery(id+"F330.wireOp",EDGE,"E165.top")])]})]}),makeQuery(id+"F333.opExtrude","SWEPT_FACE",FACE,{"disambiguationData":[OSD([sQuery(id+"F332.wireOp",EDGE,"E166.top")])]})]});
            var sketch = newSketch(context, id + "F334", { "sketchPlane" : qUnion([Q0])});
            skLineSegment(sketch, "E167.bottom", {"start": v(-26.6, -0.99) * mm, "end": v(-32.94, -0.99) * mm});
            skLineSegment(sketch, "E167.top", {"start": v(-26.6, -7.34) * mm, "end": v(-32.94, -7.34) * mm});
            skLineSegment(sketch, "E167.left", {"start": v(-26.6, -0.99) * mm, "end": v(-26.6, -7.34) * mm});
            skLineSegment(sketch, "E167.right", {"start": v(-32.94, -0.99) * mm, "end": v(-32.94, -7.34) * mm});
            skSolve(sketch);
        }
        {
            var Q0;
            Q0 = qSketchRegion(id + "F334", true);
            var Q1;
            Q1=makeQuery(id+"F334.imprint","IMPRINT",FACE,{"disambiguationData":[TD([[makeQuery(id+"F334.imprint","IMPRINT",EDGE,{"derivedFrom":sQuery(id+"F334.wireOp",EDGE,"E167.bottom")}),-1.0]])]});
            extrude(context, id + "F335", {"entities" : qUnion([Q0, Q1]), "operationType" : NewBodyOperationType.ADD, "oppositeDirection" : true, "depth" : 19.05 * mm});
        }
        {
            var Q0;
            Q0=makeQuery(id+"F335.boolean.opBoolean","MERGE",FACE,{"derivedFrom":[makeQuery(id+"F333.opExtrude","CAP_FACE",FACE,{"disambiguationData":[OSD([sQuery(id+"F332.wireOp",EDGE,"E166.bottom"),sQuery(id+"F332.wireOp",EDGE,"E166.top"),sQuery(id+"F332.wireOp",EDGE,"E166.left"),sQuery(id+"F332.wireOp",EDGE,"E166.right")])],"isStart":false}),makeQuery(id+"F335.opExtrude","SWEPT_FACE",FACE,{"disambiguationData":[OSD([sQuery(id+"F334.wireOp",EDGE,"E167.left")])]})]});
            var sketch = newSketch(context, id + "F336", { "sketchPlane" : qUnion([Q0])});
            skLineSegment(sketch, "E168.bottom", {"start": v(-7.34, 50.8) * mm, "end": v(-0.99, 50.8) * mm});
            skLineSegment(sketch, "E168.top", {"start": v(-7.34, 57.15) * mm, "end": v(-0.99, 57.15) * mm});
            skLineSegment(sketch, "E168.left", {"start": v(-7.34, 50.8) * mm, "end": v(-7.34, 57.15) * mm});
            skLineSegment(sketch, "E168.right", {"start": v(-0.99, 50.8) * mm, "end": v(-0.99, 57.15) * mm});
            skSolve(sketch);
        }
        {
            var Q0;
            Q0 = qSketchRegion(id + "F336", true);
            var Q1;
            Q1=makeQuery(id+"F336.imprint","IMPRINT",FACE,{"disambiguationData":[TD([[makeQuery(id+"F336.imprint","IMPRINT",EDGE,{"derivedFrom":sQuery(id+"F336.wireOp",EDGE,"E168.bottom")}),1.0]])]});
            extrude(context, id + "F337", {"entities" : qUnion([Q0, Q1]), "operationType" : NewBodyOperationType.ADD, "oppositeDirection" : true, "depth" : 19.05 * mm});
        }
        {
            var Q0;
            Q0=makeQuery(id+"F337.boolean.opBoolean","MERGE",FACE,{"derivedFrom":[makeQuery(id+"F335.boolean.opBoolean","MERGE",FACE,{"derivedFrom":[makeQuery(id+"F333.boolean.opBoolean","MERGE",FACE,{"derivedFrom":[makeQuery(id+"F331.opExtrude","CAP_FACE",FACE,{"disambiguationData":[OSD([sQuery(id+"F330.wireOp",EDGE,"E165.bottom"),sQuery(id+"F330.wireOp",EDGE,"E165.top"),sQuery(id+"F330.wireOp",EDGE,"E165.left"),sQuery(id+"F330.wireOp",EDGE,"E165.right")])],"isStart":false}),makeQuery(id+"F333.opExtrude","SWEPT_FACE",FACE,{"disambiguationData":[OSD([sQuery(id+"F332.wireOp",EDGE,"E166.left")])]})]}),makeQuery(id+"F335.opExtrude","SWEPT_FACE",FACE,{"disambiguationData":[OSD([sQuery(id+"F334.wireOp",EDGE,"E167.bottom")])]})]}),makeQuery(id+"F337.opExtrude","SWEPT_FACE",FACE,{"disambiguationData":[OSD([sQuery(id+"F336.wireOp",EDGE,"E168.right")])]})]});
            var sketch = newSketch(context, id + "F338", { "sketchPlane" : qUnion([Q0])});
            skLineSegment(sketch, "E169.bottom", {"start": v(45.64, 50.8) * mm, "end": v(39.3, 50.8) * mm});
            skLineSegment(sketch, "E169.top", {"start": v(45.64, 57.15) * mm, "end": v(39.3, 57.15) * mm});
            skLineSegment(sketch, "E169.left", {"start": v(45.64, 50.8) * mm, "end": v(45.64, 57.15) * mm});
            skLineSegment(sketch, "E169.right", {"start": v(39.3, 50.8) * mm, "end": v(39.3, 57.15) * mm});
            skSolve(sketch);
        }
        {
            var Q0;
            Q0 = qSketchRegion(id + "F338", true);
            var Q1;
            Q1=makeQuery(id+"F338.imprint","IMPRINT",FACE,{"disambiguationData":[TD([[makeQuery(id+"F338.imprint","IMPRINT",EDGE,{"derivedFrom":sQuery(id+"F338.wireOp",EDGE,"E169.bottom")}),-1.0]])]});
            extrude(context, id + "F339", {"entities" : qUnion([Q0, Q1]), "operationType" : NewBodyOperationType.ADD, "oppositeDirection" : true, "depth" : 19.05 * mm});
        }
        {
            var Q0;
            Q0=makeQuery(id+"F339.boolean.opBoolean","MERGE",FACE,{"derivedFrom":[makeQuery(id+"F337.opExtrude","CAP_FACE",FACE,{"disambiguationData":[OSD([sQuery(id+"F336.wireOp",EDGE,"E168.bottom"),sQuery(id+"F336.wireOp",EDGE,"E168.top"),sQuery(id+"F336.wireOp",EDGE,"E168.left"),sQuery(id+"F336.wireOp",EDGE,"E168.right")])],"isStart":false}),makeQuery(id+"F339.opExtrude","SWEPT_FACE",FACE,{"disambiguationData":[OSD([sQuery(id+"F338.wireOp",EDGE,"E169.left")])]})]});
            var sketch = newSketch(context, id + "F340", { "sketchPlane" : qUnion([Q0])});
            skLineSegment(sketch, "E170.bottom", {"start": v(20.04, 50.8) * mm, "end": v(13.69, 50.8) * mm});
            skLineSegment(sketch, "E170.top", {"start": v(20.04, 57.15) * mm, "end": v(13.69, 57.15) * mm});
            skLineSegment(sketch, "E170.left", {"start": v(20.04, 50.8) * mm, "end": v(20.04, 57.15) * mm});
            skLineSegment(sketch, "E170.right", {"start": v(13.69, 50.8) * mm, "end": v(13.69, 57.15) * mm});
            skSolve(sketch);
        }
        {
            var Q0;
            Q0 = qSketchRegion(id + "F340", true);
            var Q1;
            Q1=makeQuery(id+"F340.imprint","IMPRINT",FACE,{"disambiguationData":[TD([[makeQuery(id+"F340.imprint","IMPRINT",EDGE,{"derivedFrom":sQuery(id+"F340.wireOp",EDGE,"E170.bottom")}),-1.0]])]});
            extrude(context, id + "F341", {"entities" : qUnion([Q0, Q1]), "operationType" : NewBodyOperationType.ADD, "oppositeDirection" : true, "depth" : 19.05 * mm});
        }
        {
            var Q0;
            Q0=makeQuery(id+"F341.boolean.opBoolean","MERGE",FACE,{"derivedFrom":[makeQuery(id+"F339.boolean.opBoolean","MERGE",FACE,{"derivedFrom":[makeQuery(id+"F337.opExtrude","SWEPT_FACE",FACE,{"disambiguationData":[OSD([sQuery(id+"F336.wireOp",EDGE,"E168.top")])]}),makeQuery(id+"F339.opExtrude","SWEPT_FACE",FACE,{"disambiguationData":[OSD([sQuery(id+"F338.wireOp",EDGE,"E169.top")])]})]}),makeQuery(id+"F341.opExtrude","SWEPT_FACE",FACE,{"disambiguationData":[OSD([sQuery(id+"F340.wireOp",EDGE,"E170.top")])]})]});
            var sketch = newSketch(context, id + "F342", { "sketchPlane" : qUnion([Q0])});
            skLineSegment(sketch, "E171.bottom", {"start": v(-26.6, -20.04) * mm, "end": v(-32.94, -20.04) * mm});
            skLineSegment(sketch, "E171.top", {"start": v(-26.6, -13.69) * mm, "end": v(-32.94, -13.69) * mm});
            skLineSegment(sketch, "E171.left", {"start": v(-26.6, -20.04) * mm, "end": v(-26.6, -13.69) * mm});
            skLineSegment(sketch, "E171.right", {"start": v(-32.94, -20.04) * mm, "end": v(-32.94, -13.69) * mm});
            skSolve(sketch);
        }
        {
            var Q0;
            Q0 = qSketchRegion(id + "F342", true);
            var Q1;
            Q1=makeQuery(id+"F342.imprint","IMPRINT",FACE,{"disambiguationData":[TD([[makeQuery(id+"F342.imprint","IMPRINT",EDGE,{"derivedFrom":sQuery(id+"F342.wireOp",EDGE,"E171.bottom")}),1.0]])]});
            extrude(context, id + "F343", {"entities" : qUnion([Q0, Q1]), "operationType" : NewBodyOperationType.ADD, "oppositeDirection" : true, "depth" : 31.75 * mm});
        }
        {
            var Q0;
            Q0=makeQuery(id+"F343.boolean.opBoolean","MERGE",FACE,{"derivedFrom":[makeQuery(id+"F341.opExtrude","CAP_FACE",FACE,{"disambiguationData":[OSD([sQuery(id+"F340.wireOp",EDGE,"E170.bottom"),sQuery(id+"F340.wireOp",EDGE,"E170.top"),sQuery(id+"F340.wireOp",EDGE,"E170.left"),sQuery(id+"F340.wireOp",EDGE,"E170.right")])],"isStart":false}),makeQuery(id+"F343.opExtrude","SWEPT_FACE",FACE,{"disambiguationData":[OSD([sQuery(id+"F342.wireOp",EDGE,"E171.left")])]})]});
            var sketch = newSketch(context, id + "F344", { "sketchPlane" : qUnion([Q0])});
            skLineSegment(sketch, "E172.bottom", {"start": v(-13.69, 25.4) * mm, "end": v(-20.04, 25.4) * mm});
            skLineSegment(sketch, "E172.top", {"start": v(-13.69, 31.75) * mm, "end": v(-20.04, 31.75) * mm});
            skLineSegment(sketch, "E172.left", {"start": v(-13.69, 25.4) * mm, "end": v(-13.69, 31.75) * mm});
            skLineSegment(sketch, "E172.right", {"start": v(-20.04, 25.4) * mm, "end": v(-20.04, 31.75) * mm});
            skSolve(sketch);
        }
        {
            var Q0;
            Q0 = qSketchRegion(id + "F344", true);
            var Q1;
            Q1=makeQuery(id+"F344.imprint","IMPRINT",FACE,{"disambiguationData":[TD([[makeQuery(id+"F344.imprint","IMPRINT",EDGE,{"derivedFrom":sQuery(id+"F344.wireOp",EDGE,"E172.bottom")}),1.0]])]});
            extrude(context, id + "F345", {"entities" : qUnion([Q0, Q1]), "operationType" : NewBodyOperationType.ADD, "oppositeDirection" : true, "depth" : 19.05 * mm});
        }
        {
            var Q0;
            Q0=makeQuery(id+"F345.boolean.opBoolean","MERGE",FACE,{"derivedFrom":[makeQuery(id+"F343.opExtrude","CAP_FACE",FACE,{"disambiguationData":[OSD([sQuery(id+"F342.wireOp",EDGE,"E171.bottom"),sQuery(id+"F342.wireOp",EDGE,"E171.top"),sQuery(id+"F342.wireOp",EDGE,"E171.left"),sQuery(id+"F342.wireOp",EDGE,"E171.right")])],"isStart":false}),makeQuery(id+"F345.opExtrude","SWEPT_FACE",FACE,{"disambiguationData":[OSD([sQuery(id+"F344.wireOp",EDGE,"E172.bottom")])]})]});
            var sketch = newSketch(context, id + "F346", { "sketchPlane" : qUnion([Q0])});
            skLineSegment(sketch, "E173.bottom", {"start": v(-45.64, 13.69) * mm, "end": v(-39.3, 13.69) * mm});
            skLineSegment(sketch, "E173.top", {"start": v(-45.64, 20.04) * mm, "end": v(-39.3, 20.04) * mm});
            skLineSegment(sketch, "E173.left", {"start": v(-45.64, 13.69) * mm, "end": v(-45.64, 20.04) * mm});
            skLineSegment(sketch, "E173.right", {"start": v(-39.3, 13.69) * mm, "end": v(-39.3, 20.04) * mm});
            skSolve(sketch);
        }
        {
            var Q0;
            Q0 = qSketchRegion(id + "F346", true);
            var Q1;
            Q1=makeQuery(id+"F346.imprint","IMPRINT",FACE,{"disambiguationData":[TD([[makeQuery(id+"F346.imprint","IMPRINT",EDGE,{"derivedFrom":sQuery(id+"F346.wireOp",EDGE,"E173.bottom")}),-1.0]])]});
            extrude(context, id + "F347", {"entities" : qUnion([Q0, Q1]), "operationType" : NewBodyOperationType.ADD, "oppositeDirection" : true, "depth" : 19.05 * mm});
        }
        {
            var Q0;
            Q0=makeQuery(id+"F347.boolean.opBoolean","MERGE",FACE,{"derivedFrom":[makeQuery(id+"F345.boolean.opBoolean","MERGE",FACE,{"derivedFrom":[makeQuery(id+"F343.boolean.opBoolean","MERGE",FACE,{"derivedFrom":[makeQuery(id+"F341.boolean.opBoolean","MERGE",FACE,{"derivedFrom":[makeQuery(id+"F339.opExtrude","CAP_FACE",FACE,{"disambiguationData":[OSD([sQuery(id+"F338.wireOp",EDGE,"E169.bottom"),sQuery(id+"F338.wireOp",EDGE,"E169.top"),sQuery(id+"F338.wireOp",EDGE,"E169.left"),sQuery(id+"F338.wireOp",EDGE,"E169.right")])],"isStart":false}),makeQuery(id+"F341.opExtrude","SWEPT_FACE",FACE,{"disambiguationData":[OSD([sQuery(id+"F340.wireOp",EDGE,"E170.left")])]})]}),makeQuery(id+"F343.opExtrude","SWEPT_FACE",FACE,{"disambiguationData":[OSD([sQuery(id+"F342.wireOp",EDGE,"E171.bottom")])]})]}),makeQuery(id+"F345.opExtrude","SWEPT_FACE",FACE,{"disambiguationData":[OSD([sQuery(id+"F344.wireOp",EDGE,"E172.right")])]})]}),makeQuery(id+"F347.opExtrude","SWEPT_FACE",FACE,{"disambiguationData":[OSD([sQuery(id+"F346.wireOp",EDGE,"E173.top")])]})]});
            var sketch = newSketch(context, id + "F348", { "sketchPlane" : qUnion([Q0])});
            skLineSegment(sketch, "E174.bottom", {"start": v(-45.64, 44.45) * mm, "end": v(-39.3, 44.45) * mm});
            skLineSegment(sketch, "E174.top", {"start": v(-45.64, 38.1) * mm, "end": v(-39.3, 38.1) * mm});
            skLineSegment(sketch, "E174.left", {"start": v(-45.64, 44.45) * mm, "end": v(-45.64, 38.1) * mm});
            skLineSegment(sketch, "E174.right", {"start": v(-39.3, 44.45) * mm, "end": v(-39.3, 38.1) * mm});
            skSolve(sketch);
        }
        {
            var Q0;
            Q0=makeQuery(id+"F348.imprint","IMPRINT",FACE,{"disambiguationData":[TD([[makeQuery(id+"F348.imprint","IMPRINT",EDGE,{"derivedFrom":sQuery(id+"F348.wireOp",EDGE,"E174.bottom")}),-1.0]])]});
            extrude(context, id + "F349", {"entities" : qUnion([Q0]), "operationType" : NewBodyOperationType.ADD, "oppositeDirection" : true, "depth" : 19.05 * mm});
        }
        {
            var Q0;
            Q0=makeQuery(id+"F349.boolean.opBoolean","MERGE",FACE,{"derivedFrom":[makeQuery(id+"F347.opExtrude","CAP_FACE",FACE,{"disambiguationData":[OSD([sQuery(id+"F346.wireOp",EDGE,"E173.bottom"),sQuery(id+"F346.wireOp",EDGE,"E173.top"),sQuery(id+"F346.wireOp",EDGE,"E173.left"),sQuery(id+"F346.wireOp",EDGE,"E173.right")])],"isStart":false}),makeQuery(id+"F349.opExtrude","SWEPT_FACE",FACE,{"disambiguationData":[OSD([sQuery(id+"F348.wireOp",EDGE,"E174.bottom")])]})]});
            var sketch = newSketch(context, id + "F350", { "sketchPlane" : qUnion([Q0])});
            skLineSegment(sketch, "E175.bottom", {"start": v(-45.64, -0.99) * mm, "end": v(-39.3, -0.99) * mm});
            skLineSegment(sketch, "E175.top", {"start": v(-45.64, -7.34) * mm, "end": v(-39.3, -7.34) * mm});
            skLineSegment(sketch, "E175.left", {"start": v(-45.64, -0.99) * mm, "end": v(-45.64, -7.34) * mm});
            skLineSegment(sketch, "E175.right", {"start": v(-39.3, -0.99) * mm, "end": v(-39.3, -7.34) * mm});
            skSolve(sketch);
        }
        {
            var Q0;
            Q0 = qSketchRegion(id + "F350", true);
            extrude(context, id + "F351", {"entities" : qUnion([Q0]), "operationType" : NewBodyOperationType.ADD, "oppositeDirection" : true, "depth" : 19.05 * mm});
        }
        {
            var Q0;
            Q0=makeQuery(id+"F351.boolean.opBoolean","MERGE",FACE,{"derivedFrom":[makeQuery(id+"F349.boolean.opBoolean","MERGE",FACE,{"derivedFrom":[makeQuery(id+"F347.boolean.opBoolean","MERGE",FACE,{"derivedFrom":[makeQuery(id+"F345.opExtrude","CAP_FACE",FACE,{"disambiguationData":[OSD([sQuery(id+"F344.wireOp",EDGE,"E172.bottom"),sQuery(id+"F344.wireOp",EDGE,"E172.top"),sQuery(id+"F344.wireOp",EDGE,"E172.left"),sQuery(id+"F344.wireOp",EDGE,"E172.right")])],"isStart":false}),makeQuery(id+"F347.opExtrude","SWEPT_FACE",FACE,{"disambiguationData":[OSD([sQuery(id+"F346.wireOp",EDGE,"E173.left")])]})]}),makeQuery(id+"F349.opExtrude","SWEPT_FACE",FACE,{"disambiguationData":[OSD([sQuery(id+"F348.wireOp",EDGE,"E174.left")])]})]}),makeQuery(id+"F351.opExtrude","SWEPT_FACE",FACE,{"disambiguationData":[OSD([sQuery(id+"F350.wireOp",EDGE,"E175.left")])]})]});
            var sketch = newSketch(context, id + "F352", { "sketchPlane" : qUnion([Q0])});
            skLineSegment(sketch, "E176.bottom", {"start": v(0.99, 25.4) * mm, "end": v(7.34, 25.4) * mm});
            skLineSegment(sketch, "E176.top", {"start": v(0.99, 31.75) * mm, "end": v(7.34, 31.75) * mm});
            skLineSegment(sketch, "E176.left", {"start": v(0.99, 25.4) * mm, "end": v(0.99, 31.75) * mm});
            skLineSegment(sketch, "E176.right", {"start": v(7.34, 25.4) * mm, "end": v(7.34, 31.75) * mm});
            skSolve(sketch);
        }
        {
            var Q0;
            Q0 = qSketchRegion(id + "F352", true);
            var Q1;
            Q1=makeQuery(id+"F352.imprint","IMPRINT",FACE,{"disambiguationData":[TD([[makeQuery(id+"F352.imprint","IMPRINT",EDGE,{"derivedFrom":sQuery(id+"F352.wireOp",EDGE,"E176.bottom")}),-1.0]])]});
            extrude(context, id + "F353", {"entities" : qUnion([Q0, Q1]), "operationType" : NewBodyOperationType.ADD, "oppositeDirection" : true, "depth" : 19.05 * mm});
        }
        {
            var Q0;
            Q0=makeQuery(id+"F353.boolean.opBoolean","MERGE",FACE,{"derivedFrom":[makeQuery(id+"F351.opExtrude","CAP_FACE",FACE,{"disambiguationData":[OSD([sQuery(id+"F350.wireOp",EDGE,"E175.bottom"),sQuery(id+"F350.wireOp",EDGE,"E175.top"),sQuery(id+"F350.wireOp",EDGE,"E175.left"),sQuery(id+"F350.wireOp",EDGE,"E175.right")])],"isStart":false}),makeQuery(id+"F353.opExtrude","SWEPT_FACE",FACE,{"disambiguationData":[OSD([sQuery(id+"F352.wireOp",EDGE,"E176.bottom")])]})]});
            var sketch = newSketch(context, id + "F354", { "sketchPlane" : qUnion([Q0])});
            skLineSegment(sketch, "E177.bottom", {"start": v(-26.6, 7.34) * mm, "end": v(-32.94, 7.34) * mm});
            skLineSegment(sketch, "E177.top", {"start": v(-26.6, 0.99) * mm, "end": v(-32.94, 0.99) * mm});
            skLineSegment(sketch, "E177.left", {"start": v(-26.6, 7.34) * mm, "end": v(-26.6, 0.99) * mm});
            skLineSegment(sketch, "E177.right", {"start": v(-32.94, 7.34) * mm, "end": v(-32.94, 0.99) * mm});
            skSolve(sketch);
        }
        {
            var Q0;
            Q0 = qSketchRegion(id + "F354", true);
            var Q1;
            Q1=makeQuery(id+"F354.imprint","IMPRINT",FACE,{"disambiguationData":[TD([[makeQuery(id+"F354.imprint","IMPRINT",EDGE,{"derivedFrom":sQuery(id+"F354.wireOp",EDGE,"E177.bottom")}),-1.0]])]});
            extrude(context, id + "F355", {"entities" : qUnion([Q0, Q1]), "operationType" : NewBodyOperationType.ADD, "oppositeDirection" : true, "depth" : 19.05 * mm});
        }
        {
            var Q0;
            Q0=makeQuery(id+"F355.boolean.opBoolean","MERGE",FACE,{"derivedFrom":[makeQuery(id+"F353.boolean.opBoolean","MERGE",FACE,{"derivedFrom":[makeQuery(id+"F351.opExtrude","SWEPT_FACE",FACE,{"disambiguationData":[OSD([sQuery(id+"F350.wireOp",EDGE,"E175.top")])]}),makeQuery(id+"F353.opExtrude","SWEPT_FACE",FACE,{"disambiguationData":[OSD([sQuery(id+"F352.wireOp",EDGE,"E176.right")])]})]}),makeQuery(id+"F355.opExtrude","SWEPT_FACE",FACE,{"disambiguationData":[OSD([sQuery(id+"F354.wireOp",EDGE,"E177.bottom")])]})]});
            var sketch = newSketch(context, id + "F356", { "sketchPlane" : qUnion([Q0])});
            skLineSegment(sketch, "E178.bottom", {"start": v(-26.6, 44.45) * mm, "end": v(-32.94, 44.45) * mm});
            skLineSegment(sketch, "E178.top", {"start": v(-26.6, 38.1) * mm, "end": v(-32.94, 38.1) * mm});
            skLineSegment(sketch, "E178.left", {"start": v(-26.6, 44.45) * mm, "end": v(-26.6, 38.1) * mm});
            skLineSegment(sketch, "E178.right", {"start": v(-32.94, 44.45) * mm, "end": v(-32.94, 38.1) * mm});
            skSolve(sketch);
        }
        {
            var Q0;
            Q0=makeQuery(id+"F356.imprint","IMPRINT",FACE,{"disambiguationData":[TD([[makeQuery(id+"F356.imprint","IMPRINT",EDGE,{"derivedFrom":sQuery(id+"F356.wireOp",EDGE,"E178.bottom")}),-1.0]])]});
            extrude(context, id + "F357", {"entities" : qUnion([Q0]), "operationType" : NewBodyOperationType.ADD, "oppositeDirection" : true, "depth" : 31.75 * mm});
        }
        {
            var Q0;
            Q0=makeQuery(id+"F357.boolean.opBoolean","MERGE",FACE,{"derivedFrom":[makeQuery(id+"F355.opExtrude","CAP_FACE",FACE,{"disambiguationData":[OSD([sQuery(id+"F354.wireOp",EDGE,"E177.bottom"),sQuery(id+"F354.wireOp",EDGE,"E177.top"),sQuery(id+"F354.wireOp",EDGE,"E177.left"),sQuery(id+"F354.wireOp",EDGE,"E177.right")])],"isStart":false}),makeQuery(id+"F357.opExtrude","SWEPT_FACE",FACE,{"disambiguationData":[OSD([sQuery(id+"F356.wireOp",EDGE,"E178.bottom")])]})]});
            var sketch = newSketch(context, id + "F358", { "sketchPlane" : qUnion([Q0])});
            skLineSegment(sketch, "E179.bottom", {"start": v(-26.6, 24.41) * mm, "end": v(-32.94, 24.41) * mm});
            skLineSegment(sketch, "E179.top", {"start": v(-26.6, 18.06) * mm, "end": v(-32.94, 18.06) * mm});
            skLineSegment(sketch, "E179.left", {"start": v(-26.6, 24.41) * mm, "end": v(-26.6, 18.06) * mm});
            skLineSegment(sketch, "E179.right", {"start": v(-32.94, 24.41) * mm, "end": v(-32.94, 18.06) * mm});
            skSolve(sketch);
        }
        {
            var Q0;
            Q0 = qSketchRegion(id + "F358", true);
            var Q1;
            Q1=makeQuery(id+"F358.imprint","IMPRINT",FACE,{"disambiguationData":[TD([[makeQuery(id+"F358.imprint","IMPRINT",EDGE,{"derivedFrom":sQuery(id+"F358.wireOp",EDGE,"E179.bottom")}),-1.0]])]});
            extrude(context, id + "F359", {"entities" : qUnion([Q0, Q1]), "operationType" : NewBodyOperationType.ADD, "oppositeDirection" : true, "depth" : 19.05 * mm});
        }
        {
            var Q0;
            Q0=makeQuery(id+"F359.boolean.opBoolean","MERGE",FACE,{"derivedFrom":[makeQuery(id+"F357.opExtrude","CAP_FACE",FACE,{"disambiguationData":[OSD([sQuery(id+"F356.wireOp",EDGE,"E178.bottom"),sQuery(id+"F356.wireOp",EDGE,"E178.top"),sQuery(id+"F356.wireOp",EDGE,"E178.left"),sQuery(id+"F356.wireOp",EDGE,"E178.right")])],"isStart":false}),makeQuery(id+"F359.opExtrude","SWEPT_FACE",FACE,{"disambiguationData":[OSD([sQuery(id+"F358.wireOp",EDGE,"E179.bottom")])]})]});
            var sketch = newSketch(context, id + "F360", { "sketchPlane" : qUnion([Q0])});
            skLineSegment(sketch, "E180.bottom", {"start": v(26.6, 25.4) * mm, "end": v(32.94, 25.4) * mm});
            skLineSegment(sketch, "E180.top", {"start": v(26.6, 31.75) * mm, "end": v(32.94, 31.75) * mm});
            skLineSegment(sketch, "E180.left", {"start": v(26.6, 25.4) * mm, "end": v(26.6, 31.75) * mm});
            skLineSegment(sketch, "E180.right", {"start": v(32.94, 25.4) * mm, "end": v(32.94, 31.75) * mm});
            skSolve(sketch);
        }
        {
            var Q0;
            Q0 = qSketchRegion(id + "F360", true);
            var Q1;
            Q1=makeQuery(id+"F360.imprint","IMPRINT",FACE,{"disambiguationData":[TD([[makeQuery(id+"F360.imprint","IMPRINT",EDGE,{"derivedFrom":sQuery(id+"F360.wireOp",EDGE,"E180.bottom")}),-1.0]])]});
            extrude(context, id + "F361", {"entities" : qUnion([Q0, Q1]), "operationType" : NewBodyOperationType.ADD, "oppositeDirection" : true, "depth" : 19.05 * mm});
        }
        {
            var Q0;
            Q0=makeQuery(id+"F361.boolean.opBoolean","MERGE",FACE,{"derivedFrom":[makeQuery(id+"F359.boolean.opBoolean","MERGE",FACE,{"derivedFrom":[makeQuery(id+"F357.boolean.opBoolean","MERGE",FACE,{"derivedFrom":[makeQuery(id+"F355.boolean.opBoolean","MERGE",FACE,{"derivedFrom":[makeQuery(id+"F353.opExtrude","CAP_FACE",FACE,{"disambiguationData":[OSD([sQuery(id+"F352.wireOp",EDGE,"E176.bottom"),sQuery(id+"F352.wireOp",EDGE,"E176.top"),sQuery(id+"F352.wireOp",EDGE,"E176.left"),sQuery(id+"F352.wireOp",EDGE,"E176.right")])],"isStart":false}),makeQuery(id+"F355.opExtrude","SWEPT_FACE",FACE,{"disambiguationData":[OSD([sQuery(id+"F354.wireOp",EDGE,"E177.left")])]})]}),makeQuery(id+"F357.opExtrude","SWEPT_FACE",FACE,{"disambiguationData":[OSD([sQuery(id+"F356.wireOp",EDGE,"E178.left")])]})]}),makeQuery(id+"F359.opExtrude","SWEPT_FACE",FACE,{"disambiguationData":[OSD([sQuery(id+"F358.wireOp",EDGE,"E179.left")])]})]}),makeQuery(id+"F361.opExtrude","SWEPT_FACE",FACE,{"disambiguationData":[OSD([sQuery(id+"F360.wireOp",EDGE,"E180.left")])]})]});
            var sketch = newSketch(context, id + "F362", { "sketchPlane" : qUnion([Q0])});
            skLineSegment(sketch, "E181.bottom", {"start": v(5.36, 25.4) * mm, "end": v(11.71, 25.4) * mm});
            skLineSegment(sketch, "E181.top", {"start": v(5.36, 31.75) * mm, "end": v(11.71, 31.75) * mm});
            skLineSegment(sketch, "E181.left", {"start": v(5.36, 25.4) * mm, "end": v(5.36, 31.75) * mm});
            skLineSegment(sketch, "E181.right", {"start": v(11.71, 25.4) * mm, "end": v(11.71, 31.75) * mm});
            skSolve(sketch);
        }
        {
            var Q0;
            Q0=makeQuery(id+"F362.imprint","IMPRINT",FACE,{"disambiguationData":[TD([[makeQuery(id+"F362.imprint","IMPRINT",EDGE,{"derivedFrom":sQuery(id+"F362.wireOp",EDGE,"E181.bottom")}),1.0]])]});
            extrude(context, id + "F363", {"entities" : qUnion([Q0]), "operationType" : NewBodyOperationType.ADD, "oppositeDirection" : true, "depth" : 19.05 * mm});
        }
        {
            var Q0;
            Q0=makeQuery(id+"F363.boolean.opBoolean","MERGE",FACE,{"derivedFrom":[makeQuery(id+"F361.opExtrude","CAP_FACE",FACE,{"disambiguationData":[OSD([sQuery(id+"F360.wireOp",EDGE,"E180.bottom"),sQuery(id+"F360.wireOp",EDGE,"E180.top"),sQuery(id+"F360.wireOp",EDGE,"E180.left"),sQuery(id+"F360.wireOp",EDGE,"E180.right")])],"isStart":false}),makeQuery(id+"F363.opExtrude","SWEPT_FACE",FACE,{"disambiguationData":[OSD([sQuery(id+"F362.wireOp",EDGE,"E181.left")])]})]});
            var sketch = newSketch(context, id + "F364", { "sketchPlane" : qUnion([Q0])});
            skLineSegment(sketch, "E182.bottom", {"start": v(-45.64, 31.75) * mm, "end": v(-39.3, 31.75) * mm});
            skLineSegment(sketch, "E182.top", {"start": v(-45.64, 25.4) * mm, "end": v(-39.3, 25.4) * mm});
            skLineSegment(sketch, "E182.left", {"start": v(-45.64, 31.75) * mm, "end": v(-45.64, 25.4) * mm});
            skLineSegment(sketch, "E182.right", {"start": v(-39.3, 31.75) * mm, "end": v(-39.3, 25.4) * mm});
            skSolve(sketch);
        }
        {
            var Q0;
            Q0 = qSketchRegion(id + "F364", true);
            var Q1;
            Q1=makeQuery(id+"F364.imprint","IMPRINT",FACE,{"disambiguationData":[TD([[makeQuery(id+"F364.imprint","IMPRINT",EDGE,{"derivedFrom":sQuery(id+"F364.wireOp",EDGE,"E182.bottom")}),1.0]])]});
            extrude(context, id + "F365", {"entities" : qUnion([Q0, Q1]), "operationType" : NewBodyOperationType.ADD, "oppositeDirection" : true, "depth" : 19.05 * mm});
        }
        {
            var Q0;
            Q0=makeQuery(id+"F365.boolean.opBoolean","MERGE",FACE,{"derivedFrom":[makeQuery(id+"F363.boolean.opBoolean","MERGE",FACE,{"derivedFrom":[makeQuery(id+"F361.boolean.opBoolean","MERGE",FACE,{"derivedFrom":[makeQuery(id+"F359.opExtrude","CAP_FACE",FACE,{"disambiguationData":[OSD([sQuery(id+"F358.wireOp",EDGE,"E179.bottom"),sQuery(id+"F358.wireOp",EDGE,"E179.top"),sQuery(id+"F358.wireOp",EDGE,"E179.left"),sQuery(id+"F358.wireOp",EDGE,"E179.right")])],"isStart":false}),makeQuery(id+"F361.opExtrude","SWEPT_FACE",FACE,{"disambiguationData":[OSD([sQuery(id+"F360.wireOp",EDGE,"E180.bottom")])]})]}),makeQuery(id+"F363.opExtrude","SWEPT_FACE",FACE,{"disambiguationData":[OSD([sQuery(id+"F362.wireOp",EDGE,"E181.bottom")])]})]}),makeQuery(id+"F365.opExtrude","SWEPT_FACE",FACE,{"disambiguationData":[OSD([sQuery(id+"F364.wireOp",EDGE,"E182.top")])]})]});
            var sketch = newSketch(context, id + "F366", { "sketchPlane" : qUnion([Q0])});
            skLineSegment(sketch, "E183.bottom", {"start": v(-45.64, -24.41) * mm, "end": v(-39.3, -24.41) * mm});
            skLineSegment(sketch, "E183.top", {"start": v(-45.64, -18.06) * mm, "end": v(-39.3, -18.06) * mm});
            skLineSegment(sketch, "E183.left", {"start": v(-45.64, -24.41) * mm, "end": v(-45.64, -18.06) * mm});
            skLineSegment(sketch, "E183.right", {"start": v(-39.3, -24.41) * mm, "end": v(-39.3, -18.06) * mm});
            skSolve(sketch);
        }
        {
            var Q0;
            Q0 = qSketchRegion(id + "F366", true);
            var Q1;
            Q1=makeQuery(id+"F366.imprint","IMPRINT",FACE,{"disambiguationData":[TD([[makeQuery(id+"F366.imprint","IMPRINT",EDGE,{"derivedFrom":sQuery(id+"F366.wireOp",EDGE,"E183.bottom")}),1.0]])]});
            extrude(context, id + "F367", {"entities" : qUnion([Q0, Q1]), "operationType" : NewBodyOperationType.ADD, "oppositeDirection" : true, "depth" : 19.05 * mm});
        }
        {
            var Q0;
            Q0=makeQuery(id+"F367.boolean.opBoolean","MERGE",FACE,{"derivedFrom":[makeQuery(id+"F365.opExtrude","CAP_FACE",FACE,{"disambiguationData":[OSD([sQuery(id+"F364.wireOp",EDGE,"E182.bottom"),sQuery(id+"F364.wireOp",EDGE,"E182.top"),sQuery(id+"F364.wireOp",EDGE,"E182.left"),sQuery(id+"F364.wireOp",EDGE,"E182.right")])],"isStart":false}),makeQuery(id+"F367.opExtrude","SWEPT_FACE",FACE,{"disambiguationData":[OSD([sQuery(id+"F366.wireOp",EDGE,"E183.bottom")])]})]});
            var sketch = newSketch(context, id + "F368", { "sketchPlane" : qUnion([Q0])});
            skLineSegment(sketch, "E184.bottom", {"start": v(39.3, 44.45) * mm, "end": v(45.64, 44.45) * mm});
            skLineSegment(sketch, "E184.top", {"start": v(39.3, 38.1) * mm, "end": v(45.64, 38.1) * mm});
            skLineSegment(sketch, "E184.left", {"start": v(39.3, 44.45) * mm, "end": v(39.3, 38.1) * mm});
            skLineSegment(sketch, "E184.right", {"start": v(45.64, 44.45) * mm, "end": v(45.64, 38.1) * mm});
            skSolve(sketch);
        }
        {
            var Q0;
            Q0 = qSketchRegion(id + "F368", true);
            var Q1;
            Q1=makeQuery(id+"F368.imprint","IMPRINT",FACE,{"disambiguationData":[TD([[makeQuery(id+"F368.imprint","IMPRINT",EDGE,{"derivedFrom":sQuery(id+"F368.wireOp",EDGE,"E184.bottom")}),1.0]])]});
            extrude(context, id + "F369", {"entities" : qUnion([Q0, Q1]), "operationType" : NewBodyOperationType.ADD, "oppositeDirection" : true, "depth" : 19.05 * mm});
        }
        {
            var Q0;
            Q0=makeQuery(id+"F369.boolean.opBoolean","MERGE",FACE,{"derivedFrom":[makeQuery(id+"F367.boolean.opBoolean","MERGE",FACE,{"derivedFrom":[makeQuery(id+"F365.opExtrude","SWEPT_FACE",FACE,{"disambiguationData":[OSD([sQuery(id+"F364.wireOp",EDGE,"E182.right")])]}),makeQuery(id+"F367.opExtrude","SWEPT_FACE",FACE,{"disambiguationData":[OSD([sQuery(id+"F366.wireOp",EDGE,"E183.right")])]})]}),makeQuery(id+"F369.opExtrude","SWEPT_FACE",FACE,{"disambiguationData":[OSD([sQuery(id+"F368.wireOp",EDGE,"E184.left")])]})]});
            var sketch = newSketch(context, id + "F370", { "sketchPlane" : qUnion([Q0])});
            skLineSegment(sketch, "E185.bottom", {"start": v(5.36, 44.45) * mm, "end": v(11.71, 44.45) * mm});
            skLineSegment(sketch, "E185.top", {"start": v(5.36, 38.1) * mm, "end": v(11.71, 38.1) * mm});
            skLineSegment(sketch, "E185.left", {"start": v(5.36, 44.45) * mm, "end": v(5.36, 38.1) * mm});
            skLineSegment(sketch, "E185.right", {"start": v(11.71, 44.45) * mm, "end": v(11.71, 38.1) * mm});
            skSolve(sketch);
        }
        {
            var Q0;
            Q0=makeQuery(id+"F370.imprint","IMPRINT",FACE,{"disambiguationData":[TD([[makeQuery(id+"F370.imprint","IMPRINT",EDGE,{"derivedFrom":sQuery(id+"F370.wireOp",EDGE,"E185.bottom")}),1.0]])]});
            extrude(context, id + "F371", {"entities" : qUnion([Q0]), "operationType" : NewBodyOperationType.ADD, "oppositeDirection" : true, "depth" : 19.05 * mm});
        }
        {
            var Q0;
            Q0=makeQuery(id+"F371.boolean.opBoolean","MERGE",FACE,{"derivedFrom":[makeQuery(id+"F369.opExtrude","CAP_FACE",FACE,{"disambiguationData":[OSD([sQuery(id+"F368.wireOp",EDGE,"E184.bottom"),sQuery(id+"F368.wireOp",EDGE,"E184.top"),sQuery(id+"F368.wireOp",EDGE,"E184.left"),sQuery(id+"F368.wireOp",EDGE,"E184.right")])],"isStart":false}),makeQuery(id+"F371.opExtrude","SWEPT_FACE",FACE,{"disambiguationData":[OSD([sQuery(id+"F370.wireOp",EDGE,"E185.left")])]})]});
            var sketch = newSketch(context, id + "F372", { "sketchPlane" : qUnion([Q0])});
            skLineSegment(sketch, "E186.bottom", {"start": v(-58.34, 44.45) * mm, "end": v(-52, 44.45) * mm});
            skLineSegment(sketch, "E186.top", {"start": v(-58.34, 38.1) * mm, "end": v(-52, 38.1) * mm});
            skLineSegment(sketch, "E186.left", {"start": v(-58.34, 44.45) * mm, "end": v(-58.34, 38.1) * mm});
            skLineSegment(sketch, "E186.right", {"start": v(-52, 44.45) * mm, "end": v(-52, 38.1) * mm});
            skSolve(sketch);
        }
        {
            var Q0;
            Q0=makeQuery(id+"F372.imprint","IMPRINT",FACE,{"disambiguationData":[TD([[makeQuery(id+"F372.imprint","IMPRINT",EDGE,{"derivedFrom":sQuery(id+"F372.wireOp",EDGE,"E186.bottom")}),-1.0]])]});
            extrude(context, id + "F373", {"entities" : qUnion([Q0]), "operationType" : NewBodyOperationType.ADD, "oppositeDirection" : true, "depth" : 19.05 * mm});
        }
        {
            var Q0;
            Q0=makeQuery(id+"F373.opExtrude","SWEPT_FACE",FACE,{"disambiguationData":[OSD([sQuery(id+"F372.wireOp",EDGE,"E186.right")])]});
            var sketch = newSketch(context, id + "F374", { "sketchPlane" : qUnion([Q0])});
            skLineSegment(sketch, "E187.bottom", {"start": v(24.41, 44.45) * mm, "end": v(18.06, 44.45) * mm});
            skLineSegment(sketch, "E187.top", {"start": v(24.41, 38.1) * mm, "end": v(18.06, 38.1) * mm});
            skLineSegment(sketch, "E187.left", {"start": v(24.41, 44.45) * mm, "end": v(24.41, 38.1) * mm});
            skLineSegment(sketch, "E187.right", {"start": v(18.06, 44.45) * mm, "end": v(18.06, 38.1) * mm});
            skSolve(sketch);
        }
        {
            var Q0;
            Q0=makeQuery(id+"F374.imprint","IMPRINT",FACE,{"disambiguationData":[TD([[makeQuery(id+"F374.imprint","IMPRINT",EDGE,{"derivedFrom":sQuery(id+"F374.wireOp",EDGE,"E187.bottom")}),1.0]])]});
            extrude(context, id + "F375", {"entities" : qUnion([Q0]), "operationType" : NewBodyOperationType.ADD, "oppositeDirection" : true, "depth" : 19.05 * mm});
        }
        {
            var Q0;
            Q0=makeQuery(id+"F375.boolean.opBoolean","MERGE",FACE,{"derivedFrom":[makeQuery(id+"F373.opExtrude","CAP_FACE",FACE,{"disambiguationData":[OSD([sQuery(id+"F372.wireOp",EDGE,"E186.bottom"),sQuery(id+"F372.wireOp",EDGE,"E186.top"),sQuery(id+"F372.wireOp",EDGE,"E186.left"),sQuery(id+"F372.wireOp",EDGE,"E186.right")])],"isStart":false}),makeQuery(id+"F375.opExtrude","SWEPT_FACE",FACE,{"disambiguationData":[OSD([sQuery(id+"F374.wireOp",EDGE,"E187.left")])]})]});
            var sketch = newSketch(context, id + "F376", { "sketchPlane" : qUnion([Q0])});
            skLineSegment(sketch, "E188.bottom", {"start": v(71.04, 38.1) * mm, "end": v(64.7, 38.1) * mm});
            skLineSegment(sketch, "E188.top", {"start": v(71.04, 44.45) * mm, "end": v(64.7, 44.45) * mm});
            skLineSegment(sketch, "E188.left", {"start": v(71.04, 38.1) * mm, "end": v(71.04, 44.45) * mm});
            skLineSegment(sketch, "E188.right", {"start": v(64.7, 38.1) * mm, "end": v(64.7, 44.45) * mm});
            skSolve(sketch);
        }
        {
            var Q0;
            Q0=makeQuery(id+"F376.imprint","IMPRINT",FACE,{"disambiguationData":[TD([[makeQuery(id+"F376.imprint","IMPRINT",EDGE,{"derivedFrom":sQuery(id+"F376.wireOp",EDGE,"E188.bottom")}),1.0]])]});
            extrude(context, id + "F377", {"entities" : qUnion([Q0]), "operationType" : NewBodyOperationType.ADD, "oppositeDirection" : true, "depth" : 19.05 * mm});
        }
        {
            var Q0;
            Q0=makeQuery(id+"F377.boolean.opBoolean","MERGE",FACE,{"derivedFrom":[makeQuery(id+"F375.boolean.opBoolean","MERGE",FACE,{"derivedFrom":[makeQuery(id+"F373.boolean.opBoolean","MERGE",FACE,{"derivedFrom":[makeQuery(id+"F371.boolean.opBoolean","MERGE",FACE,{"derivedFrom":[makeQuery(id+"F369.boolean.opBoolean","MERGE",FACE,{"derivedFrom":[makeQuery(id+"F367.opExtrude","CAP_FACE",FACE,{"disambiguationData":[OSD([sQuery(id+"F366.wireOp",EDGE,"E183.bottom"),sQuery(id+"F366.wireOp",EDGE,"E183.top"),sQuery(id+"F366.wireOp",EDGE,"E183.left"),sQuery(id+"F366.wireOp",EDGE,"E183.right")])],"isStart":false}),makeQuery(id+"F369.opExtrude","SWEPT_FACE",FACE,{"disambiguationData":[OSD([sQuery(id+"F368.wireOp",EDGE,"E184.bottom")])]})]}),makeQuery(id+"F371.opExtrude","SWEPT_FACE",FACE,{"disambiguationData":[OSD([sQuery(id+"F370.wireOp",EDGE,"E185.bottom")])]})]}),makeQuery(id+"F373.opExtrude","SWEPT_FACE",FACE,{"disambiguationData":[OSD([sQuery(id+"F372.wireOp",EDGE,"E186.bottom")])]})]}),makeQuery(id+"F375.opExtrude","SWEPT_FACE",FACE,{"disambiguationData":[OSD([sQuery(id+"F374.wireOp",EDGE,"E187.bottom")])]})]}),makeQuery(id+"F377.opExtrude","SWEPT_FACE",FACE,{"disambiguationData":[OSD([sQuery(id+"F376.wireOp",EDGE,"E188.top")])]})]});
            var sketch = newSketch(context, id + "F378", { "sketchPlane" : qUnion([Q0])});
            skLineSegment(sketch, "E189.bottom", {"start": v(-71.04, 5.36) * mm, "end": v(-64.7, 5.36) * mm});
            skLineSegment(sketch, "E189.top", {"start": v(-71.04, 11.71) * mm, "end": v(-64.7, 11.71) * mm});
            skLineSegment(sketch, "E189.left", {"start": v(-71.04, 5.36) * mm, "end": v(-71.04, 11.71) * mm});
            skLineSegment(sketch, "E189.right", {"start": v(-64.7, 5.36) * mm, "end": v(-64.7, 11.71) * mm});
            skSolve(sketch);
        }
        {
            var Q0;
            Q0=makeQuery(id+"F378.imprint","IMPRINT",FACE,{"disambiguationData":[TD([[makeQuery(id+"F378.imprint","IMPRINT",EDGE,{"derivedFrom":sQuery(id+"F378.wireOp",EDGE,"E189.bottom")}),1.0]])]});
            extrude(context, id + "F379", {"entities" : qUnion([Q0]), "operationType" : NewBodyOperationType.ADD, "oppositeDirection" : true, "depth" : 19.05 * mm});
        }
        {
            var Q0;
            Q0=makeQuery(id+"F379.boolean.opBoolean","MERGE",FACE,{"derivedFrom":[makeQuery(id+"F377.opExtrude","CAP_FACE",FACE,{"disambiguationData":[OSD([sQuery(id+"F376.wireOp",EDGE,"E188.bottom"),sQuery(id+"F376.wireOp",EDGE,"E188.top"),sQuery(id+"F376.wireOp",EDGE,"E188.left"),sQuery(id+"F376.wireOp",EDGE,"E188.right")])],"isStart":false}),makeQuery(id+"F379.opExtrude","SWEPT_FACE",FACE,{"disambiguationData":[OSD([sQuery(id+"F378.wireOp",EDGE,"E189.bottom")])]})]});
            var sketch = newSketch(context, id + "F380", { "sketchPlane" : qUnion([Q0])});
            skLineSegment(sketch, "E190.bottom", {"start": v(-71.04, 25.4) * mm, "end": v(-64.7, 25.4) * mm});
            skLineSegment(sketch, "E190.top", {"start": v(-71.04, 31.75) * mm, "end": v(-64.7, 31.75) * mm});
            skLineSegment(sketch, "E190.left", {"start": v(-71.04, 25.4) * mm, "end": v(-71.04, 31.75) * mm});
            skLineSegment(sketch, "E190.right", {"start": v(-64.7, 25.4) * mm, "end": v(-64.7, 31.75) * mm});
            skSolve(sketch);
        }
        {
            var Q0;
            Q0=makeQuery(id+"F380.imprint","IMPRINT",FACE,{"disambiguationData":[TD([[makeQuery(id+"F380.imprint","IMPRINT",EDGE,{"derivedFrom":sQuery(id+"F380.wireOp",EDGE,"E190.bottom")}),1.0]])]});
            extrude(context, id + "F381", {"entities" : qUnion([Q0]), "operationType" : NewBodyOperationType.ADD, "oppositeDirection" : true, "depth" : 19.05 * mm});
        }
        {
            var Q0;
            Q0=makeQuery(id+"F381.boolean.opBoolean","MERGE",FACE,{"derivedFrom":[makeQuery(id+"F379.boolean.opBoolean","MERGE",FACE,{"derivedFrom":[makeQuery(id+"F377.boolean.opBoolean","MERGE",FACE,{"derivedFrom":[makeQuery(id+"F375.opExtrude","CAP_FACE",FACE,{"disambiguationData":[OSD([sQuery(id+"F374.wireOp",EDGE,"E187.bottom"),sQuery(id+"F374.wireOp",EDGE,"E187.top"),sQuery(id+"F374.wireOp",EDGE,"E187.left"),sQuery(id+"F374.wireOp",EDGE,"E187.right")])],"isStart":false}),makeQuery(id+"F377.opExtrude","SWEPT_FACE",FACE,{"disambiguationData":[OSD([sQuery(id+"F376.wireOp",EDGE,"E188.left")])]})]}),makeQuery(id+"F379.opExtrude","SWEPT_FACE",FACE,{"disambiguationData":[OSD([sQuery(id+"F378.wireOp",EDGE,"E189.left")])]})]}),makeQuery(id+"F381.opExtrude","SWEPT_FACE",FACE,{"disambiguationData":[OSD([sQuery(id+"F380.wireOp",EDGE,"E190.left")])]})]});
            var sketch = newSketch(context, id + "F382", { "sketchPlane" : qUnion([Q0])});
            skLineSegment(sketch, "E191.bottom", {"start": v(-24.41, 25.4) * mm, "end": v(-18.06, 25.4) * mm});
            skLineSegment(sketch, "E191.top", {"start": v(-24.41, 31.75) * mm, "end": v(-18.06, 31.75) * mm});
            skLineSegment(sketch, "E191.left", {"start": v(-24.41, 25.4) * mm, "end": v(-24.41, 31.75) * mm});
            skLineSegment(sketch, "E191.right", {"start": v(-18.06, 25.4) * mm, "end": v(-18.06, 31.75) * mm});
            skSolve(sketch);
        }
        {
            var Q0;
            Q0=makeQuery(id+"F382.imprint","IMPRINT",FACE,{"disambiguationData":[TD([[makeQuery(id+"F382.imprint","IMPRINT",EDGE,{"derivedFrom":sQuery(id+"F382.wireOp",EDGE,"E191.bottom")}),1.0]])]});
            extrude(context, id + "F383", {"entities" : qUnion([Q0]), "operationType" : NewBodyOperationType.ADD, "oppositeDirection" : true, "depth" : 19.05 * mm});
        }
        {
            var Q0;
            Q0=makeQuery(id+"F383.boolean.opBoolean","MERGE",FACE,{"derivedFrom":[makeQuery(id+"F381.opExtrude","CAP_FACE",FACE,{"disambiguationData":[OSD([sQuery(id+"F380.wireOp",EDGE,"E190.bottom"),sQuery(id+"F380.wireOp",EDGE,"E190.top"),sQuery(id+"F380.wireOp",EDGE,"E190.left"),sQuery(id+"F380.wireOp",EDGE,"E190.right")])],"isStart":false}),makeQuery(id+"F383.opExtrude","SWEPT_FACE",FACE,{"disambiguationData":[OSD([sQuery(id+"F382.wireOp",EDGE,"E191.left")])]})]});
            var sketch = newSketch(context, id + "F384", { "sketchPlane" : qUnion([Q0])});
            skLineSegment(sketch, "E192.bottom", {"start": v(52, 25.4) * mm, "end": v(58.34, 25.4) * mm});
            skLineSegment(sketch, "E192.top", {"start": v(52, 31.75) * mm, "end": v(58.34, 31.75) * mm});
            skLineSegment(sketch, "E192.left", {"start": v(52, 25.4) * mm, "end": v(52, 31.75) * mm});
            skLineSegment(sketch, "E192.right", {"start": v(58.34, 25.4) * mm, "end": v(58.34, 31.75) * mm});
            skSolve(sketch);
        }
        {
            var Q0;
            Q0=makeQuery(id+"F384.imprint","IMPRINT",FACE,{"disambiguationData":[TD([[makeQuery(id+"F384.imprint","IMPRINT",EDGE,{"derivedFrom":sQuery(id+"F384.wireOp",EDGE,"E192.bottom")}),-1.0]])]});
            extrude(context, id + "F385", {"entities" : qUnion([Q0]), "operationType" : NewBodyOperationType.ADD, "oppositeDirection" : true, "depth" : 31.75 * mm});
        }
        {
            var Q0;
            Q0=makeQuery(id+"F385.boolean.opBoolean","MERGE",FACE,{"derivedFrom":[makeQuery(id+"F383.boolean.opBoolean","MERGE",FACE,{"derivedFrom":[makeQuery(id+"F381.boolean.opBoolean","MERGE",FACE,{"derivedFrom":[makeQuery(id+"F379.opExtrude","CAP_FACE",FACE,{"disambiguationData":[OSD([sQuery(id+"F378.wireOp",EDGE,"E189.bottom"),sQuery(id+"F378.wireOp",EDGE,"E189.top"),sQuery(id+"F378.wireOp",EDGE,"E189.left"),sQuery(id+"F378.wireOp",EDGE,"E189.right")])],"isStart":false}),makeQuery(id+"F381.opExtrude","SWEPT_FACE",FACE,{"disambiguationData":[OSD([sQuery(id+"F380.wireOp",EDGE,"E190.bottom")])]})]}),makeQuery(id+"F383.opExtrude","SWEPT_FACE",FACE,{"disambiguationData":[OSD([sQuery(id+"F382.wireOp",EDGE,"E191.bottom")])]})]}),makeQuery(id+"F385.opExtrude","SWEPT_FACE",FACE,{"disambiguationData":[OSD([sQuery(id+"F384.wireOp",EDGE,"E192.bottom")])]})]});
            var sketch = newSketch(context, id + "F386", { "sketchPlane" : qUnion([Q0])});
            skLineSegment(sketch, "E193.bottom", {"start": v(-52, 7.34) * mm, "end": v(-58.34, 7.34) * mm});
            skLineSegment(sketch, "E193.top", {"start": v(-52, 0.99) * mm, "end": v(-58.34, 0.99) * mm});
            skLineSegment(sketch, "E193.left", {"start": v(-52, 7.34) * mm, "end": v(-52, 0.99) * mm});
            skLineSegment(sketch, "E193.right", {"start": v(-58.34, 7.34) * mm, "end": v(-58.34, 0.99) * mm});
            skSolve(sketch);
        }
        {
            var Q0;
            Q0=makeQuery(id+"F386.imprint","IMPRINT",FACE,{"disambiguationData":[TD([[makeQuery(id+"F386.imprint","IMPRINT",EDGE,{"derivedFrom":sQuery(id+"F386.wireOp",EDGE,"E193.bottom")}),-1.0]])]});
            extrude(context, id + "F387", {"entities" : qUnion([Q0]), "operationType" : NewBodyOperationType.ADD, "oppositeDirection" : true, "depth" : 19.05 * mm});
        }
        {
            var Q0;
            Q0=makeQuery(id+"F387.boolean.opBoolean","MERGE",FACE,{"derivedFrom":[makeQuery(id+"F385.boolean.opBoolean","MERGE",FACE,{"derivedFrom":[makeQuery(id+"F383.opExtrude","CAP_FACE",FACE,{"disambiguationData":[OSD([sQuery(id+"F382.wireOp",EDGE,"E191.bottom"),sQuery(id+"F382.wireOp",EDGE,"E191.top"),sQuery(id+"F382.wireOp",EDGE,"E191.left"),sQuery(id+"F382.wireOp",EDGE,"E191.right")])],"isStart":false}),makeQuery(id+"F385.opExtrude","SWEPT_FACE",FACE,{"disambiguationData":[OSD([sQuery(id+"F384.wireOp",EDGE,"E192.left")])]})]}),makeQuery(id+"F387.opExtrude","SWEPT_FACE",FACE,{"disambiguationData":[OSD([sQuery(id+"F386.wireOp",EDGE,"E193.left")])]})]});
            var sketch = newSketch(context, id + "F388", { "sketchPlane" : qUnion([Q0])});
            skLineSegment(sketch, "E194.bottom", {"start": v(-7.34, 44.45) * mm, "end": v(-0.99, 44.45) * mm});
            skLineSegment(sketch, "E194.top", {"start": v(-7.34, 38.1) * mm, "end": v(-0.99, 38.1) * mm});
            skLineSegment(sketch, "E194.left", {"start": v(-7.34, 44.45) * mm, "end": v(-7.34, 38.1) * mm});
            skLineSegment(sketch, "E194.right", {"start": v(-0.99, 44.45) * mm, "end": v(-0.99, 38.1) * mm});
            skSolve(sketch);
        }
        {
            var Q0;
            Q0=makeQuery(id+"F388.imprint","IMPRINT",FACE,{"disambiguationData":[TD([[makeQuery(id+"F388.imprint","IMPRINT",EDGE,{"derivedFrom":sQuery(id+"F388.wireOp",EDGE,"E194.bottom")}),1.0]])]});
            extrude(context, id + "F389", {"entities" : qUnion([Q0]), "operationType" : NewBodyOperationType.ADD, "oppositeDirection" : true, "depth" : 19.05 * mm});
        }
        {
            var Q0;
            Q0=makeQuery(id+"F389.boolean.opBoolean","MERGE",FACE,{"derivedFrom":[makeQuery(id+"F387.opExtrude","CAP_FACE",FACE,{"disambiguationData":[OSD([sQuery(id+"F386.wireOp",EDGE,"E193.bottom"),sQuery(id+"F386.wireOp",EDGE,"E193.top"),sQuery(id+"F386.wireOp",EDGE,"E193.left"),sQuery(id+"F386.wireOp",EDGE,"E193.right")])],"isStart":false}),makeQuery(id+"F389.opExtrude","SWEPT_FACE",FACE,{"disambiguationData":[OSD([sQuery(id+"F388.wireOp",EDGE,"E194.bottom")])]})]});
            var sketch = newSketch(context, id + "F390", { "sketchPlane" : qUnion([Q0])});
            skLineSegment(sketch, "E195.bottom", {"start": v(-71.04, -7.34) * mm, "end": v(-64.7, -7.34) * mm});
            skLineSegment(sketch, "E195.top", {"start": v(-71.04, -0.99) * mm, "end": v(-64.7, -0.99) * mm});
            skLineSegment(sketch, "E195.left", {"start": v(-71.04, -7.34) * mm, "end": v(-71.04, -0.99) * mm});
            skLineSegment(sketch, "E195.right", {"start": v(-64.7, -7.34) * mm, "end": v(-64.7, -0.99) * mm});
            skSolve(sketch);
        }
        {
            var Q0;
            Q0=makeQuery(id+"F390.imprint","IMPRINT",FACE,{"disambiguationData":[TD([[makeQuery(id+"F390.imprint","IMPRINT",EDGE,{"derivedFrom":sQuery(id+"F390.wireOp",EDGE,"E195.bottom")}),1.0]])]});
            extrude(context, id + "F391", {"entities" : qUnion([Q0]), "operationType" : NewBodyOperationType.ADD, "oppositeDirection" : true, "depth" : 19.05 * mm});
        }
        {
            var Q0;
            Q0=makeQuery(id+"F391.boolean.opBoolean","MERGE",FACE,{"derivedFrom":[makeQuery(id+"F389.boolean.opBoolean","MERGE",FACE,{"derivedFrom":[makeQuery(id+"F387.opExtrude","SWEPT_FACE",FACE,{"disambiguationData":[OSD([sQuery(id+"F386.wireOp",EDGE,"E193.top")])]}),makeQuery(id+"F389.opExtrude","SWEPT_FACE",FACE,{"disambiguationData":[OSD([sQuery(id+"F388.wireOp",EDGE,"E194.right")])]})]}),makeQuery(id+"F391.opExtrude","SWEPT_FACE",FACE,{"disambiguationData":[OSD([sQuery(id+"F390.wireOp",EDGE,"E195.top")])]})]});
            var sketch = newSketch(context, id + "F392", { "sketchPlane" : qUnion([Q0])});
            skLineSegment(sketch, "E196.bottom", {"start": v(71.04, 25.4) * mm, "end": v(64.7, 25.4) * mm});
            skLineSegment(sketch, "E196.top", {"start": v(71.04, 31.75) * mm, "end": v(64.7, 31.75) * mm});
            skLineSegment(sketch, "E196.left", {"start": v(71.04, 25.4) * mm, "end": v(71.04, 31.75) * mm});
            skLineSegment(sketch, "E196.right", {"start": v(64.7, 25.4) * mm, "end": v(64.7, 31.75) * mm});
            skSolve(sketch);
        }
        {
            var Q0;
            Q0=makeQuery(id+"F392.imprint","IMPRINT",FACE,{"disambiguationData":[TD([[makeQuery(id+"F392.imprint","IMPRINT",EDGE,{"derivedFrom":sQuery(id+"F392.wireOp",EDGE,"E196.bottom")}),1.0]])]});
            extrude(context, id + "F393", {"entities" : qUnion([Q0]), "operationType" : NewBodyOperationType.ADD, "oppositeDirection" : true, "depth" : 19.05 * mm});
        }
        {
            var Q0;
            Q0=makeQuery(id+"F393.boolean.opBoolean","MERGE",FACE,{"derivedFrom":[makeQuery(id+"F391.opExtrude","CAP_FACE",FACE,{"disambiguationData":[OSD([sQuery(id+"F390.wireOp",EDGE,"E195.bottom"),sQuery(id+"F390.wireOp",EDGE,"E195.top"),sQuery(id+"F390.wireOp",EDGE,"E195.left"),sQuery(id+"F390.wireOp",EDGE,"E195.right")])],"isStart":false}),makeQuery(id+"F393.opExtrude","SWEPT_FACE",FACE,{"disambiguationData":[OSD([sQuery(id+"F392.wireOp",EDGE,"E196.bottom")])]})]});
            var sketch = newSketch(context, id + "F394", { "sketchPlane" : qUnion([Q0])});
            skLineSegment(sketch, "E197.bottom", {"start": v(-71.04, 20.04) * mm, "end": v(-64.7, 20.04) * mm});
            skLineSegment(sketch, "E197.top", {"start": v(-71.04, 13.69) * mm, "end": v(-64.7, 13.69) * mm});
            skLineSegment(sketch, "E197.left", {"start": v(-71.04, 20.04) * mm, "end": v(-71.04, 13.69) * mm});
            skLineSegment(sketch, "E197.right", {"start": v(-64.7, 20.04) * mm, "end": v(-64.7, 13.69) * mm});
            skSolve(sketch);
        }
        {
            var Q0;
            Q0=makeQuery(id+"F394.imprint","IMPRINT",FACE,{"disambiguationData":[TD([[makeQuery(id+"F394.imprint","IMPRINT",EDGE,{"derivedFrom":sQuery(id+"F394.wireOp",EDGE,"E197.bottom")}),1.0]])]});
            extrude(context, id + "F395", {"entities" : qUnion([Q0]), "operationType" : NewBodyOperationType.ADD, "oppositeDirection" : true, "depth" : 19.05 * mm});
        }
        {
            var Q0;
            Q0=makeQuery(id+"F395.boolean.opBoolean","MERGE",FACE,{"derivedFrom":[makeQuery(id+"F393.boolean.opBoolean","MERGE",FACE,{"derivedFrom":[makeQuery(id+"F391.boolean.opBoolean","MERGE",FACE,{"derivedFrom":[makeQuery(id+"F389.opExtrude","CAP_FACE",FACE,{"disambiguationData":[OSD([sQuery(id+"F388.wireOp",EDGE,"E194.bottom"),sQuery(id+"F388.wireOp",EDGE,"E194.top"),sQuery(id+"F388.wireOp",EDGE,"E194.left"),sQuery(id+"F388.wireOp",EDGE,"E194.right")])],"isStart":false}),makeQuery(id+"F391.opExtrude","SWEPT_FACE",FACE,{"disambiguationData":[OSD([sQuery(id+"F390.wireOp",EDGE,"E195.left")])]})]}),makeQuery(id+"F393.opExtrude","SWEPT_FACE",FACE,{"disambiguationData":[OSD([sQuery(id+"F392.wireOp",EDGE,"E196.left")])]})]}),makeQuery(id+"F395.opExtrude","SWEPT_FACE",FACE,{"disambiguationData":[OSD([sQuery(id+"F394.wireOp",EDGE,"E197.left")])]})]});
            var sketch = newSketch(context, id + "F396", { "sketchPlane" : qUnion([Q0])});
            skLineSegment(sketch, "E198.bottom", {"start": v(20.04, 44.45) * mm, "end": v(13.69, 44.45) * mm});
            skLineSegment(sketch, "E198.top", {"start": v(20.04, 38.1) * mm, "end": v(13.69, 38.1) * mm});
            skLineSegment(sketch, "E198.left", {"start": v(20.04, 44.45) * mm, "end": v(20.04, 38.1) * mm});
            skLineSegment(sketch, "E198.right", {"start": v(13.69, 44.45) * mm, "end": v(13.69, 38.1) * mm});
            skSolve(sketch);
        }
        {
            var Q0;
            Q0=makeQuery(id+"F396.imprint","IMPRINT",FACE,{"disambiguationData":[TD([[makeQuery(id+"F396.imprint","IMPRINT",EDGE,{"derivedFrom":sQuery(id+"F396.wireOp",EDGE,"E198.bottom")}),-1.0]])]});
            extrude(context, id + "F397", {"entities" : qUnion([Q0]), "operationType" : NewBodyOperationType.ADD, "oppositeDirection" : true, "depth" : 19.05 * mm});
        }
        {
            var Q0;
            Q0=makeQuery(id+"F397.boolean.opBoolean","MERGE",FACE,{"derivedFrom":[makeQuery(id+"F395.opExtrude","CAP_FACE",FACE,{"disambiguationData":[OSD([sQuery(id+"F394.wireOp",EDGE,"E197.bottom"),sQuery(id+"F394.wireOp",EDGE,"E197.top"),sQuery(id+"F394.wireOp",EDGE,"E197.left"),sQuery(id+"F394.wireOp",EDGE,"E197.right")])],"isStart":false}),makeQuery(id+"F397.opExtrude","SWEPT_FACE",FACE,{"disambiguationData":[OSD([sQuery(id+"F396.wireOp",EDGE,"E198.bottom")])]})]});
            var sketch = newSketch(context, id + "F398", { "sketchPlane" : qUnion([Q0])});
            skLineSegment(sketch, "E199.bottom", {"start": v(-52, -13.69) * mm, "end": v(-58.34, -13.69) * mm});
            skLineSegment(sketch, "E199.top", {"start": v(-52, -20.04) * mm, "end": v(-58.34, -20.04) * mm});
            skLineSegment(sketch, "E199.left", {"start": v(-52, -13.69) * mm, "end": v(-52, -20.04) * mm});
            skLineSegment(sketch, "E199.right", {"start": v(-58.34, -13.69) * mm, "end": v(-58.34, -20.04) * mm});
            skSolve(sketch);
        }
        {
            var Q0;
            Q0=makeQuery(id+"F398.imprint","IMPRINT",FACE,{"disambiguationData":[TD([[makeQuery(id+"F398.imprint","IMPRINT",EDGE,{"derivedFrom":sQuery(id+"F398.wireOp",EDGE,"E199.bottom")}),-1.0]])]});
            extrude(context, id + "F399", {"entities" : qUnion([Q0]), "operationType" : NewBodyOperationType.ADD, "oppositeDirection" : true, "depth" : 44.45 * mm});
        }
        {
            var Q0;
            Q0=makeQuery(id+"F399.boolean.opBoolean","MERGE",FACE,{"derivedFrom":[makeQuery(id+"F397.opExtrude","CAP_FACE",FACE,{"disambiguationData":[OSD([sQuery(id+"F396.wireOp",EDGE,"E198.bottom"),sQuery(id+"F396.wireOp",EDGE,"E198.top"),sQuery(id+"F396.wireOp",EDGE,"E198.left"),sQuery(id+"F396.wireOp",EDGE,"E198.right")])],"isStart":false}),makeQuery(id+"F399.opExtrude","SWEPT_FACE",FACE,{"disambiguationData":[OSD([sQuery(id+"F398.wireOp",EDGE,"E199.left")])]})]});
            var sketch = newSketch(context, id + "F400", { "sketchPlane" : qUnion([Q0])});
            skLineSegment(sketch, "E200.bottom", {"start": v(-20.04, 0) * mm, "end": v(-13.69, 0) * mm});
            skLineSegment(sketch, "E200.top", {"start": v(-20.04, 6.35) * mm, "end": v(-13.69, 6.35) * mm});
            skLineSegment(sketch, "E200.left", {"start": v(-20.04, 0) * mm, "end": v(-20.04, 6.35) * mm});
            skLineSegment(sketch, "E200.right", {"start": v(-13.69, 0) * mm, "end": v(-13.69, 6.35) * mm});
            skSolve(sketch);
        }
        {
            var Q0;
            Q0=makeQuery(id+"F400.imprint","IMPRINT",FACE,{"disambiguationData":[TD([[makeQuery(id+"F400.imprint","IMPRINT",EDGE,{"derivedFrom":sQuery(id+"F400.wireOp",EDGE,"E200.bottom")}),-1.0]])]});
            extrude(context, id + "F401", {"entities" : qUnion([Q0]), "operationType" : NewBodyOperationType.ADD, "oppositeDirection" : true, "depth" : 19.05 * mm});
        }
        {
            var Q0;
            Q0=makeQuery(id+"F401.boolean.opBoolean","MERGE",FACE,{"derivedFrom":[makeQuery(id+"F399.opExtrude","CAP_FACE",FACE,{"disambiguationData":[OSD([sQuery(id+"F398.wireOp",EDGE,"E199.bottom"),sQuery(id+"F398.wireOp",EDGE,"E199.top"),sQuery(id+"F398.wireOp",EDGE,"E199.left"),sQuery(id+"F398.wireOp",EDGE,"E199.right")])],"isStart":false}),makeQuery(id+"F401.opExtrude","SWEPT_FACE",FACE,{"disambiguationData":[OSD([sQuery(id+"F400.wireOp",EDGE,"E200.bottom")])]})]});
            var sketch = newSketch(context, id + "F402", { "sketchPlane" : qUnion([Q0])});
            skLineSegment(sketch, "E201.bottom", {"start": v(-71.04, 13.69) * mm, "end": v(-64.7, 13.69) * mm});
            skLineSegment(sketch, "E201.top", {"start": v(-71.04, 20.04) * mm, "end": v(-64.7, 20.04) * mm});
            skLineSegment(sketch, "E201.left", {"start": v(-71.04, 13.69) * mm, "end": v(-71.04, 20.04) * mm});
            skLineSegment(sketch, "E201.right", {"start": v(-64.7, 13.69) * mm, "end": v(-64.7, 20.04) * mm});
            skSolve(sketch);
        }
        {
            var Q0;
            Q0=makeQuery(id+"F402.imprint","IMPRINT",FACE,{"disambiguationData":[TD([[makeQuery(id+"F402.imprint","IMPRINT",EDGE,{"derivedFrom":sQuery(id+"F402.wireOp",EDGE,"E201.bottom")}),1.0]])]});
            extrude(context, id + "F403", {"entities" : qUnion([Q0]), "operationType" : NewBodyOperationType.ADD, "oppositeDirection" : true, "depth" : 19.05 * mm});
        }
        {
            var Q0;
            Q0=makeQuery(id+"F403.boolean.opBoolean","MERGE",FACE,{"derivedFrom":[makeQuery(id+"F401.boolean.opBoolean","MERGE",FACE,{"derivedFrom":[makeQuery(id+"F399.boolean.opBoolean","MERGE",FACE,{"derivedFrom":[makeQuery(id+"F397.boolean.opBoolean","MERGE",FACE,{"derivedFrom":[makeQuery(id+"F395.boolean.opBoolean","MERGE",FACE,{"derivedFrom":[makeQuery(id+"F393.opExtrude","CAP_FACE",FACE,{"disambiguationData":[OSD([sQuery(id+"F392.wireOp",EDGE,"E196.bottom"),sQuery(id+"F392.wireOp",EDGE,"E196.top"),sQuery(id+"F392.wireOp",EDGE,"E196.left"),sQuery(id+"F392.wireOp",EDGE,"E196.right")])],"isStart":false}),makeQuery(id+"F395.opExtrude","SWEPT_FACE",FACE,{"disambiguationData":[OSD([sQuery(id+"F394.wireOp",EDGE,"E197.bottom")])]})]}),makeQuery(id+"F397.opExtrude","SWEPT_FACE",FACE,{"disambiguationData":[OSD([sQuery(id+"F396.wireOp",EDGE,"E198.left")])]})]}),makeQuery(id+"F399.opExtrude","SWEPT_FACE",FACE,{"disambiguationData":[OSD([sQuery(id+"F398.wireOp",EDGE,"E199.top")])]})]}),makeQuery(id+"F401.opExtrude","SWEPT_FACE",FACE,{"disambiguationData":[OSD([sQuery(id+"F400.wireOp",EDGE,"E200.left")])]})]}),makeQuery(id+"F403.opExtrude","SWEPT_FACE",FACE,{"disambiguationData":[OSD([sQuery(id+"F402.wireOp",EDGE,"E201.top")])]})]});
            var sketch = newSketch(context, id + "F404", { "sketchPlane" : qUnion([Q0])});
            skLineSegment(sketch, "E202.bottom", {"start": v(-71.04, 19.05) * mm, "end": v(-64.7, 19.05) * mm});
            skLineSegment(sketch, "E202.top", {"start": v(-71.04, 12.7) * mm, "end": v(-64.7, 12.7) * mm});
            skLineSegment(sketch, "E202.left", {"start": v(-71.04, 19.05) * mm, "end": v(-71.04, 12.7) * mm});
            skLineSegment(sketch, "E202.right", {"start": v(-64.7, 19.05) * mm, "end": v(-64.7, 12.7) * mm});
            skSolve(sketch);
        }
        {
            var Q0;
            Q0=makeQuery(id+"F404.imprint","IMPRINT",FACE,{"disambiguationData":[TD([[makeQuery(id+"F404.imprint","IMPRINT",EDGE,{"derivedFrom":sQuery(id+"F404.wireOp",EDGE,"E202.bottom")}),1.0]])]});
            extrude(context, id + "F405", {"entities" : qUnion([Q0]), "operationType" : NewBodyOperationType.ADD, "oppositeDirection" : true, "depth" : 19.05 * mm});
        }
        {
            var Q0;
            Q0=makeQuery(id+"F405.boolean.opBoolean","MERGE",FACE,{"derivedFrom":[makeQuery(id+"F403.opExtrude","CAP_FACE",FACE,{"disambiguationData":[OSD([sQuery(id+"F402.wireOp",EDGE,"E201.bottom"),sQuery(id+"F402.wireOp",EDGE,"E201.top"),sQuery(id+"F402.wireOp",EDGE,"E201.left"),sQuery(id+"F402.wireOp",EDGE,"E201.right")])],"isStart":false}),makeQuery(id+"F405.opExtrude","SWEPT_FACE",FACE,{"disambiguationData":[OSD([sQuery(id+"F404.wireOp",EDGE,"E202.bottom")])]})]});
            var sketch = newSketch(context, id + "F406", { "sketchPlane" : qUnion([Q0])});
            skLineSegment(sketch, "E203.bottom", {"start": v(-71.04, -0.99) * mm, "end": v(-64.7, -0.99) * mm});
            skLineSegment(sketch, "E203.top", {"start": v(-71.04, -7.34) * mm, "end": v(-64.7, -7.34) * mm});
            skLineSegment(sketch, "E203.left", {"start": v(-71.04, -0.99) * mm, "end": v(-71.04, -7.34) * mm});
            skLineSegment(sketch, "E203.right", {"start": v(-64.7, -0.99) * mm, "end": v(-64.7, -7.34) * mm});
            skSolve(sketch);
        }
        {
            var Q0;
            Q0=makeQuery(id+"F406.imprint","IMPRINT",FACE,{"disambiguationData":[TD([[makeQuery(id+"F406.imprint","IMPRINT",EDGE,{"derivedFrom":sQuery(id+"F406.wireOp",EDGE,"E203.bottom")}),1.0]])]});
            extrude(context, id + "F407", {"entities" : qUnion([Q0]), "operationType" : NewBodyOperationType.ADD, "oppositeDirection" : true, "depth" : 19.05 * mm});
        }
        {
            var Q0;
            Q0=makeQuery(id+"F407.boolean.opBoolean","MERGE",FACE,{"derivedFrom":[makeQuery(id+"F405.boolean.opBoolean","MERGE",FACE,{"derivedFrom":[makeQuery(id+"F403.boolean.opBoolean","MERGE",FACE,{"derivedFrom":[makeQuery(id+"F401.opExtrude","CAP_FACE",FACE,{"disambiguationData":[OSD([sQuery(id+"F400.wireOp",EDGE,"E200.bottom"),sQuery(id+"F400.wireOp",EDGE,"E200.top"),sQuery(id+"F400.wireOp",EDGE,"E200.left"),sQuery(id+"F400.wireOp",EDGE,"E200.right")])],"isStart":false}),makeQuery(id+"F403.opExtrude","SWEPT_FACE",FACE,{"disambiguationData":[OSD([sQuery(id+"F402.wireOp",EDGE,"E201.left")])]})]}),makeQuery(id+"F405.opExtrude","SWEPT_FACE",FACE,{"disambiguationData":[OSD([sQuery(id+"F404.wireOp",EDGE,"E202.left")])]})]}),makeQuery(id+"F407.opExtrude","SWEPT_FACE",FACE,{"disambiguationData":[OSD([sQuery(id+"F406.wireOp",EDGE,"E203.left")])]})]});
            var sketch = newSketch(context, id + "F408", { "sketchPlane" : qUnion([Q0])});
            skLineSegment(sketch, "E204.bottom", {"start": v(0.99, 0) * mm, "end": v(7.34, 0) * mm});
            skLineSegment(sketch, "E204.top", {"start": v(0.99, 6.35) * mm, "end": v(7.34, 6.35) * mm});
            skLineSegment(sketch, "E204.left", {"start": v(0.99, 0) * mm, "end": v(0.99, 6.35) * mm});
            skLineSegment(sketch, "E204.right", {"start": v(7.34, 0) * mm, "end": v(7.34, 6.35) * mm});
            skSolve(sketch);
        }
        {
            var Q0;
            Q0=makeQuery(id+"F408.imprint","IMPRINT",FACE,{"disambiguationData":[TD([[makeQuery(id+"F408.imprint","IMPRINT",EDGE,{"derivedFrom":sQuery(id+"F408.wireOp",EDGE,"E204.bottom")}),1.0]])]});
            extrude(context, id + "F409", {"entities" : qUnion([Q0]), "operationType" : NewBodyOperationType.ADD, "oppositeDirection" : true, "depth" : 19.05 * mm});
        }
        {
            var Q0;
            Q0=makeQuery(id+"F409.boolean.opBoolean","MERGE",FACE,{"derivedFrom":[makeQuery(id+"F407.opExtrude","CAP_FACE",FACE,{"disambiguationData":[OSD([sQuery(id+"F406.wireOp",EDGE,"E203.bottom"),sQuery(id+"F406.wireOp",EDGE,"E203.top"),sQuery(id+"F406.wireOp",EDGE,"E203.left"),sQuery(id+"F406.wireOp",EDGE,"E203.right")])],"isStart":false}),makeQuery(id+"F409.opExtrude","SWEPT_FACE",FACE,{"disambiguationData":[OSD([sQuery(id+"F408.wireOp",EDGE,"E204.bottom")])]})]});
            var sketch = newSketch(context, id + "F410", { "sketchPlane" : qUnion([Q0])});
            skLineSegment(sketch, "E205.bottom", {"start": v(-52, 0.99) * mm, "end": v(-58.34, 0.99) * mm});
            skLineSegment(sketch, "E205.top", {"start": v(-52, 7.34) * mm, "end": v(-58.34, 7.34) * mm});
            skLineSegment(sketch, "E205.left", {"start": v(-52, 0.99) * mm, "end": v(-52, 7.34) * mm});
            skLineSegment(sketch, "E205.right", {"start": v(-58.34, 0.99) * mm, "end": v(-58.34, 7.34) * mm});
            skSolve(sketch);
        }
        {
            var Q0;
            Q0=makeQuery(id+"F410.imprint","IMPRINT",FACE,{"disambiguationData":[TD([[makeQuery(id+"F410.imprint","IMPRINT",EDGE,{"derivedFrom":sQuery(id+"F410.wireOp",EDGE,"E205.bottom")}),-1.0]])]});
            extrude(context, id + "F411", {"entities" : qUnion([Q0]), "operationType" : NewBodyOperationType.ADD, "oppositeDirection" : true, "depth" : 19.05 * mm});
        }
        {
            var Q0;
            Q0=makeQuery(id+"F411.boolean.opBoolean","MERGE",FACE,{"derivedFrom":[makeQuery(id+"F409.boolean.opBoolean","MERGE",FACE,{"derivedFrom":[makeQuery(id+"F407.opExtrude","SWEPT_FACE",FACE,{"disambiguationData":[OSD([sQuery(id+"F406.wireOp",EDGE,"E203.top")])]}),makeQuery(id+"F409.opExtrude","SWEPT_FACE",FACE,{"disambiguationData":[OSD([sQuery(id+"F408.wireOp",EDGE,"E204.right")])]})]}),makeQuery(id+"F411.opExtrude","SWEPT_FACE",FACE,{"disambiguationData":[OSD([sQuery(id+"F410.wireOp",EDGE,"E205.top")])]})]});
            var sketch = newSketch(context, id + "F412", { "sketchPlane" : qUnion([Q0])});
            skLineSegment(sketch, "E206.bottom", {"start": v(-52, 19.05) * mm, "end": v(-58.34, 19.05) * mm});
            skLineSegment(sketch, "E206.top", {"start": v(-52, 12.7) * mm, "end": v(-58.34, 12.7) * mm});
            skLineSegment(sketch, "E206.left", {"start": v(-52, 19.05) * mm, "end": v(-52, 12.7) * mm});
            skLineSegment(sketch, "E206.right", {"start": v(-58.34, 19.05) * mm, "end": v(-58.34, 12.7) * mm});
            skSolve(sketch);
        }
        {
            var Q0;
            Q0=makeQuery(id+"F412.imprint","IMPRINT",FACE,{"disambiguationData":[TD([[makeQuery(id+"F412.imprint","IMPRINT",EDGE,{"derivedFrom":sQuery(id+"F412.wireOp",EDGE,"E206.bottom")}),-1.0]])]});
            extrude(context, id + "F413", {"entities" : qUnion([Q0]), "operationType" : NewBodyOperationType.ADD, "oppositeDirection" : true, "depth" : 31.75 * mm});
        }
        {
            var Q0;
            Q0=makeQuery(id+"F413.boolean.opBoolean","MERGE",FACE,{"derivedFrom":[makeQuery(id+"F411.boolean.opBoolean","MERGE",FACE,{"derivedFrom":[makeQuery(id+"F409.opExtrude","CAP_FACE",FACE,{"disambiguationData":[OSD([sQuery(id+"F408.wireOp",EDGE,"E204.bottom"),sQuery(id+"F408.wireOp",EDGE,"E204.top"),sQuery(id+"F408.wireOp",EDGE,"E204.left"),sQuery(id+"F408.wireOp",EDGE,"E204.right")])],"isStart":false}),makeQuery(id+"F411.opExtrude","SWEPT_FACE",FACE,{"disambiguationData":[OSD([sQuery(id+"F410.wireOp",EDGE,"E205.left")])]})]}),makeQuery(id+"F413.opExtrude","SWEPT_FACE",FACE,{"disambiguationData":[OSD([sQuery(id+"F412.wireOp",EDGE,"E206.left")])]})]});
            var sketch = newSketch(context, id + "F414", { "sketchPlane" : qUnion([Q0])});
            skLineSegment(sketch, "E207.bottom", {"start": v(24.41, 19.05) * mm, "end": v(18.06, 19.05) * mm});
            skLineSegment(sketch, "E207.top", {"start": v(24.41, 12.7) * mm, "end": v(18.06, 12.7) * mm});
            skLineSegment(sketch, "E207.left", {"start": v(24.41, 19.05) * mm, "end": v(24.41, 12.7) * mm});
            skLineSegment(sketch, "E207.right", {"start": v(18.06, 19.05) * mm, "end": v(18.06, 12.7) * mm});
            skSolve(sketch);
        }
        {
            var Q0;
            Q0=makeQuery(id+"F414.imprint","IMPRINT",FACE,{"disambiguationData":[TD([[makeQuery(id+"F414.imprint","IMPRINT",EDGE,{"derivedFrom":sQuery(id+"F414.wireOp",EDGE,"E207.bottom")}),1.0]])]});
            extrude(context, id + "F415", {"entities" : qUnion([Q0]), "operationType" : NewBodyOperationType.ADD, "oppositeDirection" : true, "depth" : 19.05 * mm});
        }
        {
            var Q0;
            Q0=makeQuery(id+"F415.boolean.opBoolean","MERGE",FACE,{"derivedFrom":[makeQuery(id+"F413.opExtrude","CAP_FACE",FACE,{"disambiguationData":[OSD([sQuery(id+"F412.wireOp",EDGE,"E206.bottom"),sQuery(id+"F412.wireOp",EDGE,"E206.top"),sQuery(id+"F412.wireOp",EDGE,"E206.left"),sQuery(id+"F412.wireOp",EDGE,"E206.right")])],"isStart":false}),makeQuery(id+"F415.opExtrude","SWEPT_FACE",FACE,{"disambiguationData":[OSD([sQuery(id+"F414.wireOp",EDGE,"E207.left")])]})]});
            var sketch = newSketch(context, id + "F416", { "sketchPlane" : qUnion([Q0])});
            skLineSegment(sketch, "E208.bottom", {"start": v(71.04, 12.7) * mm, "end": v(64.7, 12.7) * mm});
            skLineSegment(sketch, "E208.top", {"start": v(71.04, 19.05) * mm, "end": v(64.7, 19.05) * mm});
            skLineSegment(sketch, "E208.left", {"start": v(71.04, 12.7) * mm, "end": v(71.04, 19.05) * mm});
            skLineSegment(sketch, "E208.right", {"start": v(64.7, 12.7) * mm, "end": v(64.7, 19.05) * mm});
            skSolve(sketch);
        }
        {
            var Q0;
            Q0=makeQuery(id+"F416.imprint","IMPRINT",FACE,{"disambiguationData":[TD([[makeQuery(id+"F416.imprint","IMPRINT",EDGE,{"derivedFrom":sQuery(id+"F416.wireOp",EDGE,"E208.bottom")}),1.0]])]});
            extrude(context, id + "F417", {"entities" : qUnion([Q0]), "operationType" : NewBodyOperationType.ADD, "oppositeDirection" : true, "depth" : 19.05 * mm});
        }
        {
            var Q0;
            Q0=makeQuery(id+"F417.boolean.opBoolean","MERGE",FACE,{"derivedFrom":[makeQuery(id+"F415.boolean.opBoolean","MERGE",FACE,{"derivedFrom":[makeQuery(id+"F413.boolean.opBoolean","MERGE",FACE,{"derivedFrom":[makeQuery(id+"F411.opExtrude","CAP_FACE",FACE,{"disambiguationData":[OSD([sQuery(id+"F410.wireOp",EDGE,"E205.bottom"),sQuery(id+"F410.wireOp",EDGE,"E205.top"),sQuery(id+"F410.wireOp",EDGE,"E205.left"),sQuery(id+"F410.wireOp",EDGE,"E205.right")])],"isStart":false}),makeQuery(id+"F413.opExtrude","SWEPT_FACE",FACE,{"disambiguationData":[OSD([sQuery(id+"F412.wireOp",EDGE,"E206.bottom")])]})]}),makeQuery(id+"F415.opExtrude","SWEPT_FACE",FACE,{"disambiguationData":[OSD([sQuery(id+"F414.wireOp",EDGE,"E207.bottom")])]})]}),makeQuery(id+"F417.opExtrude","SWEPT_FACE",FACE,{"disambiguationData":[OSD([sQuery(id+"F416.wireOp",EDGE,"E208.top")])]})]});
            var sketch = newSketch(context, id + "F418", { "sketchPlane" : qUnion([Q0])});
            skLineSegment(sketch, "E209.bottom", {"start": v(-71.04, 5.36) * mm, "end": v(-64.7, 5.36) * mm});
            skLineSegment(sketch, "E209.top", {"start": v(-71.04, 11.71) * mm, "end": v(-64.7, 11.71) * mm});
            skLineSegment(sketch, "E209.left", {"start": v(-71.04, 5.36) * mm, "end": v(-71.04, 11.71) * mm});
            skLineSegment(sketch, "E209.right", {"start": v(-64.7, 5.36) * mm, "end": v(-64.7, 11.71) * mm});
            skSolve(sketch);
        }
        {
            var Q0;
            Q0=makeQuery(id+"F418.imprint","IMPRINT",FACE,{"disambiguationData":[TD([[makeQuery(id+"F418.imprint","IMPRINT",EDGE,{"derivedFrom":sQuery(id+"F418.wireOp",EDGE,"E209.bottom")}),1.0]])]});
            extrude(context, id + "F419", {"entities" : qUnion([Q0]), "operationType" : NewBodyOperationType.ADD, "oppositeDirection" : true, "depth" : 19.05 * mm});
        }
        {
            var Q0;
            Q0=makeQuery(id+"F419.boolean.opBoolean","MERGE",FACE,{"derivedFrom":[makeQuery(id+"F417.opExtrude","CAP_FACE",FACE,{"disambiguationData":[OSD([sQuery(id+"F416.wireOp",EDGE,"E208.bottom"),sQuery(id+"F416.wireOp",EDGE,"E208.top"),sQuery(id+"F416.wireOp",EDGE,"E208.left"),sQuery(id+"F416.wireOp",EDGE,"E208.right")])],"isStart":false}),makeQuery(id+"F419.opExtrude","SWEPT_FACE",FACE,{"disambiguationData":[OSD([sQuery(id+"F418.wireOp",EDGE,"E209.bottom")])]})]});
            var sketch = newSketch(context, id + "F420", { "sketchPlane" : qUnion([Q0])});
            skLineSegment(sketch, "E210.bottom", {"start": v(-64.7, 0) * mm, "end": v(-71.04, 0) * mm});
            skLineSegment(sketch, "E210.top", {"start": v(-64.7, 6.35) * mm, "end": v(-71.04, 6.35) * mm});
            skLineSegment(sketch, "E210.left", {"start": v(-64.7, 0) * mm, "end": v(-64.7, 6.35) * mm});
            skLineSegment(sketch, "E210.right", {"start": v(-71.04, 0) * mm, "end": v(-71.04, 6.35) * mm});
            skSolve(sketch);
        }
        {
            var Q0;
            Q0=makeQuery(id+"F420.imprint","IMPRINT",FACE,{"disambiguationData":[TD([[makeQuery(id+"F420.imprint","IMPRINT",EDGE,{"derivedFrom":sQuery(id+"F420.wireOp",EDGE,"E210.bottom")}),1.0]])]});
            extrude(context, id + "F421", {"entities" : qUnion([Q0]), "operationType" : NewBodyOperationType.ADD, "oppositeDirection" : true, "depth" : 19.05 * mm});
        }
        {
            var Q0;
            Q0=makeQuery(id+"F421.boolean.opBoolean","MERGE",FACE,{"derivedFrom":[makeQuery(id+"F419.boolean.opBoolean","MERGE",FACE,{"derivedFrom":[makeQuery(id+"F417.boolean.opBoolean","MERGE",FACE,{"derivedFrom":[makeQuery(id+"F415.opExtrude","CAP_FACE",FACE,{"disambiguationData":[OSD([sQuery(id+"F414.wireOp",EDGE,"E207.bottom"),sQuery(id+"F414.wireOp",EDGE,"E207.top"),sQuery(id+"F414.wireOp",EDGE,"E207.left"),sQuery(id+"F414.wireOp",EDGE,"E207.right")])],"isStart":false}),makeQuery(id+"F417.opExtrude","SWEPT_FACE",FACE,{"disambiguationData":[OSD([sQuery(id+"F416.wireOp",EDGE,"E208.left")])]})]}),makeQuery(id+"F419.opExtrude","SWEPT_FACE",FACE,{"disambiguationData":[OSD([sQuery(id+"F418.wireOp",EDGE,"E209.left")])]})]}),makeQuery(id+"F421.opExtrude","SWEPT_FACE",FACE,{"disambiguationData":[OSD([sQuery(id+"F420.wireOp",EDGE,"E210.right")])]})]});
            var sketch = newSketch(context, id + "F422", { "sketchPlane" : qUnion([Q0])});
            skLineSegment(sketch, "E211.bottom", {"start": v(-24.41, 0) * mm, "end": v(-18.06, 0) * mm});
            skLineSegment(sketch, "E211.top", {"start": v(-24.41, 6.35) * mm, "end": v(-18.06, 6.35) * mm});
            skLineSegment(sketch, "E211.left", {"start": v(-24.41, 0) * mm, "end": v(-24.41, 6.35) * mm});
            skLineSegment(sketch, "E211.right", {"start": v(-18.06, 0) * mm, "end": v(-18.06, 6.35) * mm});
            skSolve(sketch);
        }
        {
            var Q0;
            Q0=makeQuery(id+"F422.imprint","IMPRINT",FACE,{"disambiguationData":[TD([[makeQuery(id+"F422.imprint","IMPRINT",EDGE,{"derivedFrom":sQuery(id+"F422.wireOp",EDGE,"E211.bottom")}),1.0]])]});
            extrude(context, id + "F423", {"entities" : qUnion([Q0]), "operationType" : NewBodyOperationType.ADD, "oppositeDirection" : true, "depth" : 19.05 * mm});
        }
        {
            var Q0;
            Q0=makeQuery(id+"F423.boolean.opBoolean","MERGE",FACE,{"derivedFrom":[makeQuery(id+"F421.opExtrude","CAP_FACE",FACE,{"disambiguationData":[OSD([sQuery(id+"F420.wireOp",EDGE,"E210.bottom"),sQuery(id+"F420.wireOp",EDGE,"E210.top"),sQuery(id+"F420.wireOp",EDGE,"E210.left"),sQuery(id+"F420.wireOp",EDGE,"E210.right")])],"isStart":false}),makeQuery(id+"F423.opExtrude","SWEPT_FACE",FACE,{"disambiguationData":[OSD([sQuery(id+"F422.wireOp",EDGE,"E211.left")])]})]});
            var sketch = newSketch(context, id + "F424", { "sketchPlane" : qUnion([Q0])});
            skLineSegment(sketch, "E212.bottom", {"start": v(52, 0) * mm, "end": v(58.34, 0) * mm});
            skLineSegment(sketch, "E212.top", {"start": v(52, 6.35) * mm, "end": v(58.34, 6.35) * mm});
            skLineSegment(sketch, "E212.left", {"start": v(52, 0) * mm, "end": v(52, 6.35) * mm});
            skLineSegment(sketch, "E212.right", {"start": v(58.34, 0) * mm, "end": v(58.34, 6.35) * mm});
            skSolve(sketch);
        }
        {
            var Q0;
            Q0=makeQuery(id+"F424.imprint","IMPRINT",FACE,{"disambiguationData":[TD([[makeQuery(id+"F424.imprint","IMPRINT",EDGE,{"derivedFrom":sQuery(id+"F424.wireOp",EDGE,"E212.bottom")}),-1.0]])]});
            extrude(context, id + "F425", {"entities" : qUnion([Q0]), "operationType" : NewBodyOperationType.ADD, "oppositeDirection" : true, "depth" : 19.05 * mm});
        }
        {
            var Q0;
            Q0=makeQuery(id+"F425.opExtrude","SWEPT_FACE",FACE,{"disambiguationData":[OSD([sQuery(id+"F424.wireOp",EDGE,"E212.right")])]});
            var sketch = newSketch(context, id + "F426", { "sketchPlane" : qUnion([Q0])});
            skLineSegment(sketch, "E213.bottom", {"start": v(-5.36, 0) * mm, "end": v(-11.71, 0) * mm});
            skLineSegment(sketch, "E213.top", {"start": v(-5.36, 6.35) * mm, "end": v(-11.71, 6.35) * mm});
            skLineSegment(sketch, "E213.left", {"start": v(-5.36, 0) * mm, "end": v(-5.36, 6.35) * mm});
            skLineSegment(sketch, "E213.right", {"start": v(-11.71, 0) * mm, "end": v(-11.71, 6.35) * mm});
            skSolve(sketch);
        }
        {
            var Q0;
            Q0=makeQuery(id+"F426.imprint","IMPRINT",FACE,{"disambiguationData":[TD([[makeQuery(id+"F426.imprint","IMPRINT",EDGE,{"derivedFrom":sQuery(id+"F426.wireOp",EDGE,"E213.bottom")}),-1.0]])]});
            extrude(context, id + "F427", {"entities" : qUnion([Q0]), "operationType" : NewBodyOperationType.ADD, "oppositeDirection" : true, "depth" : 19.05 * mm});
        }
        {
            var Q0;
            Q0=makeQuery(id+"F427.boolean.opBoolean","MERGE",FACE,{"derivedFrom":[makeQuery(id+"F425.opExtrude","CAP_FACE",FACE,{"disambiguationData":[OSD([sQuery(id+"F424.wireOp",EDGE,"E212.bottom"),sQuery(id+"F424.wireOp",EDGE,"E212.top"),sQuery(id+"F424.wireOp",EDGE,"E212.left"),sQuery(id+"F424.wireOp",EDGE,"E212.right")])],"isStart":false}),makeQuery(id+"F427.opExtrude","SWEPT_FACE",FACE,{"disambiguationData":[OSD([sQuery(id+"F426.wireOp",EDGE,"E213.left")])]})]});
            var sketch = newSketch(context, id + "F428", { "sketchPlane" : qUnion([Q0])});
            skLineSegment(sketch, "E214.bottom", {"start": v(-39.3, 6.35) * mm, "end": v(-45.64, 6.35) * mm});
            skLineSegment(sketch, "E214.top", {"start": v(-39.3, 0) * mm, "end": v(-45.64, 0) * mm});
            skLineSegment(sketch, "E214.left", {"start": v(-39.3, 6.35) * mm, "end": v(-39.3, 0) * mm});
            skLineSegment(sketch, "E214.right", {"start": v(-45.64, 6.35) * mm, "end": v(-45.64, 0) * mm});
            skSolve(sketch);
        }
        {
            var Q0;
            Q0=makeQuery(id+"F428.imprint","IMPRINT",FACE,{"disambiguationData":[TD([[makeQuery(id+"F428.imprint","IMPRINT",EDGE,{"derivedFrom":sQuery(id+"F428.wireOp",EDGE,"E214.bottom")}),1.0]])]});
            extrude(context, id + "F429", {"entities" : qUnion([Q0]), "operationType" : NewBodyOperationType.ADD, "oppositeDirection" : true, "depth" : 19.05 * mm});
        }
        {
            var Q0;
            Q0=makeQuery(id+"F429.boolean.opBoolean","MERGE",FACE,{"derivedFrom":[makeQuery(id+"F427.boolean.opBoolean","MERGE",FACE,{"derivedFrom":[makeQuery(id+"F425.boolean.opBoolean","MERGE",FACE,{"derivedFrom":[makeQuery(id+"F423.boolean.opBoolean","MERGE",FACE,{"derivedFrom":[makeQuery(id+"F421.boolean.opBoolean","MERGE",FACE,{"derivedFrom":[makeQuery(id+"F419.opExtrude","CAP_FACE",FACE,{"disambiguationData":[OSD([sQuery(id+"F418.wireOp",EDGE,"E209.bottom"),sQuery(id+"F418.wireOp",EDGE,"E209.top"),sQuery(id+"F418.wireOp",EDGE,"E209.left"),sQuery(id+"F418.wireOp",EDGE,"E209.right")])],"isStart":false}),makeQuery(id+"F421.opExtrude","SWEPT_FACE",FACE,{"disambiguationData":[OSD([sQuery(id+"F420.wireOp",EDGE,"E210.bottom")])]})]}),makeQuery(id+"F423.opExtrude","SWEPT_FACE",FACE,{"disambiguationData":[OSD([sQuery(id+"F422.wireOp",EDGE,"E211.bottom")])]})]}),makeQuery(id+"F425.opExtrude","SWEPT_FACE",FACE,{"disambiguationData":[OSD([sQuery(id+"F424.wireOp",EDGE,"E212.bottom")])]})]}),makeQuery(id+"F427.opExtrude","SWEPT_FACE",FACE,{"disambiguationData":[OSD([sQuery(id+"F426.wireOp",EDGE,"E213.bottom")])]})]}),makeQuery(id+"F429.opExtrude","SWEPT_FACE",FACE,{"disambiguationData":[OSD([sQuery(id+"F428.wireOp",EDGE,"E214.top")])]})]});
            var sketch = newSketch(context, id + "F430", { "sketchPlane" : qUnion([Q0])});
            skLineSegment(sketch, "E215.bottom", {"start": v(-39.3, -24.41) * mm, "end": v(-45.64, -24.41) * mm});
            skLineSegment(sketch, "E215.top", {"start": v(-39.3, -18.06) * mm, "end": v(-45.64, -18.06) * mm});
            skLineSegment(sketch, "E215.left", {"start": v(-39.3, -24.41) * mm, "end": v(-39.3, -18.06) * mm});
            skLineSegment(sketch, "E215.right", {"start": v(-45.64, -24.41) * mm, "end": v(-45.64, -18.06) * mm});
            skSolve(sketch);
        }
        {
            var Q0;
            Q0=makeQuery(id+"F430.imprint","IMPRINT",FACE,{"disambiguationData":[TD([[makeQuery(id+"F430.imprint","IMPRINT",EDGE,{"derivedFrom":sQuery(id+"F430.wireOp",EDGE,"E215.bottom")}),1.0]])]});
            extrude(context, id + "F431", {"entities" : qUnion([Q0]), "operationType" : NewBodyOperationType.ADD, "oppositeDirection" : true, "depth" : 19.05 * mm});
        }
        {
            var Q0;
            Q0=makeQuery(id+"F431.boolean.opBoolean","MERGE",FACE,{"derivedFrom":[makeQuery(id+"F429.opExtrude","CAP_FACE",FACE,{"disambiguationData":[OSD([sQuery(id+"F428.wireOp",EDGE,"E214.bottom"),sQuery(id+"F428.wireOp",EDGE,"E214.top"),sQuery(id+"F428.wireOp",EDGE,"E214.left"),sQuery(id+"F428.wireOp",EDGE,"E214.right")])],"isStart":false}),makeQuery(id+"F431.opExtrude","SWEPT_FACE",FACE,{"disambiguationData":[OSD([sQuery(id+"F430.wireOp",EDGE,"E215.bottom")])]})]});
            var sketch = newSketch(context, id + "F432", { "sketchPlane" : qUnion([Q0])});
            skLineSegment(sketch, "E216.bottom", {"start": v(45.64, 19.05) * mm, "end": v(39.3, 19.05) * mm});
            skLineSegment(sketch, "E216.top", {"start": v(45.64, 12.7) * mm, "end": v(39.3, 12.7) * mm});
            skLineSegment(sketch, "E216.left", {"start": v(45.64, 19.05) * mm, "end": v(45.64, 12.7) * mm});
            skLineSegment(sketch, "E216.right", {"start": v(39.3, 19.05) * mm, "end": v(39.3, 12.7) * mm});
            skSolve(sketch);
        }
        {
            var Q0;
            Q0=makeQuery(id+"F432.imprint","IMPRINT",FACE,{"disambiguationData":[TD([[makeQuery(id+"F432.imprint","IMPRINT",EDGE,{"derivedFrom":sQuery(id+"F432.wireOp",EDGE,"E216.bottom")}),1.0]])]});
            extrude(context, id + "F433", {"entities" : qUnion([Q0]), "operationType" : NewBodyOperationType.ADD, "oppositeDirection" : true, "depth" : 19.05 * mm});
        }
        {
            var Q0;
            Q0=makeQuery(id+"F433.boolean.opBoolean","MERGE",FACE,{"derivedFrom":[makeQuery(id+"F431.boolean.opBoolean","MERGE",FACE,{"derivedFrom":[makeQuery(id+"F429.opExtrude","SWEPT_FACE",FACE,{"disambiguationData":[OSD([sQuery(id+"F428.wireOp",EDGE,"E214.right")])]}),makeQuery(id+"F431.opExtrude","SWEPT_FACE",FACE,{"disambiguationData":[OSD([sQuery(id+"F430.wireOp",EDGE,"E215.right")])]})]}),makeQuery(id+"F433.opExtrude","SWEPT_FACE",FACE,{"disambiguationData":[OSD([sQuery(id+"F432.wireOp",EDGE,"E216.left")])]})]});
            var sketch = newSketch(context, id + "F434", { "sketchPlane" : qUnion([Q0])});
            skLineSegment(sketch, "E217.bottom", {"start": v(-5.36, 19.05) * mm, "end": v(-11.71, 19.05) * mm});
            skLineSegment(sketch, "E217.top", {"start": v(-5.36, 12.7) * mm, "end": v(-11.71, 12.7) * mm});
            skLineSegment(sketch, "E217.left", {"start": v(-5.36, 19.05) * mm, "end": v(-5.36, 12.7) * mm});
            skLineSegment(sketch, "E217.right", {"start": v(-11.71, 19.05) * mm, "end": v(-11.71, 12.7) * mm});
            skSolve(sketch);
        }
        {
            var Q0;
            Q0=makeQuery(id+"F434.imprint","IMPRINT",FACE,{"disambiguationData":[TD([[makeQuery(id+"F434.imprint","IMPRINT",EDGE,{"derivedFrom":sQuery(id+"F434.wireOp",EDGE,"E217.bottom")}),-1.0]])]});
            extrude(context, id + "F435", {"entities" : qUnion([Q0]), "operationType" : NewBodyOperationType.ADD, "oppositeDirection" : true, "depth" : 19.05 * mm});
        }
        {
            var Q0;
            Q0=makeQuery(id+"F435.boolean.opBoolean","MERGE",FACE,{"derivedFrom":[makeQuery(id+"F433.opExtrude","CAP_FACE",FACE,{"disambiguationData":[OSD([sQuery(id+"F432.wireOp",EDGE,"E216.bottom"),sQuery(id+"F432.wireOp",EDGE,"E216.top"),sQuery(id+"F432.wireOp",EDGE,"E216.left"),sQuery(id+"F432.wireOp",EDGE,"E216.right")])],"isStart":false}),makeQuery(id+"F435.opExtrude","SWEPT_FACE",FACE,{"disambiguationData":[OSD([sQuery(id+"F434.wireOp",EDGE,"E217.left")])]})]});
            var sketch = newSketch(context, id + "F436", { "sketchPlane" : qUnion([Q0])});
            skLineSegment(sketch, "E218.bottom", {"start": v(-26.6, 12.7) * mm, "end": v(-32.94, 12.7) * mm});
            skLineSegment(sketch, "E218.top", {"start": v(-26.6, 19.05) * mm, "end": v(-32.94, 19.05) * mm});
            skLineSegment(sketch, "E218.left", {"start": v(-26.6, 12.7) * mm, "end": v(-26.6, 19.05) * mm});
            skLineSegment(sketch, "E218.right", {"start": v(-32.94, 12.7) * mm, "end": v(-32.94, 19.05) * mm});
            skSolve(sketch);
        }
        {
            var Q0;
            Q0=makeQuery(id+"F436.imprint","IMPRINT",FACE,{"disambiguationData":[TD([[makeQuery(id+"F436.imprint","IMPRINT",EDGE,{"derivedFrom":sQuery(id+"F436.wireOp",EDGE,"E218.bottom")}),1.0]])]});
            extrude(context, id + "F437", {"entities" : qUnion([Q0]), "operationType" : NewBodyOperationType.ADD, "oppositeDirection" : true, "depth" : 19.05 * mm});
        }
        {
            var Q0;
            Q0=makeQuery(id+"F437.boolean.opBoolean","MERGE",FACE,{"derivedFrom":[makeQuery(id+"F435.boolean.opBoolean","MERGE",FACE,{"derivedFrom":[makeQuery(id+"F433.boolean.opBoolean","MERGE",FACE,{"derivedFrom":[makeQuery(id+"F431.opExtrude","CAP_FACE",FACE,{"disambiguationData":[OSD([sQuery(id+"F430.wireOp",EDGE,"E215.bottom"),sQuery(id+"F430.wireOp",EDGE,"E215.top"),sQuery(id+"F430.wireOp",EDGE,"E215.left"),sQuery(id+"F430.wireOp",EDGE,"E215.right")])],"isStart":false}),makeQuery(id+"F433.opExtrude","SWEPT_FACE",FACE,{"disambiguationData":[OSD([sQuery(id+"F432.wireOp",EDGE,"E216.bottom")])]})]}),makeQuery(id+"F435.opExtrude","SWEPT_FACE",FACE,{"disambiguationData":[OSD([sQuery(id+"F434.wireOp",EDGE,"E217.bottom")])]})]}),makeQuery(id+"F437.opExtrude","SWEPT_FACE",FACE,{"disambiguationData":[OSD([sQuery(id+"F436.wireOp",EDGE,"E218.top")])]})]});
            var sketch = newSketch(context, id + "F438", { "sketchPlane" : qUnion([Q0])});
            skLineSegment(sketch, "E219.bottom", {"start": v(-26.6, 24.41) * mm, "end": v(-32.94, 24.41) * mm});
            skLineSegment(sketch, "E219.top", {"start": v(-26.6, 18.06) * mm, "end": v(-32.94, 18.06) * mm});
            skLineSegment(sketch, "E219.left", {"start": v(-26.6, 24.41) * mm, "end": v(-26.6, 18.06) * mm});
            skLineSegment(sketch, "E219.right", {"start": v(-32.94, 24.41) * mm, "end": v(-32.94, 18.06) * mm});
            skSolve(sketch);
        }
        {
            var Q0;
            Q0=makeQuery(id+"F438.imprint","IMPRINT",FACE,{"disambiguationData":[TD([[makeQuery(id+"F438.imprint","IMPRINT",EDGE,{"derivedFrom":sQuery(id+"F438.wireOp",EDGE,"E219.bottom")}),-1.0]])]});
            extrude(context, id + "F439", {"entities" : qUnion([Q0]), "operationType" : NewBodyOperationType.ADD, "oppositeDirection" : true, "depth" : 19.05 * mm});
        }
        {
            var Q0;
            Q0=makeQuery(id+"F439.boolean.opBoolean","MERGE",FACE,{"derivedFrom":[makeQuery(id+"F437.opExtrude","CAP_FACE",FACE,{"disambiguationData":[OSD([sQuery(id+"F436.wireOp",EDGE,"E218.bottom"),sQuery(id+"F436.wireOp",EDGE,"E218.top"),sQuery(id+"F436.wireOp",EDGE,"E218.left"),sQuery(id+"F436.wireOp",EDGE,"E218.right")])],"isStart":false}),makeQuery(id+"F439.opExtrude","SWEPT_FACE",FACE,{"disambiguationData":[OSD([sQuery(id+"F438.wireOp",EDGE,"E219.bottom")])]})]});
            var sketch = newSketch(context, id + "F440", { "sketchPlane" : qUnion([Q0])});
            skLineSegment(sketch, "E220.bottom", {"start": v(26.6, 0) * mm, "end": v(32.94, 0) * mm});
            skLineSegment(sketch, "E220.top", {"start": v(26.6, 6.35) * mm, "end": v(32.94, 6.35) * mm});
            skLineSegment(sketch, "E220.left", {"start": v(26.6, 0) * mm, "end": v(26.6, 6.35) * mm});
            skLineSegment(sketch, "E220.right", {"start": v(32.94, 0) * mm, "end": v(32.94, 6.35) * mm});
            skSolve(sketch);
        }
        {
            var Q0;
            Q0=makeQuery(id+"F440.imprint","IMPRINT",FACE,{"disambiguationData":[TD([[makeQuery(id+"F440.imprint","IMPRINT",EDGE,{"derivedFrom":sQuery(id+"F440.wireOp",EDGE,"E220.bottom")}),-1.0]])]});
            extrude(context, id + "F441", {"entities" : qUnion([Q0]), "operationType" : NewBodyOperationType.ADD, "oppositeDirection" : true, "depth" : 31.75 * mm});
        }
        {
            var Q0;
            Q0=makeQuery(id+"F441.boolean.opBoolean","MERGE",FACE,{"derivedFrom":[makeQuery(id+"F439.opExtrude","CAP_FACE",FACE,{"disambiguationData":[OSD([sQuery(id+"F438.wireOp",EDGE,"E219.bottom"),sQuery(id+"F438.wireOp",EDGE,"E219.top"),sQuery(id+"F438.wireOp",EDGE,"E219.left"),sQuery(id+"F438.wireOp",EDGE,"E219.right")])],"isStart":false}),makeQuery(id+"F441.opExtrude","SWEPT_FACE",FACE,{"disambiguationData":[OSD([sQuery(id+"F440.wireOp",EDGE,"E220.bottom")])]})]});
            var sketch = newSketch(context, id + "F442", { "sketchPlane" : qUnion([Q0])});
            skLineSegment(sketch, "E221.bottom", {"start": v(-26.6, 7.34) * mm, "end": v(-32.94, 7.34) * mm});
            skLineSegment(sketch, "E221.top", {"start": v(-26.6, 0.99) * mm, "end": v(-32.94, 0.99) * mm});
            skLineSegment(sketch, "E221.left", {"start": v(-26.6, 7.34) * mm, "end": v(-26.6, 0.99) * mm});
            skLineSegment(sketch, "E221.right", {"start": v(-32.94, 7.34) * mm, "end": v(-32.94, 0.99) * mm});
            skSolve(sketch);
        }
        {
            var Q0;
            Q0=makeQuery(id+"F442.imprint","IMPRINT",FACE,{"disambiguationData":[TD([[makeQuery(id+"F442.imprint","IMPRINT",EDGE,{"derivedFrom":sQuery(id+"F442.wireOp",EDGE,"E221.bottom")}),-1.0]])]});
            extrude(context, id + "F443", {"entities" : qUnion([Q0]), "operationType" : NewBodyOperationType.ADD, "oppositeDirection" : true, "depth" : 19.05 * mm});
        }
        {
            var Q0;
            Q0=makeQuery(id+"F443.boolean.opBoolean","MERGE",FACE,{"derivedFrom":[makeQuery(id+"F441.boolean.opBoolean","MERGE",FACE,{"derivedFrom":[makeQuery(id+"F439.boolean.opBoolean","MERGE",FACE,{"derivedFrom":[makeQuery(id+"F437.boolean.opBoolean","MERGE",FACE,{"derivedFrom":[makeQuery(id+"F435.opExtrude","CAP_FACE",FACE,{"disambiguationData":[OSD([sQuery(id+"F434.wireOp",EDGE,"E217.bottom"),sQuery(id+"F434.wireOp",EDGE,"E217.top"),sQuery(id+"F434.wireOp",EDGE,"E217.left"),sQuery(id+"F434.wireOp",EDGE,"E217.right")])],"isStart":false}),makeQuery(id+"F437.opExtrude","SWEPT_FACE",FACE,{"disambiguationData":[OSD([sQuery(id+"F436.wireOp",EDGE,"E218.left")])]})]}),makeQuery(id+"F439.opExtrude","SWEPT_FACE",FACE,{"disambiguationData":[OSD([sQuery(id+"F438.wireOp",EDGE,"E219.left")])]})]}),makeQuery(id+"F441.opExtrude","SWEPT_FACE",FACE,{"disambiguationData":[OSD([sQuery(id+"F440.wireOp",EDGE,"E220.left")])]})]}),makeQuery(id+"F443.opExtrude","SWEPT_FACE",FACE,{"disambiguationData":[OSD([sQuery(id+"F442.wireOp",EDGE,"E221.left")])]})]});
            var sketch = newSketch(context, id + "F444", { "sketchPlane" : qUnion([Q0])});
            skLineSegment(sketch, "E222.bottom", {"start": v(-7.34, 19.05) * mm, "end": v(-0.99, 19.05) * mm});
            skLineSegment(sketch, "E222.top", {"start": v(-7.34, 12.7) * mm, "end": v(-0.99, 12.7) * mm});
            skLineSegment(sketch, "E222.left", {"start": v(-7.34, 19.05) * mm, "end": v(-7.34, 12.7) * mm});
            skLineSegment(sketch, "E222.right", {"start": v(-0.99, 19.05) * mm, "end": v(-0.99, 12.7) * mm});
            skSolve(sketch);
        }
        {
            var Q0;
            Q0=makeQuery(id+"F444.imprint","IMPRINT",FACE,{"disambiguationData":[TD([[makeQuery(id+"F444.imprint","IMPRINT",EDGE,{"derivedFrom":sQuery(id+"F444.wireOp",EDGE,"E222.bottom")}),1.0]])]});
            extrude(context, id + "F445", {"entities" : qUnion([Q0]), "operationType" : NewBodyOperationType.ADD, "oppositeDirection" : true, "depth" : 19.05 * mm});
        }
        {
            var Q0;
            Q0=makeQuery(id+"F445.boolean.opBoolean","MERGE",FACE,{"derivedFrom":[makeQuery(id+"F443.opExtrude","CAP_FACE",FACE,{"disambiguationData":[OSD([sQuery(id+"F442.wireOp",EDGE,"E221.bottom"),sQuery(id+"F442.wireOp",EDGE,"E221.top"),sQuery(id+"F442.wireOp",EDGE,"E221.left"),sQuery(id+"F442.wireOp",EDGE,"E221.right")])],"isStart":false}),makeQuery(id+"F445.opExtrude","SWEPT_FACE",FACE,{"disambiguationData":[OSD([sQuery(id+"F444.wireOp",EDGE,"E222.bottom")])]})]});
            var sketch = newSketch(context, id + "F446", { "sketchPlane" : qUnion([Q0])});
            skLineSegment(sketch, "E223.bottom", {"start": v(-45.64, -7.34) * mm, "end": v(-39.3, -7.34) * mm});
            skLineSegment(sketch, "E223.top", {"start": v(-45.64, -0.99) * mm, "end": v(-39.3, -0.99) * mm});
            skLineSegment(sketch, "E223.left", {"start": v(-45.64, -7.34) * mm, "end": v(-45.64, -0.99) * mm});
            skLineSegment(sketch, "E223.right", {"start": v(-39.3, -7.34) * mm, "end": v(-39.3, -0.99) * mm});
            skSolve(sketch);
        }
        {
            var Q0;
            Q0=makeQuery(id+"F446.imprint","IMPRINT",FACE,{"disambiguationData":[TD([[makeQuery(id+"F446.imprint","IMPRINT",EDGE,{"derivedFrom":sQuery(id+"F446.wireOp",EDGE,"E223.bottom")}),1.0]])]});
            extrude(context, id + "F447", {"entities" : qUnion([Q0]), "operationType" : NewBodyOperationType.ADD, "oppositeDirection" : true, "depth" : 19.05 * mm});
        }
        {
            var Q0;
            Q0=makeQuery(id+"F447.boolean.opBoolean","MERGE",FACE,{"derivedFrom":[makeQuery(id+"F445.boolean.opBoolean","MERGE",FACE,{"derivedFrom":[makeQuery(id+"F443.opExtrude","SWEPT_FACE",FACE,{"disambiguationData":[OSD([sQuery(id+"F442.wireOp",EDGE,"E221.top")])]}),makeQuery(id+"F445.opExtrude","SWEPT_FACE",FACE,{"disambiguationData":[OSD([sQuery(id+"F444.wireOp",EDGE,"E222.right")])]})]}),makeQuery(id+"F447.opExtrude","SWEPT_FACE",FACE,{"disambiguationData":[OSD([sQuery(id+"F446.wireOp",EDGE,"E223.top")])]})]});
            var sketch = newSketch(context, id + "F448", { "sketchPlane" : qUnion([Q0])});
            skLineSegment(sketch, "E224.bottom", {"start": v(45.64, 0) * mm, "end": v(39.3, 0) * mm});
            skLineSegment(sketch, "E224.top", {"start": v(45.64, 6.35) * mm, "end": v(39.3, 6.35) * mm});
            skLineSegment(sketch, "E224.left", {"start": v(45.64, 0) * mm, "end": v(45.64, 6.35) * mm});
            skLineSegment(sketch, "E224.right", {"start": v(39.3, 0) * mm, "end": v(39.3, 6.35) * mm});
            skSolve(sketch);
        }
        {
            var Q0;
            Q0=makeQuery(id+"F448.imprint","IMPRINT",FACE,{"disambiguationData":[TD([[makeQuery(id+"F448.imprint","IMPRINT",EDGE,{"derivedFrom":sQuery(id+"F448.wireOp",EDGE,"E224.bottom")}),1.0]])]});
            extrude(context, id + "F449", {"entities" : qUnion([Q0]), "operationType" : NewBodyOperationType.ADD, "oppositeDirection" : true, "depth" : 19.05 * mm});
        }
        {
            var Q0;
            Q0=makeQuery(id+"F449.boolean.opBoolean","MERGE",FACE,{"derivedFrom":[makeQuery(id+"F447.opExtrude","CAP_FACE",FACE,{"disambiguationData":[OSD([sQuery(id+"F446.wireOp",EDGE,"E223.bottom"),sQuery(id+"F446.wireOp",EDGE,"E223.top"),sQuery(id+"F446.wireOp",EDGE,"E223.left"),sQuery(id+"F446.wireOp",EDGE,"E223.right")])],"isStart":false}),makeQuery(id+"F449.opExtrude","SWEPT_FACE",FACE,{"disambiguationData":[OSD([sQuery(id+"F448.wireOp",EDGE,"E224.bottom")])]})]});
            var sketch = newSketch(context, id + "F450", { "sketchPlane" : qUnion([Q0])});
            skLineSegment(sketch, "E225.bottom", {"start": v(-45.64, 20.04) * mm, "end": v(-39.3, 20.04) * mm});
            skLineSegment(sketch, "E225.top", {"start": v(-45.64, 13.69) * mm, "end": v(-39.3, 13.69) * mm});
            skLineSegment(sketch, "E225.left", {"start": v(-45.64, 20.04) * mm, "end": v(-45.64, 13.69) * mm});
            skLineSegment(sketch, "E225.right", {"start": v(-39.3, 20.04) * mm, "end": v(-39.3, 13.69) * mm});
            skSolve(sketch);
        }
        {
            var Q0;
            Q0=makeQuery(id+"F450.imprint","IMPRINT",FACE,{"disambiguationData":[TD([[makeQuery(id+"F450.imprint","IMPRINT",EDGE,{"derivedFrom":sQuery(id+"F450.wireOp",EDGE,"E225.bottom")}),1.0]])]});
            extrude(context, id + "F451", {"entities" : qUnion([Q0]), "operationType" : NewBodyOperationType.ADD, "oppositeDirection" : true, "depth" : 19.05 * mm});
        }
        {
            var Q0;
            Q0=makeQuery(id+"F451.boolean.opBoolean","MERGE",FACE,{"derivedFrom":[makeQuery(id+"F449.boolean.opBoolean","MERGE",FACE,{"derivedFrom":[makeQuery(id+"F447.boolean.opBoolean","MERGE",FACE,{"derivedFrom":[makeQuery(id+"F445.opExtrude","CAP_FACE",FACE,{"disambiguationData":[OSD([sQuery(id+"F444.wireOp",EDGE,"E222.bottom"),sQuery(id+"F444.wireOp",EDGE,"E222.top"),sQuery(id+"F444.wireOp",EDGE,"E222.left"),sQuery(id+"F444.wireOp",EDGE,"E222.right")])],"isStart":false}),makeQuery(id+"F447.opExtrude","SWEPT_FACE",FACE,{"disambiguationData":[OSD([sQuery(id+"F446.wireOp",EDGE,"E223.left")])]})]}),makeQuery(id+"F449.opExtrude","SWEPT_FACE",FACE,{"disambiguationData":[OSD([sQuery(id+"F448.wireOp",EDGE,"E224.left")])]})]}),makeQuery(id+"F451.opExtrude","SWEPT_FACE",FACE,{"disambiguationData":[OSD([sQuery(id+"F450.wireOp",EDGE,"E225.left")])]})]});
            var sketch = newSketch(context, id + "F452", { "sketchPlane" : qUnion([Q0])});
            skLineSegment(sketch, "E226.bottom", {"start": v(20.04, 19.05) * mm, "end": v(13.69, 19.05) * mm});
            skLineSegment(sketch, "E226.top", {"start": v(20.04, 12.7) * mm, "end": v(13.69, 12.7) * mm});
            skLineSegment(sketch, "E226.left", {"start": v(20.04, 19.05) * mm, "end": v(20.04, 12.7) * mm});
            skLineSegment(sketch, "E226.right", {"start": v(13.69, 19.05) * mm, "end": v(13.69, 12.7) * mm});
            skSolve(sketch);
        }
        {
            var Q0;
            Q0=makeQuery(id+"F452.imprint","IMPRINT",FACE,{"disambiguationData":[TD([[makeQuery(id+"F452.imprint","IMPRINT",EDGE,{"derivedFrom":sQuery(id+"F452.wireOp",EDGE,"E226.bottom")}),-1.0]])]});
            extrude(context, id + "F453", {"entities" : qUnion([Q0]), "operationType" : NewBodyOperationType.ADD, "oppositeDirection" : true, "depth" : 19.05 * mm});
        }
        {
            var Q0;
            Q0=makeQuery(id+"F453.boolean.opBoolean","MERGE",FACE,{"derivedFrom":[makeQuery(id+"F451.opExtrude","CAP_FACE",FACE,{"disambiguationData":[OSD([sQuery(id+"F450.wireOp",EDGE,"E225.bottom"),sQuery(id+"F450.wireOp",EDGE,"E225.top"),sQuery(id+"F450.wireOp",EDGE,"E225.left"),sQuery(id+"F450.wireOp",EDGE,"E225.right")])],"isStart":false}),makeQuery(id+"F453.opExtrude","SWEPT_FACE",FACE,{"disambiguationData":[OSD([sQuery(id+"F452.wireOp",EDGE,"E226.bottom")])]})]});
            var sketch = newSketch(context, id + "F454", { "sketchPlane" : qUnion([Q0])});
            skLineSegment(sketch, "E227.bottom", {"start": v(-26.6, -20.04) * mm, "end": v(-32.94, -20.04) * mm});
            skLineSegment(sketch, "E227.top", {"start": v(-26.6, -13.69) * mm, "end": v(-32.94, -13.69) * mm});
            skLineSegment(sketch, "E227.left", {"start": v(-26.6, -20.04) * mm, "end": v(-26.6, -13.69) * mm});
            skLineSegment(sketch, "E227.right", {"start": v(-32.94, -20.04) * mm, "end": v(-32.94, -13.69) * mm});
            skSolve(sketch);
        }
        {
            var Q0;
            Q0=makeQuery(id+"F454.imprint","IMPRINT",FACE,{"disambiguationData":[TD([[makeQuery(id+"F454.imprint","IMPRINT",EDGE,{"derivedFrom":sQuery(id+"F454.wireOp",EDGE,"E227.bottom")}),-1.0]])]});
            extrude(context, id + "F455", {"entities" : qUnion([Q0]), "operationType" : NewBodyOperationType.ADD, "oppositeDirection" : true, "depth" : 19.05 * mm});
        }
        {
            var Q0;
            Q0=makeQuery(id+"F455.boolean.opBoolean","MERGE",FACE,{"derivedFrom":[makeQuery(id+"F453.opExtrude","CAP_FACE",FACE,{"disambiguationData":[OSD([sQuery(id+"F452.wireOp",EDGE,"E226.bottom"),sQuery(id+"F452.wireOp",EDGE,"E226.top"),sQuery(id+"F452.wireOp",EDGE,"E226.left"),sQuery(id+"F452.wireOp",EDGE,"E226.right")])],"isStart":false}),makeQuery(id+"F455.opExtrude","SWEPT_FACE",FACE,{"disambiguationData":[OSD([sQuery(id+"F454.wireOp",EDGE,"E227.left")])]})]});
            var sketch = newSketch(context, id + "F456", { "sketchPlane" : qUnion([Q0])});
            skLineSegment(sketch, "E228.bottom", {"start": v(-13.69, 0) * mm, "end": v(-20.04, 0) * mm});
            skLineSegment(sketch, "E228.top", {"start": v(-13.69, 6.35) * mm, "end": v(-20.04, 6.35) * mm});
            skLineSegment(sketch, "E228.left", {"start": v(-13.69, 0) * mm, "end": v(-13.69, 6.35) * mm});
            skLineSegment(sketch, "E228.right", {"start": v(-20.04, 0) * mm, "end": v(-20.04, 6.35) * mm});
            skSolve(sketch);
        }
        {
            var Q0;
            Q0=makeQuery(id+"F456.imprint","IMPRINT",FACE,{"disambiguationData":[TD([[makeQuery(id+"F456.imprint","IMPRINT",EDGE,{"derivedFrom":sQuery(id+"F456.wireOp",EDGE,"E228.bottom")}),-1.0]])]});
            extrude(context, id + "F457", {"entities" : qUnion([Q0]), "operationType" : NewBodyOperationType.ADD, "depth" : 3.17 * mm});
        }
        {
            var Q0;
            Q0=makeQuery(id+"F457.opExtrude","CAP_FACE",FACE,{"disambiguationData":[OSD([sQuery(id+"F456.wireOp",EDGE,"E228.bottom"),sQuery(id+"F456.wireOp",EDGE,"E228.top"),sQuery(id+"F456.wireOp",EDGE,"E228.left"),sQuery(id+"F456.wireOp",EDGE,"E228.right")])],"isStart":false});
            var sketch = newSketch(context, id + "F458", { "sketchPlane" : qUnion([Q0])});
            skLineSegment(sketch, "E229", {"start": v(-13.69, 0) * mm, "end": v(24.41, 0) * mm});
            skLineSegment(sketch, "E230", {"start": v(-20.04, 0) * mm, "end": v(-70.84, 0) * mm});
            skLineSegment(sketch, "E231", {"start": v(-70.84, 0) * mm, "end": v(-70.84, 95.25) * mm});
            skLineSegment(sketch, "E232.bottom", {"start": v(-70.84, 95.25) * mm, "end": v(24.41, 95.25) * mm});
            skLineSegment(sketch, "E232.top", {"start": v(-70.84, 0) * mm, "end": v(24.41, 0) * mm});
            skLineSegment(sketch, "E232.left", {"start": v(-70.84, 95.25) * mm, "end": v(-70.84, 0) * mm});
            skLineSegment(sketch, "E232.right", {"start": v(24.41, 95.25) * mm, "end": v(24.41, 0) * mm});
            skSolve(sketch);
        }
        {
            var Q0;
            Q0=makeQuery(id+"F1.opExtrude","SWEPT_BODY",BODY,{"disambiguationData":[OSD([sQuery(id+"F0.wireOp",EDGE,"E0.bottom"),sQuery(id+"F0.wireOp",EDGE,"E0.top"),sQuery(id+"F0.wireOp",EDGE,"E0.left"),sQuery(id+"F0.wireOp",EDGE,"E0.right")])]});
            var Q1;
            Q1=makeQuery(id+"F458.imprint","IMPRINT",FACE,{"disambiguationData":[TD([[makeQuery(id+"F458.imprint","IMPRINT",EDGE,{"derivedFrom":sQuery(id+"F458.wireOp",EDGE,"E232.bottom")}),-1.0]])]});
            mirror(context, id + "F459", {"operationType" : NewBodyOperationType.ADD, "entities" : qUnion([Q0]), "mirrorPlane" : qUnion([Q1])});
        }
    });
